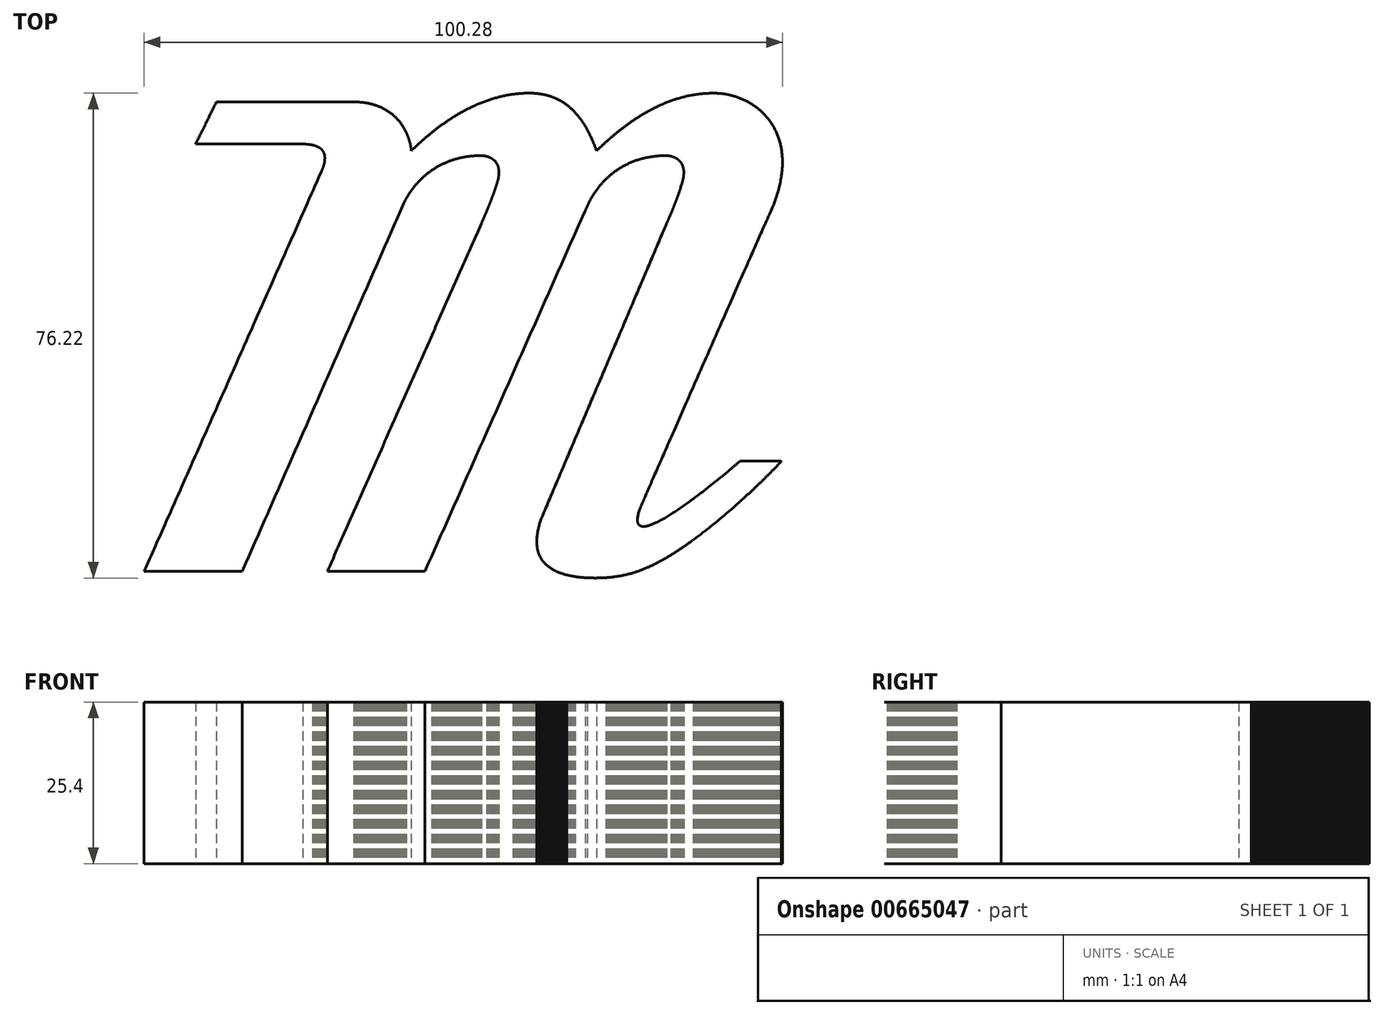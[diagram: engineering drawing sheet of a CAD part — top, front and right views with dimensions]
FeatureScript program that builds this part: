
annotation { "Feature Type Name" : "Feature", "Feature Type Description" : "" }
export const myFeature = defineFeature(function(context is Context, id is Id, definition is map)
    precondition{}
    {
        {
            var Q0;
            Q0=qCreatedBy(makeId("Top.planeOp"),FACE);
            var sketch = newSketch(context, id + "F0", { "sketchPlane" : qUnion([Q0])});
            skLineSegment(sketch, "E0", {"start": v(28.08, -26.44) * mm, "end": v(28.1, -26.39) * mm});
            skLineSegment(sketch, "E1", {"start": v(28.1, -26.39) * mm, "end": v(28.13, -26.32) * mm});
            skLineSegment(sketch, "E2", {"start": v(28.13, -26.32) * mm, "end": v(28.16, -26.25) * mm});
            skLineSegment(sketch, "E3", {"start": v(28.16, -26.25) * mm, "end": v(28.2, -26.16) * mm});
            skLineSegment(sketch, "E4", {"start": v(28.2, -26.16) * mm, "end": v(28.24, -26.05) * mm});
            skLineSegment(sketch, "E5", {"start": v(28.24, -26.05) * mm, "end": v(28.3, -25.94) * mm});
            skLineSegment(sketch, "E6", {"start": v(28.3, -25.94) * mm, "end": v(28.35, -25.81) * mm});
            skLineSegment(sketch, "E7", {"start": v(28.35, -25.81) * mm, "end": v(28.4, -25.68) * mm});
            skLineSegment(sketch, "E8", {"start": v(28.4, -25.68) * mm, "end": v(28.47, -25.53) * mm});
            skLineSegment(sketch, "E9", {"start": v(28.47, -25.53) * mm, "end": v(28.54, -25.37) * mm});
            skLineSegment(sketch, "E10", {"start": v(28.54, -25.37) * mm, "end": v(28.62, -25.2) * mm});
            skLineSegment(sketch, "E11", {"start": v(28.62, -25.2) * mm, "end": v(28.7, -25.02) * mm});
            skLineSegment(sketch, "E12", {"start": v(28.7, -25.02) * mm, "end": v(28.78, -24.82) * mm});
            skLineSegment(sketch, "E13", {"start": v(28.78, -24.82) * mm, "end": v(28.87, -24.62) * mm});
            skLineSegment(sketch, "E14", {"start": v(28.87, -24.62) * mm, "end": v(28.96, -24.4) * mm});
            skLineSegment(sketch, "E15", {"start": v(28.96, -24.4) * mm, "end": v(29.06, -24.19) * mm});
            skLineSegment(sketch, "E16", {"start": v(29.06, -24.19) * mm, "end": v(29.16, -23.95) * mm});
            skLineSegment(sketch, "E17", {"start": v(29.16, -23.95) * mm, "end": v(29.27, -23.71) * mm});
            skLineSegment(sketch, "E18", {"start": v(29.27, -23.71) * mm, "end": v(29.38, -23.46) * mm});
            skLineSegment(sketch, "E19", {"start": v(29.38, -23.46) * mm, "end": v(29.5, -23.2) * mm});
            skLineSegment(sketch, "E20", {"start": v(29.5, -23.2) * mm, "end": v(29.61, -22.93) * mm});
            skLineSegment(sketch, "E21", {"start": v(29.61, -22.93) * mm, "end": v(29.73, -22.65) * mm});
            skLineSegment(sketch, "E22", {"start": v(29.73, -22.65) * mm, "end": v(29.86, -22.36) * mm});
            skLineSegment(sketch, "E23", {"start": v(29.86, -22.36) * mm, "end": v(29.99, -22.07) * mm});
            skLineSegment(sketch, "E24", {"start": v(29.99, -22.07) * mm, "end": v(30.12, -21.76) * mm});
            skLineSegment(sketch, "E25", {"start": v(30.12, -21.76) * mm, "end": v(30.26, -21.45) * mm});
            skLineSegment(sketch, "E26", {"start": v(30.26, -21.45) * mm, "end": v(30.4, -21.13) * mm});
            skLineSegment(sketch, "E27", {"start": v(30.4, -21.13) * mm, "end": v(30.54, -20.8) * mm});
            skLineSegment(sketch, "E28", {"start": v(30.54, -20.8) * mm, "end": v(30.69, -20.47) * mm});
            skLineSegment(sketch, "E29", {"start": v(30.69, -20.47) * mm, "end": v(30.84, -20.12) * mm});
            skLineSegment(sketch, "E30", {"start": v(30.84, -20.12) * mm, "end": v(31, -19.77) * mm});
            skLineSegment(sketch, "E31", {"start": v(31, -19.77) * mm, "end": v(31.15, -19.42) * mm});
            skLineSegment(sketch, "E32", {"start": v(31.15, -19.42) * mm, "end": v(31.31, -19.05) * mm});
            skLineSegment(sketch, "E33", {"start": v(31.31, -19.05) * mm, "end": v(31.47, -18.68) * mm});
            skLineSegment(sketch, "E34", {"start": v(31.47, -18.68) * mm, "end": v(31.64, -18.3) * mm});
            skLineSegment(sketch, "E35", {"start": v(31.64, -18.3) * mm, "end": v(31.8, -17.92) * mm});
            skLineSegment(sketch, "E36", {"start": v(31.8, -17.92) * mm, "end": v(31.98, -17.53) * mm});
            skLineSegment(sketch, "E37", {"start": v(31.98, -17.53) * mm, "end": v(32.15, -17.13) * mm});
            skLineSegment(sketch, "E38", {"start": v(32.15, -17.13) * mm, "end": v(32.33, -16.73) * mm});
            skLineSegment(sketch, "E39", {"start": v(32.33, -16.73) * mm, "end": v(32.5, -16.33) * mm});
            skLineSegment(sketch, "E40", {"start": v(32.5, -16.33) * mm, "end": v(32.69, -15.91) * mm});
            skLineSegment(sketch, "E41", {"start": v(32.69, -15.91) * mm, "end": v(32.87, -15.5) * mm});
            skLineSegment(sketch, "E42", {"start": v(32.87, -15.5) * mm, "end": v(33.06, -15.07) * mm});
            skLineSegment(sketch, "E43", {"start": v(33.06, -15.07) * mm, "end": v(33.24, -14.65) * mm});
            skLineSegment(sketch, "E44", {"start": v(33.24, -14.65) * mm, "end": v(33.43, -14.21) * mm});
            skLineSegment(sketch, "E45", {"start": v(33.43, -14.21) * mm, "end": v(33.62, -13.78) * mm});
            skLineSegment(sketch, "E46", {"start": v(33.62, -13.78) * mm, "end": v(33.82, -13.34) * mm});
            skLineSegment(sketch, "E47", {"start": v(33.82, -13.34) * mm, "end": v(34.01, -12.9) * mm});
            skLineSegment(sketch, "E48", {"start": v(34.01, -12.9) * mm, "end": v(34.2, -12.44) * mm});
            skLineSegment(sketch, "E49", {"start": v(34.2, -12.44) * mm, "end": v(34.4, -12) * mm});
            skLineSegment(sketch, "E50", {"start": v(34.4, -12) * mm, "end": v(34.6, -11.54) * mm});
            skLineSegment(sketch, "E51", {"start": v(34.6, -11.54) * mm, "end": v(34.8, -11.08) * mm});
            skLineSegment(sketch, "E52", {"start": v(34.8, -11.08) * mm, "end": v(35.01, -10.62) * mm});
            skLineSegment(sketch, "E53", {"start": v(35.01, -10.62) * mm, "end": v(35.22, -10.15) * mm});
            skLineSegment(sketch, "E54", {"start": v(35.22, -10.15) * mm, "end": v(35.42, -9.68) * mm});
            skLineSegment(sketch, "E55", {"start": v(35.42, -9.68) * mm, "end": v(35.63, -9.21) * mm});
            skLineSegment(sketch, "E56", {"start": v(35.63, -9.21) * mm, "end": v(35.84, -8.74) * mm});
            skLineSegment(sketch, "E57", {"start": v(35.84, -8.74) * mm, "end": v(36.04, -8.27) * mm});
            skLineSegment(sketch, "E58", {"start": v(36.04, -8.27) * mm, "end": v(36.25, -7.79) * mm});
            skLineSegment(sketch, "E59", {"start": v(36.25, -7.79) * mm, "end": v(36.46, -7.31) * mm});
            skLineSegment(sketch, "E60", {"start": v(36.46, -7.31) * mm, "end": v(36.68, -6.83) * mm});
            skLineSegment(sketch, "E61", {"start": v(36.68, -6.83) * mm, "end": v(36.89, -6.35) * mm});
            skLineSegment(sketch, "E62", {"start": v(36.89, -6.35) * mm, "end": v(37.1, -5.87) * mm});
            skLineSegment(sketch, "E63", {"start": v(37.1, -5.87) * mm, "end": v(37.31, -5.38) * mm});
            skLineSegment(sketch, "E64", {"start": v(37.31, -5.38) * mm, "end": v(37.53, -4.9) * mm});
            skLineSegment(sketch, "E65", {"start": v(37.53, -4.9) * mm, "end": v(37.74, -4.41) * mm});
            skLineSegment(sketch, "E66", {"start": v(37.74, -4.41) * mm, "end": v(37.95, -3.93) * mm});
            skLineSegment(sketch, "E67", {"start": v(37.95, -3.93) * mm, "end": v(38.17, -3.44) * mm});
            skLineSegment(sketch, "E68", {"start": v(38.17, -3.44) * mm, "end": v(38.38, -2.95) * mm});
            skLineSegment(sketch, "E69", {"start": v(38.38, -2.95) * mm, "end": v(38.6, -2.47) * mm});
            skLineSegment(sketch, "E70", {"start": v(38.6, -2.47) * mm, "end": v(38.8, -1.98) * mm});
            skLineSegment(sketch, "E71", {"start": v(38.8, -1.98) * mm, "end": v(39.02, -1.5) * mm});
            skLineSegment(sketch, "E72", {"start": v(39.02, -1.5) * mm, "end": v(39.23, -1) * mm});
            skLineSegment(sketch, "E73", {"start": v(39.23, -1) * mm, "end": v(39.45, -0.52) * mm});
            skLineSegment(sketch, "E74", {"start": v(39.45, -0.52) * mm, "end": v(39.66, -0.04) * mm});
            skLineSegment(sketch, "E75", {"start": v(39.66, -0.04) * mm, "end": v(39.87, 0.44) * mm});
            skLineSegment(sketch, "E76", {"start": v(39.87, 0.44) * mm, "end": v(40.08, 0.92) * mm});
            skLineSegment(sketch, "E77", {"start": v(40.08, 0.92) * mm, "end": v(40.3, 1.4) * mm});
            skLineSegment(sketch, "E78", {"start": v(40.3, 1.4) * mm, "end": v(40.5, 1.88) * mm});
            skLineSegment(sketch, "E79", {"start": v(40.5, 1.88) * mm, "end": v(40.71, 2.35) * mm});
            skLineSegment(sketch, "E80", {"start": v(40.71, 2.35) * mm, "end": v(40.92, 2.83) * mm});
            skLineSegment(sketch, "E81", {"start": v(40.92, 2.83) * mm, "end": v(41.13, 3.3) * mm});
            skLineSegment(sketch, "E82", {"start": v(41.13, 3.3) * mm, "end": v(41.34, 3.77) * mm});
            skLineSegment(sketch, "E83", {"start": v(41.34, 3.77) * mm, "end": v(41.54, 4.23) * mm});
            skLineSegment(sketch, "E84", {"start": v(41.54, 4.23) * mm, "end": v(41.75, 4.7) * mm});
            skLineSegment(sketch, "E85", {"start": v(41.75, 4.7) * mm, "end": v(41.95, 5.16) * mm});
            skLineSegment(sketch, "E86", {"start": v(41.95, 5.16) * mm, "end": v(42.15, 5.61) * mm});
            skLineSegment(sketch, "E87", {"start": v(42.15, 5.61) * mm, "end": v(42.35, 6.07) * mm});
            skLineSegment(sketch, "E88", {"start": v(42.35, 6.07) * mm, "end": v(42.55, 6.52) * mm});
            skLineSegment(sketch, "E89", {"start": v(42.55, 6.52) * mm, "end": v(42.74, 6.96) * mm});
            skLineSegment(sketch, "E90", {"start": v(42.74, 6.96) * mm, "end": v(42.94, 7.4) * mm});
            skLineSegment(sketch, "E91", {"start": v(42.94, 7.4) * mm, "end": v(43.13, 7.84) * mm});
            skLineSegment(sketch, "E92", {"start": v(43.13, 7.84) * mm, "end": v(43.32, 8.28) * mm});
            skLineSegment(sketch, "E93", {"start": v(43.32, 8.28) * mm, "end": v(43.51, 8.7) * mm});
            skLineSegment(sketch, "E94", {"start": v(43.51, 8.7) * mm, "end": v(43.7, 9.13) * mm});
            skLineSegment(sketch, "E95", {"start": v(43.7, 9.13) * mm, "end": v(43.89, 9.55) * mm});
            skLineSegment(sketch, "E96", {"start": v(43.89, 9.55) * mm, "end": v(44.07, 9.96) * mm});
            skLineSegment(sketch, "E97", {"start": v(44.07, 9.96) * mm, "end": v(44.25, 10.37) * mm});
            skLineSegment(sketch, "E98", {"start": v(44.25, 10.37) * mm, "end": v(44.43, 10.77) * mm});
            skLineSegment(sketch, "E99", {"start": v(44.43, 10.77) * mm, "end": v(44.6, 11.17) * mm});
            skLineSegment(sketch, "E100", {"start": v(44.6, 11.17) * mm, "end": v(44.78, 11.56) * mm});
            skLineSegment(sketch, "E101", {"start": v(44.78, 11.56) * mm, "end": v(44.95, 11.95) * mm});
            skLineSegment(sketch, "E102", {"start": v(44.95, 11.95) * mm, "end": v(45.11, 12.33) * mm});
            skLineSegment(sketch, "E103", {"start": v(45.11, 12.33) * mm, "end": v(45.28, 12.7) * mm});
            skLineSegment(sketch, "E104", {"start": v(45.28, 12.7) * mm, "end": v(45.44, 13.07) * mm});
            skLineSegment(sketch, "E105", {"start": v(45.44, 13.07) * mm, "end": v(45.6, 13.43) * mm});
            skLineSegment(sketch, "E106", {"start": v(45.6, 13.43) * mm, "end": v(45.76, 13.78) * mm});
            skLineSegment(sketch, "E107", {"start": v(45.76, 13.78) * mm, "end": v(45.91, 14.13) * mm});
            skLineSegment(sketch, "E108", {"start": v(45.91, 14.13) * mm, "end": v(46.06, 14.47) * mm});
            skLineSegment(sketch, "E109", {"start": v(46.06, 14.47) * mm, "end": v(46.2, 14.8) * mm});
            skLineSegment(sketch, "E110", {"start": v(46.2, 14.8) * mm, "end": v(46.35, 15.12) * mm});
            skLineSegment(sketch, "E111", {"start": v(46.35, 15.12) * mm, "end": v(46.5, 15.44) * mm});
            skLineSegment(sketch, "E112", {"start": v(46.5, 15.44) * mm, "end": v(46.63, 15.74) * mm});
            skLineSegment(sketch, "E113", {"start": v(46.63, 15.74) * mm, "end": v(46.76, 16.04) * mm});
            skLineSegment(sketch, "E114", {"start": v(46.76, 16.04) * mm, "end": v(46.89, 16.33) * mm});
            skLineSegment(sketch, "E115", {"start": v(46.89, 16.33) * mm, "end": v(47.01, 16.62) * mm});
            skLineSegment(sketch, "E116", {"start": v(47.01, 16.62) * mm, "end": v(47.14, 16.89) * mm});
            skLineSegment(sketch, "E117", {"start": v(47.14, 16.89) * mm, "end": v(47.25, 17.15) * mm});
            skLineSegment(sketch, "E118", {"start": v(47.25, 17.15) * mm, "end": v(47.37, 17.4) * mm});
            skLineSegment(sketch, "E119", {"start": v(47.37, 17.4) * mm, "end": v(47.48, 17.65) * mm});
            skLineSegment(sketch, "E120", {"start": v(47.48, 17.65) * mm, "end": v(47.58, 17.89) * mm});
            skLineSegment(sketch, "E121", {"start": v(47.58, 17.89) * mm, "end": v(47.68, 18.12) * mm});
            skLineSegment(sketch, "E122", {"start": v(47.68, 18.12) * mm, "end": v(47.78, 18.33) * mm});
            skLineSegment(sketch, "E123", {"start": v(47.78, 18.33) * mm, "end": v(47.87, 18.54) * mm});
            skLineSegment(sketch, "E124", {"start": v(47.87, 18.54) * mm, "end": v(47.96, 18.73) * mm});
            skLineSegment(sketch, "E125", {"start": v(47.96, 18.73) * mm, "end": v(48.04, 18.92) * mm});
            skLineSegment(sketch, "E126", {"start": v(48.04, 18.92) * mm, "end": v(48.12, 19.1) * mm});
            skLineSegment(sketch, "E127", {"start": v(48.12, 19.1) * mm, "end": v(48.2, 19.26) * mm});
            skLineSegment(sketch, "E128", {"start": v(48.2, 19.26) * mm, "end": v(48.33, 19.55) * mm});
            skLineSegment(sketch, "E129", {"start": v(48.33, 19.55) * mm, "end": v(48.45, 19.84) * mm});
            skLineSegment(sketch, "E130", {"start": v(48.45, 19.84) * mm, "end": v(48.57, 20.12) * mm});
            skLineSegment(sketch, "E131", {"start": v(48.57, 20.12) * mm, "end": v(48.68, 20.4) * mm});
            skLineSegment(sketch, "E132", {"start": v(48.68, 20.4) * mm, "end": v(48.8, 20.69) * mm});
            skLineSegment(sketch, "E133", {"start": v(48.8, 20.69) * mm, "end": v(48.9, 20.97) * mm});
            skLineSegment(sketch, "E134", {"start": v(48.9, 20.97) * mm, "end": v(49, 21.24) * mm});
            skLineSegment(sketch, "E135", {"start": v(49, 21.24) * mm, "end": v(49.1, 21.52) * mm});
            skLineSegment(sketch, "E136", {"start": v(49.1, 21.52) * mm, "end": v(49.2, 21.8) * mm});
            skLineSegment(sketch, "E137", {"start": v(49.2, 21.8) * mm, "end": v(49.28, 22.06) * mm});
            skLineSegment(sketch, "E138", {"start": v(49.28, 22.06) * mm, "end": v(49.36, 22.33) * mm});
            skLineSegment(sketch, "E139", {"start": v(49.36, 22.33) * mm, "end": v(49.44, 22.6) * mm});
            skLineSegment(sketch, "E140", {"start": v(49.44, 22.6) * mm, "end": v(49.51, 22.86) * mm});
            skLineSegment(sketch, "E141", {"start": v(49.51, 22.86) * mm, "end": v(49.58, 23.12) * mm});
            skLineSegment(sketch, "E142", {"start": v(49.58, 23.12) * mm, "end": v(49.65, 23.38) * mm});
            skLineSegment(sketch, "E143", {"start": v(49.65, 23.38) * mm, "end": v(49.7, 23.64) * mm});
            skLineSegment(sketch, "E144", {"start": v(49.7, 23.64) * mm, "end": v(49.77, 23.9) * mm});
            skLineSegment(sketch, "E145", {"start": v(49.77, 23.9) * mm, "end": v(49.82, 24.15) * mm});
            skLineSegment(sketch, "E146", {"start": v(49.82, 24.15) * mm, "end": v(49.87, 24.4) * mm});
            skLineSegment(sketch, "E147", {"start": v(49.87, 24.4) * mm, "end": v(49.91, 24.65) * mm});
            skLineSegment(sketch, "E148", {"start": v(49.91, 24.65) * mm, "end": v(49.95, 24.9) * mm});
            skLineSegment(sketch, "E149", {"start": v(49.95, 24.9) * mm, "end": v(49.99, 25.14) * mm});
            skLineSegment(sketch, "E150", {"start": v(49.99, 25.14) * mm, "end": v(50.02, 25.38) * mm});
            skLineSegment(sketch, "E151", {"start": v(50.02, 25.38) * mm, "end": v(50.05, 25.62) * mm});
            skLineSegment(sketch, "E152", {"start": v(50.05, 25.62) * mm, "end": v(50.08, 25.86) * mm});
            skLineSegment(sketch, "E153", {"start": v(50.08, 25.86) * mm, "end": v(50.1, 26.1) * mm});
            skLineSegment(sketch, "E154", {"start": v(50.1, 26.1) * mm, "end": v(50.11, 26.32) * mm});
            skLineSegment(sketch, "E155", {"start": v(50.11, 26.32) * mm, "end": v(50.13, 26.55) * mm});
            skLineSegment(sketch, "E156", {"start": v(50.13, 26.55) * mm, "end": v(50.14, 26.78) * mm});
            skLineSegment(sketch, "E157", {"start": v(50.14, 26.78) * mm, "end": v(50.14, 27) * mm});
            skLineSegment(sketch, "E158", {"start": v(50.14, 27) * mm, "end": v(50.14, 27.23) * mm});
            skLineSegment(sketch, "E159", {"start": v(50.14, 27.23) * mm, "end": v(50.14, 27.45) * mm});
            skLineSegment(sketch, "E160", {"start": v(50.14, 27.45) * mm, "end": v(50.14, 27.67) * mm});
            skLineSegment(sketch, "E161", {"start": v(50.14, 27.67) * mm, "end": v(50.13, 27.9) * mm});
            skLineSegment(sketch, "E162", {"start": v(50.13, 27.9) * mm, "end": v(50.12, 28.1) * mm});
            skLineSegment(sketch, "E163", {"start": v(50.12, 28.1) * mm, "end": v(50.1, 28.32) * mm});
            skLineSegment(sketch, "E164", {"start": v(50.1, 28.32) * mm, "end": v(50.08, 28.53) * mm});
            skLineSegment(sketch, "E165", {"start": v(50.08, 28.53) * mm, "end": v(50.06, 28.74) * mm});
            skLineSegment(sketch, "E166", {"start": v(50.06, 28.74) * mm, "end": v(50.03, 28.94) * mm});
            skLineSegment(sketch, "E167", {"start": v(50.03, 28.94) * mm, "end": v(50, 29.15) * mm});
            skLineSegment(sketch, "E168", {"start": v(50, 29.15) * mm, "end": v(49.97, 29.35) * mm});
            skLineSegment(sketch, "E169", {"start": v(49.97, 29.35) * mm, "end": v(49.94, 29.55) * mm});
            skLineSegment(sketch, "E170", {"start": v(49.94, 29.55) * mm, "end": v(49.9, 29.74) * mm});
            skLineSegment(sketch, "E171", {"start": v(49.9, 29.74) * mm, "end": v(49.86, 29.94) * mm});
            skLineSegment(sketch, "E172", {"start": v(49.86, 29.94) * mm, "end": v(49.81, 30.13) * mm});
            skLineSegment(sketch, "E173", {"start": v(49.81, 30.13) * mm, "end": v(49.76, 30.32) * mm});
            skLineSegment(sketch, "E174", {"start": v(49.76, 30.32) * mm, "end": v(49.71, 30.5) * mm});
            skLineSegment(sketch, "E175", {"start": v(49.71, 30.5) * mm, "end": v(49.66, 30.7) * mm});
            skLineSegment(sketch, "E176", {"start": v(49.66, 30.7) * mm, "end": v(49.6, 30.88) * mm});
            skLineSegment(sketch, "E177", {"start": v(49.6, 30.88) * mm, "end": v(49.54, 31.06) * mm});
            skLineSegment(sketch, "E178", {"start": v(49.54, 31.06) * mm, "end": v(49.48, 31.23) * mm});
            skLineSegment(sketch, "E179", {"start": v(49.48, 31.23) * mm, "end": v(49.41, 31.41) * mm});
            skLineSegment(sketch, "E180", {"start": v(49.41, 31.41) * mm, "end": v(49.35, 31.59) * mm});
            skLineSegment(sketch, "E181", {"start": v(49.35, 31.59) * mm, "end": v(49.27, 31.76) * mm});
            skLineSegment(sketch, "E182", {"start": v(49.27, 31.76) * mm, "end": v(49.2, 31.93) * mm});
            skLineSegment(sketch, "E183", {"start": v(49.2, 31.93) * mm, "end": v(49.12, 32.1) * mm});
            skLineSegment(sketch, "E184", {"start": v(49.12, 32.1) * mm, "end": v(49.05, 32.26) * mm});
            skLineSegment(sketch, "E185", {"start": v(49.05, 32.26) * mm, "end": v(48.96, 32.42) * mm});
            skLineSegment(sketch, "E186", {"start": v(48.96, 32.42) * mm, "end": v(48.88, 32.58) * mm});
            skLineSegment(sketch, "E187", {"start": v(48.88, 32.58) * mm, "end": v(48.8, 32.74) * mm});
            skLineSegment(sketch, "E188", {"start": v(48.8, 32.74) * mm, "end": v(48.7, 32.9) * mm});
            skLineSegment(sketch, "E189", {"start": v(48.7, 32.9) * mm, "end": v(48.61, 33.05) * mm});
            skLineSegment(sketch, "E190", {"start": v(48.61, 33.05) * mm, "end": v(48.52, 33.2) * mm});
            skLineSegment(sketch, "E191", {"start": v(48.52, 33.2) * mm, "end": v(48.42, 33.35) * mm});
            skLineSegment(sketch, "E192", {"start": v(48.42, 33.35) * mm, "end": v(48.33, 33.5) * mm});
            skLineSegment(sketch, "E193", {"start": v(48.33, 33.5) * mm, "end": v(48.23, 33.64) * mm});
            skLineSegment(sketch, "E194", {"start": v(48.23, 33.64) * mm, "end": v(48.12, 33.78) * mm});
            skLineSegment(sketch, "E195", {"start": v(48.12, 33.78) * mm, "end": v(48.02, 33.92) * mm});
            skLineSegment(sketch, "E196", {"start": v(48.02, 33.92) * mm, "end": v(47.91, 34.06) * mm});
            skLineSegment(sketch, "E197", {"start": v(47.91, 34.06) * mm, "end": v(47.8, 34.2) * mm});
            skLineSegment(sketch, "E198", {"start": v(47.8, 34.2) * mm, "end": v(47.7, 34.33) * mm});
            skLineSegment(sketch, "E199", {"start": v(47.7, 34.33) * mm, "end": v(47.58, 34.46) * mm});
            skLineSegment(sketch, "E200", {"start": v(47.58, 34.46) * mm, "end": v(47.46, 34.6) * mm});
            skLineSegment(sketch, "E201", {"start": v(47.46, 34.6) * mm, "end": v(47.35, 34.72) * mm});
            skLineSegment(sketch, "E202", {"start": v(47.35, 34.72) * mm, "end": v(47.23, 34.84) * mm});
            skLineSegment(sketch, "E203", {"start": v(47.23, 34.84) * mm, "end": v(47.1, 34.96) * mm});
            skLineSegment(sketch, "E204", {"start": v(47.1, 34.96) * mm, "end": v(46.98, 35.08) * mm});
            skLineSegment(sketch, "E205", {"start": v(46.98, 35.08) * mm, "end": v(46.86, 35.2) * mm});
            skLineSegment(sketch, "E206", {"start": v(46.86, 35.2) * mm, "end": v(46.73, 35.31) * mm});
            skLineSegment(sketch, "E207", {"start": v(46.73, 35.31) * mm, "end": v(46.6, 35.43) * mm});
            skLineSegment(sketch, "E208", {"start": v(46.6, 35.43) * mm, "end": v(46.48, 35.54) * mm});
            skLineSegment(sketch, "E209", {"start": v(46.48, 35.54) * mm, "end": v(46.35, 35.64) * mm});
            skLineSegment(sketch, "E210", {"start": v(46.35, 35.64) * mm, "end": v(46.21, 35.75) * mm});
            skLineSegment(sketch, "E211", {"start": v(46.21, 35.75) * mm, "end": v(46.08, 35.85) * mm});
            skLineSegment(sketch, "E212", {"start": v(46.08, 35.85) * mm, "end": v(45.95, 35.95) * mm});
            skLineSegment(sketch, "E213", {"start": v(45.95, 35.95) * mm, "end": v(45.8, 36.05) * mm});
            skLineSegment(sketch, "E214", {"start": v(45.8, 36.05) * mm, "end": v(45.67, 36.15) * mm});
            skLineSegment(sketch, "E215", {"start": v(45.67, 36.15) * mm, "end": v(45.53, 36.24) * mm});
            skLineSegment(sketch, "E216", {"start": v(45.53, 36.24) * mm, "end": v(45.4, 36.34) * mm});
            skLineSegment(sketch, "E217", {"start": v(45.4, 36.34) * mm, "end": v(45.25, 36.43) * mm});
            skLineSegment(sketch, "E218", {"start": v(45.25, 36.43) * mm, "end": v(45.1, 36.51) * mm});
            skLineSegment(sketch, "E219", {"start": v(45.1, 36.51) * mm, "end": v(44.96, 36.6) * mm});
            skLineSegment(sketch, "E220", {"start": v(44.96, 36.6) * mm, "end": v(44.82, 36.68) * mm});
            skLineSegment(sketch, "E221", {"start": v(44.82, 36.68) * mm, "end": v(44.67, 36.76) * mm});
            skLineSegment(sketch, "E222", {"start": v(44.67, 36.76) * mm, "end": v(44.52, 36.84) * mm});
            skLineSegment(sketch, "E223", {"start": v(44.52, 36.84) * mm, "end": v(44.37, 36.91) * mm});
            skLineSegment(sketch, "E224", {"start": v(44.37, 36.91) * mm, "end": v(44.22, 36.99) * mm});
            skLineSegment(sketch, "E225", {"start": v(44.22, 36.99) * mm, "end": v(44.07, 37.06) * mm});
            skLineSegment(sketch, "E226", {"start": v(44.07, 37.06) * mm, "end": v(43.92, 37.13) * mm});
            skLineSegment(sketch, "E227", {"start": v(43.92, 37.13) * mm, "end": v(43.77, 37.2) * mm});
            skLineSegment(sketch, "E228", {"start": v(43.77, 37.2) * mm, "end": v(43.62, 37.26) * mm});
            skLineSegment(sketch, "E229", {"start": v(43.62, 37.26) * mm, "end": v(43.46, 37.32) * mm});
            skLineSegment(sketch, "E230", {"start": v(43.46, 37.32) * mm, "end": v(43.3, 37.38) * mm});
            skLineSegment(sketch, "E231", {"start": v(43.3, 37.38) * mm, "end": v(43.15, 37.44) * mm});
            skLineSegment(sketch, "E232", {"start": v(43.15, 37.44) * mm, "end": v(43, 37.5) * mm});
            skLineSegment(sketch, "E233", {"start": v(43, 37.5) * mm, "end": v(42.84, 37.54) * mm});
            skLineSegment(sketch, "E234", {"start": v(42.84, 37.54) * mm, "end": v(42.68, 37.6) * mm});
            skLineSegment(sketch, "E235", {"start": v(42.68, 37.6) * mm, "end": v(42.52, 37.64) * mm});
            skLineSegment(sketch, "E236", {"start": v(42.52, 37.64) * mm, "end": v(42.37, 37.69) * mm});
            skLineSegment(sketch, "E237", {"start": v(42.37, 37.69) * mm, "end": v(42.2, 37.73) * mm});
            skLineSegment(sketch, "E238", {"start": v(42.2, 37.73) * mm, "end": v(42.05, 37.77) * mm});
            skLineSegment(sketch, "E239", {"start": v(42.05, 37.77) * mm, "end": v(41.89, 37.8) * mm});
            skLineSegment(sketch, "E240", {"start": v(41.89, 37.8) * mm, "end": v(41.73, 37.85) * mm});
            skLineSegment(sketch, "E241", {"start": v(41.73, 37.85) * mm, "end": v(41.57, 37.88) * mm});
            skLineSegment(sketch, "E242", {"start": v(41.57, 37.88) * mm, "end": v(41.4, 37.91) * mm});
            skLineSegment(sketch, "E243", {"start": v(41.4, 37.91) * mm, "end": v(41.25, 37.94) * mm});
            skLineSegment(sketch, "E244", {"start": v(41.25, 37.94) * mm, "end": v(41.09, 37.97) * mm});
            skLineSegment(sketch, "E245", {"start": v(41.09, 37.97) * mm, "end": v(40.93, 38) * mm});
            skLineSegment(sketch, "E246", {"start": v(40.93, 38) * mm, "end": v(40.76, 38.01) * mm});
            skLineSegment(sketch, "E247", {"start": v(40.76, 38.01) * mm, "end": v(40.6, 38.03) * mm});
            skLineSegment(sketch, "E248", {"start": v(40.6, 38.03) * mm, "end": v(40.44, 38.05) * mm});
            skLineSegment(sketch, "E249", {"start": v(40.44, 38.05) * mm, "end": v(40.28, 38.07) * mm});
            skLineSegment(sketch, "E250", {"start": v(40.28, 38.07) * mm, "end": v(40.12, 38.08) * mm});
            skLineSegment(sketch, "E251", {"start": v(40.12, 38.08) * mm, "end": v(39.96, 38.1) * mm});
            skLineSegment(sketch, "E252", {"start": v(39.96, 38.1) * mm, "end": v(39.8, 38.1) * mm});
            skLineSegment(sketch, "E253", {"start": v(39.8, 38.1) * mm, "end": v(39.64, 38.1) * mm});
            skLineSegment(sketch, "E254", {"start": v(39.64, 38.1) * mm, "end": v(39.48, 38.1) * mm});
            skLineSegment(sketch, "E255", {"start": v(39.48, 38.1) * mm, "end": v(39.32, 38.1) * mm});
            skLineSegment(sketch, "E256", {"start": v(39.32, 38.1) * mm, "end": v(39.11, 38.1) * mm});
            skLineSegment(sketch, "E257", {"start": v(39.11, 38.1) * mm, "end": v(38.91, 38.1) * mm});
            skLineSegment(sketch, "E258", {"start": v(38.91, 38.1) * mm, "end": v(38.7, 38.1) * mm});
            skLineSegment(sketch, "E259", {"start": v(38.7, 38.1) * mm, "end": v(38.5, 38.1) * mm});
            skLineSegment(sketch, "E260", {"start": v(38.5, 38.1) * mm, "end": v(38.3, 38.08) * mm});
            skLineSegment(sketch, "E261", {"start": v(38.3, 38.08) * mm, "end": v(38.1, 38.07) * mm});
            skLineSegment(sketch, "E262", {"start": v(38.1, 38.07) * mm, "end": v(37.9, 38.05) * mm});
            skLineSegment(sketch, "E263", {"start": v(37.9, 38.05) * mm, "end": v(37.7, 38.04) * mm});
            skLineSegment(sketch, "E264", {"start": v(37.7, 38.04) * mm, "end": v(37.5, 38.02) * mm});
            skLineSegment(sketch, "E265", {"start": v(37.5, 38.02) * mm, "end": v(37.31, 38) * mm});
            skLineSegment(sketch, "E266", {"start": v(37.31, 38) * mm, "end": v(37.12, 37.98) * mm});
            skLineSegment(sketch, "E267", {"start": v(37.12, 37.98) * mm, "end": v(36.92, 37.95) * mm});
            skLineSegment(sketch, "E268", {"start": v(36.92, 37.95) * mm, "end": v(36.73, 37.93) * mm});
            skLineSegment(sketch, "E269", {"start": v(36.73, 37.93) * mm, "end": v(36.53, 37.9) * mm});
            skLineSegment(sketch, "E270", {"start": v(36.53, 37.9) * mm, "end": v(36.34, 37.87) * mm});
            skLineSegment(sketch, "E271", {"start": v(36.34, 37.87) * mm, "end": v(36.15, 37.84) * mm});
            skLineSegment(sketch, "E272", {"start": v(36.15, 37.84) * mm, "end": v(35.96, 37.8) * mm});
            skLineSegment(sketch, "E273", {"start": v(35.96, 37.8) * mm, "end": v(35.76, 37.77) * mm});
            skLineSegment(sketch, "E274", {"start": v(35.76, 37.77) * mm, "end": v(35.58, 37.73) * mm});
            skLineSegment(sketch, "E275", {"start": v(35.58, 37.73) * mm, "end": v(35.39, 37.69) * mm});
            skLineSegment(sketch, "E276", {"start": v(35.39, 37.69) * mm, "end": v(35.2, 37.65) * mm});
            skLineSegment(sketch, "E277", {"start": v(35.2, 37.65) * mm, "end": v(35.01, 37.6) * mm});
            skLineSegment(sketch, "E278", {"start": v(35.01, 37.6) * mm, "end": v(34.82, 37.56) * mm});
            skLineSegment(sketch, "E279", {"start": v(34.82, 37.56) * mm, "end": v(34.64, 37.52) * mm});
            skLineSegment(sketch, "E280", {"start": v(34.64, 37.52) * mm, "end": v(34.45, 37.47) * mm});
            skLineSegment(sketch, "E281", {"start": v(34.45, 37.47) * mm, "end": v(34.27, 37.42) * mm});
            skLineSegment(sketch, "E282", {"start": v(34.27, 37.42) * mm, "end": v(34.09, 37.37) * mm});
            skLineSegment(sketch, "E283", {"start": v(34.09, 37.37) * mm, "end": v(33.9, 37.32) * mm});
            skLineSegment(sketch, "E284", {"start": v(33.9, 37.32) * mm, "end": v(33.73, 37.26) * mm});
            skLineSegment(sketch, "E285", {"start": v(33.73, 37.26) * mm, "end": v(33.54, 37.2) * mm});
            skLineSegment(sketch, "E286", {"start": v(33.54, 37.2) * mm, "end": v(33.37, 37.15) * mm});
            skLineSegment(sketch, "E287", {"start": v(33.37, 37.15) * mm, "end": v(33.19, 37.1) * mm});
            skLineSegment(sketch, "E288", {"start": v(33.19, 37.1) * mm, "end": v(33, 37.03) * mm});
            skLineSegment(sketch, "E289", {"start": v(33, 37.03) * mm, "end": v(32.83, 36.97) * mm});
            skLineSegment(sketch, "E290", {"start": v(32.83, 36.97) * mm, "end": v(32.66, 36.9) * mm});
            skLineSegment(sketch, "E291", {"start": v(32.66, 36.9) * mm, "end": v(32.48, 36.84) * mm});
            skLineSegment(sketch, "E292", {"start": v(32.48, 36.84) * mm, "end": v(32.3, 36.78) * mm});
            skLineSegment(sketch, "E293", {"start": v(32.3, 36.78) * mm, "end": v(32.14, 36.71) * mm});
            skLineSegment(sketch, "E294", {"start": v(32.14, 36.71) * mm, "end": v(31.96, 36.65) * mm});
            skLineSegment(sketch, "E295", {"start": v(31.96, 36.65) * mm, "end": v(31.8, 36.58) * mm});
            skLineSegment(sketch, "E296", {"start": v(31.8, 36.58) * mm, "end": v(31.62, 36.5) * mm});
            skLineSegment(sketch, "E297", {"start": v(31.62, 36.5) * mm, "end": v(31.45, 36.44) * mm});
            skLineSegment(sketch, "E298", {"start": v(31.45, 36.44) * mm, "end": v(31.28, 36.36) * mm});
            skLineSegment(sketch, "E299", {"start": v(31.28, 36.36) * mm, "end": v(31.12, 36.3) * mm});
            skLineSegment(sketch, "E300", {"start": v(31.12, 36.3) * mm, "end": v(30.95, 36.22) * mm});
            skLineSegment(sketch, "E301", {"start": v(30.95, 36.22) * mm, "end": v(30.79, 36.14) * mm});
            skLineSegment(sketch, "E302", {"start": v(30.79, 36.14) * mm, "end": v(30.62, 36.07) * mm});
            skLineSegment(sketch, "E303", {"start": v(30.62, 36.07) * mm, "end": v(30.46, 35.99) * mm});
            skLineSegment(sketch, "E304", {"start": v(30.46, 35.99) * mm, "end": v(30.3, 35.91) * mm});
            skLineSegment(sketch, "E305", {"start": v(30.3, 35.91) * mm, "end": v(30.13, 35.83) * mm});
            skLineSegment(sketch, "E306", {"start": v(30.13, 35.83) * mm, "end": v(29.97, 35.75) * mm});
            skLineSegment(sketch, "E307", {"start": v(29.97, 35.75) * mm, "end": v(29.81, 35.67) * mm});
            skLineSegment(sketch, "E308", {"start": v(29.81, 35.67) * mm, "end": v(29.66, 35.59) * mm});
            skLineSegment(sketch, "E309", {"start": v(29.66, 35.59) * mm, "end": v(29.5, 35.5) * mm});
            skLineSegment(sketch, "E310", {"start": v(29.5, 35.5) * mm, "end": v(29.34, 35.42) * mm});
            skLineSegment(sketch, "E311", {"start": v(29.34, 35.42) * mm, "end": v(29.19, 35.34) * mm});
            skLineSegment(sketch, "E312", {"start": v(29.19, 35.34) * mm, "end": v(29.03, 35.25) * mm});
            skLineSegment(sketch, "E313", {"start": v(29.03, 35.25) * mm, "end": v(28.88, 35.17) * mm});
            skLineSegment(sketch, "E314", {"start": v(28.88, 35.17) * mm, "end": v(28.73, 35.08) * mm});
            skLineSegment(sketch, "E315", {"start": v(28.73, 35.08) * mm, "end": v(28.57, 35) * mm});
            skLineSegment(sketch, "E316", {"start": v(28.57, 35) * mm, "end": v(28.42, 34.9) * mm});
            skLineSegment(sketch, "E317", {"start": v(28.42, 34.9) * mm, "end": v(28.27, 34.82) * mm});
            skLineSegment(sketch, "E318", {"start": v(28.27, 34.82) * mm, "end": v(28.13, 34.73) * mm});
            skLineSegment(sketch, "E319", {"start": v(28.13, 34.73) * mm, "end": v(27.98, 34.64) * mm});
            skLineSegment(sketch, "E320", {"start": v(27.98, 34.64) * mm, "end": v(27.83, 34.55) * mm});
            skLineSegment(sketch, "E321", {"start": v(27.83, 34.55) * mm, "end": v(27.69, 34.46) * mm});
            skLineSegment(sketch, "E322", {"start": v(27.69, 34.46) * mm, "end": v(27.54, 34.37) * mm});
            skLineSegment(sketch, "E323", {"start": v(27.54, 34.37) * mm, "end": v(27.4, 34.28) * mm});
            skLineSegment(sketch, "E324", {"start": v(27.4, 34.28) * mm, "end": v(27.26, 34.19) * mm});
            skLineSegment(sketch, "E325", {"start": v(27.26, 34.19) * mm, "end": v(27.12, 34.1) * mm});
            skLineSegment(sketch, "E326", {"start": v(27.12, 34.1) * mm, "end": v(26.98, 34) * mm});
            skLineSegment(sketch, "E327", {"start": v(26.98, 34) * mm, "end": v(26.84, 33.9) * mm});
            skLineSegment(sketch, "E328", {"start": v(26.84, 33.9) * mm, "end": v(26.7, 33.82) * mm});
            skLineSegment(sketch, "E329", {"start": v(26.7, 33.82) * mm, "end": v(26.56, 33.72) * mm});
            skLineSegment(sketch, "E330", {"start": v(26.56, 33.72) * mm, "end": v(26.43, 33.63) * mm});
            skLineSegment(sketch, "E331", {"start": v(26.43, 33.63) * mm, "end": v(26.3, 33.54) * mm});
            skLineSegment(sketch, "E332", {"start": v(26.3, 33.54) * mm, "end": v(26.16, 33.44) * mm});
            skLineSegment(sketch, "E333", {"start": v(26.16, 33.44) * mm, "end": v(26.03, 33.35) * mm});
            skLineSegment(sketch, "E334", {"start": v(26.03, 33.35) * mm, "end": v(25.9, 33.25) * mm});
            skLineSegment(sketch, "E335", {"start": v(25.9, 33.25) * mm, "end": v(25.77, 33.16) * mm});
            skLineSegment(sketch, "E336", {"start": v(25.77, 33.16) * mm, "end": v(25.64, 33.06) * mm});
            skLineSegment(sketch, "E337", {"start": v(25.64, 33.06) * mm, "end": v(25.5, 32.97) * mm});
            skLineSegment(sketch, "E338", {"start": v(25.5, 32.97) * mm, "end": v(25.38, 32.88) * mm});
            skLineSegment(sketch, "E339", {"start": v(25.38, 32.88) * mm, "end": v(25.26, 32.78) * mm});
            skLineSegment(sketch, "E340", {"start": v(25.26, 32.78) * mm, "end": v(25.13, 32.69) * mm});
            skLineSegment(sketch, "E341", {"start": v(25.13, 32.69) * mm, "end": v(25, 32.6) * mm});
            skLineSegment(sketch, "E342", {"start": v(25, 32.6) * mm, "end": v(24.89, 32.5) * mm});
            skLineSegment(sketch, "E343", {"start": v(24.89, 32.5) * mm, "end": v(24.77, 32.4) * mm});
            skLineSegment(sketch, "E344", {"start": v(24.77, 32.4) * mm, "end": v(24.65, 32.31) * mm});
            skLineSegment(sketch, "E345", {"start": v(24.65, 32.31) * mm, "end": v(24.53, 32.22) * mm});
            skLineSegment(sketch, "E346", {"start": v(24.53, 32.22) * mm, "end": v(24.41, 32.12) * mm});
            skLineSegment(sketch, "E347", {"start": v(24.41, 32.12) * mm, "end": v(24.3, 32.03) * mm});
            skLineSegment(sketch, "E348", {"start": v(24.3, 32.03) * mm, "end": v(24.18, 31.94) * mm});
            skLineSegment(sketch, "E349", {"start": v(24.18, 31.94) * mm, "end": v(24.07, 31.84) * mm});
            skLineSegment(sketch, "E350", {"start": v(24.07, 31.84) * mm, "end": v(23.95, 31.75) * mm});
            skLineSegment(sketch, "E351", {"start": v(23.95, 31.75) * mm, "end": v(23.84, 31.66) * mm});
            skLineSegment(sketch, "E352", {"start": v(23.84, 31.66) * mm, "end": v(23.73, 31.57) * mm});
            skLineSegment(sketch, "E353", {"start": v(23.73, 31.57) * mm, "end": v(23.62, 31.48) * mm});
            skLineSegment(sketch, "E354", {"start": v(23.62, 31.48) * mm, "end": v(23.51, 31.38) * mm});
            skLineSegment(sketch, "E355", {"start": v(23.51, 31.38) * mm, "end": v(23.4, 31.3) * mm});
            skLineSegment(sketch, "E356", {"start": v(23.4, 31.3) * mm, "end": v(23.3, 31.2) * mm});
            skLineSegment(sketch, "E357", {"start": v(23.3, 31.2) * mm, "end": v(23.2, 31.11) * mm});
            skLineSegment(sketch, "E358", {"start": v(23.2, 31.11) * mm, "end": v(23.1, 31.02) * mm});
            skLineSegment(sketch, "E359", {"start": v(23.1, 31.02) * mm, "end": v(23, 30.94) * mm});
            skLineSegment(sketch, "E360", {"start": v(23, 30.94) * mm, "end": v(22.9, 30.85) * mm});
            skLineSegment(sketch, "E361", {"start": v(22.9, 30.85) * mm, "end": v(22.8, 30.76) * mm});
            skLineSegment(sketch, "E362", {"start": v(22.8, 30.76) * mm, "end": v(22.7, 30.67) * mm});
            skLineSegment(sketch, "E363", {"start": v(22.7, 30.67) * mm, "end": v(22.6, 30.59) * mm});
            skLineSegment(sketch, "E364", {"start": v(22.6, 30.59) * mm, "end": v(22.5, 30.5) * mm});
            skLineSegment(sketch, "E365", {"start": v(22.5, 30.5) * mm, "end": v(22.4, 30.42) * mm});
            skLineSegment(sketch, "E366", {"start": v(22.4, 30.42) * mm, "end": v(22.31, 30.33) * mm});
            skLineSegment(sketch, "E367", {"start": v(22.31, 30.33) * mm, "end": v(22.22, 30.25) * mm});
            skLineSegment(sketch, "E368", {"start": v(22.22, 30.25) * mm, "end": v(22.13, 30.17) * mm});
            skLineSegment(sketch, "E369", {"start": v(22.13, 30.17) * mm, "end": v(22.04, 30.09) * mm});
            skLineSegment(sketch, "E370", {"start": v(22.04, 30.09) * mm, "end": v(21.96, 30) * mm});
            skLineSegment(sketch, "E371", {"start": v(21.96, 30) * mm, "end": v(21.87, 29.93) * mm});
            skLineSegment(sketch, "E372", {"start": v(21.87, 29.93) * mm, "end": v(21.78, 29.85) * mm});
            skLineSegment(sketch, "E373", {"start": v(21.78, 29.85) * mm, "end": v(21.7, 29.77) * mm});
            skLineSegment(sketch, "E374", {"start": v(21.7, 29.77) * mm, "end": v(21.62, 29.7) * mm});
            skLineSegment(sketch, "E375", {"start": v(21.62, 29.7) * mm, "end": v(21.53, 29.62) * mm});
            skLineSegment(sketch, "E376", {"start": v(21.53, 29.62) * mm, "end": v(21.45, 29.54) * mm});
            skLineSegment(sketch, "E377", {"start": v(21.45, 29.54) * mm, "end": v(21.37, 29.47) * mm});
            skLineSegment(sketch, "E378", {"start": v(21.37, 29.47) * mm, "end": v(21.3, 29.4) * mm});
            skLineSegment(sketch, "E379", {"start": v(21.3, 29.4) * mm, "end": v(21.22, 29.32) * mm});
            skLineSegment(sketch, "E380", {"start": v(21.22, 29.32) * mm, "end": v(21.15, 29.25) * mm});
            skLineSegment(sketch, "E381", {"start": v(21.15, 29.25) * mm, "end": v(21.07, 29.19) * mm});
            skLineSegment(sketch, "E382", {"start": v(21.07, 29.19) * mm, "end": v(21, 29.12) * mm});
            skLineSegment(sketch, "E383", {"start": v(21, 29.12) * mm, "end": v(20.93, 29.05) * mm});
            skLineSegment(sketch, "E384", {"start": v(20.93, 29.05) * mm, "end": v(20.88, 29.17) * mm});
            skLineSegment(sketch, "E385", {"start": v(20.88, 29.17) * mm, "end": v(20.84, 29.3) * mm});
            skLineSegment(sketch, "E386", {"start": v(20.84, 29.3) * mm, "end": v(20.8, 29.42) * mm});
            skLineSegment(sketch, "E387", {"start": v(20.8, 29.42) * mm, "end": v(20.75, 29.55) * mm});
            skLineSegment(sketch, "E388", {"start": v(20.75, 29.55) * mm, "end": v(20.7, 29.67) * mm});
            skLineSegment(sketch, "E389", {"start": v(20.7, 29.67) * mm, "end": v(20.65, 29.79) * mm});
            skLineSegment(sketch, "E390", {"start": v(20.65, 29.79) * mm, "end": v(20.6, 29.91) * mm});
            skLineSegment(sketch, "E391", {"start": v(20.6, 29.91) * mm, "end": v(20.56, 30.03) * mm});
            skLineSegment(sketch, "E392", {"start": v(20.56, 30.03) * mm, "end": v(20.51, 30.15) * mm});
            skLineSegment(sketch, "E393", {"start": v(20.51, 30.15) * mm, "end": v(20.46, 30.27) * mm});
            skLineSegment(sketch, "E394", {"start": v(20.46, 30.27) * mm, "end": v(20.41, 30.39) * mm});
            skLineSegment(sketch, "E395", {"start": v(20.41, 30.39) * mm, "end": v(20.36, 30.5) * mm});
            skLineSegment(sketch, "E396", {"start": v(20.36, 30.5) * mm, "end": v(20.31, 30.62) * mm});
            skLineSegment(sketch, "E397", {"start": v(20.31, 30.62) * mm, "end": v(20.26, 30.74) * mm});
            skLineSegment(sketch, "E398", {"start": v(20.26, 30.74) * mm, "end": v(20.21, 30.85) * mm});
            skLineSegment(sketch, "E399", {"start": v(20.21, 30.85) * mm, "end": v(20.16, 30.97) * mm});
            skLineSegment(sketch, "E400", {"start": v(20.16, 30.97) * mm, "end": v(20.11, 31.08) * mm});
            skLineSegment(sketch, "E401", {"start": v(20.11, 31.08) * mm, "end": v(20.06, 31.2) * mm});
            skLineSegment(sketch, "E402", {"start": v(20.06, 31.2) * mm, "end": v(20, 31.31) * mm});
            skLineSegment(sketch, "E403", {"start": v(20, 31.31) * mm, "end": v(19.95, 31.42) * mm});
            skLineSegment(sketch, "E404", {"start": v(19.95, 31.42) * mm, "end": v(19.9, 31.54) * mm});
            skLineSegment(sketch, "E405", {"start": v(19.9, 31.54) * mm, "end": v(19.84, 31.65) * mm});
            skLineSegment(sketch, "E406", {"start": v(19.84, 31.65) * mm, "end": v(19.79, 31.76) * mm});
            skLineSegment(sketch, "E407", {"start": v(19.79, 31.76) * mm, "end": v(19.73, 31.87) * mm});
            skLineSegment(sketch, "E408", {"start": v(19.73, 31.87) * mm, "end": v(19.68, 31.97) * mm});
            skLineSegment(sketch, "E409", {"start": v(19.68, 31.97) * mm, "end": v(19.62, 32.08) * mm});
            skLineSegment(sketch, "E410", {"start": v(19.62, 32.08) * mm, "end": v(19.57, 32.19) * mm});
            skLineSegment(sketch, "E411", {"start": v(19.57, 32.19) * mm, "end": v(19.5, 32.3) * mm});
            skLineSegment(sketch, "E412", {"start": v(19.5, 32.3) * mm, "end": v(19.45, 32.4) * mm});
            skLineSegment(sketch, "E413", {"start": v(19.45, 32.4) * mm, "end": v(19.4, 32.5) * mm});
            skLineSegment(sketch, "E414", {"start": v(19.4, 32.5) * mm, "end": v(19.33, 32.61) * mm});
            skLineSegment(sketch, "E415", {"start": v(19.33, 32.61) * mm, "end": v(19.27, 32.71) * mm});
            skLineSegment(sketch, "E416", {"start": v(19.27, 32.71) * mm, "end": v(19.21, 32.82) * mm});
            skLineSegment(sketch, "E417", {"start": v(19.21, 32.82) * mm, "end": v(19.15, 32.92) * mm});
            skLineSegment(sketch, "E418", {"start": v(19.15, 32.92) * mm, "end": v(19.1, 33.02) * mm});
            skLineSegment(sketch, "E419", {"start": v(19.1, 33.02) * mm, "end": v(19.03, 33.12) * mm});
            skLineSegment(sketch, "E420", {"start": v(19.03, 33.12) * mm, "end": v(18.97, 33.22) * mm});
            skLineSegment(sketch, "E421", {"start": v(18.97, 33.22) * mm, "end": v(18.9, 33.32) * mm});
            skLineSegment(sketch, "E422", {"start": v(18.9, 33.32) * mm, "end": v(18.84, 33.42) * mm});
            skLineSegment(sketch, "E423", {"start": v(18.84, 33.42) * mm, "end": v(18.78, 33.51) * mm});
            skLineSegment(sketch, "E424", {"start": v(18.78, 33.51) * mm, "end": v(18.71, 33.6) * mm});
            skLineSegment(sketch, "E425", {"start": v(18.71, 33.6) * mm, "end": v(18.65, 33.7) * mm});
            skLineSegment(sketch, "E426", {"start": v(18.65, 33.7) * mm, "end": v(18.58, 33.8) * mm});
            skLineSegment(sketch, "E427", {"start": v(18.58, 33.8) * mm, "end": v(18.52, 33.9) * mm});
            skLineSegment(sketch, "E428", {"start": v(18.52, 33.9) * mm, "end": v(18.45, 33.99) * mm});
            skLineSegment(sketch, "E429", {"start": v(18.45, 33.99) * mm, "end": v(18.38, 34.08) * mm});
            skLineSegment(sketch, "E430", {"start": v(18.38, 34.08) * mm, "end": v(18.32, 34.17) * mm});
            skLineSegment(sketch, "E431", {"start": v(18.32, 34.17) * mm, "end": v(18.25, 34.26) * mm});
            skLineSegment(sketch, "E432", {"start": v(18.25, 34.26) * mm, "end": v(18.18, 34.35) * mm});
            skLineSegment(sketch, "E433", {"start": v(18.18, 34.35) * mm, "end": v(18.1, 34.44) * mm});
            skLineSegment(sketch, "E434", {"start": v(18.1, 34.44) * mm, "end": v(18.04, 34.52) * mm});
            skLineSegment(sketch, "E435", {"start": v(18.04, 34.52) * mm, "end": v(17.97, 34.61) * mm});
            skLineSegment(sketch, "E436", {"start": v(17.97, 34.61) * mm, "end": v(17.9, 34.7) * mm});
            skLineSegment(sketch, "E437", {"start": v(17.9, 34.7) * mm, "end": v(17.82, 34.78) * mm});
            skLineSegment(sketch, "E438", {"start": v(17.82, 34.78) * mm, "end": v(17.75, 34.87) * mm});
            skLineSegment(sketch, "E439", {"start": v(17.75, 34.87) * mm, "end": v(17.68, 34.95) * mm});
            skLineSegment(sketch, "E440", {"start": v(17.68, 34.95) * mm, "end": v(17.6, 35.03) * mm});
            skLineSegment(sketch, "E441", {"start": v(17.6, 35.03) * mm, "end": v(17.53, 35.11) * mm});
            skLineSegment(sketch, "E442", {"start": v(17.53, 35.11) * mm, "end": v(17.45, 35.2) * mm});
            skLineSegment(sketch, "E443", {"start": v(17.45, 35.2) * mm, "end": v(17.37, 35.27) * mm});
            skLineSegment(sketch, "E444", {"start": v(17.37, 35.27) * mm, "end": v(17.3, 35.35) * mm});
            skLineSegment(sketch, "E445", {"start": v(17.3, 35.35) * mm, "end": v(17.22, 35.43) * mm});
            skLineSegment(sketch, "E446", {"start": v(17.22, 35.43) * mm, "end": v(17.14, 35.5) * mm});
            skLineSegment(sketch, "E447", {"start": v(17.14, 35.5) * mm, "end": v(17.06, 35.58) * mm});
            skLineSegment(sketch, "E448", {"start": v(17.06, 35.58) * mm, "end": v(16.98, 35.65) * mm});
            skLineSegment(sketch, "E449", {"start": v(16.98, 35.65) * mm, "end": v(16.9, 35.73) * mm});
            skLineSegment(sketch, "E450", {"start": v(16.9, 35.73) * mm, "end": v(16.82, 35.8) * mm});
            skLineSegment(sketch, "E451", {"start": v(16.82, 35.8) * mm, "end": v(16.74, 35.87) * mm});
            skLineSegment(sketch, "E452", {"start": v(16.74, 35.87) * mm, "end": v(16.66, 35.94) * mm});
            skLineSegment(sketch, "E453", {"start": v(16.66, 35.94) * mm, "end": v(16.57, 36.01) * mm});
            skLineSegment(sketch, "E454", {"start": v(16.57, 36.01) * mm, "end": v(16.5, 36.08) * mm});
            skLineSegment(sketch, "E455", {"start": v(16.5, 36.08) * mm, "end": v(16.4, 36.15) * mm});
            skLineSegment(sketch, "E456", {"start": v(16.4, 36.15) * mm, "end": v(16.32, 36.21) * mm});
            skLineSegment(sketch, "E457", {"start": v(16.32, 36.21) * mm, "end": v(16.23, 36.28) * mm});
            skLineSegment(sketch, "E458", {"start": v(16.23, 36.28) * mm, "end": v(16.15, 36.34) * mm});
            skLineSegment(sketch, "E459", {"start": v(16.15, 36.34) * mm, "end": v(16.06, 36.4) * mm});
            skLineSegment(sketch, "E460", {"start": v(16.06, 36.4) * mm, "end": v(15.97, 36.47) * mm});
            skLineSegment(sketch, "E461", {"start": v(15.97, 36.47) * mm, "end": v(15.88, 36.53) * mm});
            skLineSegment(sketch, "E462", {"start": v(15.88, 36.53) * mm, "end": v(15.8, 36.59) * mm});
            skLineSegment(sketch, "E463", {"start": v(15.8, 36.59) * mm, "end": v(15.7, 36.65) * mm});
            skLineSegment(sketch, "E464", {"start": v(15.7, 36.65) * mm, "end": v(15.61, 36.7) * mm});
            skLineSegment(sketch, "E465", {"start": v(15.61, 36.7) * mm, "end": v(15.52, 36.76) * mm});
            skLineSegment(sketch, "E466", {"start": v(15.52, 36.76) * mm, "end": v(15.43, 36.82) * mm});
            skLineSegment(sketch, "E467", {"start": v(15.43, 36.82) * mm, "end": v(15.33, 36.87) * mm});
            skLineSegment(sketch, "E468", {"start": v(15.33, 36.87) * mm, "end": v(15.24, 36.93) * mm});
            skLineSegment(sketch, "E469", {"start": v(15.24, 36.93) * mm, "end": v(15.14, 36.98) * mm});
            skLineSegment(sketch, "E470", {"start": v(15.14, 36.98) * mm, "end": v(15.05, 37.03) * mm});
            skLineSegment(sketch, "E471", {"start": v(15.05, 37.03) * mm, "end": v(14.95, 37.08) * mm});
            skLineSegment(sketch, "E472", {"start": v(14.95, 37.08) * mm, "end": v(14.85, 37.13) * mm});
            skLineSegment(sketch, "E473", {"start": v(14.85, 37.13) * mm, "end": v(14.76, 37.18) * mm});
            skLineSegment(sketch, "E474", {"start": v(14.76, 37.18) * mm, "end": v(14.66, 37.23) * mm});
            skLineSegment(sketch, "E475", {"start": v(14.66, 37.23) * mm, "end": v(14.56, 37.27) * mm});
            skLineSegment(sketch, "E476", {"start": v(14.56, 37.27) * mm, "end": v(14.46, 37.32) * mm});
            skLineSegment(sketch, "E477", {"start": v(14.46, 37.32) * mm, "end": v(14.36, 37.36) * mm});
            skLineSegment(sketch, "E478", {"start": v(14.36, 37.36) * mm, "end": v(14.25, 37.4) * mm});
            skLineSegment(sketch, "E479", {"start": v(14.25, 37.4) * mm, "end": v(14.15, 37.44) * mm});
            skLineSegment(sketch, "E480", {"start": v(14.15, 37.44) * mm, "end": v(14.05, 37.48) * mm});
            skLineSegment(sketch, "E481", {"start": v(14.05, 37.48) * mm, "end": v(13.94, 37.52) * mm});
            skLineSegment(sketch, "E482", {"start": v(13.94, 37.52) * mm, "end": v(13.84, 37.56) * mm});
            skLineSegment(sketch, "E483", {"start": v(13.84, 37.56) * mm, "end": v(13.73, 37.6) * mm});
            skLineSegment(sketch, "E484", {"start": v(13.73, 37.6) * mm, "end": v(13.62, 37.63) * mm});
            skLineSegment(sketch, "E485", {"start": v(13.62, 37.63) * mm, "end": v(13.51, 37.67) * mm});
            skLineSegment(sketch, "E486", {"start": v(13.51, 37.67) * mm, "end": v(13.4, 37.7) * mm});
            skLineSegment(sketch, "E487", {"start": v(13.4, 37.7) * mm, "end": v(13.3, 37.73) * mm});
            skLineSegment(sketch, "E488", {"start": v(13.3, 37.73) * mm, "end": v(13.19, 37.76) * mm});
            skLineSegment(sketch, "E489", {"start": v(13.19, 37.76) * mm, "end": v(13.07, 37.79) * mm});
            skLineSegment(sketch, "E490", {"start": v(13.07, 37.79) * mm, "end": v(12.96, 37.82) * mm});
            skLineSegment(sketch, "E491", {"start": v(12.96, 37.82) * mm, "end": v(12.85, 37.84) * mm});
            skLineSegment(sketch, "E492", {"start": v(12.85, 37.84) * mm, "end": v(12.73, 37.87) * mm});
            skLineSegment(sketch, "E493", {"start": v(12.73, 37.87) * mm, "end": v(12.62, 37.9) * mm});
            skLineSegment(sketch, "E494", {"start": v(12.62, 37.9) * mm, "end": v(12.5, 37.92) * mm});
            skLineSegment(sketch, "E495", {"start": v(12.5, 37.92) * mm, "end": v(12.39, 37.94) * mm});
            skLineSegment(sketch, "E496", {"start": v(12.39, 37.94) * mm, "end": v(12.27, 37.96) * mm});
            skLineSegment(sketch, "E497", {"start": v(12.27, 37.96) * mm, "end": v(12.15, 37.98) * mm});
            skLineSegment(sketch, "E498", {"start": v(12.15, 37.98) * mm, "end": v(12.03, 38) * mm});
            skLineSegment(sketch, "E499", {"start": v(12.03, 38) * mm, "end": v(11.9, 38.01) * mm});
            skLineSegment(sketch, "E500", {"start": v(11.9, 38.01) * mm, "end": v(11.79, 38.03) * mm});
            skLineSegment(sketch, "E501", {"start": v(11.79, 38.03) * mm, "end": v(11.67, 38.04) * mm});
            skLineSegment(sketch, "E502", {"start": v(11.67, 38.04) * mm, "end": v(11.54, 38.05) * mm});
            skLineSegment(sketch, "E503", {"start": v(11.54, 38.05) * mm, "end": v(11.42, 38.07) * mm});
            skLineSegment(sketch, "E504", {"start": v(11.42, 38.07) * mm, "end": v(11.3, 38.08) * mm});
            skLineSegment(sketch, "E505", {"start": v(11.3, 38.08) * mm, "end": v(11.17, 38.08) * mm});
            skLineSegment(sketch, "E506", {"start": v(11.17, 38.08) * mm, "end": v(11.04, 38.1) * mm});
            skLineSegment(sketch, "E507", {"start": v(11.04, 38.1) * mm, "end": v(10.91, 38.1) * mm});
            skLineSegment(sketch, "E508", {"start": v(10.91, 38.1) * mm, "end": v(10.78, 38.1) * mm});
            skLineSegment(sketch, "E509", {"start": v(10.78, 38.1) * mm, "end": v(10.65, 38.1) * mm});
            skLineSegment(sketch, "E510", {"start": v(10.65, 38.1) * mm, "end": v(10.52, 38.1) * mm});
            skLineSegment(sketch, "E511", {"start": v(10.52, 38.1) * mm, "end": v(10.4, 38.1) * mm});
            skLineSegment(sketch, "E512", {"start": v(10.4, 38.1) * mm, "end": v(10.19, 38.1) * mm});
            skLineSegment(sketch, "E513", {"start": v(10.19, 38.1) * mm, "end": v(9.99, 38.1) * mm});
            skLineSegment(sketch, "E514", {"start": v(9.99, 38.1) * mm, "end": v(9.79, 38.1) * mm});
            skLineSegment(sketch, "E515", {"start": v(9.79, 38.1) * mm, "end": v(9.59, 38.1) * mm});
            skLineSegment(sketch, "E516", {"start": v(9.59, 38.1) * mm, "end": v(9.39, 38.08) * mm});
            skLineSegment(sketch, "E517", {"start": v(9.39, 38.08) * mm, "end": v(9.19, 38.07) * mm});
            skLineSegment(sketch, "E518", {"start": v(9.19, 38.07) * mm, "end": v(8.99, 38.06) * mm});
            skLineSegment(sketch, "E519", {"start": v(8.99, 38.06) * mm, "end": v(8.8, 38.04) * mm});
            skLineSegment(sketch, "E520", {"start": v(8.8, 38.04) * mm, "end": v(8.6, 38.02) * mm});
            skLineSegment(sketch, "E521", {"start": v(8.6, 38.02) * mm, "end": v(8.4, 38) * mm});
            skLineSegment(sketch, "E522", {"start": v(8.4, 38) * mm, "end": v(8.2, 37.98) * mm});
            skLineSegment(sketch, "E523", {"start": v(8.2, 37.98) * mm, "end": v(8, 37.96) * mm});
            skLineSegment(sketch, "E524", {"start": v(8, 37.96) * mm, "end": v(7.81, 37.93) * mm});
            skLineSegment(sketch, "E525", {"start": v(7.81, 37.93) * mm, "end": v(7.62, 37.9) * mm});
            skLineSegment(sketch, "E526", {"start": v(7.62, 37.9) * mm, "end": v(7.43, 37.87) * mm});
            skLineSegment(sketch, "E527", {"start": v(7.43, 37.87) * mm, "end": v(7.24, 37.84) * mm});
            skLineSegment(sketch, "E528", {"start": v(7.24, 37.84) * mm, "end": v(7.04, 37.8) * mm});
            skLineSegment(sketch, "E529", {"start": v(7.04, 37.8) * mm, "end": v(6.85, 37.78) * mm});
            skLineSegment(sketch, "E530", {"start": v(6.85, 37.78) * mm, "end": v(6.67, 37.74) * mm});
            skLineSegment(sketch, "E531", {"start": v(6.67, 37.74) * mm, "end": v(6.48, 37.7) * mm});
            skLineSegment(sketch, "E532", {"start": v(6.48, 37.7) * mm, "end": v(6.29, 37.66) * mm});
            skLineSegment(sketch, "E533", {"start": v(6.29, 37.66) * mm, "end": v(6.1, 37.62) * mm});
            skLineSegment(sketch, "E534", {"start": v(6.1, 37.62) * mm, "end": v(5.92, 37.58) * mm});
            skLineSegment(sketch, "E535", {"start": v(5.92, 37.58) * mm, "end": v(5.73, 37.53) * mm});
            skLineSegment(sketch, "E536", {"start": v(5.73, 37.53) * mm, "end": v(5.55, 37.48) * mm});
            skLineSegment(sketch, "E537", {"start": v(5.55, 37.48) * mm, "end": v(5.36, 37.44) * mm});
            skLineSegment(sketch, "E538", {"start": v(5.36, 37.44) * mm, "end": v(5.18, 37.39) * mm});
            skLineSegment(sketch, "E539", {"start": v(5.18, 37.39) * mm, "end": v(5, 37.33) * mm});
            skLineSegment(sketch, "E540", {"start": v(5, 37.33) * mm, "end": v(4.81, 37.28) * mm});
            skLineSegment(sketch, "E541", {"start": v(4.81, 37.28) * mm, "end": v(4.63, 37.23) * mm});
            skLineSegment(sketch, "E542", {"start": v(4.63, 37.23) * mm, "end": v(4.45, 37.17) * mm});
            skLineSegment(sketch, "E543", {"start": v(4.45, 37.17) * mm, "end": v(4.28, 37.12) * mm});
            skLineSegment(sketch, "E544", {"start": v(4.28, 37.12) * mm, "end": v(4.1, 37.06) * mm});
            skLineSegment(sketch, "E545", {"start": v(4.1, 37.06) * mm, "end": v(3.92, 37) * mm});
            skLineSegment(sketch, "E546", {"start": v(3.92, 37) * mm, "end": v(3.74, 36.94) * mm});
            skLineSegment(sketch, "E547", {"start": v(3.74, 36.94) * mm, "end": v(3.57, 36.87) * mm});
            skLineSegment(sketch, "E548", {"start": v(3.57, 36.87) * mm, "end": v(3.4, 36.81) * mm});
            skLineSegment(sketch, "E549", {"start": v(3.4, 36.81) * mm, "end": v(3.22, 36.75) * mm});
            skLineSegment(sketch, "E550", {"start": v(3.22, 36.75) * mm, "end": v(3.05, 36.68) * mm});
            skLineSegment(sketch, "E551", {"start": v(3.05, 36.68) * mm, "end": v(2.88, 36.61) * mm});
            skLineSegment(sketch, "E552", {"start": v(2.88, 36.61) * mm, "end": v(2.7, 36.54) * mm});
            skLineSegment(sketch, "E553", {"start": v(2.7, 36.54) * mm, "end": v(2.53, 36.47) * mm});
            skLineSegment(sketch, "E554", {"start": v(2.53, 36.47) * mm, "end": v(2.36, 36.4) * mm});
            skLineSegment(sketch, "E555", {"start": v(2.36, 36.4) * mm, "end": v(2.2, 36.33) * mm});
            skLineSegment(sketch, "E556", {"start": v(2.2, 36.33) * mm, "end": v(2.03, 36.26) * mm});
            skLineSegment(sketch, "E557", {"start": v(2.03, 36.26) * mm, "end": v(1.86, 36.18) * mm});
            skLineSegment(sketch, "E558", {"start": v(1.86, 36.18) * mm, "end": v(1.7, 36.1) * mm});
            skLineSegment(sketch, "E559", {"start": v(1.7, 36.1) * mm, "end": v(1.53, 36.03) * mm});
            skLineSegment(sketch, "E560", {"start": v(1.53, 36.03) * mm, "end": v(1.37, 35.96) * mm});
            skLineSegment(sketch, "E561", {"start": v(1.37, 35.96) * mm, "end": v(1.2, 35.88) * mm});
            skLineSegment(sketch, "E562", {"start": v(1.2, 35.88) * mm, "end": v(1.04, 35.8) * mm});
            skLineSegment(sketch, "E563", {"start": v(1.04, 35.8) * mm, "end": v(0.88, 35.72) * mm});
            skLineSegment(sketch, "E564", {"start": v(0.88, 35.72) * mm, "end": v(0.72, 35.64) * mm});
            skLineSegment(sketch, "E565", {"start": v(0.72, 35.64) * mm, "end": v(0.56, 35.56) * mm});
            skLineSegment(sketch, "E566", {"start": v(0.56, 35.56) * mm, "end": v(0.4, 35.48) * mm});
            skLineSegment(sketch, "E567", {"start": v(0.4, 35.48) * mm, "end": v(0.25, 35.4) * mm});
            skLineSegment(sketch, "E568", {"start": v(0.25, 35.4) * mm, "end": v(0.1, 35.3) * mm});
            skLineSegment(sketch, "E569", {"start": v(0.1, 35.3) * mm, "end": v(-0.06, 35.22) * mm});
            skLineSegment(sketch, "E570", {"start": v(-0.06, 35.22) * mm, "end": v(-0.22, 35.14) * mm});
            skLineSegment(sketch, "E571", {"start": v(-0.22, 35.14) * mm, "end": v(-0.37, 35.05) * mm});
            skLineSegment(sketch, "E572", {"start": v(-0.37, 35.05) * mm, "end": v(-0.52, 34.97) * mm});
            skLineSegment(sketch, "E573", {"start": v(-0.52, 34.97) * mm, "end": v(-0.67, 34.88) * mm});
            skLineSegment(sketch, "E574", {"start": v(-0.67, 34.88) * mm, "end": v(-0.82, 34.8) * mm});
            skLineSegment(sketch, "E575", {"start": v(-0.82, 34.8) * mm, "end": v(-0.97, 34.7) * mm});
            skLineSegment(sketch, "E576", {"start": v(-0.97, 34.7) * mm, "end": v(-1.12, 34.62) * mm});
            skLineSegment(sketch, "E577", {"start": v(-1.12, 34.62) * mm, "end": v(-1.27, 34.53) * mm});
            skLineSegment(sketch, "E578", {"start": v(-1.27, 34.53) * mm, "end": v(-1.41, 34.44) * mm});
            skLineSegment(sketch, "E579", {"start": v(-1.41, 34.44) * mm, "end": v(-1.56, 34.35) * mm});
            skLineSegment(sketch, "E580", {"start": v(-1.56, 34.35) * mm, "end": v(-1.7, 34.25) * mm});
            skLineSegment(sketch, "E581", {"start": v(-1.7, 34.25) * mm, "end": v(-1.85, 34.16) * mm});
            skLineSegment(sketch, "E582", {"start": v(-1.85, 34.16) * mm, "end": v(-1.99, 34.07) * mm});
            skLineSegment(sketch, "E583", {"start": v(-1.99, 34.07) * mm, "end": v(-2.13, 33.98) * mm});
            skLineSegment(sketch, "E584", {"start": v(-2.13, 33.98) * mm, "end": v(-2.27, 33.89) * mm});
            skLineSegment(sketch, "E585", {"start": v(-2.27, 33.89) * mm, "end": v(-2.4, 33.8) * mm});
            skLineSegment(sketch, "E586", {"start": v(-2.4, 33.8) * mm, "end": v(-2.54, 33.7) * mm});
            skLineSegment(sketch, "E587", {"start": v(-2.54, 33.7) * mm, "end": v(-2.68, 33.6) * mm});
            skLineSegment(sketch, "E588", {"start": v(-2.68, 33.6) * mm, "end": v(-2.82, 33.52) * mm});
            skLineSegment(sketch, "E589", {"start": v(-2.82, 33.52) * mm, "end": v(-2.95, 33.42) * mm});
            skLineSegment(sketch, "E590", {"start": v(-2.95, 33.42) * mm, "end": v(-3.08, 33.33) * mm});
            skLineSegment(sketch, "E591", {"start": v(-3.08, 33.33) * mm, "end": v(-3.22, 33.23) * mm});
            skLineSegment(sketch, "E592", {"start": v(-3.22, 33.23) * mm, "end": v(-3.35, 33.14) * mm});
            skLineSegment(sketch, "E593", {"start": v(-3.35, 33.14) * mm, "end": v(-3.48, 33.05) * mm});
            skLineSegment(sketch, "E594", {"start": v(-3.48, 33.05) * mm, "end": v(-3.6, 32.95) * mm});
            skLineSegment(sketch, "E595", {"start": v(-3.6, 32.95) * mm, "end": v(-3.73, 32.86) * mm});
            skLineSegment(sketch, "E596", {"start": v(-3.73, 32.86) * mm, "end": v(-3.86, 32.76) * mm});
            skLineSegment(sketch, "E597", {"start": v(-3.86, 32.76) * mm, "end": v(-3.99, 32.67) * mm});
            skLineSegment(sketch, "E598", {"start": v(-3.99, 32.67) * mm, "end": v(-4.11, 32.57) * mm});
            skLineSegment(sketch, "E599", {"start": v(-4.11, 32.57) * mm, "end": v(-4.23, 32.48) * mm});
            skLineSegment(sketch, "E600", {"start": v(-4.23, 32.48) * mm, "end": v(-4.36, 32.39) * mm});
            skLineSegment(sketch, "E601", {"start": v(-4.36, 32.39) * mm, "end": v(-4.48, 32.3) * mm});
            skLineSegment(sketch, "E602", {"start": v(-4.48, 32.3) * mm, "end": v(-4.6, 32.2) * mm});
            skLineSegment(sketch, "E603", {"start": v(-4.6, 32.2) * mm, "end": v(-4.72, 32.1) * mm});
            skLineSegment(sketch, "E604", {"start": v(-4.72, 32.1) * mm, "end": v(-4.83, 32.01) * mm});
            skLineSegment(sketch, "E605", {"start": v(-4.83, 32.01) * mm, "end": v(-4.95, 31.92) * mm});
            skLineSegment(sketch, "E606", {"start": v(-4.95, 31.92) * mm, "end": v(-5.07, 31.82) * mm});
            skLineSegment(sketch, "E607", {"start": v(-5.07, 31.82) * mm, "end": v(-5.18, 31.73) * mm});
            skLineSegment(sketch, "E608", {"start": v(-5.18, 31.73) * mm, "end": v(-5.3, 31.64) * mm});
            skLineSegment(sketch, "E609", {"start": v(-5.3, 31.64) * mm, "end": v(-5.4, 31.55) * mm});
            skLineSegment(sketch, "E610", {"start": v(-5.4, 31.55) * mm, "end": v(-5.51, 31.45) * mm});
            skLineSegment(sketch, "E611", {"start": v(-5.51, 31.45) * mm, "end": v(-5.62, 31.36) * mm});
            skLineSegment(sketch, "E612", {"start": v(-5.62, 31.36) * mm, "end": v(-5.73, 31.27) * mm});
            skLineSegment(sketch, "E613", {"start": v(-5.73, 31.27) * mm, "end": v(-5.84, 31.18) * mm});
            skLineSegment(sketch, "E614", {"start": v(-5.84, 31.18) * mm, "end": v(-5.94, 31.09) * mm});
            skLineSegment(sketch, "E615", {"start": v(-5.94, 31.09) * mm, "end": v(-6.05, 31) * mm});
            skLineSegment(sketch, "E616", {"start": v(-6.05, 31) * mm, "end": v(-6.15, 30.91) * mm});
            skLineSegment(sketch, "E617", {"start": v(-6.15, 30.91) * mm, "end": v(-6.25, 30.82) * mm});
            skLineSegment(sketch, "E618", {"start": v(-6.25, 30.82) * mm, "end": v(-6.35, 30.73) * mm});
            skLineSegment(sketch, "E619", {"start": v(-6.35, 30.73) * mm, "end": v(-6.45, 30.65) * mm});
            skLineSegment(sketch, "E620", {"start": v(-6.45, 30.65) * mm, "end": v(-6.55, 30.56) * mm});
            skLineSegment(sketch, "E621", {"start": v(-6.55, 30.56) * mm, "end": v(-6.65, 30.47) * mm});
            skLineSegment(sketch, "E622", {"start": v(-6.65, 30.47) * mm, "end": v(-6.75, 30.39) * mm});
            skLineSegment(sketch, "E623", {"start": v(-6.75, 30.39) * mm, "end": v(-6.84, 30.3) * mm});
            skLineSegment(sketch, "E624", {"start": v(-6.84, 30.3) * mm, "end": v(-6.93, 30.22) * mm});
            skLineSegment(sketch, "E625", {"start": v(-6.93, 30.22) * mm, "end": v(-7.02, 30.13) * mm});
            skLineSegment(sketch, "E626", {"start": v(-7.02, 30.13) * mm, "end": v(-7.12, 30.05) * mm});
            skLineSegment(sketch, "E627", {"start": v(-7.12, 30.05) * mm, "end": v(-7.2, 29.97) * mm});
            skLineSegment(sketch, "E628", {"start": v(-7.2, 29.97) * mm, "end": v(-7.3, 29.89) * mm});
            skLineSegment(sketch, "E629", {"start": v(-7.3, 29.89) * mm, "end": v(-7.38, 29.8) * mm});
            skLineSegment(sketch, "E630", {"start": v(-7.38, 29.8) * mm, "end": v(-7.47, 29.72) * mm});
            skLineSegment(sketch, "E631", {"start": v(-7.47, 29.72) * mm, "end": v(-7.55, 29.65) * mm});
            skLineSegment(sketch, "E632", {"start": v(-7.55, 29.65) * mm, "end": v(-7.63, 29.57) * mm});
            skLineSegment(sketch, "E633", {"start": v(-7.63, 29.57) * mm, "end": v(-7.71, 29.5) * mm});
            skLineSegment(sketch, "E634", {"start": v(-7.71, 29.5) * mm, "end": v(-7.8, 29.41) * mm});
            skLineSegment(sketch, "E635", {"start": v(-7.8, 29.41) * mm, "end": v(-7.87, 29.34) * mm});
            skLineSegment(sketch, "E636", {"start": v(-7.87, 29.34) * mm, "end": v(-7.95, 29.27) * mm});
            skLineSegment(sketch, "E637", {"start": v(-7.95, 29.27) * mm, "end": v(-8.03, 29.2) * mm});
            skLineSegment(sketch, "E638", {"start": v(-8.03, 29.2) * mm, "end": v(-8.1, 29.12) * mm});
            skLineSegment(sketch, "E639", {"start": v(-8.1, 29.12) * mm, "end": v(-8.18, 29.05) * mm});
            skLineSegment(sketch, "E640", {"start": v(-8.18, 29.05) * mm, "end": v(-8.18, 29.09) * mm});
            skLineSegment(sketch, "E641", {"start": v(-8.18, 29.09) * mm, "end": v(-8.18, 29.13) * mm});
            skLineSegment(sketch, "E642", {"start": v(-8.18, 29.13) * mm, "end": v(-8.19, 29.17) * mm});
            skLineSegment(sketch, "E643", {"start": v(-8.19, 29.17) * mm, "end": v(-8.19, 29.22) * mm});
            skLineSegment(sketch, "E644", {"start": v(-8.19, 29.22) * mm, "end": v(-8.2, 29.26) * mm});
            skLineSegment(sketch, "E645", {"start": v(-8.2, 29.26) * mm, "end": v(-8.2, 29.31) * mm});
            skLineSegment(sketch, "E646", {"start": v(-8.2, 29.31) * mm, "end": v(-8.2, 29.36) * mm});
            skLineSegment(sketch, "E647", {"start": v(-8.2, 29.36) * mm, "end": v(-8.21, 29.41) * mm});
            skLineSegment(sketch, "E648", {"start": v(-8.21, 29.41) * mm, "end": v(-8.22, 29.46) * mm});
            skLineSegment(sketch, "E649", {"start": v(-8.22, 29.46) * mm, "end": v(-8.23, 29.52) * mm});
            skLineSegment(sketch, "E650", {"start": v(-8.23, 29.52) * mm, "end": v(-8.24, 29.57) * mm});
            skLineSegment(sketch, "E651", {"start": v(-8.24, 29.57) * mm, "end": v(-8.24, 29.63) * mm});
            skLineSegment(sketch, "E652", {"start": v(-8.24, 29.63) * mm, "end": v(-8.25, 29.68) * mm});
            skLineSegment(sketch, "E653", {"start": v(-8.25, 29.68) * mm, "end": v(-8.26, 29.74) * mm});
            skLineSegment(sketch, "E654", {"start": v(-8.26, 29.74) * mm, "end": v(-8.28, 29.8) * mm});
            skLineSegment(sketch, "E655", {"start": v(-8.28, 29.8) * mm, "end": v(-8.29, 29.86) * mm});
            skLineSegment(sketch, "E656", {"start": v(-8.29, 29.86) * mm, "end": v(-8.3, 29.92) * mm});
            skLineSegment(sketch, "E657", {"start": v(-8.3, 29.92) * mm, "end": v(-8.31, 29.98) * mm});
            skLineSegment(sketch, "E658", {"start": v(-8.31, 29.98) * mm, "end": v(-8.33, 30.05) * mm});
            skLineSegment(sketch, "E659", {"start": v(-8.33, 30.05) * mm, "end": v(-8.34, 30.11) * mm});
            skLineSegment(sketch, "E660", {"start": v(-8.34, 30.11) * mm, "end": v(-8.36, 30.18) * mm});
            skLineSegment(sketch, "E661", {"start": v(-8.36, 30.18) * mm, "end": v(-8.37, 30.24) * mm});
            skLineSegment(sketch, "E662", {"start": v(-8.37, 30.24) * mm, "end": v(-8.39, 30.31) * mm});
            skLineSegment(sketch, "E663", {"start": v(-8.39, 30.31) * mm, "end": v(-8.4, 30.38) * mm});
            skLineSegment(sketch, "E664", {"start": v(-8.4, 30.38) * mm, "end": v(-8.43, 30.45) * mm});
            skLineSegment(sketch, "E665", {"start": v(-8.43, 30.45) * mm, "end": v(-8.45, 30.52) * mm});
            skLineSegment(sketch, "E666", {"start": v(-8.45, 30.52) * mm, "end": v(-8.47, 30.59) * mm});
            skLineSegment(sketch, "E667", {"start": v(-8.47, 30.59) * mm, "end": v(-8.49, 30.66) * mm});
            skLineSegment(sketch, "E668", {"start": v(-8.49, 30.66) * mm, "end": v(-8.5, 30.73) * mm});
            skLineSegment(sketch, "E669", {"start": v(-8.5, 30.73) * mm, "end": v(-8.53, 30.8) * mm});
            skLineSegment(sketch, "E670", {"start": v(-8.53, 30.8) * mm, "end": v(-8.55, 30.88) * mm});
            skLineSegment(sketch, "E671", {"start": v(-8.55, 30.88) * mm, "end": v(-8.58, 30.96) * mm});
            skLineSegment(sketch, "E672", {"start": v(-8.58, 30.96) * mm, "end": v(-8.6, 31.03) * mm});
            skLineSegment(sketch, "E673", {"start": v(-8.6, 31.03) * mm, "end": v(-8.63, 31.1) * mm});
            skLineSegment(sketch, "E674", {"start": v(-8.63, 31.1) * mm, "end": v(-8.66, 31.18) * mm});
            skLineSegment(sketch, "E675", {"start": v(-8.66, 31.18) * mm, "end": v(-8.69, 31.26) * mm});
            skLineSegment(sketch, "E676", {"start": v(-8.69, 31.26) * mm, "end": v(-8.72, 31.34) * mm});
            skLineSegment(sketch, "E677", {"start": v(-8.72, 31.34) * mm, "end": v(-8.75, 31.42) * mm});
            skLineSegment(sketch, "E678", {"start": v(-8.75, 31.42) * mm, "end": v(-8.78, 31.5) * mm});
            skLineSegment(sketch, "E679", {"start": v(-8.78, 31.5) * mm, "end": v(-8.81, 31.57) * mm});
            skLineSegment(sketch, "E680", {"start": v(-8.81, 31.57) * mm, "end": v(-8.85, 31.65) * mm});
            skLineSegment(sketch, "E681", {"start": v(-8.85, 31.65) * mm, "end": v(-8.88, 31.73) * mm});
            skLineSegment(sketch, "E682", {"start": v(-8.88, 31.73) * mm, "end": v(-8.92, 31.81) * mm});
            skLineSegment(sketch, "E683", {"start": v(-8.92, 31.81) * mm, "end": v(-8.95, 31.9) * mm});
            skLineSegment(sketch, "E684", {"start": v(-8.95, 31.9) * mm, "end": v(-9, 31.97) * mm});
            skLineSegment(sketch, "E685", {"start": v(-9, 31.97) * mm, "end": v(-9.03, 32.05) * mm});
            skLineSegment(sketch, "E686", {"start": v(-9.03, 32.05) * mm, "end": v(-9.07, 32.14) * mm});
            skLineSegment(sketch, "E687", {"start": v(-9.07, 32.14) * mm, "end": v(-9.11, 32.22) * mm});
            skLineSegment(sketch, "E688", {"start": v(-9.11, 32.22) * mm, "end": v(-9.15, 32.3) * mm});
            skLineSegment(sketch, "E689", {"start": v(-9.15, 32.3) * mm, "end": v(-9.2, 32.38) * mm});
            skLineSegment(sketch, "E690", {"start": v(-9.2, 32.38) * mm, "end": v(-9.24, 32.46) * mm});
            skLineSegment(sketch, "E691", {"start": v(-9.24, 32.46) * mm, "end": v(-9.29, 32.54) * mm});
            skLineSegment(sketch, "E692", {"start": v(-9.29, 32.54) * mm, "end": v(-9.34, 32.63) * mm});
            skLineSegment(sketch, "E693", {"start": v(-9.34, 32.63) * mm, "end": v(-9.38, 32.7) * mm});
            skLineSegment(sketch, "E694", {"start": v(-9.38, 32.7) * mm, "end": v(-9.43, 32.79) * mm});
            skLineSegment(sketch, "E695", {"start": v(-9.43, 32.79) * mm, "end": v(-9.48, 32.87) * mm});
            skLineSegment(sketch, "E696", {"start": v(-9.48, 32.87) * mm, "end": v(-9.54, 32.95) * mm});
            skLineSegment(sketch, "E697", {"start": v(-9.54, 32.95) * mm, "end": v(-9.6, 33.04) * mm});
            skLineSegment(sketch, "E698", {"start": v(-9.6, 33.04) * mm, "end": v(-9.65, 33.12) * mm});
            skLineSegment(sketch, "E699", {"start": v(-9.65, 33.12) * mm, "end": v(-9.7, 33.2) * mm});
            skLineSegment(sketch, "E700", {"start": v(-9.7, 33.2) * mm, "end": v(-9.76, 33.28) * mm});
            skLineSegment(sketch, "E701", {"start": v(-9.76, 33.28) * mm, "end": v(-9.82, 33.36) * mm});
            skLineSegment(sketch, "E702", {"start": v(-9.82, 33.36) * mm, "end": v(-9.88, 33.44) * mm});
            skLineSegment(sketch, "E703", {"start": v(-9.88, 33.44) * mm, "end": v(-9.94, 33.52) * mm});
            skLineSegment(sketch, "E704", {"start": v(-9.94, 33.52) * mm, "end": v(-10, 33.6) * mm});
            skLineSegment(sketch, "E705", {"start": v(-10, 33.6) * mm, "end": v(-10.07, 33.68) * mm});
            skLineSegment(sketch, "E706", {"start": v(-10.07, 33.68) * mm, "end": v(-10.13, 33.76) * mm});
            skLineSegment(sketch, "E707", {"start": v(-10.13, 33.76) * mm, "end": v(-10.2, 33.84) * mm});
            skLineSegment(sketch, "E708", {"start": v(-10.2, 33.84) * mm, "end": v(-10.27, 33.92) * mm});
            skLineSegment(sketch, "E709", {"start": v(-10.27, 33.92) * mm, "end": v(-10.34, 34) * mm});
            skLineSegment(sketch, "E710", {"start": v(-10.34, 34) * mm, "end": v(-10.41, 34.08) * mm});
            skLineSegment(sketch, "E711", {"start": v(-10.41, 34.08) * mm, "end": v(-10.48, 34.15) * mm});
            skLineSegment(sketch, "E712", {"start": v(-10.48, 34.15) * mm, "end": v(-10.56, 34.23) * mm});
            skLineSegment(sketch, "E713", {"start": v(-10.56, 34.23) * mm, "end": v(-10.64, 34.3) * mm});
            skLineSegment(sketch, "E714", {"start": v(-10.64, 34.3) * mm, "end": v(-10.71, 34.38) * mm});
            skLineSegment(sketch, "E715", {"start": v(-10.71, 34.38) * mm, "end": v(-10.8, 34.46) * mm});
            skLineSegment(sketch, "E716", {"start": v(-10.8, 34.46) * mm, "end": v(-10.87, 34.53) * mm});
            skLineSegment(sketch, "E717", {"start": v(-10.87, 34.53) * mm, "end": v(-10.96, 34.6) * mm});
            skLineSegment(sketch, "E718", {"start": v(-10.96, 34.6) * mm, "end": v(-11.04, 34.68) * mm});
            skLineSegment(sketch, "E719", {"start": v(-11.04, 34.68) * mm, "end": v(-11.13, 34.75) * mm});
            skLineSegment(sketch, "E720", {"start": v(-11.13, 34.75) * mm, "end": v(-11.21, 34.82) * mm});
            skLineSegment(sketch, "E721", {"start": v(-11.21, 34.82) * mm, "end": v(-11.3, 34.9) * mm});
            skLineSegment(sketch, "E722", {"start": v(-11.3, 34.9) * mm, "end": v(-11.4, 34.96) * mm});
            skLineSegment(sketch, "E723", {"start": v(-11.4, 34.96) * mm, "end": v(-11.49, 35.03) * mm});
            skLineSegment(sketch, "E724", {"start": v(-11.49, 35.03) * mm, "end": v(-11.58, 35.1) * mm});
            skLineSegment(sketch, "E725", {"start": v(-11.58, 35.1) * mm, "end": v(-11.68, 35.16) * mm});
            skLineSegment(sketch, "E726", {"start": v(-11.68, 35.16) * mm, "end": v(-11.77, 35.23) * mm});
            skLineSegment(sketch, "E727", {"start": v(-11.77, 35.23) * mm, "end": v(-11.87, 35.3) * mm});
            skLineSegment(sketch, "E728", {"start": v(-11.87, 35.3) * mm, "end": v(-11.97, 35.36) * mm});
            skLineSegment(sketch, "E729", {"start": v(-11.97, 35.36) * mm, "end": v(-12.08, 35.42) * mm});
            skLineSegment(sketch, "E730", {"start": v(-12.08, 35.42) * mm, "end": v(-12.18, 35.48) * mm});
            skLineSegment(sketch, "E731", {"start": v(-12.18, 35.48) * mm, "end": v(-12.29, 35.55) * mm});
            skLineSegment(sketch, "E732", {"start": v(-12.29, 35.55) * mm, "end": v(-12.4, 35.6) * mm});
            skLineSegment(sketch, "E733", {"start": v(-12.4, 35.6) * mm, "end": v(-12.5, 35.66) * mm});
            skLineSegment(sketch, "E734", {"start": v(-12.5, 35.66) * mm, "end": v(-12.62, 35.72) * mm});
            skLineSegment(sketch, "E735", {"start": v(-12.62, 35.72) * mm, "end": v(-12.73, 35.78) * mm});
            skLineSegment(sketch, "E736", {"start": v(-12.73, 35.78) * mm, "end": v(-12.84, 35.83) * mm});
            skLineSegment(sketch, "E737", {"start": v(-12.84, 35.83) * mm, "end": v(-12.96, 35.88) * mm});
            skLineSegment(sketch, "E738", {"start": v(-12.96, 35.88) * mm, "end": v(-13.08, 35.94) * mm});
            skLineSegment(sketch, "E739", {"start": v(-13.08, 35.94) * mm, "end": v(-13.2, 35.99) * mm});
            skLineSegment(sketch, "E740", {"start": v(-13.2, 35.99) * mm, "end": v(-13.32, 36.04) * mm});
            skLineSegment(sketch, "E741", {"start": v(-13.32, 36.04) * mm, "end": v(-13.45, 36.09) * mm});
            skLineSegment(sketch, "E742", {"start": v(-13.45, 36.09) * mm, "end": v(-13.58, 36.13) * mm});
            skLineSegment(sketch, "E743", {"start": v(-13.58, 36.13) * mm, "end": v(-13.7, 36.18) * mm});
            skLineSegment(sketch, "E744", {"start": v(-13.7, 36.18) * mm, "end": v(-13.83, 36.22) * mm});
            skLineSegment(sketch, "E745", {"start": v(-13.83, 36.22) * mm, "end": v(-13.97, 36.26) * mm});
            skLineSegment(sketch, "E746", {"start": v(-13.97, 36.26) * mm, "end": v(-14.1, 36.3) * mm});
            skLineSegment(sketch, "E747", {"start": v(-14.1, 36.3) * mm, "end": v(-14.24, 36.34) * mm});
            skLineSegment(sketch, "E748", {"start": v(-14.24, 36.34) * mm, "end": v(-14.38, 36.38) * mm});
            skLineSegment(sketch, "E749", {"start": v(-14.38, 36.38) * mm, "end": v(-14.52, 36.42) * mm});
            skLineSegment(sketch, "E750", {"start": v(-14.52, 36.42) * mm, "end": v(-14.66, 36.45) * mm});
            skLineSegment(sketch, "E751", {"start": v(-14.66, 36.45) * mm, "end": v(-14.8, 36.48) * mm});
            skLineSegment(sketch, "E752", {"start": v(-14.8, 36.48) * mm, "end": v(-14.95, 36.51) * mm});
            skLineSegment(sketch, "E753", {"start": v(-14.95, 36.51) * mm, "end": v(-15.1, 36.54) * mm});
            skLineSegment(sketch, "E754", {"start": v(-15.1, 36.54) * mm, "end": v(-15.25, 36.57) * mm});
            skLineSegment(sketch, "E755", {"start": v(-15.25, 36.57) * mm, "end": v(-15.4, 36.6) * mm});
            skLineSegment(sketch, "E756", {"start": v(-15.4, 36.6) * mm, "end": v(-15.56, 36.62) * mm});
            skLineSegment(sketch, "E757", {"start": v(-15.56, 36.62) * mm, "end": v(-15.72, 36.64) * mm});
            skLineSegment(sketch, "E758", {"start": v(-15.72, 36.64) * mm, "end": v(-15.88, 36.66) * mm});
            skLineSegment(sketch, "E759", {"start": v(-15.88, 36.66) * mm, "end": v(-16.04, 36.68) * mm});
            skLineSegment(sketch, "E760", {"start": v(-16.04, 36.68) * mm, "end": v(-16.2, 36.7) * mm});
            skLineSegment(sketch, "E761", {"start": v(-16.2, 36.7) * mm, "end": v(-16.37, 36.7) * mm});
            skLineSegment(sketch, "E762", {"start": v(-16.37, 36.7) * mm, "end": v(-16.54, 36.72) * mm});
            skLineSegment(sketch, "E763", {"start": v(-16.54, 36.72) * mm, "end": v(-16.71, 36.73) * mm});
            skLineSegment(sketch, "E764", {"start": v(-16.71, 36.73) * mm, "end": v(-16.88, 36.73) * mm});
            skLineSegment(sketch, "E765", {"start": v(-16.88, 36.73) * mm, "end": v(-17.06, 36.74) * mm});
            skLineSegment(sketch, "E766", {"start": v(-17.06, 36.74) * mm, "end": v(-17.24, 36.74) * mm});
            skLineSegment(sketch, "E767", {"start": v(-17.24, 36.74) * mm, "end": v(-17.42, 36.74) * mm});
            skLineSegment(sketch, "E768", {"start": v(-17.42, 36.74) * mm, "end": v(-17.58, 36.74) * mm});
            skLineSegment(sketch, "E769", {"start": v(-17.58, 36.74) * mm, "end": v(-17.75, 36.74) * mm});
            skLineSegment(sketch, "E770", {"start": v(-17.75, 36.74) * mm, "end": v(-17.92, 36.74) * mm});
            skLineSegment(sketch, "E771", {"start": v(-17.92, 36.74) * mm, "end": v(-18.08, 36.74) * mm});
            skLineSegment(sketch, "E772", {"start": v(-18.08, 36.74) * mm, "end": v(-18.25, 36.74) * mm});
            skLineSegment(sketch, "E773", {"start": v(-18.25, 36.74) * mm, "end": v(-18.42, 36.74) * mm});
            skLineSegment(sketch, "E774", {"start": v(-18.42, 36.74) * mm, "end": v(-18.59, 36.74) * mm});
            skLineSegment(sketch, "E775", {"start": v(-18.59, 36.74) * mm, "end": v(-18.75, 36.74) * mm});
            skLineSegment(sketch, "E776", {"start": v(-18.75, 36.74) * mm, "end": v(-18.92, 36.74) * mm});
            skLineSegment(sketch, "E777", {"start": v(-18.92, 36.74) * mm, "end": v(-19.09, 36.74) * mm});
            skLineSegment(sketch, "E778", {"start": v(-19.09, 36.74) * mm, "end": v(-19.25, 36.74) * mm});
            skLineSegment(sketch, "E779", {"start": v(-19.25, 36.74) * mm, "end": v(-19.42, 36.74) * mm});
            skLineSegment(sketch, "E780", {"start": v(-19.42, 36.74) * mm, "end": v(-19.59, 36.74) * mm});
            skLineSegment(sketch, "E781", {"start": v(-19.59, 36.74) * mm, "end": v(-19.75, 36.74) * mm});
            skLineSegment(sketch, "E782", {"start": v(-19.75, 36.74) * mm, "end": v(-19.92, 36.74) * mm});
            skLineSegment(sketch, "E783", {"start": v(-19.92, 36.74) * mm, "end": v(-20.09, 36.74) * mm});
            skLineSegment(sketch, "E784", {"start": v(-20.09, 36.74) * mm, "end": v(-20.25, 36.74) * mm});
            skLineSegment(sketch, "E785", {"start": v(-20.25, 36.74) * mm, "end": v(-20.42, 36.74) * mm});
            skLineSegment(sketch, "E786", {"start": v(-20.42, 36.74) * mm, "end": v(-20.59, 36.74) * mm});
            skLineSegment(sketch, "E787", {"start": v(-20.59, 36.74) * mm, "end": v(-20.76, 36.74) * mm});
            skLineSegment(sketch, "E788", {"start": v(-20.76, 36.74) * mm, "end": v(-20.92, 36.74) * mm});
            skLineSegment(sketch, "E789", {"start": v(-20.92, 36.74) * mm, "end": v(-21.09, 36.74) * mm});
            skLineSegment(sketch, "E790", {"start": v(-21.09, 36.74) * mm, "end": v(-21.26, 36.74) * mm});
            skLineSegment(sketch, "E791", {"start": v(-21.26, 36.74) * mm, "end": v(-21.42, 36.74) * mm});
            skLineSegment(sketch, "E792", {"start": v(-21.42, 36.74) * mm, "end": v(-21.59, 36.74) * mm});
            skLineSegment(sketch, "E793", {"start": v(-21.59, 36.74) * mm, "end": v(-21.76, 36.74) * mm});
            skLineSegment(sketch, "E794", {"start": v(-21.76, 36.74) * mm, "end": v(-21.92, 36.74) * mm});
            skLineSegment(sketch, "E795", {"start": v(-21.92, 36.74) * mm, "end": v(-22.1, 36.74) * mm});
            skLineSegment(sketch, "E796", {"start": v(-22.1, 36.74) * mm, "end": v(-22.26, 36.74) * mm});
            skLineSegment(sketch, "E797", {"start": v(-22.26, 36.74) * mm, "end": v(-22.42, 36.74) * mm});
            skLineSegment(sketch, "E798", {"start": v(-22.42, 36.74) * mm, "end": v(-22.6, 36.74) * mm});
            skLineSegment(sketch, "E799", {"start": v(-22.6, 36.74) * mm, "end": v(-22.76, 36.74) * mm});
            skLineSegment(sketch, "E800", {"start": v(-22.76, 36.74) * mm, "end": v(-22.93, 36.74) * mm});
            skLineSegment(sketch, "E801", {"start": v(-22.93, 36.74) * mm, "end": v(-23.1, 36.74) * mm});
            skLineSegment(sketch, "E802", {"start": v(-23.1, 36.74) * mm, "end": v(-23.26, 36.74) * mm});
            skLineSegment(sketch, "E803", {"start": v(-23.26, 36.74) * mm, "end": v(-23.43, 36.74) * mm});
            skLineSegment(sketch, "E804", {"start": v(-23.43, 36.74) * mm, "end": v(-23.6, 36.74) * mm});
            skLineSegment(sketch, "E805", {"start": v(-23.6, 36.74) * mm, "end": v(-23.76, 36.74) * mm});
            skLineSegment(sketch, "E806", {"start": v(-23.76, 36.74) * mm, "end": v(-23.93, 36.74) * mm});
            skLineSegment(sketch, "E807", {"start": v(-23.93, 36.74) * mm, "end": v(-24.1, 36.74) * mm});
            skLineSegment(sketch, "E808", {"start": v(-24.1, 36.74) * mm, "end": v(-24.26, 36.74) * mm});
            skLineSegment(sketch, "E809", {"start": v(-24.26, 36.74) * mm, "end": v(-24.43, 36.74) * mm});
            skLineSegment(sketch, "E810", {"start": v(-24.43, 36.74) * mm, "end": v(-24.6, 36.74) * mm});
            skLineSegment(sketch, "E811", {"start": v(-24.6, 36.74) * mm, "end": v(-24.76, 36.74) * mm});
            skLineSegment(sketch, "E812", {"start": v(-24.76, 36.74) * mm, "end": v(-24.93, 36.74) * mm});
            skLineSegment(sketch, "E813", {"start": v(-24.93, 36.74) * mm, "end": v(-25.1, 36.74) * mm});
            skLineSegment(sketch, "E814", {"start": v(-25.1, 36.74) * mm, "end": v(-25.26, 36.74) * mm});
            skLineSegment(sketch, "E815", {"start": v(-25.26, 36.74) * mm, "end": v(-25.43, 36.74) * mm});
            skLineSegment(sketch, "E816", {"start": v(-25.43, 36.74) * mm, "end": v(-25.6, 36.74) * mm});
            skLineSegment(sketch, "E817", {"start": v(-25.6, 36.74) * mm, "end": v(-25.76, 36.74) * mm});
            skLineSegment(sketch, "E818", {"start": v(-25.76, 36.74) * mm, "end": v(-25.93, 36.74) * mm});
            skLineSegment(sketch, "E819", {"start": v(-25.93, 36.74) * mm, "end": v(-26.1, 36.74) * mm});
            skLineSegment(sketch, "E820", {"start": v(-26.1, 36.74) * mm, "end": v(-26.26, 36.74) * mm});
            skLineSegment(sketch, "E821", {"start": v(-26.26, 36.74) * mm, "end": v(-26.43, 36.74) * mm});
            skLineSegment(sketch, "E822", {"start": v(-26.43, 36.74) * mm, "end": v(-26.6, 36.74) * mm});
            skLineSegment(sketch, "E823", {"start": v(-26.6, 36.74) * mm, "end": v(-26.77, 36.74) * mm});
            skLineSegment(sketch, "E824", {"start": v(-26.77, 36.74) * mm, "end": v(-26.93, 36.74) * mm});
            skLineSegment(sketch, "E825", {"start": v(-26.93, 36.74) * mm, "end": v(-27.1, 36.74) * mm});
            skLineSegment(sketch, "E826", {"start": v(-27.1, 36.74) * mm, "end": v(-27.27, 36.74) * mm});
            skLineSegment(sketch, "E827", {"start": v(-27.27, 36.74) * mm, "end": v(-27.43, 36.74) * mm});
            skLineSegment(sketch, "E828", {"start": v(-27.43, 36.74) * mm, "end": v(-27.6, 36.74) * mm});
            skLineSegment(sketch, "E829", {"start": v(-27.6, 36.74) * mm, "end": v(-27.77, 36.74) * mm});
            skLineSegment(sketch, "E830", {"start": v(-27.77, 36.74) * mm, "end": v(-27.93, 36.74) * mm});
            skLineSegment(sketch, "E831", {"start": v(-27.93, 36.74) * mm, "end": v(-28.1, 36.74) * mm});
            skLineSegment(sketch, "E832", {"start": v(-28.1, 36.74) * mm, "end": v(-28.27, 36.74) * mm});
            skLineSegment(sketch, "E833", {"start": v(-28.27, 36.74) * mm, "end": v(-28.43, 36.74) * mm});
            skLineSegment(sketch, "E834", {"start": v(-28.43, 36.74) * mm, "end": v(-28.6, 36.74) * mm});
            skLineSegment(sketch, "E835", {"start": v(-28.6, 36.74) * mm, "end": v(-28.77, 36.74) * mm});
            skLineSegment(sketch, "E836", {"start": v(-28.77, 36.74) * mm, "end": v(-28.94, 36.74) * mm});
            skLineSegment(sketch, "E837", {"start": v(-28.94, 36.74) * mm, "end": v(-29.1, 36.74) * mm});
            skLineSegment(sketch, "E838", {"start": v(-29.1, 36.74) * mm, "end": v(-29.27, 36.74) * mm});
            skLineSegment(sketch, "E839", {"start": v(-29.27, 36.74) * mm, "end": v(-29.44, 36.74) * mm});
            skLineSegment(sketch, "E840", {"start": v(-29.44, 36.74) * mm, "end": v(-29.6, 36.74) * mm});
            skLineSegment(sketch, "E841", {"start": v(-29.6, 36.74) * mm, "end": v(-29.77, 36.74) * mm});
            skLineSegment(sketch, "E842", {"start": v(-29.77, 36.74) * mm, "end": v(-29.94, 36.74) * mm});
            skLineSegment(sketch, "E843", {"start": v(-29.94, 36.74) * mm, "end": v(-30.1, 36.74) * mm});
            skLineSegment(sketch, "E844", {"start": v(-30.1, 36.74) * mm, "end": v(-30.27, 36.74) * mm});
            skLineSegment(sketch, "E845", {"start": v(-30.27, 36.74) * mm, "end": v(-30.44, 36.74) * mm});
            skLineSegment(sketch, "E846", {"start": v(-30.44, 36.74) * mm, "end": v(-30.6, 36.74) * mm});
            skLineSegment(sketch, "E847", {"start": v(-30.6, 36.74) * mm, "end": v(-30.77, 36.74) * mm});
            skLineSegment(sketch, "E848", {"start": v(-30.77, 36.74) * mm, "end": v(-30.94, 36.74) * mm});
            skLineSegment(sketch, "E849", {"start": v(-30.94, 36.74) * mm, "end": v(-31.1, 36.74) * mm});
            skLineSegment(sketch, "E850", {"start": v(-31.1, 36.74) * mm, "end": v(-31.27, 36.74) * mm});
            skLineSegment(sketch, "E851", {"start": v(-31.27, 36.74) * mm, "end": v(-31.44, 36.74) * mm});
            skLineSegment(sketch, "E852", {"start": v(-31.44, 36.74) * mm, "end": v(-31.6, 36.74) * mm});
            skLineSegment(sketch, "E853", {"start": v(-31.6, 36.74) * mm, "end": v(-31.77, 36.74) * mm});
            skLineSegment(sketch, "E854", {"start": v(-31.77, 36.74) * mm, "end": v(-31.94, 36.74) * mm});
            skLineSegment(sketch, "E855", {"start": v(-31.94, 36.74) * mm, "end": v(-32.1, 36.74) * mm});
            skLineSegment(sketch, "E856", {"start": v(-32.1, 36.74) * mm, "end": v(-32.27, 36.74) * mm});
            skLineSegment(sketch, "E857", {"start": v(-32.27, 36.74) * mm, "end": v(-32.44, 36.74) * mm});
            skLineSegment(sketch, "E858", {"start": v(-32.44, 36.74) * mm, "end": v(-32.6, 36.74) * mm});
            skLineSegment(sketch, "E859", {"start": v(-32.6, 36.74) * mm, "end": v(-32.78, 36.74) * mm});
            skLineSegment(sketch, "E860", {"start": v(-32.78, 36.74) * mm, "end": v(-32.94, 36.74) * mm});
            skLineSegment(sketch, "E861", {"start": v(-32.94, 36.74) * mm, "end": v(-33.1, 36.74) * mm});
            skLineSegment(sketch, "E862", {"start": v(-33.1, 36.74) * mm, "end": v(-33.28, 36.74) * mm});
            skLineSegment(sketch, "E863", {"start": v(-33.28, 36.74) * mm, "end": v(-33.44, 36.74) * mm});
            skLineSegment(sketch, "E864", {"start": v(-33.44, 36.74) * mm, "end": v(-33.6, 36.74) * mm});
            skLineSegment(sketch, "E865", {"start": v(-33.6, 36.74) * mm, "end": v(-33.78, 36.74) * mm});
            skLineSegment(sketch, "E866", {"start": v(-33.78, 36.74) * mm, "end": v(-33.94, 36.74) * mm});
            skLineSegment(sketch, "E867", {"start": v(-33.94, 36.74) * mm, "end": v(-34.11, 36.74) * mm});
            skLineSegment(sketch, "E868", {"start": v(-34.11, 36.74) * mm, "end": v(-34.28, 36.74) * mm});
            skLineSegment(sketch, "E869", {"start": v(-34.28, 36.74) * mm, "end": v(-34.44, 36.74) * mm});
            skLineSegment(sketch, "E870", {"start": v(-34.44, 36.74) * mm, "end": v(-34.61, 36.74) * mm});
            skLineSegment(sketch, "E871", {"start": v(-34.61, 36.74) * mm, "end": v(-34.78, 36.74) * mm});
            skLineSegment(sketch, "E872", {"start": v(-34.78, 36.74) * mm, "end": v(-34.95, 36.74) * mm});
            skLineSegment(sketch, "E873", {"start": v(-34.95, 36.74) * mm, "end": v(-35.11, 36.74) * mm});
            skLineSegment(sketch, "E874", {"start": v(-35.11, 36.74) * mm, "end": v(-35.28, 36.74) * mm});
            skLineSegment(sketch, "E875", {"start": v(-35.28, 36.74) * mm, "end": v(-35.45, 36.74) * mm});
            skLineSegment(sketch, "E876", {"start": v(-35.45, 36.74) * mm, "end": v(-35.61, 36.74) * mm});
            skLineSegment(sketch, "E877", {"start": v(-35.61, 36.74) * mm, "end": v(-35.78, 36.74) * mm});
            skLineSegment(sketch, "E878", {"start": v(-35.78, 36.74) * mm, "end": v(-35.95, 36.74) * mm});
            skLineSegment(sketch, "E879", {"start": v(-35.95, 36.74) * mm, "end": v(-36.11, 36.74) * mm});
            skLineSegment(sketch, "E880", {"start": v(-36.11, 36.74) * mm, "end": v(-36.28, 36.74) * mm});
            skLineSegment(sketch, "E881", {"start": v(-36.28, 36.74) * mm, "end": v(-36.45, 36.74) * mm});
            skLineSegment(sketch, "E882", {"start": v(-36.45, 36.74) * mm, "end": v(-36.61, 36.74) * mm});
            skLineSegment(sketch, "E883", {"start": v(-36.61, 36.74) * mm, "end": v(-36.78, 36.74) * mm});
            skLineSegment(sketch, "E884", {"start": v(-36.78, 36.74) * mm, "end": v(-36.95, 36.74) * mm});
            skLineSegment(sketch, "E885", {"start": v(-36.95, 36.74) * mm, "end": v(-37.12, 36.74) * mm});
            skLineSegment(sketch, "E886", {"start": v(-37.12, 36.74) * mm, "end": v(-37.28, 36.74) * mm});
            skLineSegment(sketch, "E887", {"start": v(-37.28, 36.74) * mm, "end": v(-37.45, 36.74) * mm});
            skLineSegment(sketch, "E888", {"start": v(-37.45, 36.74) * mm, "end": v(-37.62, 36.74) * mm});
            skLineSegment(sketch, "E889", {"start": v(-37.62, 36.74) * mm, "end": v(-37.78, 36.74) * mm});
            skLineSegment(sketch, "E890", {"start": v(-37.78, 36.74) * mm, "end": v(-37.95, 36.74) * mm});
            skLineSegment(sketch, "E891", {"start": v(-37.95, 36.74) * mm, "end": v(-38.12, 36.74) * mm});
            skLineSegment(sketch, "E892", {"start": v(-38.12, 36.74) * mm, "end": v(-38.28, 36.74) * mm});
            skLineSegment(sketch, "E893", {"start": v(-38.28, 36.74) * mm, "end": v(-38.45, 36.74) * mm});
            skLineSegment(sketch, "E894", {"start": v(-38.45, 36.74) * mm, "end": v(-38.62, 36.74) * mm});
            skLineSegment(sketch, "E895", {"start": v(-38.62, 36.74) * mm, "end": v(-38.79, 36.74) * mm});
            skLineSegment(sketch, "E896", {"start": v(-38.79, 36.74) * mm, "end": v(-38.81, 36.7) * mm});
            skLineSegment(sketch, "E897", {"start": v(-38.81, 36.7) * mm, "end": v(-38.84, 36.64) * mm});
            skLineSegment(sketch, "E898", {"start": v(-38.84, 36.64) * mm, "end": v(-38.86, 36.59) * mm});
            skLineSegment(sketch, "E899", {"start": v(-38.86, 36.59) * mm, "end": v(-38.89, 36.54) * mm});
            skLineSegment(sketch, "E900", {"start": v(-38.89, 36.54) * mm, "end": v(-38.91, 36.49) * mm});
            skLineSegment(sketch, "E901", {"start": v(-38.91, 36.49) * mm, "end": v(-38.94, 36.43) * mm});
            skLineSegment(sketch, "E902", {"start": v(-38.94, 36.43) * mm, "end": v(-38.96, 36.38) * mm});
            skLineSegment(sketch, "E903", {"start": v(-38.96, 36.38) * mm, "end": v(-38.99, 36.33) * mm});
            skLineSegment(sketch, "E904", {"start": v(-38.99, 36.33) * mm, "end": v(-39.01, 36.28) * mm});
            skLineSegment(sketch, "E905", {"start": v(-39.01, 36.28) * mm, "end": v(-39.04, 36.23) * mm});
            skLineSegment(sketch, "E906", {"start": v(-39.04, 36.23) * mm, "end": v(-39.07, 36.17) * mm});
            skLineSegment(sketch, "E907", {"start": v(-39.07, 36.17) * mm, "end": v(-39.1, 36.12) * mm});
            skLineSegment(sketch, "E908", {"start": v(-39.1, 36.12) * mm, "end": v(-39.12, 36.07) * mm});
            skLineSegment(sketch, "E909", {"start": v(-39.12, 36.07) * mm, "end": v(-39.14, 36.02) * mm});
            skLineSegment(sketch, "E910", {"start": v(-39.14, 36.02) * mm, "end": v(-39.17, 35.97) * mm});
            skLineSegment(sketch, "E911", {"start": v(-39.17, 35.97) * mm, "end": v(-39.2, 35.91) * mm});
            skLineSegment(sketch, "E912", {"start": v(-39.2, 35.91) * mm, "end": v(-39.22, 35.86) * mm});
            skLineSegment(sketch, "E913", {"start": v(-39.22, 35.86) * mm, "end": v(-39.24, 35.81) * mm});
            skLineSegment(sketch, "E914", {"start": v(-39.24, 35.81) * mm, "end": v(-39.27, 35.76) * mm});
            skLineSegment(sketch, "E915", {"start": v(-39.27, 35.76) * mm, "end": v(-39.3, 35.7) * mm});
            skLineSegment(sketch, "E916", {"start": v(-39.3, 35.7) * mm, "end": v(-39.32, 35.66) * mm});
            skLineSegment(sketch, "E917", {"start": v(-39.32, 35.66) * mm, "end": v(-39.35, 35.6) * mm});
            skLineSegment(sketch, "E918", {"start": v(-39.35, 35.6) * mm, "end": v(-39.37, 35.55) * mm});
            skLineSegment(sketch, "E919", {"start": v(-39.37, 35.55) * mm, "end": v(-39.4, 35.5) * mm});
            skLineSegment(sketch, "E920", {"start": v(-39.4, 35.5) * mm, "end": v(-39.42, 35.45) * mm});
            skLineSegment(sketch, "E921", {"start": v(-39.42, 35.45) * mm, "end": v(-39.45, 35.4) * mm});
            skLineSegment(sketch, "E922", {"start": v(-39.45, 35.4) * mm, "end": v(-39.47, 35.34) * mm});
            skLineSegment(sketch, "E923", {"start": v(-39.47, 35.34) * mm, "end": v(-39.5, 35.3) * mm});
            skLineSegment(sketch, "E924", {"start": v(-39.5, 35.3) * mm, "end": v(-39.53, 35.24) * mm});
            skLineSegment(sketch, "E925", {"start": v(-39.53, 35.24) * mm, "end": v(-39.55, 35.19) * mm});
            skLineSegment(sketch, "E926", {"start": v(-39.55, 35.19) * mm, "end": v(-39.58, 35.14) * mm});
            skLineSegment(sketch, "E927", {"start": v(-39.58, 35.14) * mm, "end": v(-39.6, 35.09) * mm});
            skLineSegment(sketch, "E928", {"start": v(-39.6, 35.09) * mm, "end": v(-39.63, 35.03) * mm});
            skLineSegment(sketch, "E929", {"start": v(-39.63, 35.03) * mm, "end": v(-39.65, 34.98) * mm});
            skLineSegment(sketch, "E930", {"start": v(-39.65, 34.98) * mm, "end": v(-39.68, 34.93) * mm});
            skLineSegment(sketch, "E931", {"start": v(-39.68, 34.93) * mm, "end": v(-39.7, 34.88) * mm});
            skLineSegment(sketch, "E932", {"start": v(-39.7, 34.88) * mm, "end": v(-39.73, 34.83) * mm});
            skLineSegment(sketch, "E933", {"start": v(-39.73, 34.83) * mm, "end": v(-39.76, 34.77) * mm});
            skLineSegment(sketch, "E934", {"start": v(-39.76, 34.77) * mm, "end": v(-39.78, 34.72) * mm});
            skLineSegment(sketch, "E935", {"start": v(-39.78, 34.72) * mm, "end": v(-39.8, 34.67) * mm});
            skLineSegment(sketch, "E936", {"start": v(-39.8, 34.67) * mm, "end": v(-39.83, 34.62) * mm});
            skLineSegment(sketch, "E937", {"start": v(-39.83, 34.62) * mm, "end": v(-39.86, 34.57) * mm});
            skLineSegment(sketch, "E938", {"start": v(-39.86, 34.57) * mm, "end": v(-39.88, 34.52) * mm});
            skLineSegment(sketch, "E939", {"start": v(-39.88, 34.52) * mm, "end": v(-39.9, 34.46) * mm});
            skLineSegment(sketch, "E940", {"start": v(-39.9, 34.46) * mm, "end": v(-39.93, 34.41) * mm});
            skLineSegment(sketch, "E941", {"start": v(-39.93, 34.41) * mm, "end": v(-39.96, 34.36) * mm});
            skLineSegment(sketch, "E942", {"start": v(-39.96, 34.36) * mm, "end": v(-39.99, 34.3) * mm});
            skLineSegment(sketch, "E943", {"start": v(-39.99, 34.3) * mm, "end": v(-40.01, 34.26) * mm});
            skLineSegment(sketch, "E944", {"start": v(-40.01, 34.26) * mm, "end": v(-40.04, 34.2) * mm});
            skLineSegment(sketch, "E945", {"start": v(-40.04, 34.2) * mm, "end": v(-40.06, 34.15) * mm});
            skLineSegment(sketch, "E946", {"start": v(-40.06, 34.15) * mm, "end": v(-40.09, 34.1) * mm});
            skLineSegment(sketch, "E947", {"start": v(-40.09, 34.1) * mm, "end": v(-40.11, 34.05) * mm});
            skLineSegment(sketch, "E948", {"start": v(-40.11, 34.05) * mm, "end": v(-40.14, 34) * mm});
            skLineSegment(sketch, "E949", {"start": v(-40.14, 34) * mm, "end": v(-40.16, 33.94) * mm});
            skLineSegment(sketch, "E950", {"start": v(-40.16, 33.94) * mm, "end": v(-40.2, 33.9) * mm});
            skLineSegment(sketch, "E951", {"start": v(-40.2, 33.9) * mm, "end": v(-40.22, 33.84) * mm});
            skLineSegment(sketch, "E952", {"start": v(-40.22, 33.84) * mm, "end": v(-40.24, 33.79) * mm});
            skLineSegment(sketch, "E953", {"start": v(-40.24, 33.79) * mm, "end": v(-40.27, 33.74) * mm});
            skLineSegment(sketch, "E954", {"start": v(-40.27, 33.74) * mm, "end": v(-40.3, 33.69) * mm});
            skLineSegment(sketch, "E955", {"start": v(-40.3, 33.69) * mm, "end": v(-40.32, 33.63) * mm});
            skLineSegment(sketch, "E956", {"start": v(-40.32, 33.63) * mm, "end": v(-40.34, 33.58) * mm});
            skLineSegment(sketch, "E957", {"start": v(-40.34, 33.58) * mm, "end": v(-40.37, 33.53) * mm});
            skLineSegment(sketch, "E958", {"start": v(-40.37, 33.53) * mm, "end": v(-40.4, 33.48) * mm});
            skLineSegment(sketch, "E959", {"start": v(-40.4, 33.48) * mm, "end": v(-40.42, 33.43) * mm});
            skLineSegment(sketch, "E960", {"start": v(-40.42, 33.43) * mm, "end": v(-40.45, 33.37) * mm});
            skLineSegment(sketch, "E961", {"start": v(-40.45, 33.37) * mm, "end": v(-40.47, 33.32) * mm});
            skLineSegment(sketch, "E962", {"start": v(-40.47, 33.32) * mm, "end": v(-40.5, 33.27) * mm});
            skLineSegment(sketch, "E963", {"start": v(-40.5, 33.27) * mm, "end": v(-40.52, 33.22) * mm});
            skLineSegment(sketch, "E964", {"start": v(-40.52, 33.22) * mm, "end": v(-40.55, 33.17) * mm});
            skLineSegment(sketch, "E965", {"start": v(-40.55, 33.17) * mm, "end": v(-40.57, 33.12) * mm});
            skLineSegment(sketch, "E966", {"start": v(-40.57, 33.12) * mm, "end": v(-40.6, 33.06) * mm});
            skLineSegment(sketch, "E967", {"start": v(-40.6, 33.06) * mm, "end": v(-40.62, 33.01) * mm});
            skLineSegment(sketch, "E968", {"start": v(-40.62, 33.01) * mm, "end": v(-40.65, 32.96) * mm});
            skLineSegment(sketch, "E969", {"start": v(-40.65, 32.96) * mm, "end": v(-40.68, 32.9) * mm});
            skLineSegment(sketch, "E970", {"start": v(-40.68, 32.9) * mm, "end": v(-40.7, 32.86) * mm});
            skLineSegment(sketch, "E971", {"start": v(-40.7, 32.86) * mm, "end": v(-40.73, 32.8) * mm});
            skLineSegment(sketch, "E972", {"start": v(-40.73, 32.8) * mm, "end": v(-40.75, 32.75) * mm});
            skLineSegment(sketch, "E973", {"start": v(-40.75, 32.75) * mm, "end": v(-40.78, 32.7) * mm});
            skLineSegment(sketch, "E974", {"start": v(-40.78, 32.7) * mm, "end": v(-40.8, 32.65) * mm});
            skLineSegment(sketch, "E975", {"start": v(-40.8, 32.65) * mm, "end": v(-40.83, 32.6) * mm});
            skLineSegment(sketch, "E976", {"start": v(-40.83, 32.6) * mm, "end": v(-40.85, 32.55) * mm});
            skLineSegment(sketch, "E977", {"start": v(-40.85, 32.55) * mm, "end": v(-40.88, 32.5) * mm});
            skLineSegment(sketch, "E978", {"start": v(-40.88, 32.5) * mm, "end": v(-40.9, 32.44) * mm});
            skLineSegment(sketch, "E979", {"start": v(-40.9, 32.44) * mm, "end": v(-40.93, 32.39) * mm});
            skLineSegment(sketch, "E980", {"start": v(-40.93, 32.39) * mm, "end": v(-40.96, 32.34) * mm});
            skLineSegment(sketch, "E981", {"start": v(-40.96, 32.34) * mm, "end": v(-40.98, 32.29) * mm});
            skLineSegment(sketch, "E982", {"start": v(-40.98, 32.29) * mm, "end": v(-41, 32.23) * mm});
            skLineSegment(sketch, "E983", {"start": v(-41, 32.23) * mm, "end": v(-41.03, 32.18) * mm});
            skLineSegment(sketch, "E984", {"start": v(-41.03, 32.18) * mm, "end": v(-41.06, 32.13) * mm});
            skLineSegment(sketch, "E985", {"start": v(-41.06, 32.13) * mm, "end": v(-41.08, 32.08) * mm});
            skLineSegment(sketch, "E986", {"start": v(-41.08, 32.08) * mm, "end": v(-41.1, 32.03) * mm});
            skLineSegment(sketch, "E987", {"start": v(-41.1, 32.03) * mm, "end": v(-41.14, 31.97) * mm});
            skLineSegment(sketch, "E988", {"start": v(-41.14, 31.97) * mm, "end": v(-41.16, 31.92) * mm});
            skLineSegment(sketch, "E989", {"start": v(-41.16, 31.92) * mm, "end": v(-41.19, 31.87) * mm});
            skLineSegment(sketch, "E990", {"start": v(-41.19, 31.87) * mm, "end": v(-41.21, 31.82) * mm});
            skLineSegment(sketch, "E991", {"start": v(-41.21, 31.82) * mm, "end": v(-41.24, 31.77) * mm});
            skLineSegment(sketch, "E992", {"start": v(-41.24, 31.77) * mm, "end": v(-41.26, 31.72) * mm});
            skLineSegment(sketch, "E993", {"start": v(-41.26, 31.72) * mm, "end": v(-41.29, 31.66) * mm});
            skLineSegment(sketch, "E994", {"start": v(-41.29, 31.66) * mm, "end": v(-41.31, 31.61) * mm});
            skLineSegment(sketch, "E995", {"start": v(-41.31, 31.61) * mm, "end": v(-41.34, 31.56) * mm});
            skLineSegment(sketch, "E996", {"start": v(-41.34, 31.56) * mm, "end": v(-41.37, 31.5) * mm});
            skLineSegment(sketch, "E997", {"start": v(-41.37, 31.5) * mm, "end": v(-41.4, 31.46) * mm});
            skLineSegment(sketch, "E998", {"start": v(-41.4, 31.46) * mm, "end": v(-41.42, 31.4) * mm});
            skLineSegment(sketch, "E999", {"start": v(-41.42, 31.4) * mm, "end": v(-41.44, 31.35) * mm});
            skLineSegment(sketch, "E1000", {"start": v(-41.44, 31.35) * mm, "end": v(-41.47, 31.3) * mm});
            skLineSegment(sketch, "E1001", {"start": v(-41.47, 31.3) * mm, "end": v(-41.5, 31.25) * mm});
            skLineSegment(sketch, "E1002", {"start": v(-41.5, 31.25) * mm, "end": v(-41.52, 31.2) * mm});
            skLineSegment(sketch, "E1003", {"start": v(-41.52, 31.2) * mm, "end": v(-41.54, 31.15) * mm});
            skLineSegment(sketch, "E1004", {"start": v(-41.54, 31.15) * mm, "end": v(-41.57, 31.1) * mm});
            skLineSegment(sketch, "E1005", {"start": v(-41.57, 31.1) * mm, "end": v(-41.6, 31.04) * mm});
            skLineSegment(sketch, "E1006", {"start": v(-41.6, 31.04) * mm, "end": v(-41.62, 30.99) * mm});
            skLineSegment(sketch, "E1007", {"start": v(-41.62, 30.99) * mm, "end": v(-41.65, 30.94) * mm});
            skLineSegment(sketch, "E1008", {"start": v(-41.65, 30.94) * mm, "end": v(-41.67, 30.89) * mm});
            skLineSegment(sketch, "E1009", {"start": v(-41.67, 30.89) * mm, "end": v(-41.7, 30.83) * mm});
            skLineSegment(sketch, "E1010", {"start": v(-41.7, 30.83) * mm, "end": v(-41.72, 30.78) * mm});
            skLineSegment(sketch, "E1011", {"start": v(-41.72, 30.78) * mm, "end": v(-41.75, 30.73) * mm});
            skLineSegment(sketch, "E1012", {"start": v(-41.75, 30.73) * mm, "end": v(-41.77, 30.68) * mm});
            skLineSegment(sketch, "E1013", {"start": v(-41.77, 30.68) * mm, "end": v(-41.8, 30.63) * mm});
            skLineSegment(sketch, "E1014", {"start": v(-41.8, 30.63) * mm, "end": v(-41.83, 30.57) * mm});
            skLineSegment(sketch, "E1015", {"start": v(-41.83, 30.57) * mm, "end": v(-41.85, 30.52) * mm});
            skLineSegment(sketch, "E1016", {"start": v(-41.85, 30.52) * mm, "end": v(-41.88, 30.47) * mm});
            skLineSegment(sketch, "E1017", {"start": v(-41.88, 30.47) * mm, "end": v(-41.9, 30.42) * mm});
            skLineSegment(sketch, "E1018", {"start": v(-41.9, 30.42) * mm, "end": v(-41.93, 30.37) * mm});
            skLineSegment(sketch, "E1019", {"start": v(-41.93, 30.37) * mm, "end": v(-41.95, 30.32) * mm});
            skLineSegment(sketch, "E1020", {"start": v(-41.95, 30.32) * mm, "end": v(-41.98, 30.26) * mm});
            skLineSegment(sketch, "E1021", {"start": v(-41.98, 30.26) * mm, "end": v(-42, 30.21) * mm});
            skLineSegment(sketch, "E1022", {"start": v(-42, 30.21) * mm, "end": v(-42.03, 30.16) * mm});
            skLineSegment(sketch, "E1023", {"start": v(-42.03, 30.16) * mm, "end": v(-42.06, 30.1) * mm});
            skLineSegment(sketch, "E1024", {"start": v(-42.06, 30.1) * mm, "end": v(-41.92, 30.1) * mm});
            skLineSegment(sketch, "E1025", {"start": v(-41.92, 30.1) * mm, "end": v(-41.8, 30.1) * mm});
            skLineSegment(sketch, "E1026", {"start": v(-41.8, 30.1) * mm, "end": v(-41.66, 30.1) * mm});
            skLineSegment(sketch, "E1027", {"start": v(-41.66, 30.1) * mm, "end": v(-41.53, 30.1) * mm});
            skLineSegment(sketch, "E1028", {"start": v(-41.53, 30.1) * mm, "end": v(-41.4, 30.1) * mm});
            skLineSegment(sketch, "E1029", {"start": v(-41.4, 30.1) * mm, "end": v(-41.27, 30.1) * mm});
            skLineSegment(sketch, "E1030", {"start": v(-41.27, 30.1) * mm, "end": v(-41.13, 30.1) * mm});
            skLineSegment(sketch, "E1031", {"start": v(-41.13, 30.1) * mm, "end": v(-41, 30.1) * mm});
            skLineSegment(sketch, "E1032", {"start": v(-41, 30.1) * mm, "end": v(-40.87, 30.1) * mm});
            skLineSegment(sketch, "E1033", {"start": v(-40.87, 30.1) * mm, "end": v(-40.74, 30.1) * mm});
            skLineSegment(sketch, "E1034", {"start": v(-40.74, 30.1) * mm, "end": v(-40.6, 30.1) * mm});
            skLineSegment(sketch, "E1035", {"start": v(-40.6, 30.1) * mm, "end": v(-40.48, 30.1) * mm});
            skLineSegment(sketch, "E1036", {"start": v(-40.48, 30.1) * mm, "end": v(-40.35, 30.1) * mm});
            skLineSegment(sketch, "E1037", {"start": v(-40.35, 30.1) * mm, "end": v(-40.21, 30.1) * mm});
            skLineSegment(sketch, "E1038", {"start": v(-40.21, 30.1) * mm, "end": v(-40.08, 30.1) * mm});
            skLineSegment(sketch, "E1039", {"start": v(-40.08, 30.1) * mm, "end": v(-39.95, 30.1) * mm});
            skLineSegment(sketch, "E1040", {"start": v(-39.95, 30.1) * mm, "end": v(-39.82, 30.1) * mm});
            skLineSegment(sketch, "E1041", {"start": v(-39.82, 30.1) * mm, "end": v(-39.69, 30.1) * mm});
            skLineSegment(sketch, "E1042", {"start": v(-39.69, 30.1) * mm, "end": v(-39.56, 30.1) * mm});
            skLineSegment(sketch, "E1043", {"start": v(-39.56, 30.1) * mm, "end": v(-39.43, 30.1) * mm});
            skLineSegment(sketch, "E1044", {"start": v(-39.43, 30.1) * mm, "end": v(-39.3, 30.1) * mm});
            skLineSegment(sketch, "E1045", {"start": v(-39.3, 30.1) * mm, "end": v(-39.16, 30.1) * mm});
            skLineSegment(sketch, "E1046", {"start": v(-39.16, 30.1) * mm, "end": v(-39.03, 30.1) * mm});
            skLineSegment(sketch, "E1047", {"start": v(-39.03, 30.1) * mm, "end": v(-38.9, 30.1) * mm});
            skLineSegment(sketch, "E1048", {"start": v(-38.9, 30.1) * mm, "end": v(-38.77, 30.1) * mm});
            skLineSegment(sketch, "E1049", {"start": v(-38.77, 30.1) * mm, "end": v(-38.64, 30.1) * mm});
            skLineSegment(sketch, "E1050", {"start": v(-38.64, 30.1) * mm, "end": v(-38.5, 30.1) * mm});
            skLineSegment(sketch, "E1051", {"start": v(-38.5, 30.1) * mm, "end": v(-38.37, 30.1) * mm});
            skLineSegment(sketch, "E1052", {"start": v(-38.37, 30.1) * mm, "end": v(-38.24, 30.1) * mm});
            skLineSegment(sketch, "E1053", {"start": v(-38.24, 30.1) * mm, "end": v(-38.11, 30.1) * mm});
            skLineSegment(sketch, "E1054", {"start": v(-38.11, 30.1) * mm, "end": v(-37.98, 30.1) * mm});
            skLineSegment(sketch, "E1055", {"start": v(-37.98, 30.1) * mm, "end": v(-37.85, 30.1) * mm});
            skLineSegment(sketch, "E1056", {"start": v(-37.85, 30.1) * mm, "end": v(-37.72, 30.1) * mm});
            skLineSegment(sketch, "E1057", {"start": v(-37.72, 30.1) * mm, "end": v(-37.58, 30.1) * mm});
            skLineSegment(sketch, "E1058", {"start": v(-37.58, 30.1) * mm, "end": v(-37.45, 30.1) * mm});
            skLineSegment(sketch, "E1059", {"start": v(-37.45, 30.1) * mm, "end": v(-37.32, 30.1) * mm});
            skLineSegment(sketch, "E1060", {"start": v(-37.32, 30.1) * mm, "end": v(-37.2, 30.1) * mm});
            skLineSegment(sketch, "E1061", {"start": v(-37.2, 30.1) * mm, "end": v(-37.06, 30.1) * mm});
            skLineSegment(sketch, "E1062", {"start": v(-37.06, 30.1) * mm, "end": v(-36.93, 30.1) * mm});
            skLineSegment(sketch, "E1063", {"start": v(-36.93, 30.1) * mm, "end": v(-36.8, 30.1) * mm});
            skLineSegment(sketch, "E1064", {"start": v(-36.8, 30.1) * mm, "end": v(-36.66, 30.1) * mm});
            skLineSegment(sketch, "E1065", {"start": v(-36.66, 30.1) * mm, "end": v(-36.53, 30.1) * mm});
            skLineSegment(sketch, "E1066", {"start": v(-36.53, 30.1) * mm, "end": v(-36.4, 30.1) * mm});
            skLineSegment(sketch, "E1067", {"start": v(-36.4, 30.1) * mm, "end": v(-36.27, 30.1) * mm});
            skLineSegment(sketch, "E1068", {"start": v(-36.27, 30.1) * mm, "end": v(-36.14, 30.1) * mm});
            skLineSegment(sketch, "E1069", {"start": v(-36.14, 30.1) * mm, "end": v(-36, 30.1) * mm});
            skLineSegment(sketch, "E1070", {"start": v(-36, 30.1) * mm, "end": v(-35.88, 30.1) * mm});
            skLineSegment(sketch, "E1071", {"start": v(-35.88, 30.1) * mm, "end": v(-35.74, 30.1) * mm});
            skLineSegment(sketch, "E1072", {"start": v(-35.74, 30.1) * mm, "end": v(-35.61, 30.1) * mm});
            skLineSegment(sketch, "E1073", {"start": v(-35.61, 30.1) * mm, "end": v(-35.48, 30.1) * mm});
            skLineSegment(sketch, "E1074", {"start": v(-35.48, 30.1) * mm, "end": v(-35.35, 30.1) * mm});
            skLineSegment(sketch, "E1075", {"start": v(-35.35, 30.1) * mm, "end": v(-35.22, 30.1) * mm});
            skLineSegment(sketch, "E1076", {"start": v(-35.22, 30.1) * mm, "end": v(-35.09, 30.1) * mm});
            skLineSegment(sketch, "E1077", {"start": v(-35.09, 30.1) * mm, "end": v(-34.96, 30.1) * mm});
            skLineSegment(sketch, "E1078", {"start": v(-34.96, 30.1) * mm, "end": v(-34.82, 30.1) * mm});
            skLineSegment(sketch, "E1079", {"start": v(-34.82, 30.1) * mm, "end": v(-34.7, 30.1) * mm});
            skLineSegment(sketch, "E1080", {"start": v(-34.7, 30.1) * mm, "end": v(-34.56, 30.1) * mm});
            skLineSegment(sketch, "E1081", {"start": v(-34.56, 30.1) * mm, "end": v(-34.43, 30.1) * mm});
            skLineSegment(sketch, "E1082", {"start": v(-34.43, 30.1) * mm, "end": v(-34.3, 30.1) * mm});
            skLineSegment(sketch, "E1083", {"start": v(-34.3, 30.1) * mm, "end": v(-34.17, 30.1) * mm});
            skLineSegment(sketch, "E1084", {"start": v(-34.17, 30.1) * mm, "end": v(-34.04, 30.1) * mm});
            skLineSegment(sketch, "E1085", {"start": v(-34.04, 30.1) * mm, "end": v(-33.9, 30.1) * mm});
            skLineSegment(sketch, "E1086", {"start": v(-33.9, 30.1) * mm, "end": v(-33.77, 30.1) * mm});
            skLineSegment(sketch, "E1087", {"start": v(-33.77, 30.1) * mm, "end": v(-33.64, 30.1) * mm});
            skLineSegment(sketch, "E1088", {"start": v(-33.64, 30.1) * mm, "end": v(-33.5, 30.1) * mm});
            skLineSegment(sketch, "E1089", {"start": v(-33.5, 30.1) * mm, "end": v(-33.38, 30.1) * mm});
            skLineSegment(sketch, "E1090", {"start": v(-33.38, 30.1) * mm, "end": v(-33.25, 30.1) * mm});
            skLineSegment(sketch, "E1091", {"start": v(-33.25, 30.1) * mm, "end": v(-33.11, 30.1) * mm});
            skLineSegment(sketch, "E1092", {"start": v(-33.11, 30.1) * mm, "end": v(-32.98, 30.1) * mm});
            skLineSegment(sketch, "E1093", {"start": v(-32.98, 30.1) * mm, "end": v(-32.85, 30.1) * mm});
            skLineSegment(sketch, "E1094", {"start": v(-32.85, 30.1) * mm, "end": v(-32.72, 30.1) * mm});
            skLineSegment(sketch, "E1095", {"start": v(-32.72, 30.1) * mm, "end": v(-32.59, 30.1) * mm});
            skLineSegment(sketch, "E1096", {"start": v(-32.59, 30.1) * mm, "end": v(-32.46, 30.1) * mm});
            skLineSegment(sketch, "E1097", {"start": v(-32.46, 30.1) * mm, "end": v(-32.33, 30.1) * mm});
            skLineSegment(sketch, "E1098", {"start": v(-32.33, 30.1) * mm, "end": v(-32.2, 30.1) * mm});
            skLineSegment(sketch, "E1099", {"start": v(-32.2, 30.1) * mm, "end": v(-32.06, 30.1) * mm});
            skLineSegment(sketch, "E1100", {"start": v(-32.06, 30.1) * mm, "end": v(-31.93, 30.1) * mm});
            skLineSegment(sketch, "E1101", {"start": v(-31.93, 30.1) * mm, "end": v(-31.8, 30.1) * mm});
            skLineSegment(sketch, "E1102", {"start": v(-31.8, 30.1) * mm, "end": v(-31.67, 30.1) * mm});
            skLineSegment(sketch, "E1103", {"start": v(-31.67, 30.1) * mm, "end": v(-31.54, 30.1) * mm});
            skLineSegment(sketch, "E1104", {"start": v(-31.54, 30.1) * mm, "end": v(-31.4, 30.1) * mm});
            skLineSegment(sketch, "E1105", {"start": v(-31.4, 30.1) * mm, "end": v(-31.27, 30.1) * mm});
            skLineSegment(sketch, "E1106", {"start": v(-31.27, 30.1) * mm, "end": v(-31.14, 30.1) * mm});
            skLineSegment(sketch, "E1107", {"start": v(-31.14, 30.1) * mm, "end": v(-31.01, 30.1) * mm});
            skLineSegment(sketch, "E1108", {"start": v(-31.01, 30.1) * mm, "end": v(-30.88, 30.1) * mm});
            skLineSegment(sketch, "E1109", {"start": v(-30.88, 30.1) * mm, "end": v(-30.75, 30.1) * mm});
            skLineSegment(sketch, "E1110", {"start": v(-30.75, 30.1) * mm, "end": v(-30.62, 30.1) * mm});
            skLineSegment(sketch, "E1111", {"start": v(-30.62, 30.1) * mm, "end": v(-30.49, 30.1) * mm});
            skLineSegment(sketch, "E1112", {"start": v(-30.49, 30.1) * mm, "end": v(-30.35, 30.1) * mm});
            skLineSegment(sketch, "E1113", {"start": v(-30.35, 30.1) * mm, "end": v(-30.22, 30.1) * mm});
            skLineSegment(sketch, "E1114", {"start": v(-30.22, 30.1) * mm, "end": v(-30.1, 30.1) * mm});
            skLineSegment(sketch, "E1115", {"start": v(-30.1, 30.1) * mm, "end": v(-29.96, 30.1) * mm});
            skLineSegment(sketch, "E1116", {"start": v(-29.96, 30.1) * mm, "end": v(-29.83, 30.1) * mm});
            skLineSegment(sketch, "E1117", {"start": v(-29.83, 30.1) * mm, "end": v(-29.7, 30.1) * mm});
            skLineSegment(sketch, "E1118", {"start": v(-29.7, 30.1) * mm, "end": v(-29.57, 30.1) * mm});
            skLineSegment(sketch, "E1119", {"start": v(-29.57, 30.1) * mm, "end": v(-29.43, 30.1) * mm});
            skLineSegment(sketch, "E1120", {"start": v(-29.43, 30.1) * mm, "end": v(-29.3, 30.1) * mm});
            skLineSegment(sketch, "E1121", {"start": v(-29.3, 30.1) * mm, "end": v(-29.17, 30.1) * mm});
            skLineSegment(sketch, "E1122", {"start": v(-29.17, 30.1) * mm, "end": v(-29.04, 30.1) * mm});
            skLineSegment(sketch, "E1123", {"start": v(-29.04, 30.1) * mm, "end": v(-28.9, 30.1) * mm});
            skLineSegment(sketch, "E1124", {"start": v(-28.9, 30.1) * mm, "end": v(-28.78, 30.1) * mm});
            skLineSegment(sketch, "E1125", {"start": v(-28.78, 30.1) * mm, "end": v(-28.64, 30.1) * mm});
            skLineSegment(sketch, "E1126", {"start": v(-28.64, 30.1) * mm, "end": v(-28.51, 30.1) * mm});
            skLineSegment(sketch, "E1127", {"start": v(-28.51, 30.1) * mm, "end": v(-28.38, 30.1) * mm});
            skLineSegment(sketch, "E1128", {"start": v(-28.38, 30.1) * mm, "end": v(-28.25, 30.1) * mm});
            skLineSegment(sketch, "E1129", {"start": v(-28.25, 30.1) * mm, "end": v(-28.12, 30.1) * mm});
            skLineSegment(sketch, "E1130", {"start": v(-28.12, 30.1) * mm, "end": v(-27.99, 30.1) * mm});
            skLineSegment(sketch, "E1131", {"start": v(-27.99, 30.1) * mm, "end": v(-27.86, 30.1) * mm});
            skLineSegment(sketch, "E1132", {"start": v(-27.86, 30.1) * mm, "end": v(-27.72, 30.1) * mm});
            skLineSegment(sketch, "E1133", {"start": v(-27.72, 30.1) * mm, "end": v(-27.6, 30.1) * mm});
            skLineSegment(sketch, "E1134", {"start": v(-27.6, 30.1) * mm, "end": v(-27.46, 30.1) * mm});
            skLineSegment(sketch, "E1135", {"start": v(-27.46, 30.1) * mm, "end": v(-27.33, 30.1) * mm});
            skLineSegment(sketch, "E1136", {"start": v(-27.33, 30.1) * mm, "end": v(-27.2, 30.1) * mm});
            skLineSegment(sketch, "E1137", {"start": v(-27.2, 30.1) * mm, "end": v(-27.07, 30.1) * mm});
            skLineSegment(sketch, "E1138", {"start": v(-27.07, 30.1) * mm, "end": v(-26.94, 30.1) * mm});
            skLineSegment(sketch, "E1139", {"start": v(-26.94, 30.1) * mm, "end": v(-26.8, 30.1) * mm});
            skLineSegment(sketch, "E1140", {"start": v(-26.8, 30.1) * mm, "end": v(-26.67, 30.1) * mm});
            skLineSegment(sketch, "E1141", {"start": v(-26.67, 30.1) * mm, "end": v(-26.54, 30.1) * mm});
            skLineSegment(sketch, "E1142", {"start": v(-26.54, 30.1) * mm, "end": v(-26.4, 30.1) * mm});
            skLineSegment(sketch, "E1143", {"start": v(-26.4, 30.1) * mm, "end": v(-26.28, 30.1) * mm});
            skLineSegment(sketch, "E1144", {"start": v(-26.28, 30.1) * mm, "end": v(-26.15, 30.1) * mm});
            skLineSegment(sketch, "E1145", {"start": v(-26.15, 30.1) * mm, "end": v(-26.02, 30.1) * mm});
            skLineSegment(sketch, "E1146", {"start": v(-26.02, 30.1) * mm, "end": v(-25.88, 30.1) * mm});
            skLineSegment(sketch, "E1147", {"start": v(-25.88, 30.1) * mm, "end": v(-25.75, 30.1) * mm});
            skLineSegment(sketch, "E1148", {"start": v(-25.75, 30.1) * mm, "end": v(-25.62, 30.1) * mm});
            skLineSegment(sketch, "E1149", {"start": v(-25.62, 30.1) * mm, "end": v(-25.49, 30.1) * mm});
            skLineSegment(sketch, "E1150", {"start": v(-25.49, 30.1) * mm, "end": v(-25.36, 30.1) * mm});
            skLineSegment(sketch, "E1151", {"start": v(-25.36, 30.1) * mm, "end": v(-25.23, 30.1) * mm});
            skLineSegment(sketch, "E1152", {"start": v(-25.23, 30.1) * mm, "end": v(-25.17, 30.1) * mm});
            skLineSegment(sketch, "E1153", {"start": v(-25.17, 30.1) * mm, "end": v(-25.12, 30.1) * mm});
            skLineSegment(sketch, "E1154", {"start": v(-25.12, 30.1) * mm, "end": v(-25.07, 30.1) * mm});
            skLineSegment(sketch, "E1155", {"start": v(-25.07, 30.1) * mm, "end": v(-25.01, 30.1) * mm});
            skLineSegment(sketch, "E1156", {"start": v(-25.01, 30.1) * mm, "end": v(-24.96, 30.1) * mm});
            skLineSegment(sketch, "E1157", {"start": v(-24.96, 30.1) * mm, "end": v(-24.9, 30.1) * mm});
            skLineSegment(sketch, "E1158", {"start": v(-24.9, 30.1) * mm, "end": v(-24.86, 30.1) * mm});
            skLineSegment(sketch, "E1159", {"start": v(-24.86, 30.1) * mm, "end": v(-24.8, 30.1) * mm});
            skLineSegment(sketch, "E1160", {"start": v(-24.8, 30.1) * mm, "end": v(-24.75, 30.1) * mm});
            skLineSegment(sketch, "E1161", {"start": v(-24.75, 30.1) * mm, "end": v(-24.7, 30.09) * mm});
            skLineSegment(sketch, "E1162", {"start": v(-24.7, 30.09) * mm, "end": v(-24.65, 30.08) * mm});
            skLineSegment(sketch, "E1163", {"start": v(-24.65, 30.08) * mm, "end": v(-24.6, 30.08) * mm});
            skLineSegment(sketch, "E1164", {"start": v(-24.6, 30.08) * mm, "end": v(-24.54, 30.08) * mm});
            skLineSegment(sketch, "E1165", {"start": v(-24.54, 30.08) * mm, "end": v(-24.5, 30.07) * mm});
            skLineSegment(sketch, "E1166", {"start": v(-24.5, 30.07) * mm, "end": v(-24.44, 30.07) * mm});
            skLineSegment(sketch, "E1167", {"start": v(-24.44, 30.07) * mm, "end": v(-24.39, 30.06) * mm});
            skLineSegment(sketch, "E1168", {"start": v(-24.39, 30.06) * mm, "end": v(-24.33, 30.06) * mm});
            skLineSegment(sketch, "E1169", {"start": v(-24.33, 30.06) * mm, "end": v(-24.28, 30.05) * mm});
            skLineSegment(sketch, "E1170", {"start": v(-24.28, 30.05) * mm, "end": v(-24.23, 30.04) * mm});
            skLineSegment(sketch, "E1171", {"start": v(-24.23, 30.04) * mm, "end": v(-24.18, 30.04) * mm});
            skLineSegment(sketch, "E1172", {"start": v(-24.18, 30.04) * mm, "end": v(-24.13, 30.03) * mm});
            skLineSegment(sketch, "E1173", {"start": v(-24.13, 30.03) * mm, "end": v(-24.08, 30.02) * mm});
            skLineSegment(sketch, "E1174", {"start": v(-24.08, 30.02) * mm, "end": v(-24.03, 30.02) * mm});
            skLineSegment(sketch, "E1175", {"start": v(-24.03, 30.02) * mm, "end": v(-23.98, 30) * mm});
            skLineSegment(sketch, "E1176", {"start": v(-23.98, 30) * mm, "end": v(-23.93, 30) * mm});
            skLineSegment(sketch, "E1177", {"start": v(-23.93, 30) * mm, "end": v(-23.88, 30) * mm});
            skLineSegment(sketch, "E1178", {"start": v(-23.88, 30) * mm, "end": v(-23.83, 29.98) * mm});
            skLineSegment(sketch, "E1179", {"start": v(-23.83, 29.98) * mm, "end": v(-23.78, 29.97) * mm});
            skLineSegment(sketch, "E1180", {"start": v(-23.78, 29.97) * mm, "end": v(-23.73, 29.96) * mm});
            skLineSegment(sketch, "E1181", {"start": v(-23.73, 29.96) * mm, "end": v(-23.69, 29.95) * mm});
            skLineSegment(sketch, "E1182", {"start": v(-23.69, 29.95) * mm, "end": v(-23.64, 29.94) * mm});
            skLineSegment(sketch, "E1183", {"start": v(-23.64, 29.94) * mm, "end": v(-23.6, 29.93) * mm});
            skLineSegment(sketch, "E1184", {"start": v(-23.6, 29.93) * mm, "end": v(-23.54, 29.92) * mm});
            skLineSegment(sketch, "E1185", {"start": v(-23.54, 29.92) * mm, "end": v(-23.5, 29.9) * mm});
            skLineSegment(sketch, "E1186", {"start": v(-23.5, 29.9) * mm, "end": v(-23.45, 29.9) * mm});
            skLineSegment(sketch, "E1187", {"start": v(-23.45, 29.9) * mm, "end": v(-23.4, 29.88) * mm});
            skLineSegment(sketch, "E1188", {"start": v(-23.4, 29.88) * mm, "end": v(-23.36, 29.87) * mm});
            skLineSegment(sketch, "E1189", {"start": v(-23.36, 29.87) * mm, "end": v(-23.31, 29.85) * mm});
            skLineSegment(sketch, "E1190", {"start": v(-23.31, 29.85) * mm, "end": v(-23.27, 29.84) * mm});
            skLineSegment(sketch, "E1191", {"start": v(-23.27, 29.84) * mm, "end": v(-23.22, 29.82) * mm});
            skLineSegment(sketch, "E1192", {"start": v(-23.22, 29.82) * mm, "end": v(-23.18, 29.8) * mm});
            skLineSegment(sketch, "E1193", {"start": v(-23.18, 29.8) * mm, "end": v(-23.14, 29.8) * mm});
            skLineSegment(sketch, "E1194", {"start": v(-23.14, 29.8) * mm, "end": v(-23.1, 29.77) * mm});
            skLineSegment(sketch, "E1195", {"start": v(-23.1, 29.77) * mm, "end": v(-23.05, 29.76) * mm});
            skLineSegment(sketch, "E1196", {"start": v(-23.05, 29.76) * mm, "end": v(-23, 29.74) * mm});
            skLineSegment(sketch, "E1197", {"start": v(-23, 29.74) * mm, "end": v(-22.97, 29.72) * mm});
            skLineSegment(sketch, "E1198", {"start": v(-22.97, 29.72) * mm, "end": v(-22.92, 29.7) * mm});
            skLineSegment(sketch, "E1199", {"start": v(-22.92, 29.7) * mm, "end": v(-22.88, 29.68) * mm});
            skLineSegment(sketch, "E1200", {"start": v(-22.88, 29.68) * mm, "end": v(-22.84, 29.66) * mm});
            skLineSegment(sketch, "E1201", {"start": v(-22.84, 29.66) * mm, "end": v(-22.8, 29.64) * mm});
            skLineSegment(sketch, "E1202", {"start": v(-22.8, 29.64) * mm, "end": v(-22.76, 29.62) * mm});
            skLineSegment(sketch, "E1203", {"start": v(-22.76, 29.62) * mm, "end": v(-22.73, 29.6) * mm});
            skLineSegment(sketch, "E1204", {"start": v(-22.73, 29.6) * mm, "end": v(-22.69, 29.58) * mm});
            skLineSegment(sketch, "E1205", {"start": v(-22.69, 29.58) * mm, "end": v(-22.65, 29.56) * mm});
            skLineSegment(sketch, "E1206", {"start": v(-22.65, 29.56) * mm, "end": v(-22.61, 29.53) * mm});
            skLineSegment(sketch, "E1207", {"start": v(-22.61, 29.53) * mm, "end": v(-22.58, 29.5) * mm});
            skLineSegment(sketch, "E1208", {"start": v(-22.58, 29.5) * mm, "end": v(-22.54, 29.48) * mm});
            skLineSegment(sketch, "E1209", {"start": v(-22.54, 29.48) * mm, "end": v(-22.5, 29.46) * mm});
            skLineSegment(sketch, "E1210", {"start": v(-22.5, 29.46) * mm, "end": v(-22.47, 29.43) * mm});
            skLineSegment(sketch, "E1211", {"start": v(-22.47, 29.43) * mm, "end": v(-22.44, 29.4) * mm});
            skLineSegment(sketch, "E1212", {"start": v(-22.44, 29.4) * mm, "end": v(-22.4, 29.38) * mm});
            skLineSegment(sketch, "E1213", {"start": v(-22.4, 29.38) * mm, "end": v(-22.37, 29.35) * mm});
            skLineSegment(sketch, "E1214", {"start": v(-22.37, 29.35) * mm, "end": v(-22.34, 29.33) * mm});
            skLineSegment(sketch, "E1215", {"start": v(-22.34, 29.33) * mm, "end": v(-22.31, 29.3) * mm});
            skLineSegment(sketch, "E1216", {"start": v(-22.31, 29.3) * mm, "end": v(-22.28, 29.27) * mm});
            skLineSegment(sketch, "E1217", {"start": v(-22.28, 29.27) * mm, "end": v(-22.25, 29.24) * mm});
            skLineSegment(sketch, "E1218", {"start": v(-22.25, 29.24) * mm, "end": v(-22.22, 29.2) * mm});
            skLineSegment(sketch, "E1219", {"start": v(-22.22, 29.2) * mm, "end": v(-22.2, 29.18) * mm});
            skLineSegment(sketch, "E1220", {"start": v(-22.2, 29.18) * mm, "end": v(-22.17, 29.14) * mm});
            skLineSegment(sketch, "E1221", {"start": v(-22.17, 29.14) * mm, "end": v(-22.14, 29.11) * mm});
            skLineSegment(sketch, "E1222", {"start": v(-22.14, 29.11) * mm, "end": v(-22.12, 29.08) * mm});
            skLineSegment(sketch, "E1223", {"start": v(-22.12, 29.08) * mm, "end": v(-22.1, 29.04) * mm});
            skLineSegment(sketch, "E1224", {"start": v(-22.1, 29.04) * mm, "end": v(-22.07, 29) * mm});
            skLineSegment(sketch, "E1225", {"start": v(-22.07, 29) * mm, "end": v(-22.04, 28.97) * mm});
            skLineSegment(sketch, "E1226", {"start": v(-22.04, 28.97) * mm, "end": v(-22.02, 28.94) * mm});
            skLineSegment(sketch, "E1227", {"start": v(-22.02, 28.94) * mm, "end": v(-22, 28.9) * mm});
            skLineSegment(sketch, "E1228", {"start": v(-22, 28.9) * mm, "end": v(-21.98, 28.86) * mm});
            skLineSegment(sketch, "E1229", {"start": v(-21.98, 28.86) * mm, "end": v(-21.96, 28.82) * mm});
            skLineSegment(sketch, "E1230", {"start": v(-21.96, 28.82) * mm, "end": v(-21.94, 28.78) * mm});
            skLineSegment(sketch, "E1231", {"start": v(-21.94, 28.78) * mm, "end": v(-21.92, 28.74) * mm});
            skLineSegment(sketch, "E1232", {"start": v(-21.92, 28.74) * mm, "end": v(-21.9, 28.7) * mm});
            skLineSegment(sketch, "E1233", {"start": v(-21.9, 28.7) * mm, "end": v(-21.89, 28.66) * mm});
            skLineSegment(sketch, "E1234", {"start": v(-21.89, 28.66) * mm, "end": v(-21.87, 28.62) * mm});
            skLineSegment(sketch, "E1235", {"start": v(-21.87, 28.62) * mm, "end": v(-21.86, 28.58) * mm});
            skLineSegment(sketch, "E1236", {"start": v(-21.86, 28.58) * mm, "end": v(-21.84, 28.53) * mm});
            skLineSegment(sketch, "E1237", {"start": v(-21.84, 28.53) * mm, "end": v(-21.83, 28.49) * mm});
            skLineSegment(sketch, "E1238", {"start": v(-21.83, 28.49) * mm, "end": v(-21.82, 28.44) * mm});
            skLineSegment(sketch, "E1239", {"start": v(-21.82, 28.44) * mm, "end": v(-21.8, 28.4) * mm});
            skLineSegment(sketch, "E1240", {"start": v(-21.8, 28.4) * mm, "end": v(-21.8, 28.35) * mm});
            skLineSegment(sketch, "E1241", {"start": v(-21.8, 28.35) * mm, "end": v(-21.79, 28.3) * mm});
            skLineSegment(sketch, "E1242", {"start": v(-21.79, 28.3) * mm, "end": v(-21.78, 28.25) * mm});
            skLineSegment(sketch, "E1243", {"start": v(-21.78, 28.25) * mm, "end": v(-21.77, 28.2) * mm});
            skLineSegment(sketch, "E1244", {"start": v(-21.77, 28.2) * mm, "end": v(-21.77, 28.15) * mm});
            skLineSegment(sketch, "E1245", {"start": v(-21.77, 28.15) * mm, "end": v(-21.76, 28.1) * mm});
            skLineSegment(sketch, "E1246", {"start": v(-21.76, 28.1) * mm, "end": v(-21.76, 28.05) * mm});
            skLineSegment(sketch, "E1247", {"start": v(-21.76, 28.05) * mm, "end": v(-21.76, 28) * mm});
            skLineSegment(sketch, "E1248", {"start": v(-21.76, 28) * mm, "end": v(-21.76, 27.94) * mm});
            skLineSegment(sketch, "E1249", {"start": v(-21.76, 27.94) * mm, "end": v(-21.75, 27.9) * mm});
            skLineSegment(sketch, "E1250", {"start": v(-21.75, 27.9) * mm, "end": v(-21.76, 27.83) * mm});
            skLineSegment(sketch, "E1251", {"start": v(-21.76, 27.83) * mm, "end": v(-21.76, 27.78) * mm});
            skLineSegment(sketch, "E1252", {"start": v(-21.76, 27.78) * mm, "end": v(-21.76, 27.72) * mm});
            skLineSegment(sketch, "E1253", {"start": v(-21.76, 27.72) * mm, "end": v(-21.76, 27.66) * mm});
            skLineSegment(sketch, "E1254", {"start": v(-21.76, 27.66) * mm, "end": v(-21.77, 27.6) * mm});
            skLineSegment(sketch, "E1255", {"start": v(-21.77, 27.6) * mm, "end": v(-21.77, 27.54) * mm});
            skLineSegment(sketch, "E1256", {"start": v(-21.77, 27.54) * mm, "end": v(-21.78, 27.48) * mm});
            skLineSegment(sketch, "E1257", {"start": v(-21.78, 27.48) * mm, "end": v(-21.79, 27.42) * mm});
            skLineSegment(sketch, "E1258", {"start": v(-21.79, 27.42) * mm, "end": v(-21.8, 27.36) * mm});
            skLineSegment(sketch, "E1259", {"start": v(-21.8, 27.36) * mm, "end": v(-21.81, 27.3) * mm});
            skLineSegment(sketch, "E1260", {"start": v(-21.81, 27.3) * mm, "end": v(-21.82, 27.23) * mm});
            skLineSegment(sketch, "E1261", {"start": v(-21.82, 27.23) * mm, "end": v(-21.84, 27.17) * mm});
            skLineSegment(sketch, "E1262", {"start": v(-21.84, 27.17) * mm, "end": v(-21.85, 27.1) * mm});
            skLineSegment(sketch, "E1263", {"start": v(-21.85, 27.1) * mm, "end": v(-21.86, 27.03) * mm});
            skLineSegment(sketch, "E1264", {"start": v(-21.86, 27.03) * mm, "end": v(-21.88, 26.96) * mm});
            skLineSegment(sketch, "E1265", {"start": v(-21.88, 26.96) * mm, "end": v(-21.9, 26.9) * mm});
            skLineSegment(sketch, "E1266", {"start": v(-21.9, 26.9) * mm, "end": v(-21.92, 26.82) * mm});
            skLineSegment(sketch, "E1267", {"start": v(-21.92, 26.82) * mm, "end": v(-21.94, 26.75) * mm});
            skLineSegment(sketch, "E1268", {"start": v(-21.94, 26.75) * mm, "end": v(-21.96, 26.68) * mm});
            skLineSegment(sketch, "E1269", {"start": v(-21.96, 26.68) * mm, "end": v(-21.98, 26.6) * mm});
            skLineSegment(sketch, "E1270", {"start": v(-21.98, 26.6) * mm, "end": v(-22, 26.53) * mm});
            skLineSegment(sketch, "E1271", {"start": v(-22, 26.53) * mm, "end": v(-22.04, 26.46) * mm});
            skLineSegment(sketch, "E1272", {"start": v(-22.04, 26.46) * mm, "end": v(-22.06, 26.38) * mm});
            skLineSegment(sketch, "E1273", {"start": v(-22.06, 26.38) * mm, "end": v(-22.1, 26.3) * mm});
            skLineSegment(sketch, "E1274", {"start": v(-22.1, 26.3) * mm, "end": v(-22.12, 26.23) * mm});
            skLineSegment(sketch, "E1275", {"start": v(-22.12, 26.23) * mm, "end": v(-22.15, 26.15) * mm});
            skLineSegment(sketch, "E1276", {"start": v(-22.15, 26.15) * mm, "end": v(-22.18, 26.07) * mm});
            skLineSegment(sketch, "E1277", {"start": v(-22.18, 26.07) * mm, "end": v(-22.22, 25.99) * mm});
            skLineSegment(sketch, "E1278", {"start": v(-22.22, 25.99) * mm, "end": v(-22.25, 25.9) * mm});
            skLineSegment(sketch, "E1279", {"start": v(-22.25, 25.9) * mm, "end": v(-22.3, 25.82) * mm});
            skLineSegment(sketch, "E1280", {"start": v(-22.3, 25.82) * mm, "end": v(-22.5, 25.33) * mm});
            skLineSegment(sketch, "E1281", {"start": v(-22.5, 25.33) * mm, "end": v(-22.73, 24.84) * mm});
            skLineSegment(sketch, "E1282", {"start": v(-22.73, 24.84) * mm, "end": v(-22.94, 24.35) * mm});
            skLineSegment(sketch, "E1283", {"start": v(-22.94, 24.35) * mm, "end": v(-23.16, 23.85) * mm});
            skLineSegment(sketch, "E1284", {"start": v(-23.16, 23.85) * mm, "end": v(-23.38, 23.36) * mm});
            skLineSegment(sketch, "E1285", {"start": v(-23.38, 23.36) * mm, "end": v(-23.6, 22.87) * mm});
            skLineSegment(sketch, "E1286", {"start": v(-23.6, 22.87) * mm, "end": v(-23.81, 22.38) * mm});
            skLineSegment(sketch, "E1287", {"start": v(-23.81, 22.38) * mm, "end": v(-24.03, 21.89) * mm});
            skLineSegment(sketch, "E1288", {"start": v(-24.03, 21.89) * mm, "end": v(-24.25, 21.4) * mm});
            skLineSegment(sketch, "E1289", {"start": v(-24.25, 21.4) * mm, "end": v(-24.47, 20.9) * mm});
            skLineSegment(sketch, "E1290", {"start": v(-24.47, 20.9) * mm, "end": v(-24.68, 20.42) * mm});
            skLineSegment(sketch, "E1291", {"start": v(-24.68, 20.42) * mm, "end": v(-24.9, 19.92) * mm});
            skLineSegment(sketch, "E1292", {"start": v(-24.9, 19.92) * mm, "end": v(-25.12, 19.43) * mm});
            skLineSegment(sketch, "E1293", {"start": v(-25.12, 19.43) * mm, "end": v(-25.34, 18.94) * mm});
            skLineSegment(sketch, "E1294", {"start": v(-25.34, 18.94) * mm, "end": v(-25.55, 18.45) * mm});
            skLineSegment(sketch, "E1295", {"start": v(-25.55, 18.45) * mm, "end": v(-25.77, 17.96) * mm});
            skLineSegment(sketch, "E1296", {"start": v(-25.77, 17.96) * mm, "end": v(-25.99, 17.47) * mm});
            skLineSegment(sketch, "E1297", {"start": v(-25.99, 17.47) * mm, "end": v(-26.2, 16.98) * mm});
            skLineSegment(sketch, "E1298", {"start": v(-26.2, 16.98) * mm, "end": v(-26.42, 16.48) * mm});
            skLineSegment(sketch, "E1299", {"start": v(-26.42, 16.48) * mm, "end": v(-26.64, 16) * mm});
            skLineSegment(sketch, "E1300", {"start": v(-26.64, 16) * mm, "end": v(-26.86, 15.5) * mm});
            skLineSegment(sketch, "E1301", {"start": v(-26.86, 15.5) * mm, "end": v(-27.08, 15.01) * mm});
            skLineSegment(sketch, "E1302", {"start": v(-27.08, 15.01) * mm, "end": v(-27.3, 14.52) * mm});
            skLineSegment(sketch, "E1303", {"start": v(-27.3, 14.52) * mm, "end": v(-27.51, 14.03) * mm});
            skLineSegment(sketch, "E1304", {"start": v(-27.51, 14.03) * mm, "end": v(-27.73, 13.54) * mm});
            skLineSegment(sketch, "E1305", {"start": v(-27.73, 13.54) * mm, "end": v(-27.95, 13.05) * mm});
            skLineSegment(sketch, "E1306", {"start": v(-27.95, 13.05) * mm, "end": v(-28.17, 12.55) * mm});
            skLineSegment(sketch, "E1307", {"start": v(-28.17, 12.55) * mm, "end": v(-28.38, 12.06) * mm});
            skLineSegment(sketch, "E1308", {"start": v(-28.38, 12.06) * mm, "end": v(-28.6, 11.57) * mm});
            skLineSegment(sketch, "E1309", {"start": v(-28.6, 11.57) * mm, "end": v(-28.82, 11.08) * mm});
            skLineSegment(sketch, "E1310", {"start": v(-28.82, 11.08) * mm, "end": v(-29.04, 10.59) * mm});
            skLineSegment(sketch, "E1311", {"start": v(-29.04, 10.59) * mm, "end": v(-29.25, 10.1) * mm});
            skLineSegment(sketch, "E1312", {"start": v(-29.25, 10.1) * mm, "end": v(-29.47, 9.6) * mm});
            skLineSegment(sketch, "E1313", {"start": v(-29.47, 9.6) * mm, "end": v(-29.69, 9.12) * mm});
            skLineSegment(sketch, "E1314", {"start": v(-29.69, 9.12) * mm, "end": v(-29.9, 8.62) * mm});
            skLineSegment(sketch, "E1315", {"start": v(-29.9, 8.62) * mm, "end": v(-30.12, 8.13) * mm});
            skLineSegment(sketch, "E1316", {"start": v(-30.12, 8.13) * mm, "end": v(-30.34, 7.64) * mm});
            skLineSegment(sketch, "E1317", {"start": v(-30.34, 7.64) * mm, "end": v(-30.56, 7.15) * mm});
            skLineSegment(sketch, "E1318", {"start": v(-30.56, 7.15) * mm, "end": v(-30.78, 6.66) * mm});
            skLineSegment(sketch, "E1319", {"start": v(-30.78, 6.66) * mm, "end": v(-31, 6.17) * mm});
            skLineSegment(sketch, "E1320", {"start": v(-31, 6.17) * mm, "end": v(-31.21, 5.68) * mm});
            skLineSegment(sketch, "E1321", {"start": v(-31.21, 5.68) * mm, "end": v(-31.43, 5.18) * mm});
            skLineSegment(sketch, "E1322", {"start": v(-31.43, 5.18) * mm, "end": v(-31.65, 4.7) * mm});
            skLineSegment(sketch, "E1323", {"start": v(-31.65, 4.7) * mm, "end": v(-31.87, 4.2) * mm});
            skLineSegment(sketch, "E1324", {"start": v(-31.87, 4.2) * mm, "end": v(-32.08, 3.71) * mm});
            skLineSegment(sketch, "E1325", {"start": v(-32.08, 3.71) * mm, "end": v(-32.3, 3.22) * mm});
            skLineSegment(sketch, "E1326", {"start": v(-32.3, 3.22) * mm, "end": v(-32.52, 2.73) * mm});
            skLineSegment(sketch, "E1327", {"start": v(-32.52, 2.73) * mm, "end": v(-32.74, 2.24) * mm});
            skLineSegment(sketch, "E1328", {"start": v(-32.74, 2.24) * mm, "end": v(-32.95, 1.75) * mm});
            skLineSegment(sketch, "E1329", {"start": v(-32.95, 1.75) * mm, "end": v(-33.17, 1.25) * mm});
            skLineSegment(sketch, "E1330", {"start": v(-33.17, 1.25) * mm, "end": v(-33.39, 0.76) * mm});
            skLineSegment(sketch, "E1331", {"start": v(-33.39, 0.76) * mm, "end": v(-33.6, 0.27) * mm});
            skLineSegment(sketch, "E1332", {"start": v(-33.6, 0.27) * mm, "end": v(-33.82, -0.22) * mm});
            skLineSegment(sketch, "E1333", {"start": v(-33.82, -0.22) * mm, "end": v(-34.04, -0.71) * mm});
            skLineSegment(sketch, "E1334", {"start": v(-34.04, -0.71) * mm, "end": v(-34.26, -1.2) * mm});
            skLineSegment(sketch, "E1335", {"start": v(-34.26, -1.2) * mm, "end": v(-34.48, -1.7) * mm});
            skLineSegment(sketch, "E1336", {"start": v(-34.48, -1.7) * mm, "end": v(-34.7, -2.19) * mm});
            skLineSegment(sketch, "E1337", {"start": v(-34.7, -2.19) * mm, "end": v(-34.91, -2.68) * mm});
            skLineSegment(sketch, "E1338", {"start": v(-34.91, -2.68) * mm, "end": v(-35.13, -3.17) * mm});
            skLineSegment(sketch, "E1339", {"start": v(-35.13, -3.17) * mm, "end": v(-35.35, -3.66) * mm});
            skLineSegment(sketch, "E1340", {"start": v(-35.35, -3.66) * mm, "end": v(-35.56, -4.15) * mm});
            skLineSegment(sketch, "E1341", {"start": v(-35.56, -4.15) * mm, "end": v(-35.78, -4.64) * mm});
            skLineSegment(sketch, "E1342", {"start": v(-35.78, -4.64) * mm, "end": v(-36, -5.13) * mm});
            skLineSegment(sketch, "E1343", {"start": v(-36, -5.13) * mm, "end": v(-36.22, -5.62) * mm});
            skLineSegment(sketch, "E1344", {"start": v(-36.22, -5.62) * mm, "end": v(-36.43, -6.12) * mm});
            skLineSegment(sketch, "E1345", {"start": v(-36.43, -6.12) * mm, "end": v(-36.65, -6.6) * mm});
            skLineSegment(sketch, "E1346", {"start": v(-36.65, -6.6) * mm, "end": v(-36.87, -7.1) * mm});
            skLineSegment(sketch, "E1347", {"start": v(-36.87, -7.1) * mm, "end": v(-37.09, -7.59) * mm});
            skLineSegment(sketch, "E1348", {"start": v(-37.09, -7.59) * mm, "end": v(-37.3, -8.08) * mm});
            skLineSegment(sketch, "E1349", {"start": v(-37.3, -8.08) * mm, "end": v(-37.52, -8.57) * mm});
            skLineSegment(sketch, "E1350", {"start": v(-37.52, -8.57) * mm, "end": v(-37.74, -9.06) * mm});
            skLineSegment(sketch, "E1351", {"start": v(-37.74, -9.06) * mm, "end": v(-37.96, -9.56) * mm});
            skLineSegment(sketch, "E1352", {"start": v(-37.96, -9.56) * mm, "end": v(-38.18, -10.05) * mm});
            skLineSegment(sketch, "E1353", {"start": v(-38.18, -10.05) * mm, "end": v(-38.4, -10.54) * mm});
            skLineSegment(sketch, "E1354", {"start": v(-38.4, -10.54) * mm, "end": v(-38.61, -11.03) * mm});
            skLineSegment(sketch, "E1355", {"start": v(-38.61, -11.03) * mm, "end": v(-38.83, -11.52) * mm});
            skLineSegment(sketch, "E1356", {"start": v(-38.83, -11.52) * mm, "end": v(-39.05, -12.01) * mm});
            skLineSegment(sketch, "E1357", {"start": v(-39.05, -12.01) * mm, "end": v(-39.26, -12.5) * mm});
            skLineSegment(sketch, "E1358", {"start": v(-39.26, -12.5) * mm, "end": v(-39.48, -13) * mm});
            skLineSegment(sketch, "E1359", {"start": v(-39.48, -13) * mm, "end": v(-39.7, -13.49) * mm});
            skLineSegment(sketch, "E1360", {"start": v(-39.7, -13.49) * mm, "end": v(-39.92, -13.98) * mm});
            skLineSegment(sketch, "E1361", {"start": v(-39.92, -13.98) * mm, "end": v(-40.13, -14.47) * mm});
            skLineSegment(sketch, "E1362", {"start": v(-40.13, -14.47) * mm, "end": v(-40.35, -14.96) * mm});
            skLineSegment(sketch, "E1363", {"start": v(-40.35, -14.96) * mm, "end": v(-40.57, -15.45) * mm});
            skLineSegment(sketch, "E1364", {"start": v(-40.57, -15.45) * mm, "end": v(-40.79, -15.94) * mm});
            skLineSegment(sketch, "E1365", {"start": v(-40.79, -15.94) * mm, "end": v(-41, -16.43) * mm});
            skLineSegment(sketch, "E1366", {"start": v(-41, -16.43) * mm, "end": v(-41.22, -16.92) * mm});
            skLineSegment(sketch, "E1367", {"start": v(-41.22, -16.92) * mm, "end": v(-41.44, -17.42) * mm});
            skLineSegment(sketch, "E1368", {"start": v(-41.44, -17.42) * mm, "end": v(-41.66, -17.9) * mm});
            skLineSegment(sketch, "E1369", {"start": v(-41.66, -17.9) * mm, "end": v(-41.87, -18.4) * mm});
            skLineSegment(sketch, "E1370", {"start": v(-41.87, -18.4) * mm, "end": v(-42.1, -18.9) * mm});
            skLineSegment(sketch, "E1371", {"start": v(-42.1, -18.9) * mm, "end": v(-42.3, -19.38) * mm});
            skLineSegment(sketch, "E1372", {"start": v(-42.3, -19.38) * mm, "end": v(-42.53, -19.87) * mm});
            skLineSegment(sketch, "E1373", {"start": v(-42.53, -19.87) * mm, "end": v(-42.75, -20.36) * mm});
            skLineSegment(sketch, "E1374", {"start": v(-42.75, -20.36) * mm, "end": v(-42.96, -20.86) * mm});
            skLineSegment(sketch, "E1375", {"start": v(-42.96, -20.86) * mm, "end": v(-43.18, -21.35) * mm});
            skLineSegment(sketch, "E1376", {"start": v(-43.18, -21.35) * mm, "end": v(-43.4, -21.84) * mm});
            skLineSegment(sketch, "E1377", {"start": v(-43.4, -21.84) * mm, "end": v(-43.62, -22.33) * mm});
            skLineSegment(sketch, "E1378", {"start": v(-43.62, -22.33) * mm, "end": v(-43.83, -22.82) * mm});
            skLineSegment(sketch, "E1379", {"start": v(-43.83, -22.82) * mm, "end": v(-44.05, -23.31) * mm});
            skLineSegment(sketch, "E1380", {"start": v(-44.05, -23.31) * mm, "end": v(-44.27, -23.8) * mm});
            skLineSegment(sketch, "E1381", {"start": v(-44.27, -23.8) * mm, "end": v(-44.49, -24.3) * mm});
            skLineSegment(sketch, "E1382", {"start": v(-44.49, -24.3) * mm, "end": v(-44.7, -24.79) * mm});
            skLineSegment(sketch, "E1383", {"start": v(-44.7, -24.79) * mm, "end": v(-44.92, -25.28) * mm});
            skLineSegment(sketch, "E1384", {"start": v(-44.92, -25.28) * mm, "end": v(-45.14, -25.77) * mm});
            skLineSegment(sketch, "E1385", {"start": v(-45.14, -25.77) * mm, "end": v(-45.36, -26.26) * mm});
            skLineSegment(sketch, "E1386", {"start": v(-45.36, -26.26) * mm, "end": v(-45.57, -26.75) * mm});
            skLineSegment(sketch, "E1387", {"start": v(-45.57, -26.75) * mm, "end": v(-45.8, -27.24) * mm});
            skLineSegment(sketch, "E1388", {"start": v(-45.8, -27.24) * mm, "end": v(-46, -27.73) * mm});
            skLineSegment(sketch, "E1389", {"start": v(-46, -27.73) * mm, "end": v(-46.23, -28.23) * mm});
            skLineSegment(sketch, "E1390", {"start": v(-46.23, -28.23) * mm, "end": v(-46.44, -28.72) * mm});
            skLineSegment(sketch, "E1391", {"start": v(-46.44, -28.72) * mm, "end": v(-46.66, -29.2) * mm});
            skLineSegment(sketch, "E1392", {"start": v(-46.66, -29.2) * mm, "end": v(-46.88, -29.7) * mm});
            skLineSegment(sketch, "E1393", {"start": v(-46.88, -29.7) * mm, "end": v(-47.1, -30.2) * mm});
            skLineSegment(sketch, "E1394", {"start": v(-47.1, -30.2) * mm, "end": v(-47.31, -30.68) * mm});
            skLineSegment(sketch, "E1395", {"start": v(-47.31, -30.68) * mm, "end": v(-47.53, -31.17) * mm});
            skLineSegment(sketch, "E1396", {"start": v(-47.53, -31.17) * mm, "end": v(-47.75, -31.66) * mm});
            skLineSegment(sketch, "E1397", {"start": v(-47.75, -31.66) * mm, "end": v(-47.97, -32.16) * mm});
            skLineSegment(sketch, "E1398", {"start": v(-47.97, -32.16) * mm, "end": v(-48.19, -32.65) * mm});
            skLineSegment(sketch, "E1399", {"start": v(-48.19, -32.65) * mm, "end": v(-48.4, -33.14) * mm});
            skLineSegment(sketch, "E1400", {"start": v(-48.4, -33.14) * mm, "end": v(-48.62, -33.63) * mm});
            skLineSegment(sketch, "E1401", {"start": v(-48.62, -33.63) * mm, "end": v(-48.84, -34.12) * mm});
            skLineSegment(sketch, "E1402", {"start": v(-48.84, -34.12) * mm, "end": v(-49.06, -34.61) * mm});
            skLineSegment(sketch, "E1403", {"start": v(-49.06, -34.61) * mm, "end": v(-49.27, -35.1) * mm});
            skLineSegment(sketch, "E1404", {"start": v(-49.27, -35.1) * mm, "end": v(-49.5, -35.6) * mm});
            skLineSegment(sketch, "E1405", {"start": v(-49.5, -35.6) * mm, "end": v(-49.7, -36.09) * mm});
            skLineSegment(sketch, "E1406", {"start": v(-49.7, -36.09) * mm, "end": v(-49.93, -36.58) * mm});
            skLineSegment(sketch, "E1407", {"start": v(-49.93, -36.58) * mm, "end": v(-50.14, -37.07) * mm});
            skLineSegment(sketch, "E1408", {"start": v(-50.14, -37.07) * mm, "end": v(-50.02, -37.07) * mm});
            skLineSegment(sketch, "E1409", {"start": v(-50.02, -37.07) * mm, "end": v(-49.9, -37.07) * mm});
            skLineSegment(sketch, "E1410", {"start": v(-49.9, -37.07) * mm, "end": v(-49.78, -37.07) * mm});
            skLineSegment(sketch, "E1411", {"start": v(-49.78, -37.07) * mm, "end": v(-49.66, -37.07) * mm});
            skLineSegment(sketch, "E1412", {"start": v(-49.66, -37.07) * mm, "end": v(-49.54, -37.07) * mm});
            skLineSegment(sketch, "E1413", {"start": v(-49.54, -37.07) * mm, "end": v(-49.42, -37.07) * mm});
            skLineSegment(sketch, "E1414", {"start": v(-49.42, -37.07) * mm, "end": v(-49.3, -37.07) * mm});
            skLineSegment(sketch, "E1415", {"start": v(-49.3, -37.07) * mm, "end": v(-49.18, -37.07) * mm});
            skLineSegment(sketch, "E1416", {"start": v(-49.18, -37.07) * mm, "end": v(-49.06, -37.07) * mm});
            skLineSegment(sketch, "E1417", {"start": v(-49.06, -37.07) * mm, "end": v(-48.94, -37.07) * mm});
            skLineSegment(sketch, "E1418", {"start": v(-48.94, -37.07) * mm, "end": v(-48.82, -37.07) * mm});
            skLineSegment(sketch, "E1419", {"start": v(-48.82, -37.07) * mm, "end": v(-48.7, -37.07) * mm});
            skLineSegment(sketch, "E1420", {"start": v(-48.7, -37.07) * mm, "end": v(-48.58, -37.07) * mm});
            skLineSegment(sketch, "E1421", {"start": v(-48.58, -37.07) * mm, "end": v(-48.46, -37.07) * mm});
            skLineSegment(sketch, "E1422", {"start": v(-48.46, -37.07) * mm, "end": v(-48.34, -37.07) * mm});
            skLineSegment(sketch, "E1423", {"start": v(-48.34, -37.07) * mm, "end": v(-48.22, -37.07) * mm});
            skLineSegment(sketch, "E1424", {"start": v(-48.22, -37.07) * mm, "end": v(-48.1, -37.07) * mm});
            skLineSegment(sketch, "E1425", {"start": v(-48.1, -37.07) * mm, "end": v(-47.98, -37.07) * mm});
            skLineSegment(sketch, "E1426", {"start": v(-47.98, -37.07) * mm, "end": v(-47.86, -37.07) * mm});
            skLineSegment(sketch, "E1427", {"start": v(-47.86, -37.07) * mm, "end": v(-47.74, -37.07) * mm});
            skLineSegment(sketch, "E1428", {"start": v(-47.74, -37.07) * mm, "end": v(-47.62, -37.07) * mm});
            skLineSegment(sketch, "E1429", {"start": v(-47.62, -37.07) * mm, "end": v(-47.5, -37.07) * mm});
            skLineSegment(sketch, "E1430", {"start": v(-47.5, -37.07) * mm, "end": v(-47.38, -37.07) * mm});
            skLineSegment(sketch, "E1431", {"start": v(-47.38, -37.07) * mm, "end": v(-47.26, -37.07) * mm});
            skLineSegment(sketch, "E1432", {"start": v(-47.26, -37.07) * mm, "end": v(-47.13, -37.07) * mm});
            skLineSegment(sketch, "E1433", {"start": v(-47.13, -37.07) * mm, "end": v(-47.01, -37.07) * mm});
            skLineSegment(sketch, "E1434", {"start": v(-47.01, -37.07) * mm, "end": v(-46.9, -37.07) * mm});
            skLineSegment(sketch, "E1435", {"start": v(-46.9, -37.07) * mm, "end": v(-46.77, -37.07) * mm});
            skLineSegment(sketch, "E1436", {"start": v(-46.77, -37.07) * mm, "end": v(-46.65, -37.07) * mm});
            skLineSegment(sketch, "E1437", {"start": v(-46.65, -37.07) * mm, "end": v(-46.53, -37.07) * mm});
            skLineSegment(sketch, "E1438", {"start": v(-46.53, -37.07) * mm, "end": v(-46.41, -37.07) * mm});
            skLineSegment(sketch, "E1439", {"start": v(-46.41, -37.07) * mm, "end": v(-46.3, -37.07) * mm});
            skLineSegment(sketch, "E1440", {"start": v(-46.3, -37.07) * mm, "end": v(-46.17, -37.07) * mm});
            skLineSegment(sketch, "E1441", {"start": v(-46.17, -37.07) * mm, "end": v(-46.05, -37.07) * mm});
            skLineSegment(sketch, "E1442", {"start": v(-46.05, -37.07) * mm, "end": v(-45.93, -37.07) * mm});
            skLineSegment(sketch, "E1443", {"start": v(-45.93, -37.07) * mm, "end": v(-45.81, -37.07) * mm});
            skLineSegment(sketch, "E1444", {"start": v(-45.81, -37.07) * mm, "end": v(-45.7, -37.07) * mm});
            skLineSegment(sketch, "E1445", {"start": v(-45.7, -37.07) * mm, "end": v(-45.57, -37.07) * mm});
            skLineSegment(sketch, "E1446", {"start": v(-45.57, -37.07) * mm, "end": v(-45.45, -37.07) * mm});
            skLineSegment(sketch, "E1447", {"start": v(-45.45, -37.07) * mm, "end": v(-45.33, -37.07) * mm});
            skLineSegment(sketch, "E1448", {"start": v(-45.33, -37.07) * mm, "end": v(-45.2, -37.07) * mm});
            skLineSegment(sketch, "E1449", {"start": v(-45.2, -37.07) * mm, "end": v(-45.09, -37.07) * mm});
            skLineSegment(sketch, "E1450", {"start": v(-45.09, -37.07) * mm, "end": v(-44.97, -37.07) * mm});
            skLineSegment(sketch, "E1451", {"start": v(-44.97, -37.07) * mm, "end": v(-44.85, -37.07) * mm});
            skLineSegment(sketch, "E1452", {"start": v(-44.85, -37.07) * mm, "end": v(-44.73, -37.07) * mm});
            skLineSegment(sketch, "E1453", {"start": v(-44.73, -37.07) * mm, "end": v(-44.6, -37.07) * mm});
            skLineSegment(sketch, "E1454", {"start": v(-44.6, -37.07) * mm, "end": v(-44.49, -37.07) * mm});
            skLineSegment(sketch, "E1455", {"start": v(-44.49, -37.07) * mm, "end": v(-44.37, -37.07) * mm});
            skLineSegment(sketch, "E1456", {"start": v(-44.37, -37.07) * mm, "end": v(-44.25, -37.07) * mm});
            skLineSegment(sketch, "E1457", {"start": v(-44.25, -37.07) * mm, "end": v(-44.13, -37.07) * mm});
            skLineSegment(sketch, "E1458", {"start": v(-44.13, -37.07) * mm, "end": v(-44, -37.07) * mm});
            skLineSegment(sketch, "E1459", {"start": v(-44, -37.07) * mm, "end": v(-43.89, -37.07) * mm});
            skLineSegment(sketch, "E1460", {"start": v(-43.89, -37.07) * mm, "end": v(-43.77, -37.07) * mm});
            skLineSegment(sketch, "E1461", {"start": v(-43.77, -37.07) * mm, "end": v(-43.65, -37.07) * mm});
            skLineSegment(sketch, "E1462", {"start": v(-43.65, -37.07) * mm, "end": v(-43.52, -37.07) * mm});
            skLineSegment(sketch, "E1463", {"start": v(-43.52, -37.07) * mm, "end": v(-43.4, -37.07) * mm});
            skLineSegment(sketch, "E1464", {"start": v(-43.4, -37.07) * mm, "end": v(-43.28, -37.07) * mm});
            skLineSegment(sketch, "E1465", {"start": v(-43.28, -37.07) * mm, "end": v(-43.16, -37.07) * mm});
            skLineSegment(sketch, "E1466", {"start": v(-43.16, -37.07) * mm, "end": v(-43.04, -37.07) * mm});
            skLineSegment(sketch, "E1467", {"start": v(-43.04, -37.07) * mm, "end": v(-42.92, -37.07) * mm});
            skLineSegment(sketch, "E1468", {"start": v(-42.92, -37.07) * mm, "end": v(-42.8, -37.07) * mm});
            skLineSegment(sketch, "E1469", {"start": v(-42.8, -37.07) * mm, "end": v(-42.68, -37.07) * mm});
            skLineSegment(sketch, "E1470", {"start": v(-42.68, -37.07) * mm, "end": v(-42.56, -37.07) * mm});
            skLineSegment(sketch, "E1471", {"start": v(-42.56, -37.07) * mm, "end": v(-42.44, -37.07) * mm});
            skLineSegment(sketch, "E1472", {"start": v(-42.44, -37.07) * mm, "end": v(-42.32, -37.07) * mm});
            skLineSegment(sketch, "E1473", {"start": v(-42.32, -37.07) * mm, "end": v(-42.2, -37.07) * mm});
            skLineSegment(sketch, "E1474", {"start": v(-42.2, -37.07) * mm, "end": v(-42.08, -37.07) * mm});
            skLineSegment(sketch, "E1475", {"start": v(-42.08, -37.07) * mm, "end": v(-41.96, -37.07) * mm});
            skLineSegment(sketch, "E1476", {"start": v(-41.96, -37.07) * mm, "end": v(-41.84, -37.07) * mm});
            skLineSegment(sketch, "E1477", {"start": v(-41.84, -37.07) * mm, "end": v(-41.72, -37.07) * mm});
            skLineSegment(sketch, "E1478", {"start": v(-41.72, -37.07) * mm, "end": v(-41.6, -37.07) * mm});
            skLineSegment(sketch, "E1479", {"start": v(-41.6, -37.07) * mm, "end": v(-41.48, -37.07) * mm});
            skLineSegment(sketch, "E1480", {"start": v(-41.48, -37.07) * mm, "end": v(-41.36, -37.07) * mm});
            skLineSegment(sketch, "E1481", {"start": v(-41.36, -37.07) * mm, "end": v(-41.24, -37.07) * mm});
            skLineSegment(sketch, "E1482", {"start": v(-41.24, -37.07) * mm, "end": v(-41.12, -37.07) * mm});
            skLineSegment(sketch, "E1483", {"start": v(-41.12, -37.07) * mm, "end": v(-41, -37.07) * mm});
            skLineSegment(sketch, "E1484", {"start": v(-41, -37.07) * mm, "end": v(-40.88, -37.07) * mm});
            skLineSegment(sketch, "E1485", {"start": v(-40.88, -37.07) * mm, "end": v(-40.76, -37.07) * mm});
            skLineSegment(sketch, "E1486", {"start": v(-40.76, -37.07) * mm, "end": v(-40.64, -37.07) * mm});
            skLineSegment(sketch, "E1487", {"start": v(-40.64, -37.07) * mm, "end": v(-40.52, -37.07) * mm});
            skLineSegment(sketch, "E1488", {"start": v(-40.52, -37.07) * mm, "end": v(-40.4, -37.07) * mm});
            skLineSegment(sketch, "E1489", {"start": v(-40.4, -37.07) * mm, "end": v(-40.28, -37.07) * mm});
            skLineSegment(sketch, "E1490", {"start": v(-40.28, -37.07) * mm, "end": v(-40.16, -37.07) * mm});
            skLineSegment(sketch, "E1491", {"start": v(-40.16, -37.07) * mm, "end": v(-40.03, -37.07) * mm});
            skLineSegment(sketch, "E1492", {"start": v(-40.03, -37.07) * mm, "end": v(-39.91, -37.07) * mm});
            skLineSegment(sketch, "E1493", {"start": v(-39.91, -37.07) * mm, "end": v(-39.8, -37.07) * mm});
            skLineSegment(sketch, "E1494", {"start": v(-39.8, -37.07) * mm, "end": v(-39.67, -37.07) * mm});
            skLineSegment(sketch, "E1495", {"start": v(-39.67, -37.07) * mm, "end": v(-39.55, -37.07) * mm});
            skLineSegment(sketch, "E1496", {"start": v(-39.55, -37.07) * mm, "end": v(-39.43, -37.07) * mm});
            skLineSegment(sketch, "E1497", {"start": v(-39.43, -37.07) * mm, "end": v(-39.31, -37.07) * mm});
            skLineSegment(sketch, "E1498", {"start": v(-39.31, -37.07) * mm, "end": v(-39.2, -37.07) * mm});
            skLineSegment(sketch, "E1499", {"start": v(-39.2, -37.07) * mm, "end": v(-39.07, -37.07) * mm});
            skLineSegment(sketch, "E1500", {"start": v(-39.07, -37.07) * mm, "end": v(-38.95, -37.07) * mm});
            skLineSegment(sketch, "E1501", {"start": v(-38.95, -37.07) * mm, "end": v(-38.83, -37.07) * mm});
            skLineSegment(sketch, "E1502", {"start": v(-38.83, -37.07) * mm, "end": v(-38.71, -37.07) * mm});
            skLineSegment(sketch, "E1503", {"start": v(-38.71, -37.07) * mm, "end": v(-38.6, -37.07) * mm});
            skLineSegment(sketch, "E1504", {"start": v(-38.6, -37.07) * mm, "end": v(-38.47, -37.07) * mm});
            skLineSegment(sketch, "E1505", {"start": v(-38.47, -37.07) * mm, "end": v(-38.35, -37.07) * mm});
            skLineSegment(sketch, "E1506", {"start": v(-38.35, -37.07) * mm, "end": v(-38.23, -37.07) * mm});
            skLineSegment(sketch, "E1507", {"start": v(-38.23, -37.07) * mm, "end": v(-38.1, -37.07) * mm});
            skLineSegment(sketch, "E1508", {"start": v(-38.1, -37.07) * mm, "end": v(-37.99, -37.07) * mm});
            skLineSegment(sketch, "E1509", {"start": v(-37.99, -37.07) * mm, "end": v(-37.87, -37.07) * mm});
            skLineSegment(sketch, "E1510", {"start": v(-37.87, -37.07) * mm, "end": v(-37.75, -37.07) * mm});
            skLineSegment(sketch, "E1511", {"start": v(-37.75, -37.07) * mm, "end": v(-37.63, -37.07) * mm});
            skLineSegment(sketch, "E1512", {"start": v(-37.63, -37.07) * mm, "end": v(-37.5, -37.07) * mm});
            skLineSegment(sketch, "E1513", {"start": v(-37.5, -37.07) * mm, "end": v(-37.39, -37.07) * mm});
            skLineSegment(sketch, "E1514", {"start": v(-37.39, -37.07) * mm, "end": v(-37.27, -37.07) * mm});
            skLineSegment(sketch, "E1515", {"start": v(-37.27, -37.07) * mm, "end": v(-37.15, -37.07) * mm});
            skLineSegment(sketch, "E1516", {"start": v(-37.15, -37.07) * mm, "end": v(-37.03, -37.07) * mm});
            skLineSegment(sketch, "E1517", {"start": v(-37.03, -37.07) * mm, "end": v(-36.9, -37.07) * mm});
            skLineSegment(sketch, "E1518", {"start": v(-36.9, -37.07) * mm, "end": v(-36.79, -37.07) * mm});
            skLineSegment(sketch, "E1519", {"start": v(-36.79, -37.07) * mm, "end": v(-36.67, -37.07) * mm});
            skLineSegment(sketch, "E1520", {"start": v(-36.67, -37.07) * mm, "end": v(-36.54, -37.07) * mm});
            skLineSegment(sketch, "E1521", {"start": v(-36.54, -37.07) * mm, "end": v(-36.42, -37.07) * mm});
            skLineSegment(sketch, "E1522", {"start": v(-36.42, -37.07) * mm, "end": v(-36.3, -37.07) * mm});
            skLineSegment(sketch, "E1523", {"start": v(-36.3, -37.07) * mm, "end": v(-36.18, -37.07) * mm});
            skLineSegment(sketch, "E1524", {"start": v(-36.18, -37.07) * mm, "end": v(-36.06, -37.07) * mm});
            skLineSegment(sketch, "E1525", {"start": v(-36.06, -37.07) * mm, "end": v(-35.94, -37.07) * mm});
            skLineSegment(sketch, "E1526", {"start": v(-35.94, -37.07) * mm, "end": v(-35.82, -37.07) * mm});
            skLineSegment(sketch, "E1527", {"start": v(-35.82, -37.07) * mm, "end": v(-35.7, -37.07) * mm});
            skLineSegment(sketch, "E1528", {"start": v(-35.7, -37.07) * mm, "end": v(-35.58, -37.07) * mm});
            skLineSegment(sketch, "E1529", {"start": v(-35.58, -37.07) * mm, "end": v(-35.46, -37.07) * mm});
            skLineSegment(sketch, "E1530", {"start": v(-35.46, -37.07) * mm, "end": v(-35.34, -37.07) * mm});
            skLineSegment(sketch, "E1531", {"start": v(-35.34, -37.07) * mm, "end": v(-35.22, -37.07) * mm});
            skLineSegment(sketch, "E1532", {"start": v(-35.22, -37.07) * mm, "end": v(-35.1, -37.07) * mm});
            skLineSegment(sketch, "E1533", {"start": v(-35.1, -37.07) * mm, "end": v(-34.98, -37.07) * mm});
            skLineSegment(sketch, "E1534", {"start": v(-34.98, -37.07) * mm, "end": v(-34.86, -37.07) * mm});
            skLineSegment(sketch, "E1535", {"start": v(-34.86, -37.07) * mm, "end": v(-34.74, -37.07) * mm});
            skLineSegment(sketch, "E1536", {"start": v(-34.74, -37.07) * mm, "end": v(-34.54, -36.62) * mm});
            skLineSegment(sketch, "E1537", {"start": v(-34.54, -36.62) * mm, "end": v(-34.34, -36.16) * mm});
            skLineSegment(sketch, "E1538", {"start": v(-34.34, -36.16) * mm, "end": v(-34.14, -35.71) * mm});
            skLineSegment(sketch, "E1539", {"start": v(-34.14, -35.71) * mm, "end": v(-33.95, -35.26) * mm});
            skLineSegment(sketch, "E1540", {"start": v(-33.95, -35.26) * mm, "end": v(-33.75, -34.8) * mm});
            skLineSegment(sketch, "E1541", {"start": v(-33.75, -34.8) * mm, "end": v(-33.55, -34.35) * mm});
            skLineSegment(sketch, "E1542", {"start": v(-33.55, -34.35) * mm, "end": v(-33.35, -33.9) * mm});
            skLineSegment(sketch, "E1543", {"start": v(-33.35, -33.9) * mm, "end": v(-33.15, -33.45) * mm});
            skLineSegment(sketch, "E1544", {"start": v(-33.15, -33.45) * mm, "end": v(-32.95, -33) * mm});
            skLineSegment(sketch, "E1545", {"start": v(-32.95, -33) * mm, "end": v(-32.75, -32.54) * mm});
            skLineSegment(sketch, "E1546", {"start": v(-32.75, -32.54) * mm, "end": v(-32.56, -32.09) * mm});
            skLineSegment(sketch, "E1547", {"start": v(-32.56, -32.09) * mm, "end": v(-32.36, -31.64) * mm});
            skLineSegment(sketch, "E1548", {"start": v(-32.36, -31.64) * mm, "end": v(-32.16, -31.18) * mm});
            skLineSegment(sketch, "E1549", {"start": v(-32.16, -31.18) * mm, "end": v(-31.96, -30.73) * mm});
            skLineSegment(sketch, "E1550", {"start": v(-31.96, -30.73) * mm, "end": v(-31.76, -30.28) * mm});
            skLineSegment(sketch, "E1551", {"start": v(-31.76, -30.28) * mm, "end": v(-31.56, -29.83) * mm});
            skLineSegment(sketch, "E1552", {"start": v(-31.56, -29.83) * mm, "end": v(-31.36, -29.37) * mm});
            skLineSegment(sketch, "E1553", {"start": v(-31.36, -29.37) * mm, "end": v(-31.17, -28.92) * mm});
            skLineSegment(sketch, "E1554", {"start": v(-31.17, -28.92) * mm, "end": v(-30.97, -28.47) * mm});
            skLineSegment(sketch, "E1555", {"start": v(-30.97, -28.47) * mm, "end": v(-30.77, -28.02) * mm});
            skLineSegment(sketch, "E1556", {"start": v(-30.77, -28.02) * mm, "end": v(-30.57, -27.56) * mm});
            skLineSegment(sketch, "E1557", {"start": v(-30.57, -27.56) * mm, "end": v(-30.37, -27.1) * mm});
            skLineSegment(sketch, "E1558", {"start": v(-30.37, -27.1) * mm, "end": v(-30.17, -26.66) * mm});
            skLineSegment(sketch, "E1559", {"start": v(-30.17, -26.66) * mm, "end": v(-29.97, -26.2) * mm});
            skLineSegment(sketch, "E1560", {"start": v(-29.97, -26.2) * mm, "end": v(-29.78, -25.75) * mm});
            skLineSegment(sketch, "E1561", {"start": v(-29.78, -25.75) * mm, "end": v(-29.58, -25.3) * mm});
            skLineSegment(sketch, "E1562", {"start": v(-29.58, -25.3) * mm, "end": v(-29.38, -24.85) * mm});
            skLineSegment(sketch, "E1563", {"start": v(-29.38, -24.85) * mm, "end": v(-29.18, -24.4) * mm});
            skLineSegment(sketch, "E1564", {"start": v(-29.18, -24.4) * mm, "end": v(-28.98, -23.94) * mm});
            skLineSegment(sketch, "E1565", {"start": v(-28.98, -23.94) * mm, "end": v(-28.78, -23.49) * mm});
            skLineSegment(sketch, "E1566", {"start": v(-28.78, -23.49) * mm, "end": v(-28.58, -23.04) * mm});
            skLineSegment(sketch, "E1567", {"start": v(-28.58, -23.04) * mm, "end": v(-28.39, -22.58) * mm});
            skLineSegment(sketch, "E1568", {"start": v(-28.39, -22.58) * mm, "end": v(-28.19, -22.13) * mm});
            skLineSegment(sketch, "E1569", {"start": v(-28.19, -22.13) * mm, "end": v(-27.99, -21.68) * mm});
            skLineSegment(sketch, "E1570", {"start": v(-27.99, -21.68) * mm, "end": v(-27.79, -21.22) * mm});
            skLineSegment(sketch, "E1571", {"start": v(-27.79, -21.22) * mm, "end": v(-27.6, -20.77) * mm});
            skLineSegment(sketch, "E1572", {"start": v(-27.6, -20.77) * mm, "end": v(-27.4, -20.32) * mm});
            skLineSegment(sketch, "E1573", {"start": v(-27.4, -20.32) * mm, "end": v(-27.2, -19.87) * mm});
            skLineSegment(sketch, "E1574", {"start": v(-27.2, -19.87) * mm, "end": v(-27, -19.41) * mm});
            skLineSegment(sketch, "E1575", {"start": v(-27, -19.41) * mm, "end": v(-26.8, -18.96) * mm});
            skLineSegment(sketch, "E1576", {"start": v(-26.8, -18.96) * mm, "end": v(-26.6, -18.5) * mm});
            skLineSegment(sketch, "E1577", {"start": v(-26.6, -18.5) * mm, "end": v(-26.4, -18.06) * mm});
            skLineSegment(sketch, "E1578", {"start": v(-26.4, -18.06) * mm, "end": v(-26.2, -17.6) * mm});
            skLineSegment(sketch, "E1579", {"start": v(-26.2, -17.6) * mm, "end": v(-26, -17.15) * mm});
            skLineSegment(sketch, "E1580", {"start": v(-26, -17.15) * mm, "end": v(-25.8, -16.7) * mm});
            skLineSegment(sketch, "E1581", {"start": v(-25.8, -16.7) * mm, "end": v(-25.6, -16.25) * mm});
            skLineSegment(sketch, "E1582", {"start": v(-25.6, -16.25) * mm, "end": v(-25.4, -15.8) * mm});
            skLineSegment(sketch, "E1583", {"start": v(-25.4, -15.8) * mm, "end": v(-25.2, -15.34) * mm});
            skLineSegment(sketch, "E1584", {"start": v(-25.2, -15.34) * mm, "end": v(-25, -14.89) * mm});
            skLineSegment(sketch, "E1585", {"start": v(-25, -14.89) * mm, "end": v(-24.81, -14.43) * mm});
            skLineSegment(sketch, "E1586", {"start": v(-24.81, -14.43) * mm, "end": v(-24.61, -13.98) * mm});
            skLineSegment(sketch, "E1587", {"start": v(-24.61, -13.98) * mm, "end": v(-24.41, -13.53) * mm});
            skLineSegment(sketch, "E1588", {"start": v(-24.41, -13.53) * mm, "end": v(-24.21, -13.08) * mm});
            skLineSegment(sketch, "E1589", {"start": v(-24.21, -13.08) * mm, "end": v(-24.02, -12.62) * mm});
            skLineSegment(sketch, "E1590", {"start": v(-24.02, -12.62) * mm, "end": v(-23.82, -12.17) * mm});
            skLineSegment(sketch, "E1591", {"start": v(-23.82, -12.17) * mm, "end": v(-23.62, -11.72) * mm});
            skLineSegment(sketch, "E1592", {"start": v(-23.62, -11.72) * mm, "end": v(-23.42, -11.27) * mm});
            skLineSegment(sketch, "E1593", {"start": v(-23.42, -11.27) * mm, "end": v(-23.22, -10.81) * mm});
            skLineSegment(sketch, "E1594", {"start": v(-23.22, -10.81) * mm, "end": v(-23.02, -10.36) * mm});
            skLineSegment(sketch, "E1595", {"start": v(-23.02, -10.36) * mm, "end": v(-22.82, -9.9) * mm});
            skLineSegment(sketch, "E1596", {"start": v(-22.82, -9.9) * mm, "end": v(-22.63, -9.46) * mm});
            skLineSegment(sketch, "E1597", {"start": v(-22.63, -9.46) * mm, "end": v(-22.43, -9) * mm});
            skLineSegment(sketch, "E1598", {"start": v(-22.43, -9) * mm, "end": v(-22.23, -8.55) * mm});
            skLineSegment(sketch, "E1599", {"start": v(-22.23, -8.55) * mm, "end": v(-22.03, -8.1) * mm});
            skLineSegment(sketch, "E1600", {"start": v(-22.03, -8.1) * mm, "end": v(-21.83, -7.64) * mm});
            skLineSegment(sketch, "E1601", {"start": v(-21.83, -7.64) * mm, "end": v(-21.63, -7.2) * mm});
            skLineSegment(sketch, "E1602", {"start": v(-21.63, -7.2) * mm, "end": v(-21.43, -6.74) * mm});
            skLineSegment(sketch, "E1603", {"start": v(-21.43, -6.74) * mm, "end": v(-21.24, -6.29) * mm});
            skLineSegment(sketch, "E1604", {"start": v(-21.24, -6.29) * mm, "end": v(-21.04, -5.83) * mm});
            skLineSegment(sketch, "E1605", {"start": v(-21.04, -5.83) * mm, "end": v(-20.84, -5.38) * mm});
            skLineSegment(sketch, "E1606", {"start": v(-20.84, -5.38) * mm, "end": v(-20.64, -4.93) * mm});
            skLineSegment(sketch, "E1607", {"start": v(-20.64, -4.93) * mm, "end": v(-20.44, -4.48) * mm});
            skLineSegment(sketch, "E1608", {"start": v(-20.44, -4.48) * mm, "end": v(-20.24, -4.02) * mm});
            skLineSegment(sketch, "E1609", {"start": v(-20.24, -4.02) * mm, "end": v(-20.04, -3.57) * mm});
            skLineSegment(sketch, "E1610", {"start": v(-20.04, -3.57) * mm, "end": v(-19.85, -3.12) * mm});
            skLineSegment(sketch, "E1611", {"start": v(-19.85, -3.12) * mm, "end": v(-19.65, -2.66) * mm});
            skLineSegment(sketch, "E1612", {"start": v(-19.65, -2.66) * mm, "end": v(-19.45, -2.21) * mm});
            skLineSegment(sketch, "E1613", {"start": v(-19.45, -2.21) * mm, "end": v(-19.25, -1.76) * mm});
            skLineSegment(sketch, "E1614", {"start": v(-19.25, -1.76) * mm, "end": v(-19.05, -1.3) * mm});
            skLineSegment(sketch, "E1615", {"start": v(-19.05, -1.3) * mm, "end": v(-18.85, -0.85) * mm});
            skLineSegment(sketch, "E1616", {"start": v(-18.85, -0.85) * mm, "end": v(-18.65, -0.4) * mm});
            skLineSegment(sketch, "E1617", {"start": v(-18.65, -0.4) * mm, "end": v(-18.46, 0.05) * mm});
            skLineSegment(sketch, "E1618", {"start": v(-18.46, 0.05) * mm, "end": v(-18.26, 0.5) * mm});
            skLineSegment(sketch, "E1619", {"start": v(-18.26, 0.5) * mm, "end": v(-18.06, 0.96) * mm});
            skLineSegment(sketch, "E1620", {"start": v(-18.06, 0.96) * mm, "end": v(-17.86, 1.4) * mm});
            skLineSegment(sketch, "E1621", {"start": v(-17.86, 1.4) * mm, "end": v(-17.66, 1.86) * mm});
            skLineSegment(sketch, "E1622", {"start": v(-17.66, 1.86) * mm, "end": v(-17.46, 2.31) * mm});
            skLineSegment(sketch, "E1623", {"start": v(-17.46, 2.31) * mm, "end": v(-17.26, 2.77) * mm});
            skLineSegment(sketch, "E1624", {"start": v(-17.26, 2.77) * mm, "end": v(-17.07, 3.22) * mm});
            skLineSegment(sketch, "E1625", {"start": v(-17.07, 3.22) * mm, "end": v(-16.87, 3.67) * mm});
            skLineSegment(sketch, "E1626", {"start": v(-16.87, 3.67) * mm, "end": v(-16.67, 4.13) * mm});
            skLineSegment(sketch, "E1627", {"start": v(-16.67, 4.13) * mm, "end": v(-16.47, 4.58) * mm});
            skLineSegment(sketch, "E1628", {"start": v(-16.47, 4.58) * mm, "end": v(-16.27, 5.03) * mm});
            skLineSegment(sketch, "E1629", {"start": v(-16.27, 5.03) * mm, "end": v(-16.07, 5.48) * mm});
            skLineSegment(sketch, "E1630", {"start": v(-16.07, 5.48) * mm, "end": v(-15.87, 5.94) * mm});
            skLineSegment(sketch, "E1631", {"start": v(-15.87, 5.94) * mm, "end": v(-15.68, 6.39) * mm});
            skLineSegment(sketch, "E1632", {"start": v(-15.68, 6.39) * mm, "end": v(-15.48, 6.84) * mm});
            skLineSegment(sketch, "E1633", {"start": v(-15.48, 6.84) * mm, "end": v(-15.28, 7.3) * mm});
            skLineSegment(sketch, "E1634", {"start": v(-15.28, 7.3) * mm, "end": v(-15.08, 7.75) * mm});
            skLineSegment(sketch, "E1635", {"start": v(-15.08, 7.75) * mm, "end": v(-14.88, 8.2) * mm});
            skLineSegment(sketch, "E1636", {"start": v(-14.88, 8.2) * mm, "end": v(-14.68, 8.65) * mm});
            skLineSegment(sketch, "E1637", {"start": v(-14.68, 8.65) * mm, "end": v(-14.48, 9.1) * mm});
            skLineSegment(sketch, "E1638", {"start": v(-14.48, 9.1) * mm, "end": v(-14.29, 9.56) * mm});
            skLineSegment(sketch, "E1639", {"start": v(-14.29, 9.56) * mm, "end": v(-14.09, 10.01) * mm});
            skLineSegment(sketch, "E1640", {"start": v(-14.09, 10.01) * mm, "end": v(-13.89, 10.46) * mm});
            skLineSegment(sketch, "E1641", {"start": v(-13.89, 10.46) * mm, "end": v(-13.69, 10.92) * mm});
            skLineSegment(sketch, "E1642", {"start": v(-13.69, 10.92) * mm, "end": v(-13.5, 11.37) * mm});
            skLineSegment(sketch, "E1643", {"start": v(-13.5, 11.37) * mm, "end": v(-13.3, 11.82) * mm});
            skLineSegment(sketch, "E1644", {"start": v(-13.3, 11.82) * mm, "end": v(-13.1, 12.27) * mm});
            skLineSegment(sketch, "E1645", {"start": v(-13.1, 12.27) * mm, "end": v(-12.9, 12.73) * mm});
            skLineSegment(sketch, "E1646", {"start": v(-12.9, 12.73) * mm, "end": v(-12.7, 13.18) * mm});
            skLineSegment(sketch, "E1647", {"start": v(-12.7, 13.18) * mm, "end": v(-12.5, 13.63) * mm});
            skLineSegment(sketch, "E1648", {"start": v(-12.5, 13.63) * mm, "end": v(-12.3, 14.08) * mm});
            skLineSegment(sketch, "E1649", {"start": v(-12.3, 14.08) * mm, "end": v(-12.1, 14.54) * mm});
            skLineSegment(sketch, "E1650", {"start": v(-12.1, 14.54) * mm, "end": v(-11.9, 14.99) * mm});
            skLineSegment(sketch, "E1651", {"start": v(-11.9, 14.99) * mm, "end": v(-11.7, 15.44) * mm});
            skLineSegment(sketch, "E1652", {"start": v(-11.7, 15.44) * mm, "end": v(-11.5, 15.9) * mm});
            skLineSegment(sketch, "E1653", {"start": v(-11.5, 15.9) * mm, "end": v(-11.3, 16.35) * mm});
            skLineSegment(sketch, "E1654", {"start": v(-11.3, 16.35) * mm, "end": v(-11.1, 16.8) * mm});
            skLineSegment(sketch, "E1655", {"start": v(-11.1, 16.8) * mm, "end": v(-10.9, 17.25) * mm});
            skLineSegment(sketch, "E1656", {"start": v(-10.9, 17.25) * mm, "end": v(-10.71, 17.7) * mm});
            skLineSegment(sketch, "E1657", {"start": v(-10.71, 17.7) * mm, "end": v(-10.51, 18.16) * mm});
            skLineSegment(sketch, "E1658", {"start": v(-10.51, 18.16) * mm, "end": v(-10.31, 18.61) * mm});
            skLineSegment(sketch, "E1659", {"start": v(-10.31, 18.61) * mm, "end": v(-10.12, 19.06) * mm});
            skLineSegment(sketch, "E1660", {"start": v(-10.12, 19.06) * mm, "end": v(-9.92, 19.52) * mm});
            skLineSegment(sketch, "E1661", {"start": v(-9.92, 19.52) * mm, "end": v(-9.72, 19.97) * mm});
            skLineSegment(sketch, "E1662", {"start": v(-9.72, 19.97) * mm, "end": v(-9.52, 20.42) * mm});
            skLineSegment(sketch, "E1663", {"start": v(-9.52, 20.42) * mm, "end": v(-9.32, 20.87) * mm});
            skLineSegment(sketch, "E1664", {"start": v(-9.32, 20.87) * mm, "end": v(-9.3, 20.92) * mm});
            skLineSegment(sketch, "E1665", {"start": v(-9.3, 20.92) * mm, "end": v(-9.28, 20.96) * mm});
            skLineSegment(sketch, "E1666", {"start": v(-9.28, 20.96) * mm, "end": v(-9.26, 21) * mm});
            skLineSegment(sketch, "E1667", {"start": v(-9.26, 21) * mm, "end": v(-9.23, 21.05) * mm});
            skLineSegment(sketch, "E1668", {"start": v(-9.23, 21.05) * mm, "end": v(-9.2, 21.1) * mm});
            skLineSegment(sketch, "E1669", {"start": v(-9.2, 21.1) * mm, "end": v(-9.18, 21.15) * mm});
            skLineSegment(sketch, "E1670", {"start": v(-9.18, 21.15) * mm, "end": v(-9.16, 21.2) * mm});
            skLineSegment(sketch, "E1671", {"start": v(-9.16, 21.2) * mm, "end": v(-9.13, 21.25) * mm});
            skLineSegment(sketch, "E1672", {"start": v(-9.13, 21.25) * mm, "end": v(-9.1, 21.3) * mm});
            skLineSegment(sketch, "E1673", {"start": v(-9.1, 21.3) * mm, "end": v(-9.07, 21.36) * mm});
            skLineSegment(sketch, "E1674", {"start": v(-9.07, 21.36) * mm, "end": v(-9.04, 21.41) * mm});
            skLineSegment(sketch, "E1675", {"start": v(-9.04, 21.41) * mm, "end": v(-9.01, 21.47) * mm});
            skLineSegment(sketch, "E1676", {"start": v(-9.01, 21.47) * mm, "end": v(-8.98, 21.52) * mm});
            skLineSegment(sketch, "E1677", {"start": v(-8.98, 21.52) * mm, "end": v(-8.95, 21.58) * mm});
            skLineSegment(sketch, "E1678", {"start": v(-8.95, 21.58) * mm, "end": v(-8.92, 21.64) * mm});
            skLineSegment(sketch, "E1679", {"start": v(-8.92, 21.64) * mm, "end": v(-8.88, 21.7) * mm});
            skLineSegment(sketch, "E1680", {"start": v(-8.88, 21.7) * mm, "end": v(-8.84, 21.76) * mm});
            skLineSegment(sketch, "E1681", {"start": v(-8.84, 21.76) * mm, "end": v(-8.8, 21.82) * mm});
            skLineSegment(sketch, "E1682", {"start": v(-8.8, 21.82) * mm, "end": v(-8.77, 21.89) * mm});
            skLineSegment(sketch, "E1683", {"start": v(-8.77, 21.89) * mm, "end": v(-8.73, 21.95) * mm});
            skLineSegment(sketch, "E1684", {"start": v(-8.73, 21.95) * mm, "end": v(-8.7, 22.02) * mm});
            skLineSegment(sketch, "E1685", {"start": v(-8.7, 22.02) * mm, "end": v(-8.65, 22.08) * mm});
            skLineSegment(sketch, "E1686", {"start": v(-8.65, 22.08) * mm, "end": v(-8.6, 22.15) * mm});
            skLineSegment(sketch, "E1687", {"start": v(-8.6, 22.15) * mm, "end": v(-8.56, 22.22) * mm});
            skLineSegment(sketch, "E1688", {"start": v(-8.56, 22.22) * mm, "end": v(-8.52, 22.28) * mm});
            skLineSegment(sketch, "E1689", {"start": v(-8.52, 22.28) * mm, "end": v(-8.48, 22.35) * mm});
            skLineSegment(sketch, "E1690", {"start": v(-8.48, 22.35) * mm, "end": v(-8.43, 22.42) * mm});
            skLineSegment(sketch, "E1691", {"start": v(-8.43, 22.42) * mm, "end": v(-8.38, 22.5) * mm});
            skLineSegment(sketch, "E1692", {"start": v(-8.38, 22.5) * mm, "end": v(-8.33, 22.56) * mm});
            skLineSegment(sketch, "E1693", {"start": v(-8.33, 22.56) * mm, "end": v(-8.28, 22.63) * mm});
            skLineSegment(sketch, "E1694", {"start": v(-8.28, 22.63) * mm, "end": v(-8.23, 22.7) * mm});
            skLineSegment(sketch, "E1695", {"start": v(-8.23, 22.7) * mm, "end": v(-8.18, 22.78) * mm});
            skLineSegment(sketch, "E1696", {"start": v(-8.18, 22.78) * mm, "end": v(-8.13, 22.85) * mm});
            skLineSegment(sketch, "E1697", {"start": v(-8.13, 22.85) * mm, "end": v(-8.07, 22.93) * mm});
            skLineSegment(sketch, "E1698", {"start": v(-8.07, 22.93) * mm, "end": v(-8.02, 23) * mm});
            skLineSegment(sketch, "E1699", {"start": v(-8.02, 23) * mm, "end": v(-7.96, 23.08) * mm});
            skLineSegment(sketch, "E1700", {"start": v(-7.96, 23.08) * mm, "end": v(-7.9, 23.15) * mm});
            skLineSegment(sketch, "E1701", {"start": v(-7.9, 23.15) * mm, "end": v(-7.85, 23.23) * mm});
            skLineSegment(sketch, "E1702", {"start": v(-7.85, 23.23) * mm, "end": v(-7.79, 23.3) * mm});
            skLineSegment(sketch, "E1703", {"start": v(-7.79, 23.3) * mm, "end": v(-7.73, 23.38) * mm});
            skLineSegment(sketch, "E1704", {"start": v(-7.73, 23.38) * mm, "end": v(-7.67, 23.45) * mm});
            skLineSegment(sketch, "E1705", {"start": v(-7.67, 23.45) * mm, "end": v(-7.6, 23.53) * mm});
            skLineSegment(sketch, "E1706", {"start": v(-7.6, 23.53) * mm, "end": v(-7.54, 23.6) * mm});
            skLineSegment(sketch, "E1707", {"start": v(-7.54, 23.6) * mm, "end": v(-7.47, 23.69) * mm});
            skLineSegment(sketch, "E1708", {"start": v(-7.47, 23.69) * mm, "end": v(-7.4, 23.76) * mm});
            skLineSegment(sketch, "E1709", {"start": v(-7.4, 23.76) * mm, "end": v(-7.34, 23.84) * mm});
            skLineSegment(sketch, "E1710", {"start": v(-7.34, 23.84) * mm, "end": v(-7.27, 23.92) * mm});
            skLineSegment(sketch, "E1711", {"start": v(-7.27, 23.92) * mm, "end": v(-7.2, 24) * mm});
            skLineSegment(sketch, "E1712", {"start": v(-7.2, 24) * mm, "end": v(-7.13, 24.08) * mm});
            skLineSegment(sketch, "E1713", {"start": v(-7.13, 24.08) * mm, "end": v(-7.05, 24.15) * mm});
            skLineSegment(sketch, "E1714", {"start": v(-7.05, 24.15) * mm, "end": v(-6.98, 24.23) * mm});
            skLineSegment(sketch, "E1715", {"start": v(-6.98, 24.23) * mm, "end": v(-6.9, 24.31) * mm});
            skLineSegment(sketch, "E1716", {"start": v(-6.9, 24.31) * mm, "end": v(-6.83, 24.39) * mm});
            skLineSegment(sketch, "E1717", {"start": v(-6.83, 24.39) * mm, "end": v(-6.75, 24.47) * mm});
            skLineSegment(sketch, "E1718", {"start": v(-6.75, 24.47) * mm, "end": v(-6.67, 24.55) * mm});
            skLineSegment(sketch, "E1719", {"start": v(-6.67, 24.55) * mm, "end": v(-6.6, 24.62) * mm});
            skLineSegment(sketch, "E1720", {"start": v(-6.6, 24.62) * mm, "end": v(-6.51, 24.7) * mm});
            skLineSegment(sketch, "E1721", {"start": v(-6.51, 24.7) * mm, "end": v(-6.43, 24.78) * mm});
            skLineSegment(sketch, "E1722", {"start": v(-6.43, 24.78) * mm, "end": v(-6.35, 24.86) * mm});
            skLineSegment(sketch, "E1723", {"start": v(-6.35, 24.86) * mm, "end": v(-6.26, 24.94) * mm});
            skLineSegment(sketch, "E1724", {"start": v(-6.26, 24.94) * mm, "end": v(-6.17, 25.01) * mm});
            skLineSegment(sketch, "E1725", {"start": v(-6.17, 25.01) * mm, "end": v(-6.09, 25.1) * mm});
            skLineSegment(sketch, "E1726", {"start": v(-6.09, 25.1) * mm, "end": v(-6, 25.17) * mm});
            skLineSegment(sketch, "E1727", {"start": v(-6, 25.17) * mm, "end": v(-5.9, 25.24) * mm});
            skLineSegment(sketch, "E1728", {"start": v(-5.9, 25.24) * mm, "end": v(-5.82, 25.32) * mm});
            skLineSegment(sketch, "E1729", {"start": v(-5.82, 25.32) * mm, "end": v(-5.72, 25.4) * mm});
            skLineSegment(sketch, "E1730", {"start": v(-5.72, 25.4) * mm, "end": v(-5.63, 25.47) * mm});
            skLineSegment(sketch, "E1731", {"start": v(-5.63, 25.47) * mm, "end": v(-5.53, 25.55) * mm});
            skLineSegment(sketch, "E1732", {"start": v(-5.53, 25.55) * mm, "end": v(-5.44, 25.62) * mm});
            skLineSegment(sketch, "E1733", {"start": v(-5.44, 25.62) * mm, "end": v(-5.34, 25.7) * mm});
            skLineSegment(sketch, "E1734", {"start": v(-5.34, 25.7) * mm, "end": v(-5.24, 25.77) * mm});
            skLineSegment(sketch, "E1735", {"start": v(-5.24, 25.77) * mm, "end": v(-5.14, 25.84) * mm});
            skLineSegment(sketch, "E1736", {"start": v(-5.14, 25.84) * mm, "end": v(-5.03, 25.92) * mm});
            skLineSegment(sketch, "E1737", {"start": v(-5.03, 25.92) * mm, "end": v(-4.93, 25.99) * mm});
            skLineSegment(sketch, "E1738", {"start": v(-4.93, 25.99) * mm, "end": v(-4.83, 26.06) * mm});
            skLineSegment(sketch, "E1739", {"start": v(-4.83, 26.06) * mm, "end": v(-4.72, 26.13) * mm});
            skLineSegment(sketch, "E1740", {"start": v(-4.72, 26.13) * mm, "end": v(-4.61, 26.2) * mm});
            skLineSegment(sketch, "E1741", {"start": v(-4.61, 26.2) * mm, "end": v(-4.5, 26.27) * mm});
            skLineSegment(sketch, "E1742", {"start": v(-4.5, 26.27) * mm, "end": v(-4.4, 26.34) * mm});
            skLineSegment(sketch, "E1743", {"start": v(-4.4, 26.34) * mm, "end": v(-4.28, 26.4) * mm});
            skLineSegment(sketch, "E1744", {"start": v(-4.28, 26.4) * mm, "end": v(-4.17, 26.48) * mm});
            skLineSegment(sketch, "E1745", {"start": v(-4.17, 26.48) * mm, "end": v(-4.05, 26.54) * mm});
            skLineSegment(sketch, "E1746", {"start": v(-4.05, 26.54) * mm, "end": v(-3.94, 26.6) * mm});
            skLineSegment(sketch, "E1747", {"start": v(-3.94, 26.6) * mm, "end": v(-3.82, 26.67) * mm});
            skLineSegment(sketch, "E1748", {"start": v(-3.82, 26.67) * mm, "end": v(-3.7, 26.74) * mm});
            skLineSegment(sketch, "E1749", {"start": v(-3.7, 26.74) * mm, "end": v(-3.58, 26.8) * mm});
            skLineSegment(sketch, "E1750", {"start": v(-3.58, 26.8) * mm, "end": v(-3.46, 26.86) * mm});
            skLineSegment(sketch, "E1751", {"start": v(-3.46, 26.86) * mm, "end": v(-3.33, 26.92) * mm});
            skLineSegment(sketch, "E1752", {"start": v(-3.33, 26.92) * mm, "end": v(-3.2, 26.98) * mm});
            skLineSegment(sketch, "E1753", {"start": v(-3.2, 26.98) * mm, "end": v(-3.08, 27.04) * mm});
            skLineSegment(sketch, "E1754", {"start": v(-3.08, 27.04) * mm, "end": v(-2.96, 27.1) * mm});
            skLineSegment(sketch, "E1755", {"start": v(-2.96, 27.1) * mm, "end": v(-2.83, 27.16) * mm});
            skLineSegment(sketch, "E1756", {"start": v(-2.83, 27.16) * mm, "end": v(-2.7, 27.22) * mm});
            skLineSegment(sketch, "E1757", {"start": v(-2.7, 27.22) * mm, "end": v(-2.56, 27.27) * mm});
            skLineSegment(sketch, "E1758", {"start": v(-2.56, 27.27) * mm, "end": v(-2.43, 27.33) * mm});
            skLineSegment(sketch, "E1759", {"start": v(-2.43, 27.33) * mm, "end": v(-2.3, 27.38) * mm});
            skLineSegment(sketch, "E1760", {"start": v(-2.3, 27.38) * mm, "end": v(-2.16, 27.43) * mm});
            skLineSegment(sketch, "E1761", {"start": v(-2.16, 27.43) * mm, "end": v(-2.02, 27.48) * mm});
            skLineSegment(sketch, "E1762", {"start": v(-2.02, 27.48) * mm, "end": v(-1.88, 27.53) * mm});
            skLineSegment(sketch, "E1763", {"start": v(-1.88, 27.53) * mm, "end": v(-1.74, 27.58) * mm});
            skLineSegment(sketch, "E1764", {"start": v(-1.74, 27.58) * mm, "end": v(-1.6, 27.62) * mm});
            skLineSegment(sketch, "E1765", {"start": v(-1.6, 27.62) * mm, "end": v(-1.45, 27.67) * mm});
            skLineSegment(sketch, "E1766", {"start": v(-1.45, 27.67) * mm, "end": v(-1.3, 27.71) * mm});
            skLineSegment(sketch, "E1767", {"start": v(-1.3, 27.71) * mm, "end": v(-1.16, 27.75) * mm});
            skLineSegment(sketch, "E1768", {"start": v(-1.16, 27.75) * mm, "end": v(-1.01, 27.8) * mm});
            skLineSegment(sketch, "E1769", {"start": v(-1.01, 27.8) * mm, "end": v(-0.86, 27.84) * mm});
            skLineSegment(sketch, "E1770", {"start": v(-0.86, 27.84) * mm, "end": v(-0.7, 27.87) * mm});
            skLineSegment(sketch, "E1771", {"start": v(-0.7, 27.87) * mm, "end": v(-0.56, 27.91) * mm});
            skLineSegment(sketch, "E1772", {"start": v(-0.56, 27.91) * mm, "end": v(-0.4, 27.95) * mm});
            skLineSegment(sketch, "E1773", {"start": v(-0.4, 27.95) * mm, "end": v(-0.24, 27.98) * mm});
            skLineSegment(sketch, "E1774", {"start": v(-0.24, 27.98) * mm, "end": v(-0.09, 28.01) * mm});
            skLineSegment(sketch, "E1775", {"start": v(-0.09, 28.01) * mm, "end": v(0.07, 28.04) * mm});
            skLineSegment(sketch, "E1776", {"start": v(0.07, 28.04) * mm, "end": v(0.24, 28.07) * mm});
            skLineSegment(sketch, "E1777", {"start": v(0.24, 28.07) * mm, "end": v(0.4, 28.1) * mm});
            skLineSegment(sketch, "E1778", {"start": v(0.4, 28.1) * mm, "end": v(0.56, 28.12) * mm});
            skLineSegment(sketch, "E1779", {"start": v(0.56, 28.12) * mm, "end": v(0.73, 28.15) * mm});
            skLineSegment(sketch, "E1780", {"start": v(0.73, 28.15) * mm, "end": v(0.9, 28.17) * mm});
            skLineSegment(sketch, "E1781", {"start": v(0.9, 28.17) * mm, "end": v(1.07, 28.19) * mm});
            skLineSegment(sketch, "E1782", {"start": v(1.07, 28.19) * mm, "end": v(1.24, 28.2) * mm});
            skLineSegment(sketch, "E1783", {"start": v(1.24, 28.2) * mm, "end": v(1.41, 28.22) * mm});
            skLineSegment(sketch, "E1784", {"start": v(1.41, 28.22) * mm, "end": v(1.59, 28.24) * mm});
            skLineSegment(sketch, "E1785", {"start": v(1.59, 28.24) * mm, "end": v(1.76, 28.25) * mm});
            skLineSegment(sketch, "E1786", {"start": v(1.76, 28.25) * mm, "end": v(1.94, 28.26) * mm});
            skLineSegment(sketch, "E1787", {"start": v(1.94, 28.26) * mm, "end": v(2.12, 28.27) * mm});
            skLineSegment(sketch, "E1788", {"start": v(2.12, 28.27) * mm, "end": v(2.3, 28.28) * mm});
            skLineSegment(sketch, "E1789", {"start": v(2.3, 28.28) * mm, "end": v(2.48, 28.28) * mm});
            skLineSegment(sketch, "E1790", {"start": v(2.48, 28.28) * mm, "end": v(2.67, 28.29) * mm});
            skLineSegment(sketch, "E1791", {"start": v(2.67, 28.29) * mm, "end": v(2.85, 28.29) * mm});
            skLineSegment(sketch, "E1792", {"start": v(2.85, 28.29) * mm, "end": v(2.86, 28.29) * mm});
            skLineSegment(sketch, "E1793", {"start": v(2.86, 28.29) * mm, "end": v(2.86, 28.29) * mm});
            skLineSegment(sketch, "E1794", {"start": v(2.86, 28.29) * mm, "end": v(2.87, 28.29) * mm});
            skLineSegment(sketch, "E1795", {"start": v(2.87, 28.29) * mm, "end": v(2.88, 28.29) * mm});
            skLineSegment(sketch, "E1796", {"start": v(2.88, 28.29) * mm, "end": v(2.88, 28.29) * mm});
            skLineSegment(sketch, "E1797", {"start": v(2.88, 28.29) * mm, "end": v(2.9, 28.29) * mm});
            skLineSegment(sketch, "E1798", {"start": v(2.9, 28.29) * mm, "end": v(2.9, 28.29) * mm});
            skLineSegment(sketch, "E1799", {"start": v(2.9, 28.29) * mm, "end": v(2.91, 28.29) * mm});
            skLineSegment(sketch, "E1800", {"start": v(2.91, 28.29) * mm, "end": v(2.93, 28.29) * mm});
            skLineSegment(sketch, "E1801", {"start": v(2.93, 28.29) * mm, "end": v(2.94, 28.29) * mm});
            skLineSegment(sketch, "E1802", {"start": v(2.94, 28.29) * mm, "end": v(2.95, 28.28) * mm});
            skLineSegment(sketch, "E1803", {"start": v(2.95, 28.28) * mm, "end": v(2.97, 28.28) * mm});
            skLineSegment(sketch, "E1804", {"start": v(2.97, 28.28) * mm, "end": v(2.99, 28.28) * mm});
            skLineSegment(sketch, "E1805", {"start": v(2.99, 28.28) * mm, "end": v(3, 28.28) * mm});
            skLineSegment(sketch, "E1806", {"start": v(3, 28.28) * mm, "end": v(3.02, 28.28) * mm});
            skLineSegment(sketch, "E1807", {"start": v(3.02, 28.28) * mm, "end": v(3.04, 28.28) * mm});
            skLineSegment(sketch, "E1808", {"start": v(3.04, 28.28) * mm, "end": v(3.06, 28.28) * mm});
            skLineSegment(sketch, "E1809", {"start": v(3.06, 28.28) * mm, "end": v(3.08, 28.27) * mm});
            skLineSegment(sketch, "E1810", {"start": v(3.08, 28.27) * mm, "end": v(3.1, 28.27) * mm});
            skLineSegment(sketch, "E1811", {"start": v(3.1, 28.27) * mm, "end": v(3.12, 28.27) * mm});
            skLineSegment(sketch, "E1812", {"start": v(3.12, 28.27) * mm, "end": v(3.15, 28.27) * mm});
            skLineSegment(sketch, "E1813", {"start": v(3.15, 28.27) * mm, "end": v(3.17, 28.27) * mm});
            skLineSegment(sketch, "E1814", {"start": v(3.17, 28.27) * mm, "end": v(3.2, 28.26) * mm});
            skLineSegment(sketch, "E1815", {"start": v(3.2, 28.26) * mm, "end": v(3.22, 28.26) * mm});
            skLineSegment(sketch, "E1816", {"start": v(3.22, 28.26) * mm, "end": v(3.25, 28.26) * mm});
            skLineSegment(sketch, "E1817", {"start": v(3.25, 28.26) * mm, "end": v(3.27, 28.25) * mm});
            skLineSegment(sketch, "E1818", {"start": v(3.27, 28.25) * mm, "end": v(3.3, 28.25) * mm});
            skLineSegment(sketch, "E1819", {"start": v(3.3, 28.25) * mm, "end": v(3.33, 28.24) * mm});
            skLineSegment(sketch, "E1820", {"start": v(3.33, 28.24) * mm, "end": v(3.36, 28.24) * mm});
            skLineSegment(sketch, "E1821", {"start": v(3.36, 28.24) * mm, "end": v(3.39, 28.23) * mm});
            skLineSegment(sketch, "E1822", {"start": v(3.39, 28.23) * mm, "end": v(3.42, 28.23) * mm});
            skLineSegment(sketch, "E1823", {"start": v(3.42, 28.23) * mm, "end": v(3.45, 28.22) * mm});
            skLineSegment(sketch, "E1824", {"start": v(3.45, 28.22) * mm, "end": v(3.48, 28.22) * mm});
            skLineSegment(sketch, "E1825", {"start": v(3.48, 28.22) * mm, "end": v(3.5, 28.2) * mm});
            skLineSegment(sketch, "E1826", {"start": v(3.5, 28.2) * mm, "end": v(3.54, 28.2) * mm});
            skLineSegment(sketch, "E1827", {"start": v(3.54, 28.2) * mm, "end": v(3.57, 28.2) * mm});
            skLineSegment(sketch, "E1828", {"start": v(3.57, 28.2) * mm, "end": v(3.6, 28.19) * mm});
            skLineSegment(sketch, "E1829", {"start": v(3.6, 28.19) * mm, "end": v(3.64, 28.18) * mm});
            skLineSegment(sketch, "E1830", {"start": v(3.64, 28.18) * mm, "end": v(3.67, 28.17) * mm});
            skLineSegment(sketch, "E1831", {"start": v(3.67, 28.17) * mm, "end": v(3.7, 28.16) * mm});
            skLineSegment(sketch, "E1832", {"start": v(3.7, 28.16) * mm, "end": v(3.74, 28.15) * mm});
            skLineSegment(sketch, "E1833", {"start": v(3.74, 28.15) * mm, "end": v(3.77, 28.14) * mm});
            skLineSegment(sketch, "E1834", {"start": v(3.77, 28.14) * mm, "end": v(3.8, 28.13) * mm});
            skLineSegment(sketch, "E1835", {"start": v(3.8, 28.13) * mm, "end": v(3.84, 28.12) * mm});
            skLineSegment(sketch, "E1836", {"start": v(3.84, 28.12) * mm, "end": v(3.88, 28.1) * mm});
            skLineSegment(sketch, "E1837", {"start": v(3.88, 28.1) * mm, "end": v(3.91, 28.1) * mm});
            skLineSegment(sketch, "E1838", {"start": v(3.91, 28.1) * mm, "end": v(3.95, 28.08) * mm});
            skLineSegment(sketch, "E1839", {"start": v(3.95, 28.08) * mm, "end": v(3.98, 28.07) * mm});
            skLineSegment(sketch, "E1840", {"start": v(3.98, 28.07) * mm, "end": v(4.02, 28.06) * mm});
            skLineSegment(sketch, "E1841", {"start": v(4.02, 28.06) * mm, "end": v(4.06, 28.04) * mm});
            skLineSegment(sketch, "E1842", {"start": v(4.06, 28.04) * mm, "end": v(4.1, 28.03) * mm});
            skLineSegment(sketch, "E1843", {"start": v(4.1, 28.03) * mm, "end": v(4.13, 28.01) * mm});
            skLineSegment(sketch, "E1844", {"start": v(4.13, 28.01) * mm, "end": v(4.16, 28) * mm});
            skLineSegment(sketch, "E1845", {"start": v(4.16, 28) * mm, "end": v(4.2, 27.98) * mm});
            skLineSegment(sketch, "E1846", {"start": v(4.2, 27.98) * mm, "end": v(4.24, 27.96) * mm});
            skLineSegment(sketch, "E1847", {"start": v(4.24, 27.96) * mm, "end": v(4.27, 27.94) * mm});
            skLineSegment(sketch, "E1848", {"start": v(4.27, 27.94) * mm, "end": v(4.3, 27.93) * mm});
            skLineSegment(sketch, "E1849", {"start": v(4.3, 27.93) * mm, "end": v(4.34, 27.9) * mm});
            skLineSegment(sketch, "E1850", {"start": v(4.34, 27.9) * mm, "end": v(4.38, 27.89) * mm});
            skLineSegment(sketch, "E1851", {"start": v(4.38, 27.89) * mm, "end": v(4.42, 27.87) * mm});
            skLineSegment(sketch, "E1852", {"start": v(4.42, 27.87) * mm, "end": v(4.45, 27.85) * mm});
            skLineSegment(sketch, "E1853", {"start": v(4.45, 27.85) * mm, "end": v(4.49, 27.82) * mm});
            skLineSegment(sketch, "E1854", {"start": v(4.49, 27.82) * mm, "end": v(4.52, 27.8) * mm});
            skLineSegment(sketch, "E1855", {"start": v(4.52, 27.8) * mm, "end": v(4.56, 27.78) * mm});
            skLineSegment(sketch, "E1856", {"start": v(4.56, 27.78) * mm, "end": v(4.6, 27.75) * mm});
            skLineSegment(sketch, "E1857", {"start": v(4.6, 27.75) * mm, "end": v(4.63, 27.73) * mm});
            skLineSegment(sketch, "E1858", {"start": v(4.63, 27.73) * mm, "end": v(4.66, 27.7) * mm});
            skLineSegment(sketch, "E1859", {"start": v(4.66, 27.7) * mm, "end": v(4.7, 27.68) * mm});
            skLineSegment(sketch, "E1860", {"start": v(4.7, 27.68) * mm, "end": v(4.73, 27.65) * mm});
            skLineSegment(sketch, "E1861", {"start": v(4.73, 27.65) * mm, "end": v(4.77, 27.62) * mm});
            skLineSegment(sketch, "E1862", {"start": v(4.77, 27.62) * mm, "end": v(4.8, 27.6) * mm});
            skLineSegment(sketch, "E1863", {"start": v(4.8, 27.6) * mm, "end": v(4.83, 27.56) * mm});
            skLineSegment(sketch, "E1864", {"start": v(4.83, 27.56) * mm, "end": v(4.87, 27.53) * mm});
            skLineSegment(sketch, "E1865", {"start": v(4.87, 27.53) * mm, "end": v(4.9, 27.5) * mm});
            skLineSegment(sketch, "E1866", {"start": v(4.9, 27.5) * mm, "end": v(4.93, 27.47) * mm});
            skLineSegment(sketch, "E1867", {"start": v(4.93, 27.47) * mm, "end": v(4.96, 27.44) * mm});
            skLineSegment(sketch, "E1868", {"start": v(4.96, 27.44) * mm, "end": v(5, 27.4) * mm});
            skLineSegment(sketch, "E1869", {"start": v(5, 27.4) * mm, "end": v(5.02, 27.37) * mm});
            skLineSegment(sketch, "E1870", {"start": v(5.02, 27.37) * mm, "end": v(5.05, 27.34) * mm});
            skLineSegment(sketch, "E1871", {"start": v(5.05, 27.34) * mm, "end": v(5.08, 27.3) * mm});
            skLineSegment(sketch, "E1872", {"start": v(5.08, 27.3) * mm, "end": v(5.11, 27.26) * mm});
            skLineSegment(sketch, "E1873", {"start": v(5.11, 27.26) * mm, "end": v(5.14, 27.22) * mm});
            skLineSegment(sketch, "E1874", {"start": v(5.14, 27.22) * mm, "end": v(5.17, 27.18) * mm});
            skLineSegment(sketch, "E1875", {"start": v(5.17, 27.18) * mm, "end": v(5.2, 27.15) * mm});
            skLineSegment(sketch, "E1876", {"start": v(5.2, 27.15) * mm, "end": v(5.22, 27.1) * mm});
            skLineSegment(sketch, "E1877", {"start": v(5.22, 27.1) * mm, "end": v(5.25, 27.06) * mm});
            skLineSegment(sketch, "E1878", {"start": v(5.25, 27.06) * mm, "end": v(5.27, 27.02) * mm});
            skLineSegment(sketch, "E1879", {"start": v(5.27, 27.02) * mm, "end": v(5.3, 26.98) * mm});
            skLineSegment(sketch, "E1880", {"start": v(5.3, 26.98) * mm, "end": v(5.32, 26.93) * mm});
            skLineSegment(sketch, "E1881", {"start": v(5.32, 26.93) * mm, "end": v(5.34, 26.89) * mm});
            skLineSegment(sketch, "E1882", {"start": v(5.34, 26.89) * mm, "end": v(5.36, 26.84) * mm});
            skLineSegment(sketch, "E1883", {"start": v(5.36, 26.84) * mm, "end": v(5.38, 26.8) * mm});
            skLineSegment(sketch, "E1884", {"start": v(5.38, 26.8) * mm, "end": v(5.4, 26.74) * mm});
            skLineSegment(sketch, "E1885", {"start": v(5.4, 26.74) * mm, "end": v(5.42, 26.7) * mm});
            skLineSegment(sketch, "E1886", {"start": v(5.42, 26.7) * mm, "end": v(5.44, 26.64) * mm});
            skLineSegment(sketch, "E1887", {"start": v(5.44, 26.64) * mm, "end": v(5.46, 26.59) * mm});
            skLineSegment(sketch, "E1888", {"start": v(5.46, 26.59) * mm, "end": v(5.48, 26.54) * mm});
            skLineSegment(sketch, "E1889", {"start": v(5.48, 26.54) * mm, "end": v(5.5, 26.48) * mm});
            skLineSegment(sketch, "E1890", {"start": v(5.5, 26.48) * mm, "end": v(5.5, 26.43) * mm});
            skLineSegment(sketch, "E1891", {"start": v(5.5, 26.43) * mm, "end": v(5.52, 26.37) * mm});
            skLineSegment(sketch, "E1892", {"start": v(5.52, 26.37) * mm, "end": v(5.53, 26.31) * mm});
            skLineSegment(sketch, "E1893", {"start": v(5.53, 26.31) * mm, "end": v(5.54, 26.25) * mm});
            skLineSegment(sketch, "E1894", {"start": v(5.54, 26.25) * mm, "end": v(5.55, 26.2) * mm});
            skLineSegment(sketch, "E1895", {"start": v(5.55, 26.2) * mm, "end": v(5.56, 26.13) * mm});
            skLineSegment(sketch, "E1896", {"start": v(5.56, 26.13) * mm, "end": v(5.57, 26.07) * mm});
            skLineSegment(sketch, "E1897", {"start": v(5.57, 26.07) * mm, "end": v(5.58, 26) * mm});
            skLineSegment(sketch, "E1898", {"start": v(5.58, 26) * mm, "end": v(5.59, 25.94) * mm});
            skLineSegment(sketch, "E1899", {"start": v(5.59, 25.94) * mm, "end": v(5.59, 25.88) * mm});
            skLineSegment(sketch, "E1900", {"start": v(5.59, 25.88) * mm, "end": v(5.6, 25.8) * mm});
            skLineSegment(sketch, "E1901", {"start": v(5.6, 25.8) * mm, "end": v(5.6, 25.74) * mm});
            skLineSegment(sketch, "E1902", {"start": v(5.6, 25.74) * mm, "end": v(5.6, 25.67) * mm});
            skLineSegment(sketch, "E1903", {"start": v(5.6, 25.67) * mm, "end": v(5.6, 25.6) * mm});
            skLineSegment(sketch, "E1904", {"start": v(5.6, 25.6) * mm, "end": v(5.6, 25.53) * mm});
            skLineSegment(sketch, "E1905", {"start": v(5.6, 25.53) * mm, "end": v(5.6, 25.45) * mm});
            skLineSegment(sketch, "E1906", {"start": v(5.6, 25.45) * mm, "end": v(5.59, 25.38) * mm});
            skLineSegment(sketch, "E1907", {"start": v(5.59, 25.38) * mm, "end": v(5.58, 25.3) * mm});
            skLineSegment(sketch, "E1908", {"start": v(5.58, 25.3) * mm, "end": v(5.58, 25.23) * mm});
            skLineSegment(sketch, "E1909", {"start": v(5.58, 25.23) * mm, "end": v(5.57, 25.15) * mm});
            skLineSegment(sketch, "E1910", {"start": v(5.57, 25.15) * mm, "end": v(5.56, 25.07) * mm});
            skLineSegment(sketch, "E1911", {"start": v(5.56, 25.07) * mm, "end": v(5.55, 24.99) * mm});
            skLineSegment(sketch, "E1912", {"start": v(5.55, 24.99) * mm, "end": v(5.54, 24.9) * mm});
            skLineSegment(sketch, "E1913", {"start": v(5.54, 24.9) * mm, "end": v(5.52, 24.82) * mm});
            skLineSegment(sketch, "E1914", {"start": v(5.52, 24.82) * mm, "end": v(5.5, 24.73) * mm});
            skLineSegment(sketch, "E1915", {"start": v(5.5, 24.73) * mm, "end": v(5.49, 24.65) * mm});
            skLineSegment(sketch, "E1916", {"start": v(5.49, 24.65) * mm, "end": v(5.47, 24.56) * mm});
            skLineSegment(sketch, "E1917", {"start": v(5.47, 24.56) * mm, "end": v(5.45, 24.47) * mm});
            skLineSegment(sketch, "E1918", {"start": v(5.45, 24.47) * mm, "end": v(5.43, 24.4) * mm});
            skLineSegment(sketch, "E1919", {"start": v(5.43, 24.4) * mm, "end": v(5.41, 24.34) * mm});
            skLineSegment(sketch, "E1920", {"start": v(5.41, 24.34) * mm, "end": v(5.4, 24.28) * mm});
            skLineSegment(sketch, "E1921", {"start": v(5.4, 24.28) * mm, "end": v(5.37, 24.22) * mm});
            skLineSegment(sketch, "E1922", {"start": v(5.37, 24.22) * mm, "end": v(5.36, 24.15) * mm});
            skLineSegment(sketch, "E1923", {"start": v(5.36, 24.15) * mm, "end": v(5.34, 24.09) * mm});
            skLineSegment(sketch, "E1924", {"start": v(5.34, 24.09) * mm, "end": v(5.32, 24.03) * mm});
            skLineSegment(sketch, "E1925", {"start": v(5.32, 24.03) * mm, "end": v(5.3, 23.96) * mm});
            skLineSegment(sketch, "E1926", {"start": v(5.3, 23.96) * mm, "end": v(5.28, 23.9) * mm});
            skLineSegment(sketch, "E1927", {"start": v(5.28, 23.9) * mm, "end": v(5.26, 23.83) * mm});
            skLineSegment(sketch, "E1928", {"start": v(5.26, 23.83) * mm, "end": v(5.24, 23.77) * mm});
            skLineSegment(sketch, "E1929", {"start": v(5.24, 23.77) * mm, "end": v(5.22, 23.7) * mm});
            skLineSegment(sketch, "E1930", {"start": v(5.22, 23.7) * mm, "end": v(5.2, 23.64) * mm});
            skLineSegment(sketch, "E1931", {"start": v(5.2, 23.64) * mm, "end": v(5.18, 23.58) * mm});
            skLineSegment(sketch, "E1932", {"start": v(5.18, 23.58) * mm, "end": v(5.15, 23.52) * mm});
            skLineSegment(sketch, "E1933", {"start": v(5.15, 23.52) * mm, "end": v(5.13, 23.45) * mm});
            skLineSegment(sketch, "E1934", {"start": v(5.13, 23.45) * mm, "end": v(5.11, 23.4) * mm});
            skLineSegment(sketch, "E1935", {"start": v(5.11, 23.4) * mm, "end": v(5.1, 23.33) * mm});
            skLineSegment(sketch, "E1936", {"start": v(5.1, 23.33) * mm, "end": v(5.07, 23.26) * mm});
            skLineSegment(sketch, "E1937", {"start": v(5.07, 23.26) * mm, "end": v(5.05, 23.2) * mm});
            skLineSegment(sketch, "E1938", {"start": v(5.05, 23.2) * mm, "end": v(5.03, 23.14) * mm});
            skLineSegment(sketch, "E1939", {"start": v(5.03, 23.14) * mm, "end": v(5, 23.08) * mm});
            skLineSegment(sketch, "E1940", {"start": v(5, 23.08) * mm, "end": v(4.99, 23.01) * mm});
            skLineSegment(sketch, "E1941", {"start": v(4.99, 23.01) * mm, "end": v(4.97, 22.95) * mm});
            skLineSegment(sketch, "E1942", {"start": v(4.97, 22.95) * mm, "end": v(4.94, 22.89) * mm});
            skLineSegment(sketch, "E1943", {"start": v(4.94, 22.89) * mm, "end": v(4.92, 22.82) * mm});
            skLineSegment(sketch, "E1944", {"start": v(4.92, 22.82) * mm, "end": v(4.9, 22.76) * mm});
            skLineSegment(sketch, "E1945", {"start": v(4.9, 22.76) * mm, "end": v(4.88, 22.7) * mm});
            skLineSegment(sketch, "E1946", {"start": v(4.88, 22.7) * mm, "end": v(4.86, 22.64) * mm});
            skLineSegment(sketch, "E1947", {"start": v(4.86, 22.64) * mm, "end": v(4.84, 22.57) * mm});
            skLineSegment(sketch, "E1948", {"start": v(4.84, 22.57) * mm, "end": v(4.81, 22.51) * mm});
            skLineSegment(sketch, "E1949", {"start": v(4.81, 22.51) * mm, "end": v(4.8, 22.45) * mm});
            skLineSegment(sketch, "E1950", {"start": v(4.8, 22.45) * mm, "end": v(4.77, 22.39) * mm});
            skLineSegment(sketch, "E1951", {"start": v(4.77, 22.39) * mm, "end": v(4.75, 22.33) * mm});
            skLineSegment(sketch, "E1952", {"start": v(4.75, 22.33) * mm, "end": v(4.73, 22.26) * mm});
            skLineSegment(sketch, "E1953", {"start": v(4.73, 22.26) * mm, "end": v(4.7, 22.2) * mm});
            skLineSegment(sketch, "E1954", {"start": v(4.7, 22.2) * mm, "end": v(4.68, 22.14) * mm});
            skLineSegment(sketch, "E1955", {"start": v(4.68, 22.14) * mm, "end": v(4.66, 22.08) * mm});
            skLineSegment(sketch, "E1956", {"start": v(4.66, 22.08) * mm, "end": v(4.64, 22.02) * mm});
            skLineSegment(sketch, "E1957", {"start": v(4.64, 22.02) * mm, "end": v(4.61, 21.96) * mm});
            skLineSegment(sketch, "E1958", {"start": v(4.61, 21.96) * mm, "end": v(4.6, 21.9) * mm});
            skLineSegment(sketch, "E1959", {"start": v(4.6, 21.9) * mm, "end": v(4.57, 21.83) * mm});
            skLineSegment(sketch, "E1960", {"start": v(4.57, 21.83) * mm, "end": v(4.55, 21.77) * mm});
            skLineSegment(sketch, "E1961", {"start": v(4.55, 21.77) * mm, "end": v(4.52, 21.71) * mm});
            skLineSegment(sketch, "E1962", {"start": v(4.52, 21.71) * mm, "end": v(4.5, 21.65) * mm});
            skLineSegment(sketch, "E1963", {"start": v(4.5, 21.65) * mm, "end": v(4.48, 21.6) * mm});
            skLineSegment(sketch, "E1964", {"start": v(4.48, 21.6) * mm, "end": v(4.46, 21.53) * mm});
            skLineSegment(sketch, "E1965", {"start": v(4.46, 21.53) * mm, "end": v(4.43, 21.47) * mm});
            skLineSegment(sketch, "E1966", {"start": v(4.43, 21.47) * mm, "end": v(4.41, 21.41) * mm});
            skLineSegment(sketch, "E1967", {"start": v(4.41, 21.41) * mm, "end": v(4.39, 21.35) * mm});
            skLineSegment(sketch, "E1968", {"start": v(4.39, 21.35) * mm, "end": v(4.37, 21.3) * mm});
            skLineSegment(sketch, "E1969", {"start": v(4.37, 21.3) * mm, "end": v(4.34, 21.23) * mm});
            skLineSegment(sketch, "E1970", {"start": v(4.34, 21.23) * mm, "end": v(4.32, 21.17) * mm});
            skLineSegment(sketch, "E1971", {"start": v(4.32, 21.17) * mm, "end": v(4.3, 21.12) * mm});
            skLineSegment(sketch, "E1972", {"start": v(4.3, 21.12) * mm, "end": v(4.28, 21.06) * mm});
            skLineSegment(sketch, "E1973", {"start": v(4.28, 21.06) * mm, "end": v(4.25, 21) * mm});
            skLineSegment(sketch, "E1974", {"start": v(4.25, 21) * mm, "end": v(4.23, 20.94) * mm});
            skLineSegment(sketch, "E1975", {"start": v(4.23, 20.94) * mm, "end": v(4.2, 20.88) * mm});
            skLineSegment(sketch, "E1976", {"start": v(4.2, 20.88) * mm, "end": v(4.19, 20.82) * mm});
            skLineSegment(sketch, "E1977", {"start": v(4.19, 20.82) * mm, "end": v(4.16, 20.77) * mm});
            skLineSegment(sketch, "E1978", {"start": v(4.16, 20.77) * mm, "end": v(4.14, 20.7) * mm});
            skLineSegment(sketch, "E1979", {"start": v(4.14, 20.7) * mm, "end": v(4.12, 20.65) * mm});
            skLineSegment(sketch, "E1980", {"start": v(4.12, 20.65) * mm, "end": v(4.1, 20.6) * mm});
            skLineSegment(sketch, "E1981", {"start": v(4.1, 20.6) * mm, "end": v(4.07, 20.54) * mm});
            skLineSegment(sketch, "E1982", {"start": v(4.07, 20.54) * mm, "end": v(4.05, 20.48) * mm});
            skLineSegment(sketch, "E1983", {"start": v(4.05, 20.48) * mm, "end": v(4.03, 20.43) * mm});
            skLineSegment(sketch, "E1984", {"start": v(4.03, 20.43) * mm, "end": v(4, 20.37) * mm});
            skLineSegment(sketch, "E1985", {"start": v(4, 20.37) * mm, "end": v(3.98, 20.31) * mm});
            skLineSegment(sketch, "E1986", {"start": v(3.98, 20.31) * mm, "end": v(3.96, 20.26) * mm});
            skLineSegment(sketch, "E1987", {"start": v(3.96, 20.26) * mm, "end": v(3.94, 20.2) * mm});
            skLineSegment(sketch, "E1988", {"start": v(3.94, 20.2) * mm, "end": v(3.92, 20.15) * mm});
            skLineSegment(sketch, "E1989", {"start": v(3.92, 20.15) * mm, "end": v(3.9, 20.1) * mm});
            skLineSegment(sketch, "E1990", {"start": v(3.9, 20.1) * mm, "end": v(3.87, 20.04) * mm});
            skLineSegment(sketch, "E1991", {"start": v(3.87, 20.04) * mm, "end": v(3.85, 19.98) * mm});
            skLineSegment(sketch, "E1992", {"start": v(3.85, 19.98) * mm, "end": v(3.83, 19.93) * mm});
            skLineSegment(sketch, "E1993", {"start": v(3.83, 19.93) * mm, "end": v(3.8, 19.88) * mm});
            skLineSegment(sketch, "E1994", {"start": v(3.8, 19.88) * mm, "end": v(3.79, 19.82) * mm});
            skLineSegment(sketch, "E1995", {"start": v(3.79, 19.82) * mm, "end": v(3.76, 19.77) * mm});
            skLineSegment(sketch, "E1996", {"start": v(3.76, 19.77) * mm, "end": v(3.74, 19.72) * mm});
            skLineSegment(sketch, "E1997", {"start": v(3.74, 19.72) * mm, "end": v(3.72, 19.67) * mm});
            skLineSegment(sketch, "E1998", {"start": v(3.72, 19.67) * mm, "end": v(3.7, 19.61) * mm});
            skLineSegment(sketch, "E1999", {"start": v(3.7, 19.61) * mm, "end": v(3.68, 19.56) * mm});
            skLineSegment(sketch, "E2000", {"start": v(3.68, 19.56) * mm, "end": v(3.66, 19.51) * mm});
            skLineSegment(sketch, "E2001", {"start": v(3.66, 19.51) * mm, "end": v(3.64, 19.46) * mm});
            skLineSegment(sketch, "E2002", {"start": v(3.64, 19.46) * mm, "end": v(3.61, 19.4) * mm});
            skLineSegment(sketch, "E2003", {"start": v(3.61, 19.4) * mm, "end": v(3.6, 19.36) * mm});
            skLineSegment(sketch, "E2004", {"start": v(3.6, 19.36) * mm, "end": v(3.57, 19.3) * mm});
            skLineSegment(sketch, "E2005", {"start": v(3.57, 19.3) * mm, "end": v(3.55, 19.26) * mm});
            skLineSegment(sketch, "E2006", {"start": v(3.55, 19.26) * mm, "end": v(3.53, 19.2) * mm});
            skLineSegment(sketch, "E2007", {"start": v(3.53, 19.2) * mm, "end": v(3.51, 19.16) * mm});
            skLineSegment(sketch, "E2008", {"start": v(3.51, 19.16) * mm, "end": v(3.49, 19.11) * mm});
            skLineSegment(sketch, "E2009", {"start": v(3.49, 19.11) * mm, "end": v(3.47, 19.06) * mm});
            skLineSegment(sketch, "E2010", {"start": v(3.47, 19.06) * mm, "end": v(3.45, 19.01) * mm});
            skLineSegment(sketch, "E2011", {"start": v(3.45, 19.01) * mm, "end": v(3.43, 18.97) * mm});
            skLineSegment(sketch, "E2012", {"start": v(3.43, 18.97) * mm, "end": v(3.4, 18.92) * mm});
            skLineSegment(sketch, "E2013", {"start": v(3.4, 18.92) * mm, "end": v(3.39, 18.87) * mm});
            skLineSegment(sketch, "E2014", {"start": v(3.39, 18.87) * mm, "end": v(3.37, 18.83) * mm});
            skLineSegment(sketch, "E2015", {"start": v(3.37, 18.83) * mm, "end": v(3.35, 18.78) * mm});
            skLineSegment(sketch, "E2016", {"start": v(3.35, 18.78) * mm, "end": v(3.33, 18.73) * mm});
            skLineSegment(sketch, "E2017", {"start": v(3.33, 18.73) * mm, "end": v(3.3, 18.69) * mm});
            skLineSegment(sketch, "E2018", {"start": v(3.3, 18.69) * mm, "end": v(3.29, 18.64) * mm});
            skLineSegment(sketch, "E2019", {"start": v(3.29, 18.64) * mm, "end": v(3.27, 18.6) * mm});
            skLineSegment(sketch, "E2020", {"start": v(3.27, 18.6) * mm, "end": v(3.25, 18.55) * mm});
            skLineSegment(sketch, "E2021", {"start": v(3.25, 18.55) * mm, "end": v(3.23, 18.5) * mm});
            skLineSegment(sketch, "E2022", {"start": v(3.23, 18.5) * mm, "end": v(3.21, 18.47) * mm});
            skLineSegment(sketch, "E2023", {"start": v(3.21, 18.47) * mm, "end": v(3.2, 18.42) * mm});
            skLineSegment(sketch, "E2024", {"start": v(3.2, 18.42) * mm, "end": v(3.18, 18.38) * mm});
            skLineSegment(sketch, "E2025", {"start": v(3.18, 18.38) * mm, "end": v(3.16, 18.34) * mm});
            skLineSegment(sketch, "E2026", {"start": v(3.16, 18.34) * mm, "end": v(3.14, 18.3) * mm});
            skLineSegment(sketch, "E2027", {"start": v(3.14, 18.3) * mm, "end": v(3.12, 18.25) * mm});
            skLineSegment(sketch, "E2028", {"start": v(3.12, 18.25) * mm, "end": v(3.1, 18.21) * mm});
            skLineSegment(sketch, "E2029", {"start": v(3.1, 18.21) * mm, "end": v(3.09, 18.17) * mm});
            skLineSegment(sketch, "E2030", {"start": v(3.09, 18.17) * mm, "end": v(3.07, 18.13) * mm});
            skLineSegment(sketch, "E2031", {"start": v(3.07, 18.13) * mm, "end": v(3.05, 18.1) * mm});
            skLineSegment(sketch, "E2032", {"start": v(3.05, 18.1) * mm, "end": v(3.03, 18.05) * mm});
            skLineSegment(sketch, "E2033", {"start": v(3.03, 18.05) * mm, "end": v(3.02, 18.02) * mm});
            skLineSegment(sketch, "E2034", {"start": v(3.02, 18.02) * mm, "end": v(3, 17.98) * mm});
            skLineSegment(sketch, "E2035", {"start": v(3, 17.98) * mm, "end": v(2.98, 17.94) * mm});
            skLineSegment(sketch, "E2036", {"start": v(2.98, 17.94) * mm, "end": v(2.97, 17.9) * mm});
            skLineSegment(sketch, "E2037", {"start": v(2.97, 17.9) * mm, "end": v(2.95, 17.86) * mm});
            skLineSegment(sketch, "E2038", {"start": v(2.95, 17.86) * mm, "end": v(2.93, 17.83) * mm});
            skLineSegment(sketch, "E2039", {"start": v(2.93, 17.83) * mm, "end": v(2.92, 17.8) * mm});
            skLineSegment(sketch, "E2040", {"start": v(2.92, 17.8) * mm, "end": v(2.9, 17.76) * mm});
            skLineSegment(sketch, "E2041", {"start": v(2.9, 17.76) * mm, "end": v(2.88, 17.72) * mm});
            skLineSegment(sketch, "E2042", {"start": v(2.88, 17.72) * mm, "end": v(2.87, 17.69) * mm});
            skLineSegment(sketch, "E2043", {"start": v(2.87, 17.69) * mm, "end": v(2.85, 17.65) * mm});
            skLineSegment(sketch, "E2044", {"start": v(2.85, 17.65) * mm, "end": v(2.84, 17.62) * mm});
            skLineSegment(sketch, "E2045", {"start": v(2.84, 17.62) * mm, "end": v(2.82, 17.59) * mm});
            skLineSegment(sketch, "E2046", {"start": v(2.82, 17.59) * mm, "end": v(2.64, 17.16) * mm});
            skLineSegment(sketch, "E2047", {"start": v(2.64, 17.16) * mm, "end": v(2.45, 16.73) * mm});
            skLineSegment(sketch, "E2048", {"start": v(2.45, 16.73) * mm, "end": v(2.26, 16.3) * mm});
            skLineSegment(sketch, "E2049", {"start": v(2.26, 16.3) * mm, "end": v(2.07, 15.88) * mm});
            skLineSegment(sketch, "E2050", {"start": v(2.07, 15.88) * mm, "end": v(1.88, 15.45) * mm});
            skLineSegment(sketch, "E2051", {"start": v(1.88, 15.45) * mm, "end": v(1.7, 15.02) * mm});
            skLineSegment(sketch, "E2052", {"start": v(1.7, 15.02) * mm, "end": v(1.5, 14.6) * mm});
            skLineSegment(sketch, "E2053", {"start": v(1.5, 14.6) * mm, "end": v(1.31, 14.17) * mm});
            skLineSegment(sketch, "E2054", {"start": v(1.31, 14.17) * mm, "end": v(1.12, 13.74) * mm});
            skLineSegment(sketch, "E2055", {"start": v(1.12, 13.74) * mm, "end": v(0.93, 13.32) * mm});
            skLineSegment(sketch, "E2056", {"start": v(0.93, 13.32) * mm, "end": v(0.75, 12.89) * mm});
            skLineSegment(sketch, "E2057", {"start": v(0.75, 12.89) * mm, "end": v(0.56, 12.46) * mm});
            skLineSegment(sketch, "E2058", {"start": v(0.56, 12.46) * mm, "end": v(0.37, 12.04) * mm});
            skLineSegment(sketch, "E2059", {"start": v(0.37, 12.04) * mm, "end": v(0.18, 11.6) * mm});
            skLineSegment(sketch, "E2060", {"start": v(0.18, 11.6) * mm, "end": v(-0.01, 11.18) * mm});
            skLineSegment(sketch, "E2061", {"start": v(-0.01, 11.18) * mm, "end": v(-0.2, 10.75) * mm});
            skLineSegment(sketch, "E2062", {"start": v(-0.2, 10.75) * mm, "end": v(-0.39, 10.33) * mm});
            skLineSegment(sketch, "E2063", {"start": v(-0.39, 10.33) * mm, "end": v(-0.58, 9.9) * mm});
            skLineSegment(sketch, "E2064", {"start": v(-0.58, 9.9) * mm, "end": v(-0.77, 9.47) * mm});
            skLineSegment(sketch, "E2065", {"start": v(-0.77, 9.47) * mm, "end": v(-0.96, 9.05) * mm});
            skLineSegment(sketch, "E2066", {"start": v(-0.96, 9.05) * mm, "end": v(-1.14, 8.62) * mm});
            skLineSegment(sketch, "E2067", {"start": v(-1.14, 8.62) * mm, "end": v(-1.33, 8.2) * mm});
            skLineSegment(sketch, "E2068", {"start": v(-1.33, 8.2) * mm, "end": v(-1.52, 7.77) * mm});
            skLineSegment(sketch, "E2069", {"start": v(-1.52, 7.77) * mm, "end": v(-1.71, 7.34) * mm});
            skLineSegment(sketch, "E2070", {"start": v(-1.71, 7.34) * mm, "end": v(-1.9, 6.91) * mm});
            skLineSegment(sketch, "E2071", {"start": v(-1.9, 6.91) * mm, "end": v(-2.09, 6.48) * mm});
            skLineSegment(sketch, "E2072", {"start": v(-2.09, 6.48) * mm, "end": v(-2.28, 6.06) * mm});
            skLineSegment(sketch, "E2073", {"start": v(-2.28, 6.06) * mm, "end": v(-2.47, 5.63) * mm});
            skLineSegment(sketch, "E2074", {"start": v(-2.47, 5.63) * mm, "end": v(-2.66, 5.2) * mm});
            skLineSegment(sketch, "E2075", {"start": v(-2.66, 5.2) * mm, "end": v(-2.85, 4.78) * mm});
            skLineSegment(sketch, "E2076", {"start": v(-2.85, 4.78) * mm, "end": v(-3.03, 4.35) * mm});
            skLineSegment(sketch, "E2077", {"start": v(-3.03, 4.35) * mm, "end": v(-3.22, 3.92) * mm});
            skLineSegment(sketch, "E2078", {"start": v(-3.22, 3.92) * mm, "end": v(-3.41, 3.5) * mm});
            skLineSegment(sketch, "E2079", {"start": v(-3.41, 3.5) * mm, "end": v(-3.6, 3.07) * mm});
            skLineSegment(sketch, "E2080", {"start": v(-3.6, 3.07) * mm, "end": v(-3.8, 2.64) * mm});
            skLineSegment(sketch, "E2081", {"start": v(-3.8, 2.64) * mm, "end": v(-3.98, 2.21) * mm});
            skLineSegment(sketch, "E2082", {"start": v(-3.98, 2.21) * mm, "end": v(-4.17, 1.79) * mm});
            skLineSegment(sketch, "E2083", {"start": v(-4.17, 1.79) * mm, "end": v(-4.36, 1.36) * mm});
            skLineSegment(sketch, "E2084", {"start": v(-4.36, 1.36) * mm, "end": v(-4.55, 0.93) * mm});
            skLineSegment(sketch, "E2085", {"start": v(-4.55, 0.93) * mm, "end": v(-4.74, 0.5) * mm});
            skLineSegment(sketch, "E2086", {"start": v(-4.74, 0.5) * mm, "end": v(-4.92, 0.08) * mm});
            skLineSegment(sketch, "E2087", {"start": v(-4.92, 0.08) * mm, "end": v(-5.11, -0.35) * mm});
            skLineSegment(sketch, "E2088", {"start": v(-5.11, -0.35) * mm, "end": v(-5.3, -0.77) * mm});
            skLineSegment(sketch, "E2089", {"start": v(-5.3, -0.77) * mm, "end": v(-5.5, -1.2) * mm});
            skLineSegment(sketch, "E2090", {"start": v(-5.5, -1.2) * mm, "end": v(-5.68, -1.63) * mm});
            skLineSegment(sketch, "E2091", {"start": v(-5.68, -1.63) * mm, "end": v(-5.87, -2.06) * mm});
            skLineSegment(sketch, "E2092", {"start": v(-5.87, -2.06) * mm, "end": v(-6.06, -2.48) * mm});
            skLineSegment(sketch, "E2093", {"start": v(-6.06, -2.48) * mm, "end": v(-6.25, -2.9) * mm});
            skLineSegment(sketch, "E2094", {"start": v(-6.25, -2.9) * mm, "end": v(-6.44, -3.34) * mm});
            skLineSegment(sketch, "E2095", {"start": v(-6.44, -3.34) * mm, "end": v(-6.63, -3.76) * mm});
            skLineSegment(sketch, "E2096", {"start": v(-6.63, -3.76) * mm, "end": v(-6.81, -4.2) * mm});
            skLineSegment(sketch, "E2097", {"start": v(-6.81, -4.2) * mm, "end": v(-7, -4.62) * mm});
            skLineSegment(sketch, "E2098", {"start": v(-7, -4.62) * mm, "end": v(-7.2, -5.04) * mm});
            skLineSegment(sketch, "E2099", {"start": v(-7.2, -5.04) * mm, "end": v(-7.38, -5.47) * mm});
            skLineSegment(sketch, "E2100", {"start": v(-7.38, -5.47) * mm, "end": v(-7.57, -5.9) * mm});
            skLineSegment(sketch, "E2101", {"start": v(-7.57, -5.9) * mm, "end": v(-7.76, -6.33) * mm});
            skLineSegment(sketch, "E2102", {"start": v(-7.76, -6.33) * mm, "end": v(-7.95, -6.75) * mm});
            skLineSegment(sketch, "E2103", {"start": v(-7.95, -6.75) * mm, "end": v(-8.14, -7.18) * mm});
            skLineSegment(sketch, "E2104", {"start": v(-8.14, -7.18) * mm, "end": v(-8.33, -7.6) * mm});
            skLineSegment(sketch, "E2105", {"start": v(-8.33, -7.6) * mm, "end": v(-8.52, -8.03) * mm});
            skLineSegment(sketch, "E2106", {"start": v(-8.52, -8.03) * mm, "end": v(-8.7, -8.46) * mm});
            skLineSegment(sketch, "E2107", {"start": v(-8.7, -8.46) * mm, "end": v(-8.9, -8.89) * mm});
            skLineSegment(sketch, "E2108", {"start": v(-8.9, -8.89) * mm, "end": v(-9.08, -9.31) * mm});
            skLineSegment(sketch, "E2109", {"start": v(-9.08, -9.31) * mm, "end": v(-9.27, -9.74) * mm});
            skLineSegment(sketch, "E2110", {"start": v(-9.27, -9.74) * mm, "end": v(-9.46, -10.17) * mm});
            skLineSegment(sketch, "E2111", {"start": v(-9.46, -10.17) * mm, "end": v(-9.65, -10.6) * mm});
            skLineSegment(sketch, "E2112", {"start": v(-9.65, -10.6) * mm, "end": v(-9.84, -11.02) * mm});
            skLineSegment(sketch, "E2113", {"start": v(-9.84, -11.02) * mm, "end": v(-10.03, -11.45) * mm});
            skLineSegment(sketch, "E2114", {"start": v(-10.03, -11.45) * mm, "end": v(-10.22, -11.88) * mm});
            skLineSegment(sketch, "E2115", {"start": v(-10.22, -11.88) * mm, "end": v(-10.4, -12.3) * mm});
            skLineSegment(sketch, "E2116", {"start": v(-10.4, -12.3) * mm, "end": v(-10.6, -12.73) * mm});
            skLineSegment(sketch, "E2117", {"start": v(-10.6, -12.73) * mm, "end": v(-10.78, -13.16) * mm});
            skLineSegment(sketch, "E2118", {"start": v(-10.78, -13.16) * mm, "end": v(-10.97, -13.58) * mm});
            skLineSegment(sketch, "E2119", {"start": v(-10.97, -13.58) * mm, "end": v(-11.16, -14.01) * mm});
            skLineSegment(sketch, "E2120", {"start": v(-11.16, -14.01) * mm, "end": v(-11.35, -14.44) * mm});
            skLineSegment(sketch, "E2121", {"start": v(-11.35, -14.44) * mm, "end": v(-11.54, -14.86) * mm});
            skLineSegment(sketch, "E2122", {"start": v(-11.54, -14.86) * mm, "end": v(-11.73, -15.3) * mm});
            skLineSegment(sketch, "E2123", {"start": v(-11.73, -15.3) * mm, "end": v(-11.92, -15.72) * mm});
            skLineSegment(sketch, "E2124", {"start": v(-11.92, -15.72) * mm, "end": v(-12.1, -16.15) * mm});
            skLineSegment(sketch, "E2125", {"start": v(-12.1, -16.15) * mm, "end": v(-12.3, -16.57) * mm});
            skLineSegment(sketch, "E2126", {"start": v(-12.3, -16.57) * mm, "end": v(-12.48, -17) * mm});
            skLineSegment(sketch, "E2127", {"start": v(-12.48, -17) * mm, "end": v(-12.67, -17.43) * mm});
            skLineSegment(sketch, "E2128", {"start": v(-12.67, -17.43) * mm, "end": v(-12.86, -17.85) * mm});
            skLineSegment(sketch, "E2129", {"start": v(-12.86, -17.85) * mm, "end": v(-13.05, -18.28) * mm});
            skLineSegment(sketch, "E2130", {"start": v(-13.05, -18.28) * mm, "end": v(-13.24, -18.7) * mm});
            skLineSegment(sketch, "E2131", {"start": v(-13.24, -18.7) * mm, "end": v(-13.43, -19.13) * mm});
            skLineSegment(sketch, "E2132", {"start": v(-13.43, -19.13) * mm, "end": v(-13.62, -19.56) * mm});
            skLineSegment(sketch, "E2133", {"start": v(-13.62, -19.56) * mm, "end": v(-13.8, -19.99) * mm});
            skLineSegment(sketch, "E2134", {"start": v(-13.8, -19.99) * mm, "end": v(-14, -20.42) * mm});
            skLineSegment(sketch, "E2135", {"start": v(-14, -20.42) * mm, "end": v(-14.18, -20.84) * mm});
            skLineSegment(sketch, "E2136", {"start": v(-14.18, -20.84) * mm, "end": v(-14.37, -21.27) * mm});
            skLineSegment(sketch, "E2137", {"start": v(-14.37, -21.27) * mm, "end": v(-14.56, -21.7) * mm});
            skLineSegment(sketch, "E2138", {"start": v(-14.56, -21.7) * mm, "end": v(-14.75, -22.12) * mm});
            skLineSegment(sketch, "E2139", {"start": v(-14.75, -22.12) * mm, "end": v(-14.94, -22.55) * mm});
            skLineSegment(sketch, "E2140", {"start": v(-14.94, -22.55) * mm, "end": v(-15.13, -22.98) * mm});
            skLineSegment(sketch, "E2141", {"start": v(-15.13, -22.98) * mm, "end": v(-15.32, -23.4) * mm});
            skLineSegment(sketch, "E2142", {"start": v(-15.32, -23.4) * mm, "end": v(-15.5, -23.83) * mm});
            skLineSegment(sketch, "E2143", {"start": v(-15.5, -23.83) * mm, "end": v(-15.7, -24.26) * mm});
            skLineSegment(sketch, "E2144", {"start": v(-15.7, -24.26) * mm, "end": v(-15.89, -24.69) * mm});
            skLineSegment(sketch, "E2145", {"start": v(-15.89, -24.69) * mm, "end": v(-16.07, -25.11) * mm});
            skLineSegment(sketch, "E2146", {"start": v(-16.07, -25.11) * mm, "end": v(-16.26, -25.54) * mm});
            skLineSegment(sketch, "E2147", {"start": v(-16.26, -25.54) * mm, "end": v(-16.45, -25.97) * mm});
            skLineSegment(sketch, "E2148", {"start": v(-16.45, -25.97) * mm, "end": v(-16.64, -26.4) * mm});
            skLineSegment(sketch, "E2149", {"start": v(-16.64, -26.4) * mm, "end": v(-16.83, -26.82) * mm});
            skLineSegment(sketch, "E2150", {"start": v(-16.83, -26.82) * mm, "end": v(-17.02, -27.25) * mm});
            skLineSegment(sketch, "E2151", {"start": v(-17.02, -27.25) * mm, "end": v(-17.2, -27.67) * mm});
            skLineSegment(sketch, "E2152", {"start": v(-17.2, -27.67) * mm, "end": v(-17.4, -28.1) * mm});
            skLineSegment(sketch, "E2153", {"start": v(-17.4, -28.1) * mm, "end": v(-17.59, -28.53) * mm});
            skLineSegment(sketch, "E2154", {"start": v(-17.59, -28.53) * mm, "end": v(-17.78, -28.96) * mm});
            skLineSegment(sketch, "E2155", {"start": v(-17.78, -28.96) * mm, "end": v(-17.96, -29.38) * mm});
            skLineSegment(sketch, "E2156", {"start": v(-17.96, -29.38) * mm, "end": v(-18.15, -29.8) * mm});
            skLineSegment(sketch, "E2157", {"start": v(-18.15, -29.8) * mm, "end": v(-18.34, -30.24) * mm});
            skLineSegment(sketch, "E2158", {"start": v(-18.34, -30.24) * mm, "end": v(-18.53, -30.66) * mm});
            skLineSegment(sketch, "E2159", {"start": v(-18.53, -30.66) * mm, "end": v(-18.72, -31.1) * mm});
            skLineSegment(sketch, "E2160", {"start": v(-18.72, -31.1) * mm, "end": v(-18.9, -31.52) * mm});
            skLineSegment(sketch, "E2161", {"start": v(-18.9, -31.52) * mm, "end": v(-19.1, -31.94) * mm});
            skLineSegment(sketch, "E2162", {"start": v(-19.1, -31.94) * mm, "end": v(-19.29, -32.37) * mm});
            skLineSegment(sketch, "E2163", {"start": v(-19.29, -32.37) * mm, "end": v(-19.48, -32.8) * mm});
            skLineSegment(sketch, "E2164", {"start": v(-19.48, -32.8) * mm, "end": v(-19.67, -33.23) * mm});
            skLineSegment(sketch, "E2165", {"start": v(-19.67, -33.23) * mm, "end": v(-19.85, -33.65) * mm});
            skLineSegment(sketch, "E2166", {"start": v(-19.85, -33.65) * mm, "end": v(-20.04, -34.08) * mm});
            skLineSegment(sketch, "E2167", {"start": v(-20.04, -34.08) * mm, "end": v(-20.23, -34.5) * mm});
            skLineSegment(sketch, "E2168", {"start": v(-20.23, -34.5) * mm, "end": v(-20.42, -34.93) * mm});
            skLineSegment(sketch, "E2169", {"start": v(-20.42, -34.93) * mm, "end": v(-20.61, -35.36) * mm});
            skLineSegment(sketch, "E2170", {"start": v(-20.61, -35.36) * mm, "end": v(-20.8, -35.79) * mm});
            skLineSegment(sketch, "E2171", {"start": v(-20.8, -35.79) * mm, "end": v(-20.99, -36.21) * mm});
            skLineSegment(sketch, "E2172", {"start": v(-20.99, -36.21) * mm, "end": v(-21.18, -36.64) * mm});
            skLineSegment(sketch, "E2173", {"start": v(-21.18, -36.64) * mm, "end": v(-21.37, -37.07) * mm});
            skLineSegment(sketch, "E2174", {"start": v(-21.37, -37.07) * mm, "end": v(-21.25, -37.07) * mm});
            skLineSegment(sketch, "E2175", {"start": v(-21.25, -37.07) * mm, "end": v(-21.13, -37.07) * mm});
            skLineSegment(sketch, "E2176", {"start": v(-21.13, -37.07) * mm, "end": v(-21, -37.07) * mm});
            skLineSegment(sketch, "E2177", {"start": v(-21, -37.07) * mm, "end": v(-20.89, -37.07) * mm});
            skLineSegment(sketch, "E2178", {"start": v(-20.89, -37.07) * mm, "end": v(-20.77, -37.07) * mm});
            skLineSegment(sketch, "E2179", {"start": v(-20.77, -37.07) * mm, "end": v(-20.65, -37.07) * mm});
            skLineSegment(sketch, "E2180", {"start": v(-20.65, -37.07) * mm, "end": v(-20.53, -37.07) * mm});
            skLineSegment(sketch, "E2181", {"start": v(-20.53, -37.07) * mm, "end": v(-20.4, -37.07) * mm});
            skLineSegment(sketch, "E2182", {"start": v(-20.4, -37.07) * mm, "end": v(-20.29, -37.07) * mm});
            skLineSegment(sketch, "E2183", {"start": v(-20.29, -37.07) * mm, "end": v(-20.17, -37.07) * mm});
            skLineSegment(sketch, "E2184", {"start": v(-20.17, -37.07) * mm, "end": v(-20.05, -37.07) * mm});
            skLineSegment(sketch, "E2185", {"start": v(-20.05, -37.07) * mm, "end": v(-19.93, -37.07) * mm});
            skLineSegment(sketch, "E2186", {"start": v(-19.93, -37.07) * mm, "end": v(-19.8, -37.07) * mm});
            skLineSegment(sketch, "E2187", {"start": v(-19.8, -37.07) * mm, "end": v(-19.69, -37.07) * mm});
            skLineSegment(sketch, "E2188", {"start": v(-19.69, -37.07) * mm, "end": v(-19.57, -37.07) * mm});
            skLineSegment(sketch, "E2189", {"start": v(-19.57, -37.07) * mm, "end": v(-19.45, -37.07) * mm});
            skLineSegment(sketch, "E2190", {"start": v(-19.45, -37.07) * mm, "end": v(-19.33, -37.07) * mm});
            skLineSegment(sketch, "E2191", {"start": v(-19.33, -37.07) * mm, "end": v(-19.21, -37.07) * mm});
            skLineSegment(sketch, "E2192", {"start": v(-19.21, -37.07) * mm, "end": v(-19.1, -37.07) * mm});
            skLineSegment(sketch, "E2193", {"start": v(-19.1, -37.07) * mm, "end": v(-18.97, -37.07) * mm});
            skLineSegment(sketch, "E2194", {"start": v(-18.97, -37.07) * mm, "end": v(-18.85, -37.07) * mm});
            skLineSegment(sketch, "E2195", {"start": v(-18.85, -37.07) * mm, "end": v(-18.73, -37.07) * mm});
            skLineSegment(sketch, "E2196", {"start": v(-18.73, -37.07) * mm, "end": v(-18.61, -37.07) * mm});
            skLineSegment(sketch, "E2197", {"start": v(-18.61, -37.07) * mm, "end": v(-18.5, -37.07) * mm});
            skLineSegment(sketch, "E2198", {"start": v(-18.5, -37.07) * mm, "end": v(-18.37, -37.07) * mm});
            skLineSegment(sketch, "E2199", {"start": v(-18.37, -37.07) * mm, "end": v(-18.25, -37.07) * mm});
            skLineSegment(sketch, "E2200", {"start": v(-18.25, -37.07) * mm, "end": v(-18.13, -37.07) * mm});
            skLineSegment(sketch, "E2201", {"start": v(-18.13, -37.07) * mm, "end": v(-18.01, -37.07) * mm});
            skLineSegment(sketch, "E2202", {"start": v(-18.01, -37.07) * mm, "end": v(-17.9, -37.07) * mm});
            skLineSegment(sketch, "E2203", {"start": v(-17.9, -37.07) * mm, "end": v(-17.77, -37.07) * mm});
            skLineSegment(sketch, "E2204", {"start": v(-17.77, -37.07) * mm, "end": v(-17.65, -37.07) * mm});
            skLineSegment(sketch, "E2205", {"start": v(-17.65, -37.07) * mm, "end": v(-17.53, -37.07) * mm});
            skLineSegment(sketch, "E2206", {"start": v(-17.53, -37.07) * mm, "end": v(-17.41, -37.07) * mm});
            skLineSegment(sketch, "E2207", {"start": v(-17.41, -37.07) * mm, "end": v(-17.3, -37.07) * mm});
            skLineSegment(sketch, "E2208", {"start": v(-17.3, -37.07) * mm, "end": v(-17.17, -37.07) * mm});
            skLineSegment(sketch, "E2209", {"start": v(-17.17, -37.07) * mm, "end": v(-17.05, -37.07) * mm});
            skLineSegment(sketch, "E2210", {"start": v(-17.05, -37.07) * mm, "end": v(-16.93, -37.07) * mm});
            skLineSegment(sketch, "E2211", {"start": v(-16.93, -37.07) * mm, "end": v(-16.81, -37.07) * mm});
            skLineSegment(sketch, "E2212", {"start": v(-16.81, -37.07) * mm, "end": v(-16.7, -37.07) * mm});
            skLineSegment(sketch, "E2213", {"start": v(-16.7, -37.07) * mm, "end": v(-16.57, -37.07) * mm});
            skLineSegment(sketch, "E2214", {"start": v(-16.57, -37.07) * mm, "end": v(-16.45, -37.07) * mm});
            skLineSegment(sketch, "E2215", {"start": v(-16.45, -37.07) * mm, "end": v(-16.34, -37.07) * mm});
            skLineSegment(sketch, "E2216", {"start": v(-16.34, -37.07) * mm, "end": v(-16.22, -37.07) * mm});
            skLineSegment(sketch, "E2217", {"start": v(-16.22, -37.07) * mm, "end": v(-16.1, -37.07) * mm});
            skLineSegment(sketch, "E2218", {"start": v(-16.1, -37.07) * mm, "end": v(-15.98, -37.07) * mm});
            skLineSegment(sketch, "E2219", {"start": v(-15.98, -37.07) * mm, "end": v(-15.86, -37.07) * mm});
            skLineSegment(sketch, "E2220", {"start": v(-15.86, -37.07) * mm, "end": v(-15.74, -37.07) * mm});
            skLineSegment(sketch, "E2221", {"start": v(-15.74, -37.07) * mm, "end": v(-15.62, -37.07) * mm});
            skLineSegment(sketch, "E2222", {"start": v(-15.62, -37.07) * mm, "end": v(-15.5, -37.07) * mm});
            skLineSegment(sketch, "E2223", {"start": v(-15.5, -37.07) * mm, "end": v(-15.38, -37.07) * mm});
            skLineSegment(sketch, "E2224", {"start": v(-15.38, -37.07) * mm, "end": v(-15.26, -37.07) * mm});
            skLineSegment(sketch, "E2225", {"start": v(-15.26, -37.07) * mm, "end": v(-15.14, -37.07) * mm});
            skLineSegment(sketch, "E2226", {"start": v(-15.14, -37.07) * mm, "end": v(-15.02, -37.07) * mm});
            skLineSegment(sketch, "E2227", {"start": v(-15.02, -37.07) * mm, "end": v(-14.9, -37.07) * mm});
            skLineSegment(sketch, "E2228", {"start": v(-14.9, -37.07) * mm, "end": v(-14.78, -37.07) * mm});
            skLineSegment(sketch, "E2229", {"start": v(-14.78, -37.07) * mm, "end": v(-14.66, -37.07) * mm});
            skLineSegment(sketch, "E2230", {"start": v(-14.66, -37.07) * mm, "end": v(-14.54, -37.07) * mm});
            skLineSegment(sketch, "E2231", {"start": v(-14.54, -37.07) * mm, "end": v(-14.42, -37.07) * mm});
            skLineSegment(sketch, "E2232", {"start": v(-14.42, -37.07) * mm, "end": v(-14.3, -37.07) * mm});
            skLineSegment(sketch, "E2233", {"start": v(-14.3, -37.07) * mm, "end": v(-14.18, -37.07) * mm});
            skLineSegment(sketch, "E2234", {"start": v(-14.18, -37.07) * mm, "end": v(-14.06, -37.07) * mm});
            skLineSegment(sketch, "E2235", {"start": v(-14.06, -37.07) * mm, "end": v(-13.94, -37.07) * mm});
            skLineSegment(sketch, "E2236", {"start": v(-13.94, -37.07) * mm, "end": v(-13.82, -37.07) * mm});
            skLineSegment(sketch, "E2237", {"start": v(-13.82, -37.07) * mm, "end": v(-13.7, -37.07) * mm});
            skLineSegment(sketch, "E2238", {"start": v(-13.7, -37.07) * mm, "end": v(-13.58, -37.07) * mm});
            skLineSegment(sketch, "E2239", {"start": v(-13.58, -37.07) * mm, "end": v(-13.46, -37.07) * mm});
            skLineSegment(sketch, "E2240", {"start": v(-13.46, -37.07) * mm, "end": v(-13.34, -37.07) * mm});
            skLineSegment(sketch, "E2241", {"start": v(-13.34, -37.07) * mm, "end": v(-13.22, -37.07) * mm});
            skLineSegment(sketch, "E2242", {"start": v(-13.22, -37.07) * mm, "end": v(-13.1, -37.07) * mm});
            skLineSegment(sketch, "E2243", {"start": v(-13.1, -37.07) * mm, "end": v(-12.98, -37.07) * mm});
            skLineSegment(sketch, "E2244", {"start": v(-12.98, -37.07) * mm, "end": v(-12.86, -37.07) * mm});
            skLineSegment(sketch, "E2245", {"start": v(-12.86, -37.07) * mm, "end": v(-12.74, -37.07) * mm});
            skLineSegment(sketch, "E2246", {"start": v(-12.74, -37.07) * mm, "end": v(-12.62, -37.07) * mm});
            skLineSegment(sketch, "E2247", {"start": v(-12.62, -37.07) * mm, "end": v(-12.5, -37.07) * mm});
            skLineSegment(sketch, "E2248", {"start": v(-12.5, -37.07) * mm, "end": v(-12.38, -37.07) * mm});
            skLineSegment(sketch, "E2249", {"start": v(-12.38, -37.07) * mm, "end": v(-12.26, -37.07) * mm});
            skLineSegment(sketch, "E2250", {"start": v(-12.26, -37.07) * mm, "end": v(-12.14, -37.07) * mm});
            skLineSegment(sketch, "E2251", {"start": v(-12.14, -37.07) * mm, "end": v(-12.02, -37.07) * mm});
            skLineSegment(sketch, "E2252", {"start": v(-12.02, -37.07) * mm, "end": v(-11.9, -37.07) * mm});
            skLineSegment(sketch, "E2253", {"start": v(-11.9, -37.07) * mm, "end": v(-11.78, -37.07) * mm});
            skLineSegment(sketch, "E2254", {"start": v(-11.78, -37.07) * mm, "end": v(-11.66, -37.07) * mm});
            skLineSegment(sketch, "E2255", {"start": v(-11.66, -37.07) * mm, "end": v(-11.54, -37.07) * mm});
            skLineSegment(sketch, "E2256", {"start": v(-11.54, -37.07) * mm, "end": v(-11.42, -37.07) * mm});
            skLineSegment(sketch, "E2257", {"start": v(-11.42, -37.07) * mm, "end": v(-11.3, -37.07) * mm});
            skLineSegment(sketch, "E2258", {"start": v(-11.3, -37.07) * mm, "end": v(-11.18, -37.07) * mm});
            skLineSegment(sketch, "E2259", {"start": v(-11.18, -37.07) * mm, "end": v(-11.06, -37.07) * mm});
            skLineSegment(sketch, "E2260", {"start": v(-11.06, -37.07) * mm, "end": v(-10.94, -37.07) * mm});
            skLineSegment(sketch, "E2261", {"start": v(-10.94, -37.07) * mm, "end": v(-10.82, -37.07) * mm});
            skLineSegment(sketch, "E2262", {"start": v(-10.82, -37.07) * mm, "end": v(-10.7, -37.07) * mm});
            skLineSegment(sketch, "E2263", {"start": v(-10.7, -37.07) * mm, "end": v(-10.58, -37.07) * mm});
            skLineSegment(sketch, "E2264", {"start": v(-10.58, -37.07) * mm, "end": v(-10.47, -37.07) * mm});
            skLineSegment(sketch, "E2265", {"start": v(-10.47, -37.07) * mm, "end": v(-10.35, -37.07) * mm});
            skLineSegment(sketch, "E2266", {"start": v(-10.35, -37.07) * mm, "end": v(-10.23, -37.07) * mm});
            skLineSegment(sketch, "E2267", {"start": v(-10.23, -37.07) * mm, "end": v(-10.1, -37.07) * mm});
            skLineSegment(sketch, "E2268", {"start": v(-10.1, -37.07) * mm, "end": v(-9.99, -37.07) * mm});
            skLineSegment(sketch, "E2269", {"start": v(-9.99, -37.07) * mm, "end": v(-9.87, -37.07) * mm});
            skLineSegment(sketch, "E2270", {"start": v(-9.87, -37.07) * mm, "end": v(-9.75, -37.07) * mm});
            skLineSegment(sketch, "E2271", {"start": v(-9.75, -37.07) * mm, "end": v(-9.63, -37.07) * mm});
            skLineSegment(sketch, "E2272", {"start": v(-9.63, -37.07) * mm, "end": v(-9.5, -37.07) * mm});
            skLineSegment(sketch, "E2273", {"start": v(-9.5, -37.07) * mm, "end": v(-9.39, -37.07) * mm});
            skLineSegment(sketch, "E2274", {"start": v(-9.39, -37.07) * mm, "end": v(-9.27, -37.07) * mm});
            skLineSegment(sketch, "E2275", {"start": v(-9.27, -37.07) * mm, "end": v(-9.15, -37.07) * mm});
            skLineSegment(sketch, "E2276", {"start": v(-9.15, -37.07) * mm, "end": v(-9.03, -37.07) * mm});
            skLineSegment(sketch, "E2277", {"start": v(-9.03, -37.07) * mm, "end": v(-8.9, -37.07) * mm});
            skLineSegment(sketch, "E2278", {"start": v(-8.9, -37.07) * mm, "end": v(-8.79, -37.07) * mm});
            skLineSegment(sketch, "E2279", {"start": v(-8.79, -37.07) * mm, "end": v(-8.67, -37.07) * mm});
            skLineSegment(sketch, "E2280", {"start": v(-8.67, -37.07) * mm, "end": v(-8.55, -37.07) * mm});
            skLineSegment(sketch, "E2281", {"start": v(-8.55, -37.07) * mm, "end": v(-8.43, -37.07) * mm});
            skLineSegment(sketch, "E2282", {"start": v(-8.43, -37.07) * mm, "end": v(-8.3, -37.07) * mm});
            skLineSegment(sketch, "E2283", {"start": v(-8.3, -37.07) * mm, "end": v(-8.19, -37.07) * mm});
            skLineSegment(sketch, "E2284", {"start": v(-8.19, -37.07) * mm, "end": v(-8.07, -37.07) * mm});
            skLineSegment(sketch, "E2285", {"start": v(-8.07, -37.07) * mm, "end": v(-7.95, -37.07) * mm});
            skLineSegment(sketch, "E2286", {"start": v(-7.95, -37.07) * mm, "end": v(-7.83, -37.07) * mm});
            skLineSegment(sketch, "E2287", {"start": v(-7.83, -37.07) * mm, "end": v(-7.7, -37.07) * mm});
            skLineSegment(sketch, "E2288", {"start": v(-7.7, -37.07) * mm, "end": v(-7.59, -37.07) * mm});
            skLineSegment(sketch, "E2289", {"start": v(-7.59, -37.07) * mm, "end": v(-7.47, -37.07) * mm});
            skLineSegment(sketch, "E2290", {"start": v(-7.47, -37.07) * mm, "end": v(-7.35, -37.07) * mm});
            skLineSegment(sketch, "E2291", {"start": v(-7.35, -37.07) * mm, "end": v(-7.23, -37.07) * mm});
            skLineSegment(sketch, "E2292", {"start": v(-7.23, -37.07) * mm, "end": v(-7.11, -37.07) * mm});
            skLineSegment(sketch, "E2293", {"start": v(-7.11, -37.07) * mm, "end": v(-7, -37.07) * mm});
            skLineSegment(sketch, "E2294", {"start": v(-7, -37.07) * mm, "end": v(-6.87, -37.07) * mm});
            skLineSegment(sketch, "E2295", {"start": v(-6.87, -37.07) * mm, "end": v(-6.75, -37.07) * mm});
            skLineSegment(sketch, "E2296", {"start": v(-6.75, -37.07) * mm, "end": v(-6.63, -37.07) * mm});
            skLineSegment(sketch, "E2297", {"start": v(-6.63, -37.07) * mm, "end": v(-6.51, -37.07) * mm});
            skLineSegment(sketch, "E2298", {"start": v(-6.51, -37.07) * mm, "end": v(-6.4, -37.07) * mm});
            skLineSegment(sketch, "E2299", {"start": v(-6.4, -37.07) * mm, "end": v(-6.27, -37.07) * mm});
            skLineSegment(sketch, "E2300", {"start": v(-6.27, -37.07) * mm, "end": v(-6.15, -37.07) * mm});
            skLineSegment(sketch, "E2301", {"start": v(-6.15, -37.07) * mm, "end": v(-6.03, -37.07) * mm});
            skLineSegment(sketch, "E2302", {"start": v(-6.03, -37.07) * mm, "end": v(-5.84, -36.63) * mm});
            skLineSegment(sketch, "E2303", {"start": v(-5.84, -36.63) * mm, "end": v(-5.64, -36.18) * mm});
            skLineSegment(sketch, "E2304", {"start": v(-5.64, -36.18) * mm, "end": v(-5.44, -35.74) * mm});
            skLineSegment(sketch, "E2305", {"start": v(-5.44, -35.74) * mm, "end": v(-5.25, -35.3) * mm});
            skLineSegment(sketch, "E2306", {"start": v(-5.25, -35.3) * mm, "end": v(-5.05, -34.86) * mm});
            skLineSegment(sketch, "E2307", {"start": v(-5.05, -34.86) * mm, "end": v(-4.85, -34.41) * mm});
            skLineSegment(sketch, "E2308", {"start": v(-4.85, -34.41) * mm, "end": v(-4.66, -33.97) * mm});
            skLineSegment(sketch, "E2309", {"start": v(-4.66, -33.97) * mm, "end": v(-4.46, -33.53) * mm});
            skLineSegment(sketch, "E2310", {"start": v(-4.46, -33.53) * mm, "end": v(-4.26, -33.08) * mm});
            skLineSegment(sketch, "E2311", {"start": v(-4.26, -33.08) * mm, "end": v(-4.07, -32.64) * mm});
            skLineSegment(sketch, "E2312", {"start": v(-4.07, -32.64) * mm, "end": v(-3.87, -32.2) * mm});
            skLineSegment(sketch, "E2313", {"start": v(-3.87, -32.2) * mm, "end": v(-3.67, -31.76) * mm});
            skLineSegment(sketch, "E2314", {"start": v(-3.67, -31.76) * mm, "end": v(-3.48, -31.31) * mm});
            skLineSegment(sketch, "E2315", {"start": v(-3.48, -31.31) * mm, "end": v(-3.28, -30.87) * mm});
            skLineSegment(sketch, "E2316", {"start": v(-3.28, -30.87) * mm, "end": v(-3.08, -30.43) * mm});
            skLineSegment(sketch, "E2317", {"start": v(-3.08, -30.43) * mm, "end": v(-2.89, -29.98) * mm});
            skLineSegment(sketch, "E2318", {"start": v(-2.89, -29.98) * mm, "end": v(-2.69, -29.54) * mm});
            skLineSegment(sketch, "E2319", {"start": v(-2.69, -29.54) * mm, "end": v(-2.5, -29.1) * mm});
            skLineSegment(sketch, "E2320", {"start": v(-2.5, -29.1) * mm, "end": v(-2.3, -28.66) * mm});
            skLineSegment(sketch, "E2321", {"start": v(-2.3, -28.66) * mm, "end": v(-2.1, -28.21) * mm});
            skLineSegment(sketch, "E2322", {"start": v(-2.1, -28.21) * mm, "end": v(-1.9, -27.77) * mm});
            skLineSegment(sketch, "E2323", {"start": v(-1.9, -27.77) * mm, "end": v(-1.7, -27.33) * mm});
            skLineSegment(sketch, "E2324", {"start": v(-1.7, -27.33) * mm, "end": v(-1.5, -26.89) * mm});
            skLineSegment(sketch, "E2325", {"start": v(-1.5, -26.89) * mm, "end": v(-1.31, -26.44) * mm});
            skLineSegment(sketch, "E2326", {"start": v(-1.31, -26.44) * mm, "end": v(-1.12, -26) * mm});
            skLineSegment(sketch, "E2327", {"start": v(-1.12, -26) * mm, "end": v(-0.92, -25.56) * mm});
            skLineSegment(sketch, "E2328", {"start": v(-0.92, -25.56) * mm, "end": v(-0.72, -25.11) * mm});
            skLineSegment(sketch, "E2329", {"start": v(-0.72, -25.11) * mm, "end": v(-0.53, -24.67) * mm});
            skLineSegment(sketch, "E2330", {"start": v(-0.53, -24.67) * mm, "end": v(-0.33, -24.23) * mm});
            skLineSegment(sketch, "E2331", {"start": v(-0.33, -24.23) * mm, "end": v(-0.13, -23.79) * mm});
            skLineSegment(sketch, "E2332", {"start": v(-0.13, -23.79) * mm, "end": v(0.06, -23.34) * mm});
            skLineSegment(sketch, "E2333", {"start": v(0.06, -23.34) * mm, "end": v(0.26, -22.9) * mm});
            skLineSegment(sketch, "E2334", {"start": v(0.26, -22.9) * mm, "end": v(0.46, -22.46) * mm});
            skLineSegment(sketch, "E2335", {"start": v(0.46, -22.46) * mm, "end": v(0.65, -22.01) * mm});
            skLineSegment(sketch, "E2336", {"start": v(0.65, -22.01) * mm, "end": v(0.85, -21.57) * mm});
            skLineSegment(sketch, "E2337", {"start": v(0.85, -21.57) * mm, "end": v(1.05, -21.13) * mm});
            skLineSegment(sketch, "E2338", {"start": v(1.05, -21.13) * mm, "end": v(1.24, -20.69) * mm});
            skLineSegment(sketch, "E2339", {"start": v(1.24, -20.69) * mm, "end": v(1.44, -20.24) * mm});
            skLineSegment(sketch, "E2340", {"start": v(1.44, -20.24) * mm, "end": v(1.64, -19.8) * mm});
            skLineSegment(sketch, "E2341", {"start": v(1.64, -19.8) * mm, "end": v(1.83, -19.36) * mm});
            skLineSegment(sketch, "E2342", {"start": v(1.83, -19.36) * mm, "end": v(2.03, -18.92) * mm});
            skLineSegment(sketch, "E2343", {"start": v(2.03, -18.92) * mm, "end": v(2.23, -18.47) * mm});
            skLineSegment(sketch, "E2344", {"start": v(2.23, -18.47) * mm, "end": v(2.42, -18.03) * mm});
            skLineSegment(sketch, "E2345", {"start": v(2.42, -18.03) * mm, "end": v(2.62, -17.59) * mm});
            skLineSegment(sketch, "E2346", {"start": v(2.62, -17.59) * mm, "end": v(2.82, -17.14) * mm});
            skLineSegment(sketch, "E2347", {"start": v(2.82, -17.14) * mm, "end": v(3.01, -16.7) * mm});
            skLineSegment(sketch, "E2348", {"start": v(3.01, -16.7) * mm, "end": v(3.21, -16.26) * mm});
            skLineSegment(sketch, "E2349", {"start": v(3.21, -16.26) * mm, "end": v(3.4, -15.82) * mm});
            skLineSegment(sketch, "E2350", {"start": v(3.4, -15.82) * mm, "end": v(3.6, -15.37) * mm});
            skLineSegment(sketch, "E2351", {"start": v(3.6, -15.37) * mm, "end": v(3.8, -14.93) * mm});
            skLineSegment(sketch, "E2352", {"start": v(3.8, -14.93) * mm, "end": v(4, -14.49) * mm});
            skLineSegment(sketch, "E2353", {"start": v(4, -14.49) * mm, "end": v(4.2, -14.05) * mm});
            skLineSegment(sketch, "E2354", {"start": v(4.2, -14.05) * mm, "end": v(4.4, -13.6) * mm});
            skLineSegment(sketch, "E2355", {"start": v(4.4, -13.6) * mm, "end": v(4.59, -13.16) * mm});
            skLineSegment(sketch, "E2356", {"start": v(4.59, -13.16) * mm, "end": v(4.78, -12.72) * mm});
            skLineSegment(sketch, "E2357", {"start": v(4.78, -12.72) * mm, "end": v(4.98, -12.27) * mm});
            skLineSegment(sketch, "E2358", {"start": v(4.98, -12.27) * mm, "end": v(5.18, -11.83) * mm});
            skLineSegment(sketch, "E2359", {"start": v(5.18, -11.83) * mm, "end": v(5.37, -11.39) * mm});
            skLineSegment(sketch, "E2360", {"start": v(5.37, -11.39) * mm, "end": v(5.57, -10.95) * mm});
            skLineSegment(sketch, "E2361", {"start": v(5.57, -10.95) * mm, "end": v(5.77, -10.5) * mm});
            skLineSegment(sketch, "E2362", {"start": v(5.77, -10.5) * mm, "end": v(5.96, -10.06) * mm});
            skLineSegment(sketch, "E2363", {"start": v(5.96, -10.06) * mm, "end": v(6.16, -9.62) * mm});
            skLineSegment(sketch, "E2364", {"start": v(6.16, -9.62) * mm, "end": v(6.36, -9.17) * mm});
            skLineSegment(sketch, "E2365", {"start": v(6.36, -9.17) * mm, "end": v(6.55, -8.73) * mm});
            skLineSegment(sketch, "E2366", {"start": v(6.55, -8.73) * mm, "end": v(6.75, -8.29) * mm});
            skLineSegment(sketch, "E2367", {"start": v(6.75, -8.29) * mm, "end": v(6.95, -7.85) * mm});
            skLineSegment(sketch, "E2368", {"start": v(6.95, -7.85) * mm, "end": v(7.14, -7.4) * mm});
            skLineSegment(sketch, "E2369", {"start": v(7.14, -7.4) * mm, "end": v(7.34, -6.96) * mm});
            skLineSegment(sketch, "E2370", {"start": v(7.34, -6.96) * mm, "end": v(7.54, -6.52) * mm});
            skLineSegment(sketch, "E2371", {"start": v(7.54, -6.52) * mm, "end": v(7.73, -6.08) * mm});
            skLineSegment(sketch, "E2372", {"start": v(7.73, -6.08) * mm, "end": v(7.93, -5.63) * mm});
            skLineSegment(sketch, "E2373", {"start": v(7.93, -5.63) * mm, "end": v(8.13, -5.19) * mm});
            skLineSegment(sketch, "E2374", {"start": v(8.13, -5.19) * mm, "end": v(8.32, -4.75) * mm});
            skLineSegment(sketch, "E2375", {"start": v(8.32, -4.75) * mm, "end": v(8.52, -4.3) * mm});
            skLineSegment(sketch, "E2376", {"start": v(8.52, -4.3) * mm, "end": v(8.72, -3.86) * mm});
            skLineSegment(sketch, "E2377", {"start": v(8.72, -3.86) * mm, "end": v(8.91, -3.42) * mm});
            skLineSegment(sketch, "E2378", {"start": v(8.91, -3.42) * mm, "end": v(9.1, -2.98) * mm});
            skLineSegment(sketch, "E2379", {"start": v(9.1, -2.98) * mm, "end": v(9.3, -2.53) * mm});
            skLineSegment(sketch, "E2380", {"start": v(9.3, -2.53) * mm, "end": v(9.5, -2.1) * mm});
            skLineSegment(sketch, "E2381", {"start": v(9.5, -2.1) * mm, "end": v(9.7, -1.65) * mm});
            skLineSegment(sketch, "E2382", {"start": v(9.7, -1.65) * mm, "end": v(9.9, -1.2) * mm});
            skLineSegment(sketch, "E2383", {"start": v(9.9, -1.2) * mm, "end": v(10.1, -0.76) * mm});
            skLineSegment(sketch, "E2384", {"start": v(10.1, -0.76) * mm, "end": v(10.29, -0.32) * mm});
            skLineSegment(sketch, "E2385", {"start": v(10.29, -0.32) * mm, "end": v(10.49, 0.12) * mm});
            skLineSegment(sketch, "E2386", {"start": v(10.49, 0.12) * mm, "end": v(10.68, 0.57) * mm});
            skLineSegment(sketch, "E2387", {"start": v(10.68, 0.57) * mm, "end": v(10.88, 1) * mm});
            skLineSegment(sketch, "E2388", {"start": v(10.88, 1) * mm, "end": v(11.08, 1.45) * mm});
            skLineSegment(sketch, "E2389", {"start": v(11.08, 1.45) * mm, "end": v(11.27, 1.9) * mm});
            skLineSegment(sketch, "E2390", {"start": v(11.27, 1.9) * mm, "end": v(11.47, 2.34) * mm});
            skLineSegment(sketch, "E2391", {"start": v(11.47, 2.34) * mm, "end": v(11.67, 2.78) * mm});
            skLineSegment(sketch, "E2392", {"start": v(11.67, 2.78) * mm, "end": v(11.86, 3.22) * mm});
            skLineSegment(sketch, "E2393", {"start": v(11.86, 3.22) * mm, "end": v(12.06, 3.67) * mm});
            skLineSegment(sketch, "E2394", {"start": v(12.06, 3.67) * mm, "end": v(12.26, 4.1) * mm});
            skLineSegment(sketch, "E2395", {"start": v(12.26, 4.1) * mm, "end": v(12.45, 4.55) * mm});
            skLineSegment(sketch, "E2396", {"start": v(12.45, 4.55) * mm, "end": v(12.65, 5) * mm});
            skLineSegment(sketch, "E2397", {"start": v(12.65, 5) * mm, "end": v(12.85, 5.44) * mm});
            skLineSegment(sketch, "E2398", {"start": v(12.85, 5.44) * mm, "end": v(13.04, 5.88) * mm});
            skLineSegment(sketch, "E2399", {"start": v(13.04, 5.88) * mm, "end": v(13.24, 6.32) * mm});
            skLineSegment(sketch, "E2400", {"start": v(13.24, 6.32) * mm, "end": v(13.44, 6.76) * mm});
            skLineSegment(sketch, "E2401", {"start": v(13.44, 6.76) * mm, "end": v(13.63, 7.2) * mm});
            skLineSegment(sketch, "E2402", {"start": v(13.63, 7.2) * mm, "end": v(13.83, 7.65) * mm});
            skLineSegment(sketch, "E2403", {"start": v(13.83, 7.65) * mm, "end": v(14.03, 8.1) * mm});
            skLineSegment(sketch, "E2404", {"start": v(14.03, 8.1) * mm, "end": v(14.22, 8.54) * mm});
            skLineSegment(sketch, "E2405", {"start": v(14.22, 8.54) * mm, "end": v(14.42, 8.98) * mm});
            skLineSegment(sketch, "E2406", {"start": v(14.42, 8.98) * mm, "end": v(14.62, 9.42) * mm});
            skLineSegment(sketch, "E2407", {"start": v(14.62, 9.42) * mm, "end": v(14.81, 9.86) * mm});
            skLineSegment(sketch, "E2408", {"start": v(14.81, 9.86) * mm, "end": v(15, 10.3) * mm});
            skLineSegment(sketch, "E2409", {"start": v(15, 10.3) * mm, "end": v(15.2, 10.75) * mm});
            skLineSegment(sketch, "E2410", {"start": v(15.2, 10.75) * mm, "end": v(15.4, 11.2) * mm});
            skLineSegment(sketch, "E2411", {"start": v(15.4, 11.2) * mm, "end": v(15.6, 11.64) * mm});
            skLineSegment(sketch, "E2412", {"start": v(15.6, 11.64) * mm, "end": v(15.8, 12.08) * mm});
            skLineSegment(sketch, "E2413", {"start": v(15.8, 12.08) * mm, "end": v(16, 12.52) * mm});
            skLineSegment(sketch, "E2414", {"start": v(16, 12.52) * mm, "end": v(16.19, 12.96) * mm});
            skLineSegment(sketch, "E2415", {"start": v(16.19, 12.96) * mm, "end": v(16.39, 13.4) * mm});
            skLineSegment(sketch, "E2416", {"start": v(16.39, 13.4) * mm, "end": v(16.58, 13.85) * mm});
            skLineSegment(sketch, "E2417", {"start": v(16.58, 13.85) * mm, "end": v(16.78, 14.3) * mm});
            skLineSegment(sketch, "E2418", {"start": v(16.78, 14.3) * mm, "end": v(16.98, 14.73) * mm});
            skLineSegment(sketch, "E2419", {"start": v(16.98, 14.73) * mm, "end": v(17.17, 15.18) * mm});
            skLineSegment(sketch, "E2420", {"start": v(17.17, 15.18) * mm, "end": v(17.37, 15.62) * mm});
            skLineSegment(sketch, "E2421", {"start": v(17.37, 15.62) * mm, "end": v(17.57, 16.06) * mm});
            skLineSegment(sketch, "E2422", {"start": v(17.57, 16.06) * mm, "end": v(17.76, 16.5) * mm});
            skLineSegment(sketch, "E2423", {"start": v(17.76, 16.5) * mm, "end": v(17.96, 16.95) * mm});
            skLineSegment(sketch, "E2424", {"start": v(17.96, 16.95) * mm, "end": v(18.16, 17.4) * mm});
            skLineSegment(sketch, "E2425", {"start": v(18.16, 17.4) * mm, "end": v(18.35, 17.83) * mm});
            skLineSegment(sketch, "E2426", {"start": v(18.35, 17.83) * mm, "end": v(18.55, 18.28) * mm});
            skLineSegment(sketch, "E2427", {"start": v(18.55, 18.28) * mm, "end": v(18.75, 18.72) * mm});
            skLineSegment(sketch, "E2428", {"start": v(18.75, 18.72) * mm, "end": v(18.94, 19.16) * mm});
            skLineSegment(sketch, "E2429", {"start": v(18.94, 19.16) * mm, "end": v(19.14, 19.6) * mm});
            skLineSegment(sketch, "E2430", {"start": v(19.14, 19.6) * mm, "end": v(19.14, 19.61) * mm});
            skLineSegment(sketch, "E2431", {"start": v(19.14, 19.61) * mm, "end": v(19.14, 19.62) * mm});
            skLineSegment(sketch, "E2432", {"start": v(19.14, 19.62) * mm, "end": v(19.15, 19.62) * mm});
            skLineSegment(sketch, "E2433", {"start": v(19.15, 19.62) * mm, "end": v(19.15, 19.63) * mm});
            skLineSegment(sketch, "E2434", {"start": v(19.15, 19.63) * mm, "end": v(19.15, 19.63) * mm});
            skLineSegment(sketch, "E2435", {"start": v(19.15, 19.63) * mm, "end": v(19.16, 19.64) * mm});
            skLineSegment(sketch, "E2436", {"start": v(19.16, 19.64) * mm, "end": v(19.16, 19.65) * mm});
            skLineSegment(sketch, "E2437", {"start": v(19.16, 19.65) * mm, "end": v(19.16, 19.65) * mm});
            skLineSegment(sketch, "E2438", {"start": v(19.16, 19.65) * mm, "end": v(19.16, 19.66) * mm});
            skLineSegment(sketch, "E2439", {"start": v(19.16, 19.66) * mm, "end": v(19.17, 19.66) * mm});
            skLineSegment(sketch, "E2440", {"start": v(19.17, 19.66) * mm, "end": v(19.17, 19.67) * mm});
            skLineSegment(sketch, "E2441", {"start": v(19.17, 19.67) * mm, "end": v(19.17, 19.67) * mm});
            skLineSegment(sketch, "E2442", {"start": v(19.17, 19.67) * mm, "end": v(19.17, 19.68) * mm});
            skLineSegment(sketch, "E2443", {"start": v(19.17, 19.68) * mm, "end": v(19.18, 19.69) * mm});
            skLineSegment(sketch, "E2444", {"start": v(19.18, 19.69) * mm, "end": v(19.18, 19.7) * mm});
            skLineSegment(sketch, "E2445", {"start": v(19.18, 19.7) * mm, "end": v(19.18, 19.7) * mm});
            skLineSegment(sketch, "E2446", {"start": v(19.18, 19.7) * mm, "end": v(19.19, 19.7) * mm});
            skLineSegment(sketch, "E2447", {"start": v(19.19, 19.7) * mm, "end": v(19.19, 19.7) * mm});
            skLineSegment(sketch, "E2448", {"start": v(19.19, 19.7) * mm, "end": v(19.2, 19.72) * mm});
            skLineSegment(sketch, "E2449", {"start": v(19.2, 19.72) * mm, "end": v(19.2, 19.72) * mm});
            skLineSegment(sketch, "E2450", {"start": v(19.2, 19.72) * mm, "end": v(19.2, 19.73) * mm});
            skLineSegment(sketch, "E2451", {"start": v(19.2, 19.73) * mm, "end": v(19.2, 19.73) * mm});
            skLineSegment(sketch, "E2452", {"start": v(19.2, 19.73) * mm, "end": v(19.2, 19.74) * mm});
            skLineSegment(sketch, "E2453", {"start": v(19.2, 19.74) * mm, "end": v(19.2, 19.74) * mm});
            skLineSegment(sketch, "E2454", {"start": v(19.2, 19.74) * mm, "end": v(19.2, 19.75) * mm});
            skLineSegment(sketch, "E2455", {"start": v(19.2, 19.75) * mm, "end": v(19.21, 19.76) * mm});
            skLineSegment(sketch, "E2456", {"start": v(19.21, 19.76) * mm, "end": v(19.21, 19.76) * mm});
            skLineSegment(sketch, "E2457", {"start": v(19.21, 19.76) * mm, "end": v(19.22, 19.77) * mm});
            skLineSegment(sketch, "E2458", {"start": v(19.22, 19.77) * mm, "end": v(19.22, 19.77) * mm});
            skLineSegment(sketch, "E2459", {"start": v(19.22, 19.77) * mm, "end": v(19.22, 19.78) * mm});
            skLineSegment(sketch, "E2460", {"start": v(19.22, 19.78) * mm, "end": v(19.22, 19.79) * mm});
            skLineSegment(sketch, "E2461", {"start": v(19.22, 19.79) * mm, "end": v(19.23, 19.8) * mm});
            skLineSegment(sketch, "E2462", {"start": v(19.23, 19.8) * mm, "end": v(19.23, 19.8) * mm});
            skLineSegment(sketch, "E2463", {"start": v(19.23, 19.8) * mm, "end": v(19.24, 19.8) * mm});
            skLineSegment(sketch, "E2464", {"start": v(19.24, 19.8) * mm, "end": v(19.24, 19.81) * mm});
            skLineSegment(sketch, "E2465", {"start": v(19.24, 19.81) * mm, "end": v(19.24, 19.82) * mm});
            skLineSegment(sketch, "E2466", {"start": v(19.24, 19.82) * mm, "end": v(19.24, 19.83) * mm});
            skLineSegment(sketch, "E2467", {"start": v(19.24, 19.83) * mm, "end": v(19.25, 19.83) * mm});
            skLineSegment(sketch, "E2468", {"start": v(19.25, 19.83) * mm, "end": v(19.25, 19.84) * mm});
            skLineSegment(sketch, "E2469", {"start": v(19.25, 19.84) * mm, "end": v(19.25, 19.84) * mm});
            skLineSegment(sketch, "E2470", {"start": v(19.25, 19.84) * mm, "end": v(19.26, 19.85) * mm});
            skLineSegment(sketch, "E2471", {"start": v(19.26, 19.85) * mm, "end": v(19.26, 19.86) * mm});
            skLineSegment(sketch, "E2472", {"start": v(19.26, 19.86) * mm, "end": v(19.26, 19.86) * mm});
            skLineSegment(sketch, "E2473", {"start": v(19.26, 19.86) * mm, "end": v(19.26, 19.87) * mm});
            skLineSegment(sketch, "E2474", {"start": v(19.26, 19.87) * mm, "end": v(19.27, 19.87) * mm});
            skLineSegment(sketch, "E2475", {"start": v(19.27, 19.87) * mm, "end": v(19.27, 19.88) * mm});
            skLineSegment(sketch, "E2476", {"start": v(19.27, 19.88) * mm, "end": v(19.27, 19.88) * mm});
            skLineSegment(sketch, "E2477", {"start": v(19.27, 19.88) * mm, "end": v(19.27, 19.9) * mm});
            skLineSegment(sketch, "E2478", {"start": v(19.27, 19.9) * mm, "end": v(19.28, 19.9) * mm});
            skLineSegment(sketch, "E2479", {"start": v(19.28, 19.9) * mm, "end": v(19.28, 19.9) * mm});
            skLineSegment(sketch, "E2480", {"start": v(19.28, 19.9) * mm, "end": v(19.29, 19.91) * mm});
            skLineSegment(sketch, "E2481", {"start": v(19.29, 19.91) * mm, "end": v(19.29, 19.92) * mm});
            skLineSegment(sketch, "E2482", {"start": v(19.29, 19.92) * mm, "end": v(19.3, 19.93) * mm});
            skLineSegment(sketch, "E2483", {"start": v(19.3, 19.93) * mm, "end": v(19.3, 19.93) * mm});
            skLineSegment(sketch, "E2484", {"start": v(19.3, 19.93) * mm, "end": v(19.3, 19.94) * mm});
            skLineSegment(sketch, "E2485", {"start": v(19.3, 19.94) * mm, "end": v(19.3, 19.94) * mm});
            skLineSegment(sketch, "E2486", {"start": v(19.3, 19.94) * mm, "end": v(19.3, 19.95) * mm});
            skLineSegment(sketch, "E2487", {"start": v(19.3, 19.95) * mm, "end": v(19.3, 19.95) * mm});
            skLineSegment(sketch, "E2488", {"start": v(19.3, 19.95) * mm, "end": v(19.3, 19.96) * mm});
            skLineSegment(sketch, "E2489", {"start": v(19.3, 19.96) * mm, "end": v(19.31, 19.97) * mm});
            skLineSegment(sketch, "E2490", {"start": v(19.31, 19.97) * mm, "end": v(19.31, 19.97) * mm});
            skLineSegment(sketch, "E2491", {"start": v(19.31, 19.97) * mm, "end": v(19.32, 19.98) * mm});
            skLineSegment(sketch, "E2492", {"start": v(19.32, 19.98) * mm, "end": v(19.32, 19.98) * mm});
            skLineSegment(sketch, "E2493", {"start": v(19.32, 19.98) * mm, "end": v(19.32, 19.99) * mm});
            skLineSegment(sketch, "E2494", {"start": v(19.32, 19.99) * mm, "end": v(19.32, 20) * mm});
            skLineSegment(sketch, "E2495", {"start": v(19.32, 20) * mm, "end": v(19.33, 20) * mm});
            skLineSegment(sketch, "E2496", {"start": v(19.33, 20) * mm, "end": v(19.33, 20) * mm});
            skLineSegment(sketch, "E2497", {"start": v(19.33, 20) * mm, "end": v(19.33, 20.01) * mm});
            skLineSegment(sketch, "E2498", {"start": v(19.33, 20.01) * mm, "end": v(19.34, 20.02) * mm});
            skLineSegment(sketch, "E2499", {"start": v(19.34, 20.02) * mm, "end": v(19.34, 20.02) * mm});
            skLineSegment(sketch, "E2500", {"start": v(19.34, 20.02) * mm, "end": v(19.34, 20.03) * mm});
            skLineSegment(sketch, "E2501", {"start": v(19.34, 20.03) * mm, "end": v(19.34, 20.04) * mm});
            skLineSegment(sketch, "E2502", {"start": v(19.34, 20.04) * mm, "end": v(19.35, 20.04) * mm});
            skLineSegment(sketch, "E2503", {"start": v(19.35, 20.04) * mm, "end": v(19.35, 20.05) * mm});
            skLineSegment(sketch, "E2504", {"start": v(19.35, 20.05) * mm, "end": v(19.35, 20.05) * mm});
            skLineSegment(sketch, "E2505", {"start": v(19.35, 20.05) * mm, "end": v(19.36, 20.06) * mm});
            skLineSegment(sketch, "E2506", {"start": v(19.36, 20.06) * mm, "end": v(19.36, 20.06) * mm});
            skLineSegment(sketch, "E2507", {"start": v(19.36, 20.06) * mm, "end": v(19.36, 20.07) * mm});
            skLineSegment(sketch, "E2508", {"start": v(19.36, 20.07) * mm, "end": v(19.36, 20.08) * mm});
            skLineSegment(sketch, "E2509", {"start": v(19.36, 20.08) * mm, "end": v(19.37, 20.08) * mm});
            skLineSegment(sketch, "E2510", {"start": v(19.37, 20.08) * mm, "end": v(19.37, 20.09) * mm});
            skLineSegment(sketch, "E2511", {"start": v(19.37, 20.09) * mm, "end": v(19.37, 20.1) * mm});
            skLineSegment(sketch, "E2512", {"start": v(19.37, 20.1) * mm, "end": v(19.37, 20.1) * mm});
            skLineSegment(sketch, "E2513", {"start": v(19.37, 20.1) * mm, "end": v(19.38, 20.1) * mm});
            skLineSegment(sketch, "E2514", {"start": v(19.38, 20.1) * mm, "end": v(19.38, 20.11) * mm});
            skLineSegment(sketch, "E2515", {"start": v(19.38, 20.11) * mm, "end": v(19.38, 20.12) * mm});
            skLineSegment(sketch, "E2516", {"start": v(19.38, 20.12) * mm, "end": v(19.39, 20.12) * mm});
            skLineSegment(sketch, "E2517", {"start": v(19.39, 20.12) * mm, "end": v(19.39, 20.13) * mm});
            skLineSegment(sketch, "E2518", {"start": v(19.39, 20.13) * mm, "end": v(19.4, 20.13) * mm});
            skLineSegment(sketch, "E2519", {"start": v(19.4, 20.13) * mm, "end": v(19.4, 20.14) * mm});
            skLineSegment(sketch, "E2520", {"start": v(19.4, 20.14) * mm, "end": v(19.4, 20.15) * mm});
            skLineSegment(sketch, "E2521", {"start": v(19.4, 20.15) * mm, "end": v(19.4, 20.15) * mm});
            skLineSegment(sketch, "E2522", {"start": v(19.4, 20.15) * mm, "end": v(19.4, 20.16) * mm});
            skLineSegment(sketch, "E2523", {"start": v(19.4, 20.16) * mm, "end": v(19.4, 20.16) * mm});
            skLineSegment(sketch, "E2524", {"start": v(19.4, 20.16) * mm, "end": v(19.4, 20.17) * mm});
            skLineSegment(sketch, "E2525", {"start": v(19.4, 20.17) * mm, "end": v(19.41, 20.18) * mm});
            skLineSegment(sketch, "E2526", {"start": v(19.41, 20.18) * mm, "end": v(19.41, 20.18) * mm});
            skLineSegment(sketch, "E2527", {"start": v(19.41, 20.18) * mm, "end": v(19.42, 20.19) * mm});
            skLineSegment(sketch, "E2528", {"start": v(19.42, 20.19) * mm, "end": v(19.42, 20.2) * mm});
            skLineSegment(sketch, "E2529", {"start": v(19.42, 20.2) * mm, "end": v(19.42, 20.2) * mm});
            skLineSegment(sketch, "E2530", {"start": v(19.42, 20.2) * mm, "end": v(19.43, 20.21) * mm});
            skLineSegment(sketch, "E2531", {"start": v(19.43, 20.21) * mm, "end": v(19.43, 20.22) * mm});
            skLineSegment(sketch, "E2532", {"start": v(19.43, 20.22) * mm, "end": v(19.43, 20.22) * mm});
            skLineSegment(sketch, "E2533", {"start": v(19.43, 20.22) * mm, "end": v(19.44, 20.23) * mm});
            skLineSegment(sketch, "E2534", {"start": v(19.44, 20.23) * mm, "end": v(19.44, 20.23) * mm});
            skLineSegment(sketch, "E2535", {"start": v(19.44, 20.23) * mm, "end": v(19.44, 20.24) * mm});
            skLineSegment(sketch, "E2536", {"start": v(19.44, 20.24) * mm, "end": v(19.44, 20.25) * mm});
            skLineSegment(sketch, "E2537", {"start": v(19.44, 20.25) * mm, "end": v(19.45, 20.25) * mm});
            skLineSegment(sketch, "E2538", {"start": v(19.45, 20.25) * mm, "end": v(19.45, 20.26) * mm});
            skLineSegment(sketch, "E2539", {"start": v(19.45, 20.26) * mm, "end": v(19.45, 20.26) * mm});
            skLineSegment(sketch, "E2540", {"start": v(19.45, 20.26) * mm, "end": v(19.45, 20.27) * mm});
            skLineSegment(sketch, "E2541", {"start": v(19.45, 20.27) * mm, "end": v(19.46, 20.27) * mm});
            skLineSegment(sketch, "E2542", {"start": v(19.46, 20.27) * mm, "end": v(19.46, 20.28) * mm});
            skLineSegment(sketch, "E2543", {"start": v(19.46, 20.28) * mm, "end": v(19.46, 20.29) * mm});
            skLineSegment(sketch, "E2544", {"start": v(19.46, 20.29) * mm, "end": v(19.47, 20.3) * mm});
            skLineSegment(sketch, "E2545", {"start": v(19.47, 20.3) * mm, "end": v(19.47, 20.3) * mm});
            skLineSegment(sketch, "E2546", {"start": v(19.47, 20.3) * mm, "end": v(19.48, 20.31) * mm});
            skLineSegment(sketch, "E2547", {"start": v(19.48, 20.31) * mm, "end": v(19.48, 20.32) * mm});
            skLineSegment(sketch, "E2548", {"start": v(19.48, 20.32) * mm, "end": v(19.48, 20.33) * mm});
            skLineSegment(sketch, "E2549", {"start": v(19.48, 20.33) * mm, "end": v(19.49, 20.33) * mm});
            skLineSegment(sketch, "E2550", {"start": v(19.49, 20.33) * mm, "end": v(19.49, 20.34) * mm});
            skLineSegment(sketch, "E2551", {"start": v(19.49, 20.34) * mm, "end": v(19.5, 20.34) * mm});
            skLineSegment(sketch, "E2552", {"start": v(19.5, 20.34) * mm, "end": v(19.5, 20.35) * mm});
            skLineSegment(sketch, "E2553", {"start": v(19.5, 20.35) * mm, "end": v(19.5, 20.35) * mm});
            skLineSegment(sketch, "E2554", {"start": v(19.5, 20.35) * mm, "end": v(19.5, 20.36) * mm});
            skLineSegment(sketch, "E2555", {"start": v(19.5, 20.36) * mm, "end": v(19.5, 20.36) * mm});
            skLineSegment(sketch, "E2556", {"start": v(19.5, 20.36) * mm, "end": v(19.5, 20.37) * mm});
            skLineSegment(sketch, "E2557", {"start": v(19.5, 20.37) * mm, "end": v(19.5, 20.39) * mm});
            skLineSegment(sketch, "E2558", {"start": v(19.5, 20.39) * mm, "end": v(19.51, 20.4) * mm});
            skLineSegment(sketch, "E2559", {"start": v(19.51, 20.4) * mm, "end": v(19.52, 20.42) * mm});
            skLineSegment(sketch, "E2560", {"start": v(19.52, 20.42) * mm, "end": v(19.53, 20.44) * mm});
            skLineSegment(sketch, "E2561", {"start": v(19.53, 20.44) * mm, "end": v(19.54, 20.46) * mm});
            skLineSegment(sketch, "E2562", {"start": v(19.54, 20.46) * mm, "end": v(19.55, 20.49) * mm});
            skLineSegment(sketch, "E2563", {"start": v(19.55, 20.49) * mm, "end": v(19.56, 20.52) * mm});
            skLineSegment(sketch, "E2564", {"start": v(19.56, 20.52) * mm, "end": v(19.57, 20.55) * mm});
            skLineSegment(sketch, "E2565", {"start": v(19.57, 20.55) * mm, "end": v(19.59, 20.58) * mm});
            skLineSegment(sketch, "E2566", {"start": v(19.59, 20.58) * mm, "end": v(19.6, 20.61) * mm});
            skLineSegment(sketch, "E2567", {"start": v(19.6, 20.61) * mm, "end": v(19.62, 20.65) * mm});
            skLineSegment(sketch, "E2568", {"start": v(19.62, 20.65) * mm, "end": v(19.64, 20.7) * mm});
            skLineSegment(sketch, "E2569", {"start": v(19.64, 20.7) * mm, "end": v(19.66, 20.73) * mm});
            skLineSegment(sketch, "E2570", {"start": v(19.66, 20.73) * mm, "end": v(19.68, 20.78) * mm});
            skLineSegment(sketch, "E2571", {"start": v(19.68, 20.78) * mm, "end": v(19.7, 20.82) * mm});
            skLineSegment(sketch, "E2572", {"start": v(19.7, 20.82) * mm, "end": v(19.72, 20.87) * mm});
            skLineSegment(sketch, "E2573", {"start": v(19.72, 20.87) * mm, "end": v(19.75, 20.92) * mm});
            skLineSegment(sketch, "E2574", {"start": v(19.75, 20.92) * mm, "end": v(19.77, 20.97) * mm});
            skLineSegment(sketch, "E2575", {"start": v(19.77, 20.97) * mm, "end": v(19.8, 21.03) * mm});
            skLineSegment(sketch, "E2576", {"start": v(19.8, 21.03) * mm, "end": v(19.83, 21.08) * mm});
            skLineSegment(sketch, "E2577", {"start": v(19.83, 21.08) * mm, "end": v(19.86, 21.14) * mm});
            skLineSegment(sketch, "E2578", {"start": v(19.86, 21.14) * mm, "end": v(19.89, 21.2) * mm});
            skLineSegment(sketch, "E2579", {"start": v(19.89, 21.2) * mm, "end": v(19.92, 21.26) * mm});
            skLineSegment(sketch, "E2580", {"start": v(19.92, 21.26) * mm, "end": v(19.95, 21.32) * mm});
            skLineSegment(sketch, "E2581", {"start": v(19.95, 21.32) * mm, "end": v(19.99, 21.39) * mm});
            skLineSegment(sketch, "E2582", {"start": v(19.99, 21.39) * mm, "end": v(20.02, 21.45) * mm});
            skLineSegment(sketch, "E2583", {"start": v(20.02, 21.45) * mm, "end": v(20.06, 21.52) * mm});
            skLineSegment(sketch, "E2584", {"start": v(20.06, 21.52) * mm, "end": v(20.1, 21.6) * mm});
            skLineSegment(sketch, "E2585", {"start": v(20.1, 21.6) * mm, "end": v(20.14, 21.66) * mm});
            skLineSegment(sketch, "E2586", {"start": v(20.14, 21.66) * mm, "end": v(20.18, 21.73) * mm});
            skLineSegment(sketch, "E2587", {"start": v(20.18, 21.73) * mm, "end": v(20.23, 21.8) * mm});
            skLineSegment(sketch, "E2588", {"start": v(20.23, 21.8) * mm, "end": v(20.27, 21.88) * mm});
            skLineSegment(sketch, "E2589", {"start": v(20.27, 21.88) * mm, "end": v(20.32, 21.96) * mm});
            skLineSegment(sketch, "E2590", {"start": v(20.32, 21.96) * mm, "end": v(20.36, 22.03) * mm});
            skLineSegment(sketch, "E2591", {"start": v(20.36, 22.03) * mm, "end": v(20.41, 22.11) * mm});
            skLineSegment(sketch, "E2592", {"start": v(20.41, 22.11) * mm, "end": v(20.46, 22.2) * mm});
            skLineSegment(sketch, "E2593", {"start": v(20.46, 22.2) * mm, "end": v(20.52, 22.27) * mm});
            skLineSegment(sketch, "E2594", {"start": v(20.52, 22.27) * mm, "end": v(20.57, 22.35) * mm});
            skLineSegment(sketch, "E2595", {"start": v(20.57, 22.35) * mm, "end": v(20.63, 22.44) * mm});
            skLineSegment(sketch, "E2596", {"start": v(20.63, 22.44) * mm, "end": v(20.68, 22.52) * mm});
            skLineSegment(sketch, "E2597", {"start": v(20.68, 22.52) * mm, "end": v(20.74, 22.6) * mm});
            skLineSegment(sketch, "E2598", {"start": v(20.74, 22.6) * mm, "end": v(20.8, 22.69) * mm});
            skLineSegment(sketch, "E2599", {"start": v(20.8, 22.69) * mm, "end": v(20.86, 22.77) * mm});
            skLineSegment(sketch, "E2600", {"start": v(20.86, 22.77) * mm, "end": v(20.92, 22.86) * mm});
            skLineSegment(sketch, "E2601", {"start": v(20.92, 22.86) * mm, "end": v(20.99, 22.95) * mm});
            skLineSegment(sketch, "E2602", {"start": v(20.99, 22.95) * mm, "end": v(21.05, 23.04) * mm});
            skLineSegment(sketch, "E2603", {"start": v(21.05, 23.04) * mm, "end": v(21.12, 23.13) * mm});
            skLineSegment(sketch, "E2604", {"start": v(21.12, 23.13) * mm, "end": v(21.19, 23.22) * mm});
            skLineSegment(sketch, "E2605", {"start": v(21.19, 23.22) * mm, "end": v(21.26, 23.3) * mm});
            skLineSegment(sketch, "E2606", {"start": v(21.26, 23.3) * mm, "end": v(21.33, 23.4) * mm});
            skLineSegment(sketch, "E2607", {"start": v(21.33, 23.4) * mm, "end": v(21.4, 23.49) * mm});
            skLineSegment(sketch, "E2608", {"start": v(21.4, 23.49) * mm, "end": v(21.48, 23.58) * mm});
            skLineSegment(sketch, "E2609", {"start": v(21.48, 23.58) * mm, "end": v(21.56, 23.67) * mm});
            skLineSegment(sketch, "E2610", {"start": v(21.56, 23.67) * mm, "end": v(21.64, 23.76) * mm});
            skLineSegment(sketch, "E2611", {"start": v(21.64, 23.76) * mm, "end": v(21.72, 23.85) * mm});
            skLineSegment(sketch, "E2612", {"start": v(21.72, 23.85) * mm, "end": v(21.8, 23.95) * mm});
            skLineSegment(sketch, "E2613", {"start": v(21.8, 23.95) * mm, "end": v(21.89, 24.04) * mm});
            skLineSegment(sketch, "E2614", {"start": v(21.89, 24.04) * mm, "end": v(21.97, 24.13) * mm});
            skLineSegment(sketch, "E2615", {"start": v(21.97, 24.13) * mm, "end": v(22.06, 24.23) * mm});
            skLineSegment(sketch, "E2616", {"start": v(22.06, 24.23) * mm, "end": v(22.15, 24.32) * mm});
            skLineSegment(sketch, "E2617", {"start": v(22.15, 24.32) * mm, "end": v(22.24, 24.41) * mm});
            skLineSegment(sketch, "E2618", {"start": v(22.24, 24.41) * mm, "end": v(22.33, 24.5) * mm});
            skLineSegment(sketch, "E2619", {"start": v(22.33, 24.5) * mm, "end": v(22.42, 24.6) * mm});
            skLineSegment(sketch, "E2620", {"start": v(22.42, 24.6) * mm, "end": v(22.52, 24.7) * mm});
            skLineSegment(sketch, "E2621", {"start": v(22.52, 24.7) * mm, "end": v(22.62, 24.78) * mm});
            skLineSegment(sketch, "E2622", {"start": v(22.62, 24.78) * mm, "end": v(22.72, 24.88) * mm});
            skLineSegment(sketch, "E2623", {"start": v(22.72, 24.88) * mm, "end": v(22.82, 24.97) * mm});
            skLineSegment(sketch, "E2624", {"start": v(22.82, 24.97) * mm, "end": v(22.92, 25.06) * mm});
            skLineSegment(sketch, "E2625", {"start": v(22.92, 25.06) * mm, "end": v(23.03, 25.15) * mm});
            skLineSegment(sketch, "E2626", {"start": v(23.03, 25.15) * mm, "end": v(23.13, 25.24) * mm});
            skLineSegment(sketch, "E2627", {"start": v(23.13, 25.24) * mm, "end": v(23.24, 25.33) * mm});
            skLineSegment(sketch, "E2628", {"start": v(23.24, 25.33) * mm, "end": v(23.35, 25.42) * mm});
            skLineSegment(sketch, "E2629", {"start": v(23.35, 25.42) * mm, "end": v(23.47, 25.51) * mm});
            skLineSegment(sketch, "E2630", {"start": v(23.47, 25.51) * mm, "end": v(23.58, 25.6) * mm});
            skLineSegment(sketch, "E2631", {"start": v(23.58, 25.6) * mm, "end": v(23.7, 25.69) * mm});
            skLineSegment(sketch, "E2632", {"start": v(23.7, 25.69) * mm, "end": v(23.81, 25.78) * mm});
            skLineSegment(sketch, "E2633", {"start": v(23.81, 25.78) * mm, "end": v(23.93, 25.86) * mm});
            skLineSegment(sketch, "E2634", {"start": v(23.93, 25.86) * mm, "end": v(24.06, 25.95) * mm});
            skLineSegment(sketch, "E2635", {"start": v(24.06, 25.95) * mm, "end": v(24.18, 26.03) * mm});
            skLineSegment(sketch, "E2636", {"start": v(24.18, 26.03) * mm, "end": v(24.3, 26.12) * mm});
            skLineSegment(sketch, "E2637", {"start": v(24.3, 26.12) * mm, "end": v(24.43, 26.2) * mm});
            skLineSegment(sketch, "E2638", {"start": v(24.43, 26.2) * mm, "end": v(24.56, 26.28) * mm});
            skLineSegment(sketch, "E2639", {"start": v(24.56, 26.28) * mm, "end": v(24.7, 26.37) * mm});
            skLineSegment(sketch, "E2640", {"start": v(24.7, 26.37) * mm, "end": v(24.83, 26.45) * mm});
            skLineSegment(sketch, "E2641", {"start": v(24.83, 26.45) * mm, "end": v(24.96, 26.53) * mm});
            skLineSegment(sketch, "E2642", {"start": v(24.96, 26.53) * mm, "end": v(25.1, 26.6) * mm});
            skLineSegment(sketch, "E2643", {"start": v(25.1, 26.6) * mm, "end": v(25.24, 26.68) * mm});
            skLineSegment(sketch, "E2644", {"start": v(25.24, 26.68) * mm, "end": v(25.38, 26.76) * mm});
            skLineSegment(sketch, "E2645", {"start": v(25.38, 26.76) * mm, "end": v(25.53, 26.83) * mm});
            skLineSegment(sketch, "E2646", {"start": v(25.53, 26.83) * mm, "end": v(25.67, 26.9) * mm});
            skLineSegment(sketch, "E2647", {"start": v(25.67, 26.9) * mm, "end": v(25.82, 26.98) * mm});
            skLineSegment(sketch, "E2648", {"start": v(25.82, 26.98) * mm, "end": v(25.97, 27.05) * mm});
            skLineSegment(sketch, "E2649", {"start": v(25.97, 27.05) * mm, "end": v(26.12, 27.12) * mm});
            skLineSegment(sketch, "E2650", {"start": v(26.12, 27.12) * mm, "end": v(26.27, 27.18) * mm});
            skLineSegment(sketch, "E2651", {"start": v(26.27, 27.18) * mm, "end": v(26.43, 27.25) * mm});
            skLineSegment(sketch, "E2652", {"start": v(26.43, 27.25) * mm, "end": v(26.59, 27.31) * mm});
            skLineSegment(sketch, "E2653", {"start": v(26.59, 27.31) * mm, "end": v(26.75, 27.38) * mm});
            skLineSegment(sketch, "E2654", {"start": v(26.75, 27.38) * mm, "end": v(26.9, 27.44) * mm});
            skLineSegment(sketch, "E2655", {"start": v(26.9, 27.44) * mm, "end": v(27.07, 27.5) * mm});
            skLineSegment(sketch, "E2656", {"start": v(27.07, 27.5) * mm, "end": v(27.24, 27.55) * mm});
            skLineSegment(sketch, "E2657", {"start": v(27.24, 27.55) * mm, "end": v(27.4, 27.61) * mm});
            skLineSegment(sketch, "E2658", {"start": v(27.4, 27.61) * mm, "end": v(27.58, 27.66) * mm});
            skLineSegment(sketch, "E2659", {"start": v(27.58, 27.66) * mm, "end": v(27.75, 27.72) * mm});
            skLineSegment(sketch, "E2660", {"start": v(27.75, 27.72) * mm, "end": v(27.93, 27.77) * mm});
            skLineSegment(sketch, "E2661", {"start": v(27.93, 27.77) * mm, "end": v(28.1, 27.81) * mm});
            skLineSegment(sketch, "E2662", {"start": v(28.1, 27.81) * mm, "end": v(28.28, 27.86) * mm});
            skLineSegment(sketch, "E2663", {"start": v(28.28, 27.86) * mm, "end": v(28.46, 27.9) * mm});
            skLineSegment(sketch, "E2664", {"start": v(28.46, 27.9) * mm, "end": v(28.65, 27.95) * mm});
            skLineSegment(sketch, "E2665", {"start": v(28.65, 27.95) * mm, "end": v(28.83, 27.99) * mm});
            skLineSegment(sketch, "E2666", {"start": v(28.83, 27.99) * mm, "end": v(29.02, 28.02) * mm});
            skLineSegment(sketch, "E2667", {"start": v(29.02, 28.02) * mm, "end": v(29.21, 28.06) * mm});
            skLineSegment(sketch, "E2668", {"start": v(29.21, 28.06) * mm, "end": v(29.4, 28.1) * mm});
            skLineSegment(sketch, "E2669", {"start": v(29.4, 28.1) * mm, "end": v(29.6, 28.12) * mm});
            skLineSegment(sketch, "E2670", {"start": v(29.6, 28.12) * mm, "end": v(29.8, 28.15) * mm});
            skLineSegment(sketch, "E2671", {"start": v(29.8, 28.15) * mm, "end": v(30, 28.18) * mm});
            skLineSegment(sketch, "E2672", {"start": v(30, 28.18) * mm, "end": v(30.2, 28.2) * mm});
            skLineSegment(sketch, "E2673", {"start": v(30.2, 28.2) * mm, "end": v(30.4, 28.22) * mm});
            skLineSegment(sketch, "E2674", {"start": v(30.4, 28.22) * mm, "end": v(30.61, 28.24) * mm});
            skLineSegment(sketch, "E2675", {"start": v(30.61, 28.24) * mm, "end": v(30.82, 28.25) * mm});
            skLineSegment(sketch, "E2676", {"start": v(30.82, 28.25) * mm, "end": v(31.03, 28.26) * mm});
            skLineSegment(sketch, "E2677", {"start": v(31.03, 28.26) * mm, "end": v(31.24, 28.27) * mm});
            skLineSegment(sketch, "E2678", {"start": v(31.24, 28.27) * mm, "end": v(31.46, 28.28) * mm});
            skLineSegment(sketch, "E2679", {"start": v(31.46, 28.28) * mm, "end": v(31.68, 28.29) * mm});
            skLineSegment(sketch, "E2680", {"start": v(31.68, 28.29) * mm, "end": v(31.9, 28.29) * mm});
            skLineSegment(sketch, "E2681", {"start": v(31.9, 28.29) * mm, "end": v(31.9, 28.29) * mm});
            skLineSegment(sketch, "E2682", {"start": v(31.9, 28.29) * mm, "end": v(31.91, 28.29) * mm});
            skLineSegment(sketch, "E2683", {"start": v(31.91, 28.29) * mm, "end": v(31.92, 28.29) * mm});
            skLineSegment(sketch, "E2684", {"start": v(31.92, 28.29) * mm, "end": v(31.93, 28.29) * mm});
            skLineSegment(sketch, "E2685", {"start": v(31.93, 28.29) * mm, "end": v(31.94, 28.29) * mm});
            skLineSegment(sketch, "E2686", {"start": v(31.94, 28.29) * mm, "end": v(31.95, 28.29) * mm});
            skLineSegment(sketch, "E2687", {"start": v(31.95, 28.29) * mm, "end": v(31.96, 28.29) * mm});
            skLineSegment(sketch, "E2688", {"start": v(31.96, 28.29) * mm, "end": v(31.97, 28.29) * mm});
            skLineSegment(sketch, "E2689", {"start": v(31.97, 28.29) * mm, "end": v(31.99, 28.29) * mm});
            skLineSegment(sketch, "E2690", {"start": v(31.99, 28.29) * mm, "end": v(32, 28.28) * mm});
            skLineSegment(sketch, "E2691", {"start": v(32, 28.28) * mm, "end": v(32.02, 28.28) * mm});
            skLineSegment(sketch, "E2692", {"start": v(32.02, 28.28) * mm, "end": v(32.04, 28.28) * mm});
            skLineSegment(sketch, "E2693", {"start": v(32.04, 28.28) * mm, "end": v(32.06, 28.28) * mm});
            skLineSegment(sketch, "E2694", {"start": v(32.06, 28.28) * mm, "end": v(32.08, 28.28) * mm});
            skLineSegment(sketch, "E2695", {"start": v(32.08, 28.28) * mm, "end": v(32.1, 28.28) * mm});
            skLineSegment(sketch, "E2696", {"start": v(32.1, 28.28) * mm, "end": v(32.12, 28.28) * mm});
            skLineSegment(sketch, "E2697", {"start": v(32.12, 28.28) * mm, "end": v(32.14, 28.27) * mm});
            skLineSegment(sketch, "E2698", {"start": v(32.14, 28.27) * mm, "end": v(32.17, 28.27) * mm});
            skLineSegment(sketch, "E2699", {"start": v(32.17, 28.27) * mm, "end": v(32.2, 28.27) * mm});
            skLineSegment(sketch, "E2700", {"start": v(32.2, 28.27) * mm, "end": v(32.22, 28.27) * mm});
            skLineSegment(sketch, "E2701", {"start": v(32.22, 28.27) * mm, "end": v(32.25, 28.26) * mm});
            skLineSegment(sketch, "E2702", {"start": v(32.25, 28.26) * mm, "end": v(32.27, 28.26) * mm});
            skLineSegment(sketch, "E2703", {"start": v(32.27, 28.26) * mm, "end": v(32.3, 28.25) * mm});
            skLineSegment(sketch, "E2704", {"start": v(32.3, 28.25) * mm, "end": v(32.33, 28.25) * mm});
            skLineSegment(sketch, "E2705", {"start": v(32.33, 28.25) * mm, "end": v(32.36, 28.24) * mm});
            skLineSegment(sketch, "E2706", {"start": v(32.36, 28.24) * mm, "end": v(32.4, 28.24) * mm});
            skLineSegment(sketch, "E2707", {"start": v(32.4, 28.24) * mm, "end": v(32.42, 28.23) * mm});
            skLineSegment(sketch, "E2708", {"start": v(32.42, 28.23) * mm, "end": v(32.46, 28.23) * mm});
            skLineSegment(sketch, "E2709", {"start": v(32.46, 28.23) * mm, "end": v(32.5, 28.22) * mm});
            skLineSegment(sketch, "E2710", {"start": v(32.5, 28.22) * mm, "end": v(32.52, 28.22) * mm});
            skLineSegment(sketch, "E2711", {"start": v(32.52, 28.22) * mm, "end": v(32.56, 28.2) * mm});
            skLineSegment(sketch, "E2712", {"start": v(32.56, 28.2) * mm, "end": v(32.6, 28.2) * mm});
            skLineSegment(sketch, "E2713", {"start": v(32.6, 28.2) * mm, "end": v(32.63, 28.2) * mm});
            skLineSegment(sketch, "E2714", {"start": v(32.63, 28.2) * mm, "end": v(32.66, 28.18) * mm});
            skLineSegment(sketch, "E2715", {"start": v(32.66, 28.18) * mm, "end": v(32.7, 28.17) * mm});
            skLineSegment(sketch, "E2716", {"start": v(32.7, 28.17) * mm, "end": v(32.74, 28.16) * mm});
            skLineSegment(sketch, "E2717", {"start": v(32.74, 28.16) * mm, "end": v(32.77, 28.15) * mm});
            skLineSegment(sketch, "E2718", {"start": v(32.77, 28.15) * mm, "end": v(32.81, 28.14) * mm});
            skLineSegment(sketch, "E2719", {"start": v(32.81, 28.14) * mm, "end": v(32.85, 28.13) * mm});
            skLineSegment(sketch, "E2720", {"start": v(32.85, 28.13) * mm, "end": v(32.89, 28.12) * mm});
            skLineSegment(sketch, "E2721", {"start": v(32.89, 28.12) * mm, "end": v(32.93, 28.1) * mm});
            skLineSegment(sketch, "E2722", {"start": v(32.93, 28.1) * mm, "end": v(32.97, 28.1) * mm});
            skLineSegment(sketch, "E2723", {"start": v(32.97, 28.1) * mm, "end": v(33, 28.08) * mm});
            skLineSegment(sketch, "E2724", {"start": v(33, 28.08) * mm, "end": v(33.04, 28.07) * mm});
            skLineSegment(sketch, "E2725", {"start": v(33.04, 28.07) * mm, "end": v(33.08, 28.05) * mm});
            skLineSegment(sketch, "E2726", {"start": v(33.08, 28.05) * mm, "end": v(33.12, 28.03) * mm});
            skLineSegment(sketch, "E2727", {"start": v(33.12, 28.03) * mm, "end": v(33.16, 28.02) * mm});
            skLineSegment(sketch, "E2728", {"start": v(33.16, 28.02) * mm, "end": v(33.2, 28) * mm});
            skLineSegment(sketch, "E2729", {"start": v(33.2, 28) * mm, "end": v(33.24, 27.98) * mm});
            skLineSegment(sketch, "E2730", {"start": v(33.24, 27.98) * mm, "end": v(33.28, 27.96) * mm});
            skLineSegment(sketch, "E2731", {"start": v(33.28, 27.96) * mm, "end": v(33.32, 27.94) * mm});
            skLineSegment(sketch, "E2732", {"start": v(33.32, 27.94) * mm, "end": v(33.36, 27.92) * mm});
            skLineSegment(sketch, "E2733", {"start": v(33.36, 27.92) * mm, "end": v(33.4, 27.9) * mm});
            skLineSegment(sketch, "E2734", {"start": v(33.4, 27.9) * mm, "end": v(33.44, 27.88) * mm});
            skLineSegment(sketch, "E2735", {"start": v(33.44, 27.88) * mm, "end": v(33.48, 27.86) * mm});
            skLineSegment(sketch, "E2736", {"start": v(33.48, 27.86) * mm, "end": v(33.52, 27.83) * mm});
            skLineSegment(sketch, "E2737", {"start": v(33.52, 27.83) * mm, "end": v(33.56, 27.81) * mm});
            skLineSegment(sketch, "E2738", {"start": v(33.56, 27.81) * mm, "end": v(33.6, 27.79) * mm});
            skLineSegment(sketch, "E2739", {"start": v(33.6, 27.79) * mm, "end": v(33.64, 27.76) * mm});
            skLineSegment(sketch, "E2740", {"start": v(33.64, 27.76) * mm, "end": v(33.67, 27.73) * mm});
            skLineSegment(sketch, "E2741", {"start": v(33.67, 27.73) * mm, "end": v(33.71, 27.7) * mm});
            skLineSegment(sketch, "E2742", {"start": v(33.71, 27.7) * mm, "end": v(33.75, 27.68) * mm});
            skLineSegment(sketch, "E2743", {"start": v(33.75, 27.68) * mm, "end": v(33.79, 27.65) * mm});
            skLineSegment(sketch, "E2744", {"start": v(33.79, 27.65) * mm, "end": v(33.82, 27.62) * mm});
            skLineSegment(sketch, "E2745", {"start": v(33.82, 27.62) * mm, "end": v(33.86, 27.58) * mm});
            skLineSegment(sketch, "E2746", {"start": v(33.86, 27.58) * mm, "end": v(33.9, 27.55) * mm});
            skLineSegment(sketch, "E2747", {"start": v(33.9, 27.55) * mm, "end": v(33.93, 27.52) * mm});
            skLineSegment(sketch, "E2748", {"start": v(33.93, 27.52) * mm, "end": v(33.97, 27.48) * mm});
            skLineSegment(sketch, "E2749", {"start": v(33.97, 27.48) * mm, "end": v(34, 27.45) * mm});
            skLineSegment(sketch, "E2750", {"start": v(34, 27.45) * mm, "end": v(34.04, 27.41) * mm});
            skLineSegment(sketch, "E2751", {"start": v(34.04, 27.41) * mm, "end": v(34.07, 27.37) * mm});
            skLineSegment(sketch, "E2752", {"start": v(34.07, 27.37) * mm, "end": v(34.1, 27.33) * mm});
            skLineSegment(sketch, "E2753", {"start": v(34.1, 27.33) * mm, "end": v(34.13, 27.3) * mm});
            skLineSegment(sketch, "E2754", {"start": v(34.13, 27.3) * mm, "end": v(34.17, 27.25) * mm});
            skLineSegment(sketch, "E2755", {"start": v(34.17, 27.25) * mm, "end": v(34.2, 27.21) * mm});
            skLineSegment(sketch, "E2756", {"start": v(34.2, 27.21) * mm, "end": v(34.23, 27.17) * mm});
            skLineSegment(sketch, "E2757", {"start": v(34.23, 27.17) * mm, "end": v(34.26, 27.12) * mm});
            skLineSegment(sketch, "E2758", {"start": v(34.26, 27.12) * mm, "end": v(34.28, 27.08) * mm});
            skLineSegment(sketch, "E2759", {"start": v(34.28, 27.08) * mm, "end": v(34.31, 27.03) * mm});
            skLineSegment(sketch, "E2760", {"start": v(34.31, 27.03) * mm, "end": v(34.34, 26.98) * mm});
            skLineSegment(sketch, "E2761", {"start": v(34.34, 26.98) * mm, "end": v(34.36, 26.94) * mm});
            skLineSegment(sketch, "E2762", {"start": v(34.36, 26.94) * mm, "end": v(34.39, 26.89) * mm});
            skLineSegment(sketch, "E2763", {"start": v(34.39, 26.89) * mm, "end": v(34.41, 26.83) * mm});
            skLineSegment(sketch, "E2764", {"start": v(34.41, 26.83) * mm, "end": v(34.44, 26.78) * mm});
            skLineSegment(sketch, "E2765", {"start": v(34.44, 26.78) * mm, "end": v(34.46, 26.73) * mm});
            skLineSegment(sketch, "E2766", {"start": v(34.46, 26.73) * mm, "end": v(34.48, 26.67) * mm});
            skLineSegment(sketch, "E2767", {"start": v(34.48, 26.67) * mm, "end": v(34.5, 26.62) * mm});
            skLineSegment(sketch, "E2768", {"start": v(34.5, 26.62) * mm, "end": v(34.52, 26.56) * mm});
            skLineSegment(sketch, "E2769", {"start": v(34.52, 26.56) * mm, "end": v(34.53, 26.5) * mm});
            skLineSegment(sketch, "E2770", {"start": v(34.53, 26.5) * mm, "end": v(34.55, 26.44) * mm});
            skLineSegment(sketch, "E2771", {"start": v(34.55, 26.44) * mm, "end": v(34.57, 26.38) * mm});
            skLineSegment(sketch, "E2772", {"start": v(34.57, 26.38) * mm, "end": v(34.58, 26.31) * mm});
            skLineSegment(sketch, "E2773", {"start": v(34.58, 26.31) * mm, "end": v(34.6, 26.25) * mm});
            skLineSegment(sketch, "E2774", {"start": v(34.6, 26.25) * mm, "end": v(34.6, 26.18) * mm});
            skLineSegment(sketch, "E2775", {"start": v(34.6, 26.18) * mm, "end": v(34.61, 26.12) * mm});
            skLineSegment(sketch, "E2776", {"start": v(34.61, 26.12) * mm, "end": v(34.62, 26.05) * mm});
            skLineSegment(sketch, "E2777", {"start": v(34.62, 26.05) * mm, "end": v(34.63, 25.98) * mm});
            skLineSegment(sketch, "E2778", {"start": v(34.63, 25.98) * mm, "end": v(34.64, 25.9) * mm});
            skLineSegment(sketch, "E2779", {"start": v(34.64, 25.9) * mm, "end": v(34.64, 25.83) * mm});
            skLineSegment(sketch, "E2780", {"start": v(34.64, 25.83) * mm, "end": v(34.64, 25.76) * mm});
            skLineSegment(sketch, "E2781", {"start": v(34.64, 25.76) * mm, "end": v(34.65, 25.68) * mm});
            skLineSegment(sketch, "E2782", {"start": v(34.65, 25.68) * mm, "end": v(34.65, 25.6) * mm});
            skLineSegment(sketch, "E2783", {"start": v(34.65, 25.6) * mm, "end": v(34.64, 25.53) * mm});
            skLineSegment(sketch, "E2784", {"start": v(34.64, 25.53) * mm, "end": v(34.64, 25.45) * mm});
            skLineSegment(sketch, "E2785", {"start": v(34.64, 25.45) * mm, "end": v(34.64, 25.36) * mm});
            skLineSegment(sketch, "E2786", {"start": v(34.64, 25.36) * mm, "end": v(34.63, 25.28) * mm});
            skLineSegment(sketch, "E2787", {"start": v(34.63, 25.28) * mm, "end": v(34.62, 25.2) * mm});
            skLineSegment(sketch, "E2788", {"start": v(34.62, 25.2) * mm, "end": v(34.61, 25.1) * mm});
            skLineSegment(sketch, "E2789", {"start": v(34.61, 25.1) * mm, "end": v(34.6, 25.02) * mm});
            skLineSegment(sketch, "E2790", {"start": v(34.6, 25.02) * mm, "end": v(34.59, 24.93) * mm});
            skLineSegment(sketch, "E2791", {"start": v(34.59, 24.93) * mm, "end": v(34.57, 24.84) * mm});
            skLineSegment(sketch, "E2792", {"start": v(34.57, 24.84) * mm, "end": v(34.56, 24.75) * mm});
            skLineSegment(sketch, "E2793", {"start": v(34.56, 24.75) * mm, "end": v(34.54, 24.65) * mm});
            skLineSegment(sketch, "E2794", {"start": v(34.54, 24.65) * mm, "end": v(34.52, 24.55) * mm});
            skLineSegment(sketch, "E2795", {"start": v(34.52, 24.55) * mm, "end": v(34.5, 24.46) * mm});
            skLineSegment(sketch, "E2796", {"start": v(34.5, 24.46) * mm, "end": v(34.47, 24.36) * mm});
            skLineSegment(sketch, "E2797", {"start": v(34.47, 24.36) * mm, "end": v(34.44, 24.25) * mm});
            skLineSegment(sketch, "E2798", {"start": v(34.44, 24.25) * mm, "end": v(34.42, 24.15) * mm});
            skLineSegment(sketch, "E2799", {"start": v(34.42, 24.15) * mm, "end": v(34.39, 24.05) * mm});
            skLineSegment(sketch, "E2800", {"start": v(34.39, 24.05) * mm, "end": v(34.35, 23.94) * mm});
            skLineSegment(sketch, "E2801", {"start": v(34.35, 23.94) * mm, "end": v(34.32, 23.83) * mm});
            skLineSegment(sketch, "E2802", {"start": v(34.32, 23.83) * mm, "end": v(34.28, 23.72) * mm});
            skLineSegment(sketch, "E2803", {"start": v(34.28, 23.72) * mm, "end": v(34.24, 23.6) * mm});
            skLineSegment(sketch, "E2804", {"start": v(34.24, 23.6) * mm, "end": v(34.2, 23.5) * mm});
            skLineSegment(sketch, "E2805", {"start": v(34.2, 23.5) * mm, "end": v(34.16, 23.38) * mm});
            skLineSegment(sketch, "E2806", {"start": v(34.16, 23.38) * mm, "end": v(34.11, 23.26) * mm});
            skLineSegment(sketch, "E2807", {"start": v(34.11, 23.26) * mm, "end": v(34.12, 23.26) * mm});
            skLineSegment(sketch, "E2808", {"start": v(34.12, 23.26) * mm, "end": v(34.12, 23.26) * mm});
            skLineSegment(sketch, "E2809", {"start": v(34.12, 23.26) * mm, "end": v(34.13, 23.26) * mm});
            skLineSegment(sketch, "E2810", {"start": v(34.13, 23.26) * mm, "end": v(34.13, 23.26) * mm});
            skLineSegment(sketch, "E2811", {"start": v(34.13, 23.26) * mm, "end": v(34.14, 23.26) * mm});
            skLineSegment(sketch, "E2812", {"start": v(34.14, 23.26) * mm, "end": v(34.14, 23.26) * mm});
            skLineSegment(sketch, "E2813", {"start": v(34.14, 23.26) * mm, "end": v(34.15, 23.26) * mm});
            skLineSegment(sketch, "E2814", {"start": v(34.15, 23.26) * mm, "end": v(34.15, 23.26) * mm});
            skLineSegment(sketch, "E2815", {"start": v(34.15, 23.26) * mm, "end": v(34.16, 23.26) * mm});
            skLineSegment(sketch, "E2816", {"start": v(34.16, 23.26) * mm, "end": v(34.16, 23.26) * mm});
            skLineSegment(sketch, "E2817", {"start": v(34.16, 23.26) * mm, "end": v(34.17, 23.26) * mm});
            skLineSegment(sketch, "E2818", {"start": v(34.17, 23.26) * mm, "end": v(34.17, 23.26) * mm});
            skLineSegment(sketch, "E2819", {"start": v(34.17, 23.26) * mm, "end": v(34.15, 23.2) * mm});
            skLineSegment(sketch, "E2820", {"start": v(34.15, 23.2) * mm, "end": v(34.13, 23.15) * mm});
            skLineSegment(sketch, "E2821", {"start": v(34.13, 23.15) * mm, "end": v(34.11, 23.1) * mm});
            skLineSegment(sketch, "E2822", {"start": v(34.11, 23.1) * mm, "end": v(34.1, 23.04) * mm});
            skLineSegment(sketch, "E2823", {"start": v(34.1, 23.04) * mm, "end": v(34.07, 22.99) * mm});
            skLineSegment(sketch, "E2824", {"start": v(34.07, 22.99) * mm, "end": v(34.06, 22.93) * mm});
            skLineSegment(sketch, "E2825", {"start": v(34.06, 22.93) * mm, "end": v(34.04, 22.88) * mm});
            skLineSegment(sketch, "E2826", {"start": v(34.04, 22.88) * mm, "end": v(34.02, 22.83) * mm});
            skLineSegment(sketch, "E2827", {"start": v(34.02, 22.83) * mm, "end": v(34, 22.77) * mm});
            skLineSegment(sketch, "E2828", {"start": v(34, 22.77) * mm, "end": v(33.98, 22.72) * mm});
            skLineSegment(sketch, "E2829", {"start": v(33.98, 22.72) * mm, "end": v(33.96, 22.66) * mm});
            skLineSegment(sketch, "E2830", {"start": v(33.96, 22.66) * mm, "end": v(33.95, 22.61) * mm});
            skLineSegment(sketch, "E2831", {"start": v(33.95, 22.61) * mm, "end": v(33.93, 22.56) * mm});
            skLineSegment(sketch, "E2832", {"start": v(33.93, 22.56) * mm, "end": v(33.9, 22.5) * mm});
            skLineSegment(sketch, "E2833", {"start": v(33.9, 22.5) * mm, "end": v(33.89, 22.45) * mm});
            skLineSegment(sketch, "E2834", {"start": v(33.89, 22.45) * mm, "end": v(33.87, 22.4) * mm});
            skLineSegment(sketch, "E2835", {"start": v(33.87, 22.4) * mm, "end": v(33.85, 22.35) * mm});
            skLineSegment(sketch, "E2836", {"start": v(33.85, 22.35) * mm, "end": v(33.83, 22.3) * mm});
            skLineSegment(sketch, "E2837", {"start": v(33.83, 22.3) * mm, "end": v(33.81, 22.24) * mm});
            skLineSegment(sketch, "E2838", {"start": v(33.81, 22.24) * mm, "end": v(33.8, 22.19) * mm});
            skLineSegment(sketch, "E2839", {"start": v(33.8, 22.19) * mm, "end": v(33.78, 22.13) * mm});
            skLineSegment(sketch, "E2840", {"start": v(33.78, 22.13) * mm, "end": v(33.76, 22.08) * mm});
            skLineSegment(sketch, "E2841", {"start": v(33.76, 22.08) * mm, "end": v(33.74, 22.03) * mm});
            skLineSegment(sketch, "E2842", {"start": v(33.74, 22.03) * mm, "end": v(33.72, 21.98) * mm});
            skLineSegment(sketch, "E2843", {"start": v(33.72, 21.98) * mm, "end": v(33.7, 21.93) * mm});
            skLineSegment(sketch, "E2844", {"start": v(33.7, 21.93) * mm, "end": v(33.68, 21.87) * mm});
            skLineSegment(sketch, "E2845", {"start": v(33.68, 21.87) * mm, "end": v(33.66, 21.82) * mm});
            skLineSegment(sketch, "E2846", {"start": v(33.66, 21.82) * mm, "end": v(33.64, 21.77) * mm});
            skLineSegment(sketch, "E2847", {"start": v(33.64, 21.77) * mm, "end": v(33.62, 21.72) * mm});
            skLineSegment(sketch, "E2848", {"start": v(33.62, 21.72) * mm, "end": v(33.6, 21.67) * mm});
            skLineSegment(sketch, "E2849", {"start": v(33.6, 21.67) * mm, "end": v(33.59, 21.61) * mm});
            skLineSegment(sketch, "E2850", {"start": v(33.59, 21.61) * mm, "end": v(33.57, 21.56) * mm});
            skLineSegment(sketch, "E2851", {"start": v(33.57, 21.56) * mm, "end": v(33.55, 21.51) * mm});
            skLineSegment(sketch, "E2852", {"start": v(33.55, 21.51) * mm, "end": v(33.53, 21.46) * mm});
            skLineSegment(sketch, "E2853", {"start": v(33.53, 21.46) * mm, "end": v(33.5, 21.4) * mm});
            skLineSegment(sketch, "E2854", {"start": v(33.5, 21.4) * mm, "end": v(33.49, 21.36) * mm});
            skLineSegment(sketch, "E2855", {"start": v(33.49, 21.36) * mm, "end": v(33.47, 21.3) * mm});
            skLineSegment(sketch, "E2856", {"start": v(33.47, 21.3) * mm, "end": v(33.45, 21.26) * mm});
            skLineSegment(sketch, "E2857", {"start": v(33.45, 21.26) * mm, "end": v(33.43, 21.2) * mm});
            skLineSegment(sketch, "E2858", {"start": v(33.43, 21.2) * mm, "end": v(33.41, 21.16) * mm});
            skLineSegment(sketch, "E2859", {"start": v(33.41, 21.16) * mm, "end": v(33.4, 21.1) * mm});
            skLineSegment(sketch, "E2860", {"start": v(33.4, 21.1) * mm, "end": v(33.37, 21.06) * mm});
            skLineSegment(sketch, "E2861", {"start": v(33.37, 21.06) * mm, "end": v(33.36, 21) * mm});
            skLineSegment(sketch, "E2862", {"start": v(33.36, 21) * mm, "end": v(33.34, 20.96) * mm});
            skLineSegment(sketch, "E2863", {"start": v(33.34, 20.96) * mm, "end": v(33.32, 20.9) * mm});
            skLineSegment(sketch, "E2864", {"start": v(33.32, 20.9) * mm, "end": v(33.3, 20.86) * mm});
            skLineSegment(sketch, "E2865", {"start": v(33.3, 20.86) * mm, "end": v(33.28, 20.8) * mm});
            skLineSegment(sketch, "E2866", {"start": v(33.28, 20.8) * mm, "end": v(33.26, 20.76) * mm});
            skLineSegment(sketch, "E2867", {"start": v(33.26, 20.76) * mm, "end": v(33.24, 20.7) * mm});
            skLineSegment(sketch, "E2868", {"start": v(33.24, 20.7) * mm, "end": v(33.22, 20.66) * mm});
            skLineSegment(sketch, "E2869", {"start": v(33.22, 20.66) * mm, "end": v(33.2, 20.61) * mm});
            skLineSegment(sketch, "E2870", {"start": v(33.2, 20.61) * mm, "end": v(33.18, 20.56) * mm});
            skLineSegment(sketch, "E2871", {"start": v(33.18, 20.56) * mm, "end": v(33.16, 20.52) * mm});
            skLineSegment(sketch, "E2872", {"start": v(33.16, 20.52) * mm, "end": v(33.15, 20.47) * mm});
            skLineSegment(sketch, "E2873", {"start": v(33.15, 20.47) * mm, "end": v(33.13, 20.42) * mm});
            skLineSegment(sketch, "E2874", {"start": v(33.13, 20.42) * mm, "end": v(33.1, 20.37) * mm});
            skLineSegment(sketch, "E2875", {"start": v(33.1, 20.37) * mm, "end": v(33.09, 20.32) * mm});
            skLineSegment(sketch, "E2876", {"start": v(33.09, 20.32) * mm, "end": v(33.07, 20.28) * mm});
            skLineSegment(sketch, "E2877", {"start": v(33.07, 20.28) * mm, "end": v(33.05, 20.23) * mm});
            skLineSegment(sketch, "E2878", {"start": v(33.05, 20.23) * mm, "end": v(33.03, 20.18) * mm});
            skLineSegment(sketch, "E2879", {"start": v(33.03, 20.18) * mm, "end": v(33.01, 20.14) * mm});
            skLineSegment(sketch, "E2880", {"start": v(33.01, 20.14) * mm, "end": v(33, 20.1) * mm});
            skLineSegment(sketch, "E2881", {"start": v(33, 20.1) * mm, "end": v(32.98, 20.04) * mm});
            skLineSegment(sketch, "E2882", {"start": v(32.98, 20.04) * mm, "end": v(32.96, 20) * mm});
            skLineSegment(sketch, "E2883", {"start": v(32.96, 20) * mm, "end": v(32.94, 19.95) * mm});
            skLineSegment(sketch, "E2884", {"start": v(32.94, 19.95) * mm, "end": v(32.92, 19.9) * mm});
            skLineSegment(sketch, "E2885", {"start": v(32.92, 19.9) * mm, "end": v(32.9, 19.86) * mm});
            skLineSegment(sketch, "E2886", {"start": v(32.9, 19.86) * mm, "end": v(32.88, 19.82) * mm});
            skLineSegment(sketch, "E2887", {"start": v(32.88, 19.82) * mm, "end": v(32.86, 19.77) * mm});
            skLineSegment(sketch, "E2888", {"start": v(32.86, 19.77) * mm, "end": v(32.85, 19.73) * mm});
            skLineSegment(sketch, "E2889", {"start": v(32.85, 19.73) * mm, "end": v(32.83, 19.68) * mm});
            skLineSegment(sketch, "E2890", {"start": v(32.83, 19.68) * mm, "end": v(32.8, 19.64) * mm});
            skLineSegment(sketch, "E2891", {"start": v(32.8, 19.64) * mm, "end": v(32.8, 19.6) * mm});
            skLineSegment(sketch, "E2892", {"start": v(32.8, 19.6) * mm, "end": v(32.77, 19.55) * mm});
            skLineSegment(sketch, "E2893", {"start": v(32.77, 19.55) * mm, "end": v(32.76, 19.5) * mm});
            skLineSegment(sketch, "E2894", {"start": v(32.76, 19.5) * mm, "end": v(32.74, 19.46) * mm});
            skLineSegment(sketch, "E2895", {"start": v(32.74, 19.46) * mm, "end": v(32.72, 19.42) * mm});
            skLineSegment(sketch, "E2896", {"start": v(32.72, 19.42) * mm, "end": v(32.7, 19.37) * mm});
            skLineSegment(sketch, "E2897", {"start": v(32.7, 19.37) * mm, "end": v(32.68, 19.33) * mm});
            skLineSegment(sketch, "E2898", {"start": v(32.68, 19.33) * mm, "end": v(32.67, 19.29) * mm});
            skLineSegment(sketch, "E2899", {"start": v(32.67, 19.29) * mm, "end": v(32.65, 19.25) * mm});
            skLineSegment(sketch, "E2900", {"start": v(32.65, 19.25) * mm, "end": v(32.63, 19.2) * mm});
            skLineSegment(sketch, "E2901", {"start": v(32.63, 19.2) * mm, "end": v(32.61, 19.16) * mm});
            skLineSegment(sketch, "E2902", {"start": v(32.61, 19.16) * mm, "end": v(32.6, 19.12) * mm});
            skLineSegment(sketch, "E2903", {"start": v(32.6, 19.12) * mm, "end": v(32.58, 19.08) * mm});
            skLineSegment(sketch, "E2904", {"start": v(32.58, 19.08) * mm, "end": v(32.56, 19.04) * mm});
            skLineSegment(sketch, "E2905", {"start": v(32.56, 19.04) * mm, "end": v(32.54, 19) * mm});
            skLineSegment(sketch, "E2906", {"start": v(32.54, 19) * mm, "end": v(32.53, 18.96) * mm});
            skLineSegment(sketch, "E2907", {"start": v(32.53, 18.96) * mm, "end": v(32.5, 18.92) * mm});
            skLineSegment(sketch, "E2908", {"start": v(32.5, 18.92) * mm, "end": v(32.5, 18.88) * mm});
            skLineSegment(sketch, "E2909", {"start": v(32.5, 18.88) * mm, "end": v(32.48, 18.84) * mm});
            skLineSegment(sketch, "E2910", {"start": v(32.48, 18.84) * mm, "end": v(32.46, 18.8) * mm});
            skLineSegment(sketch, "E2911", {"start": v(32.46, 18.8) * mm, "end": v(32.44, 18.76) * mm});
            skLineSegment(sketch, "E2912", {"start": v(32.44, 18.76) * mm, "end": v(32.43, 18.72) * mm});
            skLineSegment(sketch, "E2913", {"start": v(32.43, 18.72) * mm, "end": v(32.4, 18.68) * mm});
            skLineSegment(sketch, "E2914", {"start": v(32.4, 18.68) * mm, "end": v(32.4, 18.64) * mm});
            skLineSegment(sketch, "E2915", {"start": v(32.4, 18.64) * mm, "end": v(32.38, 18.6) * mm});
            skLineSegment(sketch, "E2916", {"start": v(32.38, 18.6) * mm, "end": v(32.36, 18.57) * mm});
            skLineSegment(sketch, "E2917", {"start": v(32.36, 18.57) * mm, "end": v(32.34, 18.53) * mm});
            skLineSegment(sketch, "E2918", {"start": v(32.34, 18.53) * mm, "end": v(32.33, 18.5) * mm});
            skLineSegment(sketch, "E2919", {"start": v(32.33, 18.5) * mm, "end": v(32.31, 18.46) * mm});
            skLineSegment(sketch, "E2920", {"start": v(32.31, 18.46) * mm, "end": v(32.3, 18.42) * mm});
            skLineSegment(sketch, "E2921", {"start": v(32.3, 18.42) * mm, "end": v(32.28, 18.38) * mm});
            skLineSegment(sketch, "E2922", {"start": v(32.28, 18.38) * mm, "end": v(32.27, 18.35) * mm});
            skLineSegment(sketch, "E2923", {"start": v(32.27, 18.35) * mm, "end": v(32.25, 18.31) * mm});
            skLineSegment(sketch, "E2924", {"start": v(32.25, 18.31) * mm, "end": v(32.23, 18.28) * mm});
            skLineSegment(sketch, "E2925", {"start": v(32.23, 18.28) * mm, "end": v(32.22, 18.24) * mm});
            skLineSegment(sketch, "E2926", {"start": v(32.22, 18.24) * mm, "end": v(32.2, 18.2) * mm});
            skLineSegment(sketch, "E2927", {"start": v(32.2, 18.2) * mm, "end": v(32.19, 18.17) * mm});
            skLineSegment(sketch, "E2928", {"start": v(32.19, 18.17) * mm, "end": v(32.17, 18.14) * mm});
            skLineSegment(sketch, "E2929", {"start": v(32.17, 18.14) * mm, "end": v(32.16, 18.1) * mm});
            skLineSegment(sketch, "E2930", {"start": v(32.16, 18.1) * mm, "end": v(32.14, 18.07) * mm});
            skLineSegment(sketch, "E2931", {"start": v(32.14, 18.07) * mm, "end": v(32.13, 18.04) * mm});
            skLineSegment(sketch, "E2932", {"start": v(32.13, 18.04) * mm, "end": v(32.12, 18) * mm});
            skLineSegment(sketch, "E2933", {"start": v(32.12, 18) * mm, "end": v(32.1, 17.98) * mm});
            skLineSegment(sketch, "E2934", {"start": v(32.1, 17.98) * mm, "end": v(32.09, 17.94) * mm});
            skLineSegment(sketch, "E2935", {"start": v(32.09, 17.94) * mm, "end": v(32.07, 17.91) * mm});
            skLineSegment(sketch, "E2936", {"start": v(32.07, 17.91) * mm, "end": v(32.06, 17.88) * mm});
            skLineSegment(sketch, "E2937", {"start": v(32.06, 17.88) * mm, "end": v(32.05, 17.85) * mm});
            skLineSegment(sketch, "E2938", {"start": v(32.05, 17.85) * mm, "end": v(32.03, 17.82) * mm});
            skLineSegment(sketch, "E2939", {"start": v(32.03, 17.82) * mm, "end": v(32.02, 17.79) * mm});
            skLineSegment(sketch, "E2940", {"start": v(32.02, 17.79) * mm, "end": v(32, 17.76) * mm});
            skLineSegment(sketch, "E2941", {"start": v(32, 17.76) * mm, "end": v(32, 17.73) * mm});
            skLineSegment(sketch, "E2942", {"start": v(32, 17.73) * mm, "end": v(31.98, 17.7) * mm});
            skLineSegment(sketch, "E2943", {"start": v(31.98, 17.7) * mm, "end": v(31.97, 17.67) * mm});
            skLineSegment(sketch, "E2944", {"start": v(31.97, 17.67) * mm, "end": v(31.95, 17.64) * mm});
            skLineSegment(sketch, "E2945", {"start": v(31.95, 17.64) * mm, "end": v(31.94, 17.61) * mm});
            skLineSegment(sketch, "E2946", {"start": v(31.94, 17.61) * mm, "end": v(31.93, 17.59) * mm});
            skLineSegment(sketch, "E2947", {"start": v(31.93, 17.59) * mm, "end": v(31.78, 17.23) * mm});
            skLineSegment(sketch, "E2948", {"start": v(31.78, 17.23) * mm, "end": v(31.62, 16.87) * mm});
            skLineSegment(sketch, "E2949", {"start": v(31.62, 16.87) * mm, "end": v(31.47, 16.5) * mm});
            skLineSegment(sketch, "E2950", {"start": v(31.47, 16.5) * mm, "end": v(31.32, 16.15) * mm});
            skLineSegment(sketch, "E2951", {"start": v(31.32, 16.15) * mm, "end": v(31.16, 15.78) * mm});
            skLineSegment(sketch, "E2952", {"start": v(31.16, 15.78) * mm, "end": v(31.01, 15.42) * mm});
            skLineSegment(sketch, "E2953", {"start": v(31.01, 15.42) * mm, "end": v(30.86, 15.06) * mm});
            skLineSegment(sketch, "E2954", {"start": v(30.86, 15.06) * mm, "end": v(30.7, 14.7) * mm});
            skLineSegment(sketch, "E2955", {"start": v(30.7, 14.7) * mm, "end": v(30.55, 14.34) * mm});
            skLineSegment(sketch, "E2956", {"start": v(30.55, 14.34) * mm, "end": v(30.4, 13.98) * mm});
            skLineSegment(sketch, "E2957", {"start": v(30.4, 13.98) * mm, "end": v(30.25, 13.62) * mm});
            skLineSegment(sketch, "E2958", {"start": v(30.25, 13.62) * mm, "end": v(30.1, 13.26) * mm});
            skLineSegment(sketch, "E2959", {"start": v(30.1, 13.26) * mm, "end": v(29.94, 12.9) * mm});
            skLineSegment(sketch, "E2960", {"start": v(29.94, 12.9) * mm, "end": v(29.79, 12.54) * mm});
            skLineSegment(sketch, "E2961", {"start": v(29.79, 12.54) * mm, "end": v(29.63, 12.18) * mm});
            skLineSegment(sketch, "E2962", {"start": v(29.63, 12.18) * mm, "end": v(29.48, 11.82) * mm});
            skLineSegment(sketch, "E2963", {"start": v(29.48, 11.82) * mm, "end": v(29.33, 11.46) * mm});
            skLineSegment(sketch, "E2964", {"start": v(29.33, 11.46) * mm, "end": v(29.17, 11.1) * mm});
            skLineSegment(sketch, "E2965", {"start": v(29.17, 11.1) * mm, "end": v(29.02, 10.74) * mm});
            skLineSegment(sketch, "E2966", {"start": v(29.02, 10.74) * mm, "end": v(28.87, 10.38) * mm});
            skLineSegment(sketch, "E2967", {"start": v(28.87, 10.38) * mm, "end": v(28.72, 10.02) * mm});
            skLineSegment(sketch, "E2968", {"start": v(28.72, 10.02) * mm, "end": v(28.56, 9.66) * mm});
            skLineSegment(sketch, "E2969", {"start": v(28.56, 9.66) * mm, "end": v(28.41, 9.3) * mm});
            skLineSegment(sketch, "E2970", {"start": v(28.41, 9.3) * mm, "end": v(28.26, 8.94) * mm});
            skLineSegment(sketch, "E2971", {"start": v(28.26, 8.94) * mm, "end": v(28.1, 8.58) * mm});
            skLineSegment(sketch, "E2972", {"start": v(28.1, 8.58) * mm, "end": v(27.95, 8.22) * mm});
            skLineSegment(sketch, "E2973", {"start": v(27.95, 8.22) * mm, "end": v(27.8, 7.86) * mm});
            skLineSegment(sketch, "E2974", {"start": v(27.8, 7.86) * mm, "end": v(27.65, 7.5) * mm});
            skLineSegment(sketch, "E2975", {"start": v(27.65, 7.5) * mm, "end": v(27.5, 7.13) * mm});
            skLineSegment(sketch, "E2976", {"start": v(27.5, 7.13) * mm, "end": v(27.34, 6.77) * mm});
            skLineSegment(sketch, "E2977", {"start": v(27.34, 6.77) * mm, "end": v(27.19, 6.41) * mm});
            skLineSegment(sketch, "E2978", {"start": v(27.19, 6.41) * mm, "end": v(27.03, 6.05) * mm});
            skLineSegment(sketch, "E2979", {"start": v(27.03, 6.05) * mm, "end": v(26.88, 5.7) * mm});
            skLineSegment(sketch, "E2980", {"start": v(26.88, 5.7) * mm, "end": v(26.73, 5.33) * mm});
            skLineSegment(sketch, "E2981", {"start": v(26.73, 5.33) * mm, "end": v(26.57, 4.97) * mm});
            skLineSegment(sketch, "E2982", {"start": v(26.57, 4.97) * mm, "end": v(26.42, 4.61) * mm});
            skLineSegment(sketch, "E2983", {"start": v(26.42, 4.61) * mm, "end": v(26.27, 4.25) * mm});
            skLineSegment(sketch, "E2984", {"start": v(26.27, 4.25) * mm, "end": v(26.12, 3.9) * mm});
            skLineSegment(sketch, "E2985", {"start": v(26.12, 3.9) * mm, "end": v(25.96, 3.53) * mm});
            skLineSegment(sketch, "E2986", {"start": v(25.96, 3.53) * mm, "end": v(25.8, 3.17) * mm});
            skLineSegment(sketch, "E2987", {"start": v(25.8, 3.17) * mm, "end": v(25.66, 2.8) * mm});
            skLineSegment(sketch, "E2988", {"start": v(25.66, 2.8) * mm, "end": v(25.5, 2.45) * mm});
            skLineSegment(sketch, "E2989", {"start": v(25.5, 2.45) * mm, "end": v(25.35, 2.09) * mm});
            skLineSegment(sketch, "E2990", {"start": v(25.35, 2.09) * mm, "end": v(25.2, 1.73) * mm});
            skLineSegment(sketch, "E2991", {"start": v(25.2, 1.73) * mm, "end": v(25.04, 1.37) * mm});
            skLineSegment(sketch, "E2992", {"start": v(25.04, 1.37) * mm, "end": v(24.9, 1) * mm});
            skLineSegment(sketch, "E2993", {"start": v(24.9, 1) * mm, "end": v(24.74, 0.65) * mm});
            skLineSegment(sketch, "E2994", {"start": v(24.74, 0.65) * mm, "end": v(24.59, 0.29) * mm});
            skLineSegment(sketch, "E2995", {"start": v(24.59, 0.29) * mm, "end": v(24.43, -0.07) * mm});
            skLineSegment(sketch, "E2996", {"start": v(24.43, -0.07) * mm, "end": v(24.28, -0.43) * mm});
            skLineSegment(sketch, "E2997", {"start": v(24.28, -0.43) * mm, "end": v(24.13, -0.8) * mm});
            skLineSegment(sketch, "E2998", {"start": v(24.13, -0.8) * mm, "end": v(23.97, -1.16) * mm});
            skLineSegment(sketch, "E2999", {"start": v(23.97, -1.16) * mm, "end": v(23.82, -1.52) * mm});
            skLineSegment(sketch, "E3000", {"start": v(23.82, -1.52) * mm, "end": v(23.67, -1.88) * mm});
            skLineSegment(sketch, "E3001", {"start": v(23.67, -1.88) * mm, "end": v(23.51, -2.24) * mm});
            skLineSegment(sketch, "E3002", {"start": v(23.51, -2.24) * mm, "end": v(23.36, -2.6) * mm});
            skLineSegment(sketch, "E3003", {"start": v(23.36, -2.6) * mm, "end": v(23.2, -2.96) * mm});
            skLineSegment(sketch, "E3004", {"start": v(23.2, -2.96) * mm, "end": v(23.06, -3.32) * mm});
            skLineSegment(sketch, "E3005", {"start": v(23.06, -3.32) * mm, "end": v(22.9, -3.68) * mm});
            skLineSegment(sketch, "E3006", {"start": v(22.9, -3.68) * mm, "end": v(22.75, -4.04) * mm});
            skLineSegment(sketch, "E3007", {"start": v(22.75, -4.04) * mm, "end": v(22.6, -4.4) * mm});
            skLineSegment(sketch, "E3008", {"start": v(22.6, -4.4) * mm, "end": v(22.44, -4.76) * mm});
            skLineSegment(sketch, "E3009", {"start": v(22.44, -4.76) * mm, "end": v(22.3, -5.12) * mm});
            skLineSegment(sketch, "E3010", {"start": v(22.3, -5.12) * mm, "end": v(22.14, -5.48) * mm});
            skLineSegment(sketch, "E3011", {"start": v(22.14, -5.48) * mm, "end": v(21.99, -5.84) * mm});
            skLineSegment(sketch, "E3012", {"start": v(21.99, -5.84) * mm, "end": v(21.83, -6.2) * mm});
            skLineSegment(sketch, "E3013", {"start": v(21.83, -6.2) * mm, "end": v(21.68, -6.56) * mm});
            skLineSegment(sketch, "E3014", {"start": v(21.68, -6.56) * mm, "end": v(21.53, -6.92) * mm});
            skLineSegment(sketch, "E3015", {"start": v(21.53, -6.92) * mm, "end": v(21.37, -7.28) * mm});
            skLineSegment(sketch, "E3016", {"start": v(21.37, -7.28) * mm, "end": v(21.22, -7.64) * mm});
            skLineSegment(sketch, "E3017", {"start": v(21.22, -7.64) * mm, "end": v(21.07, -8) * mm});
            skLineSegment(sketch, "E3018", {"start": v(21.07, -8) * mm, "end": v(20.91, -8.36) * mm});
            skLineSegment(sketch, "E3019", {"start": v(20.91, -8.36) * mm, "end": v(20.76, -8.72) * mm});
            skLineSegment(sketch, "E3020", {"start": v(20.76, -8.72) * mm, "end": v(20.6, -9.08) * mm});
            skLineSegment(sketch, "E3021", {"start": v(20.6, -9.08) * mm, "end": v(20.46, -9.45) * mm});
            skLineSegment(sketch, "E3022", {"start": v(20.46, -9.45) * mm, "end": v(20.3, -9.8) * mm});
            skLineSegment(sketch, "E3023", {"start": v(20.3, -9.8) * mm, "end": v(20.15, -10.17) * mm});
            skLineSegment(sketch, "E3024", {"start": v(20.15, -10.17) * mm, "end": v(20, -10.53) * mm});
            skLineSegment(sketch, "E3025", {"start": v(20, -10.53) * mm, "end": v(19.84, -10.89) * mm});
            skLineSegment(sketch, "E3026", {"start": v(19.84, -10.89) * mm, "end": v(19.7, -11.25) * mm});
            skLineSegment(sketch, "E3027", {"start": v(19.7, -11.25) * mm, "end": v(19.54, -11.6) * mm});
            skLineSegment(sketch, "E3028", {"start": v(19.54, -11.6) * mm, "end": v(19.38, -11.97) * mm});
            skLineSegment(sketch, "E3029", {"start": v(19.38, -11.97) * mm, "end": v(19.23, -12.33) * mm});
            skLineSegment(sketch, "E3030", {"start": v(19.23, -12.33) * mm, "end": v(19.08, -12.69) * mm});
            skLineSegment(sketch, "E3031", {"start": v(19.08, -12.69) * mm, "end": v(18.93, -13.05) * mm});
            skLineSegment(sketch, "E3032", {"start": v(18.93, -13.05) * mm, "end": v(18.77, -13.41) * mm});
            skLineSegment(sketch, "E3033", {"start": v(18.77, -13.41) * mm, "end": v(18.62, -13.77) * mm});
            skLineSegment(sketch, "E3034", {"start": v(18.62, -13.77) * mm, "end": v(18.47, -14.13) * mm});
            skLineSegment(sketch, "E3035", {"start": v(18.47, -14.13) * mm, "end": v(18.31, -14.5) * mm});
            skLineSegment(sketch, "E3036", {"start": v(18.31, -14.5) * mm, "end": v(18.16, -14.85) * mm});
            skLineSegment(sketch, "E3037", {"start": v(18.16, -14.85) * mm, "end": v(18, -15.21) * mm});
            skLineSegment(sketch, "E3038", {"start": v(18, -15.21) * mm, "end": v(17.86, -15.57) * mm});
            skLineSegment(sketch, "E3039", {"start": v(17.86, -15.57) * mm, "end": v(17.7, -15.93) * mm});
            skLineSegment(sketch, "E3040", {"start": v(17.7, -15.93) * mm, "end": v(17.55, -16.3) * mm});
            skLineSegment(sketch, "E3041", {"start": v(17.55, -16.3) * mm, "end": v(17.4, -16.65) * mm});
            skLineSegment(sketch, "E3042", {"start": v(17.4, -16.65) * mm, "end": v(17.24, -17.01) * mm});
            skLineSegment(sketch, "E3043", {"start": v(17.24, -17.01) * mm, "end": v(17.1, -17.37) * mm});
            skLineSegment(sketch, "E3044", {"start": v(17.1, -17.37) * mm, "end": v(16.94, -17.74) * mm});
            skLineSegment(sketch, "E3045", {"start": v(16.94, -17.74) * mm, "end": v(16.78, -18.1) * mm});
            skLineSegment(sketch, "E3046", {"start": v(16.78, -18.1) * mm, "end": v(16.63, -18.46) * mm});
            skLineSegment(sketch, "E3047", {"start": v(16.63, -18.46) * mm, "end": v(16.48, -18.82) * mm});
            skLineSegment(sketch, "E3048", {"start": v(16.48, -18.82) * mm, "end": v(16.33, -19.18) * mm});
            skLineSegment(sketch, "E3049", {"start": v(16.33, -19.18) * mm, "end": v(16.17, -19.54) * mm});
            skLineSegment(sketch, "E3050", {"start": v(16.17, -19.54) * mm, "end": v(16.02, -19.9) * mm});
            skLineSegment(sketch, "E3051", {"start": v(16.02, -19.9) * mm, "end": v(15.87, -20.26) * mm});
            skLineSegment(sketch, "E3052", {"start": v(15.87, -20.26) * mm, "end": v(15.71, -20.62) * mm});
            skLineSegment(sketch, "E3053", {"start": v(15.71, -20.62) * mm, "end": v(15.56, -20.98) * mm});
            skLineSegment(sketch, "E3054", {"start": v(15.56, -20.98) * mm, "end": v(15.4, -21.34) * mm});
            skLineSegment(sketch, "E3055", {"start": v(15.4, -21.34) * mm, "end": v(15.25, -21.7) * mm});
            skLineSegment(sketch, "E3056", {"start": v(15.25, -21.7) * mm, "end": v(15.1, -22.06) * mm});
            skLineSegment(sketch, "E3057", {"start": v(15.1, -22.06) * mm, "end": v(14.95, -22.42) * mm});
            skLineSegment(sketch, "E3058", {"start": v(14.95, -22.42) * mm, "end": v(14.8, -22.78) * mm});
            skLineSegment(sketch, "E3059", {"start": v(14.8, -22.78) * mm, "end": v(14.64, -23.14) * mm});
            skLineSegment(sketch, "E3060", {"start": v(14.64, -23.14) * mm, "end": v(14.49, -23.5) * mm});
            skLineSegment(sketch, "E3061", {"start": v(14.49, -23.5) * mm, "end": v(14.34, -23.86) * mm});
            skLineSegment(sketch, "E3062", {"start": v(14.34, -23.86) * mm, "end": v(14.18, -24.22) * mm});
            skLineSegment(sketch, "E3063", {"start": v(14.18, -24.22) * mm, "end": v(14.03, -24.58) * mm});
            skLineSegment(sketch, "E3064", {"start": v(14.03, -24.58) * mm, "end": v(13.88, -24.94) * mm});
            skLineSegment(sketch, "E3065", {"start": v(13.88, -24.94) * mm, "end": v(13.72, -25.3) * mm});
            skLineSegment(sketch, "E3066", {"start": v(13.72, -25.3) * mm, "end": v(13.57, -25.66) * mm});
            skLineSegment(sketch, "E3067", {"start": v(13.57, -25.66) * mm, "end": v(13.42, -26.03) * mm});
            skLineSegment(sketch, "E3068", {"start": v(13.42, -26.03) * mm, "end": v(13.27, -26.39) * mm});
            skLineSegment(sketch, "E3069", {"start": v(13.27, -26.39) * mm, "end": v(13.11, -26.75) * mm});
            skLineSegment(sketch, "E3070", {"start": v(13.11, -26.75) * mm, "end": v(12.96, -27.1) * mm});
            skLineSegment(sketch, "E3071", {"start": v(12.96, -27.1) * mm, "end": v(12.8, -27.47) * mm});
            skLineSegment(sketch, "E3072", {"start": v(12.8, -27.47) * mm, "end": v(12.65, -27.83) * mm});
            skLineSegment(sketch, "E3073", {"start": v(12.65, -27.83) * mm, "end": v(12.5, -28.19) * mm});
            skLineSegment(sketch, "E3074", {"start": v(12.5, -28.19) * mm, "end": v(12.35, -28.55) * mm});
            skLineSegment(sketch, "E3075", {"start": v(12.35, -28.55) * mm, "end": v(12.27, -28.75) * mm});
            skLineSegment(sketch, "E3076", {"start": v(12.27, -28.75) * mm, "end": v(12.2, -28.94) * mm});
            skLineSegment(sketch, "E3077", {"start": v(12.2, -28.94) * mm, "end": v(12.14, -29.13) * mm});
            skLineSegment(sketch, "E3078", {"start": v(12.14, -29.13) * mm, "end": v(12.08, -29.32) * mm});
            skLineSegment(sketch, "E3079", {"start": v(12.08, -29.32) * mm, "end": v(12.02, -29.51) * mm});
            skLineSegment(sketch, "E3080", {"start": v(12.02, -29.51) * mm, "end": v(11.96, -29.7) * mm});
            skLineSegment(sketch, "E3081", {"start": v(11.96, -29.7) * mm, "end": v(11.91, -29.88) * mm});
            skLineSegment(sketch, "E3082", {"start": v(11.91, -29.88) * mm, "end": v(11.86, -30.06) * mm});
            skLineSegment(sketch, "E3083", {"start": v(11.86, -30.06) * mm, "end": v(11.82, -30.23) * mm});
            skLineSegment(sketch, "E3084", {"start": v(11.82, -30.23) * mm, "end": v(11.78, -30.4) * mm});
            skLineSegment(sketch, "E3085", {"start": v(11.78, -30.4) * mm, "end": v(11.74, -30.58) * mm});
            skLineSegment(sketch, "E3086", {"start": v(11.74, -30.58) * mm, "end": v(11.7, -30.75) * mm});
            skLineSegment(sketch, "E3087", {"start": v(11.7, -30.75) * mm, "end": v(11.68, -30.92) * mm});
            skLineSegment(sketch, "E3088", {"start": v(11.68, -30.92) * mm, "end": v(11.65, -31.08) * mm});
            skLineSegment(sketch, "E3089", {"start": v(11.65, -31.08) * mm, "end": v(11.62, -31.24) * mm});
            skLineSegment(sketch, "E3090", {"start": v(11.62, -31.24) * mm, "end": v(11.6, -31.4) * mm});
            skLineSegment(sketch, "E3091", {"start": v(11.6, -31.4) * mm, "end": v(11.58, -31.56) * mm});
            skLineSegment(sketch, "E3092", {"start": v(11.58, -31.56) * mm, "end": v(11.57, -31.71) * mm});
            skLineSegment(sketch, "E3093", {"start": v(11.57, -31.71) * mm, "end": v(11.56, -31.86) * mm});
            skLineSegment(sketch, "E3094", {"start": v(11.56, -31.86) * mm, "end": v(11.55, -32.01) * mm});
            skLineSegment(sketch, "E3095", {"start": v(11.55, -32.01) * mm, "end": v(11.54, -32.16) * mm});
            skLineSegment(sketch, "E3096", {"start": v(11.54, -32.16) * mm, "end": v(11.54, -32.3) * mm});
            skLineSegment(sketch, "E3097", {"start": v(11.54, -32.3) * mm, "end": v(11.54, -32.45) * mm});
            skLineSegment(sketch, "E3098", {"start": v(11.54, -32.45) * mm, "end": v(11.54, -32.59) * mm});
            skLineSegment(sketch, "E3099", {"start": v(11.54, -32.59) * mm, "end": v(11.55, -32.73) * mm});
            skLineSegment(sketch, "E3100", {"start": v(11.55, -32.73) * mm, "end": v(11.56, -32.86) * mm});
            skLineSegment(sketch, "E3101", {"start": v(11.56, -32.86) * mm, "end": v(11.57, -33) * mm});
            skLineSegment(sketch, "E3102", {"start": v(11.57, -33) * mm, "end": v(11.59, -33.13) * mm});
            skLineSegment(sketch, "E3103", {"start": v(11.59, -33.13) * mm, "end": v(11.6, -33.26) * mm});
            skLineSegment(sketch, "E3104", {"start": v(11.6, -33.26) * mm, "end": v(11.62, -33.38) * mm});
            skLineSegment(sketch, "E3105", {"start": v(11.62, -33.38) * mm, "end": v(11.64, -33.5) * mm});
            skLineSegment(sketch, "E3106", {"start": v(11.64, -33.5) * mm, "end": v(11.67, -33.63) * mm});
            skLineSegment(sketch, "E3107", {"start": v(11.67, -33.63) * mm, "end": v(11.7, -33.75) * mm});
            skLineSegment(sketch, "E3108", {"start": v(11.7, -33.75) * mm, "end": v(11.73, -33.87) * mm});
            skLineSegment(sketch, "E3109", {"start": v(11.73, -33.87) * mm, "end": v(11.76, -33.98) * mm});
            skLineSegment(sketch, "E3110", {"start": v(11.76, -33.98) * mm, "end": v(11.8, -34.1) * mm});
            skLineSegment(sketch, "E3111", {"start": v(11.8, -34.1) * mm, "end": v(11.83, -34.2) * mm});
            skLineSegment(sketch, "E3112", {"start": v(11.83, -34.2) * mm, "end": v(11.87, -34.32) * mm});
            skLineSegment(sketch, "E3113", {"start": v(11.87, -34.32) * mm, "end": v(11.92, -34.43) * mm});
            skLineSegment(sketch, "E3114", {"start": v(11.92, -34.43) * mm, "end": v(11.96, -34.53) * mm});
            skLineSegment(sketch, "E3115", {"start": v(11.96, -34.53) * mm, "end": v(12, -34.64) * mm});
            skLineSegment(sketch, "E3116", {"start": v(12, -34.64) * mm, "end": v(12.06, -34.74) * mm});
            skLineSegment(sketch, "E3117", {"start": v(12.06, -34.74) * mm, "end": v(12.11, -34.84) * mm});
            skLineSegment(sketch, "E3118", {"start": v(12.11, -34.84) * mm, "end": v(12.16, -34.94) * mm});
            skLineSegment(sketch, "E3119", {"start": v(12.16, -34.94) * mm, "end": v(12.22, -35.03) * mm});
            skLineSegment(sketch, "E3120", {"start": v(12.22, -35.03) * mm, "end": v(12.28, -35.13) * mm});
            skLineSegment(sketch, "E3121", {"start": v(12.28, -35.13) * mm, "end": v(12.34, -35.22) * mm});
            skLineSegment(sketch, "E3122", {"start": v(12.34, -35.22) * mm, "end": v(12.4, -35.3) * mm});
            skLineSegment(sketch, "E3123", {"start": v(12.4, -35.3) * mm, "end": v(12.46, -35.4) * mm});
            skLineSegment(sketch, "E3124", {"start": v(12.46, -35.4) * mm, "end": v(12.53, -35.49) * mm});
            skLineSegment(sketch, "E3125", {"start": v(12.53, -35.49) * mm, "end": v(12.6, -35.57) * mm});
            skLineSegment(sketch, "E3126", {"start": v(12.6, -35.57) * mm, "end": v(12.67, -35.65) * mm});
            skLineSegment(sketch, "E3127", {"start": v(12.67, -35.65) * mm, "end": v(12.74, -35.73) * mm});
            skLineSegment(sketch, "E3128", {"start": v(12.74, -35.73) * mm, "end": v(12.82, -35.81) * mm});
            skLineSegment(sketch, "E3129", {"start": v(12.82, -35.81) * mm, "end": v(12.9, -35.9) * mm});
            skLineSegment(sketch, "E3130", {"start": v(12.9, -35.9) * mm, "end": v(12.97, -35.97) * mm});
            skLineSegment(sketch, "E3131", {"start": v(12.97, -35.97) * mm, "end": v(13.05, -36.04) * mm});
            skLineSegment(sketch, "E3132", {"start": v(13.05, -36.04) * mm, "end": v(13.13, -36.12) * mm});
            skLineSegment(sketch, "E3133", {"start": v(13.13, -36.12) * mm, "end": v(13.21, -36.19) * mm});
            skLineSegment(sketch, "E3134", {"start": v(13.21, -36.19) * mm, "end": v(13.3, -36.26) * mm});
            skLineSegment(sketch, "E3135", {"start": v(13.3, -36.26) * mm, "end": v(13.38, -36.32) * mm});
            skLineSegment(sketch, "E3136", {"start": v(13.38, -36.32) * mm, "end": v(13.47, -36.39) * mm});
            skLineSegment(sketch, "E3137", {"start": v(13.47, -36.39) * mm, "end": v(13.55, -36.45) * mm});
            skLineSegment(sketch, "E3138", {"start": v(13.55, -36.45) * mm, "end": v(13.64, -36.52) * mm});
            skLineSegment(sketch, "E3139", {"start": v(13.64, -36.52) * mm, "end": v(13.74, -36.58) * mm});
            skLineSegment(sketch, "E3140", {"start": v(13.74, -36.58) * mm, "end": v(13.83, -36.64) * mm});
            skLineSegment(sketch, "E3141", {"start": v(13.83, -36.64) * mm, "end": v(13.92, -36.7) * mm});
            skLineSegment(sketch, "E3142", {"start": v(13.92, -36.7) * mm, "end": v(14.02, -36.75) * mm});
            skLineSegment(sketch, "E3143", {"start": v(14.02, -36.75) * mm, "end": v(14.12, -36.8) * mm});
            skLineSegment(sketch, "E3144", {"start": v(14.12, -36.8) * mm, "end": v(14.21, -36.86) * mm});
            skLineSegment(sketch, "E3145", {"start": v(14.21, -36.86) * mm, "end": v(14.31, -36.92) * mm});
            skLineSegment(sketch, "E3146", {"start": v(14.31, -36.92) * mm, "end": v(14.41, -36.97) * mm});
            skLineSegment(sketch, "E3147", {"start": v(14.41, -36.97) * mm, "end": v(14.51, -37.02) * mm});
            skLineSegment(sketch, "E3148", {"start": v(14.51, -37.02) * mm, "end": v(14.62, -37.06) * mm});
            skLineSegment(sketch, "E3149", {"start": v(14.62, -37.06) * mm, "end": v(14.72, -37.11) * mm});
            skLineSegment(sketch, "E3150", {"start": v(14.72, -37.11) * mm, "end": v(14.82, -37.16) * mm});
            skLineSegment(sketch, "E3151", {"start": v(14.82, -37.16) * mm, "end": v(14.93, -37.2) * mm});
            skLineSegment(sketch, "E3152", {"start": v(14.93, -37.2) * mm, "end": v(15.04, -37.24) * mm});
            skLineSegment(sketch, "E3153", {"start": v(15.04, -37.24) * mm, "end": v(15.14, -37.29) * mm});
            skLineSegment(sketch, "E3154", {"start": v(15.14, -37.29) * mm, "end": v(15.25, -37.33) * mm});
            skLineSegment(sketch, "E3155", {"start": v(15.25, -37.33) * mm, "end": v(15.36, -37.37) * mm});
            skLineSegment(sketch, "E3156", {"start": v(15.36, -37.37) * mm, "end": v(15.47, -37.4) * mm});
            skLineSegment(sketch, "E3157", {"start": v(15.47, -37.4) * mm, "end": v(15.58, -37.44) * mm});
            skLineSegment(sketch, "E3158", {"start": v(15.58, -37.44) * mm, "end": v(15.7, -37.47) * mm});
            skLineSegment(sketch, "E3159", {"start": v(15.7, -37.47) * mm, "end": v(15.8, -37.5) * mm});
            skLineSegment(sketch, "E3160", {"start": v(15.8, -37.5) * mm, "end": v(15.92, -37.54) * mm});
            skLineSegment(sketch, "E3161", {"start": v(15.92, -37.54) * mm, "end": v(16.03, -37.57) * mm});
            skLineSegment(sketch, "E3162", {"start": v(16.03, -37.57) * mm, "end": v(16.15, -37.6) * mm});
            skLineSegment(sketch, "E3163", {"start": v(16.15, -37.6) * mm, "end": v(16.26, -37.63) * mm});
            skLineSegment(sketch, "E3164", {"start": v(16.26, -37.63) * mm, "end": v(16.38, -37.66) * mm});
            skLineSegment(sketch, "E3165", {"start": v(16.38, -37.66) * mm, "end": v(16.5, -37.69) * mm});
            skLineSegment(sketch, "E3166", {"start": v(16.5, -37.69) * mm, "end": v(16.6, -37.72) * mm});
            skLineSegment(sketch, "E3167", {"start": v(16.6, -37.72) * mm, "end": v(16.72, -37.74) * mm});
            skLineSegment(sketch, "E3168", {"start": v(16.72, -37.74) * mm, "end": v(16.84, -37.77) * mm});
            skLineSegment(sketch, "E3169", {"start": v(16.84, -37.77) * mm, "end": v(16.96, -37.79) * mm});
            skLineSegment(sketch, "E3170", {"start": v(16.96, -37.79) * mm, "end": v(17.07, -37.81) * mm});
            skLineSegment(sketch, "E3171", {"start": v(17.07, -37.81) * mm, "end": v(17.2, -37.83) * mm});
            skLineSegment(sketch, "E3172", {"start": v(17.2, -37.83) * mm, "end": v(17.3, -37.85) * mm});
            skLineSegment(sketch, "E3173", {"start": v(17.3, -37.85) * mm, "end": v(17.43, -37.87) * mm});
            skLineSegment(sketch, "E3174", {"start": v(17.43, -37.87) * mm, "end": v(17.55, -37.9) * mm});
            skLineSegment(sketch, "E3175", {"start": v(17.55, -37.9) * mm, "end": v(17.66, -37.9) * mm});
            skLineSegment(sketch, "E3176", {"start": v(17.66, -37.9) * mm, "end": v(17.78, -37.92) * mm});
            skLineSegment(sketch, "E3177", {"start": v(17.78, -37.92) * mm, "end": v(17.9, -37.94) * mm});
            skLineSegment(sketch, "E3178", {"start": v(17.9, -37.94) * mm, "end": v(18.02, -37.96) * mm});
            skLineSegment(sketch, "E3179", {"start": v(18.02, -37.96) * mm, "end": v(18.14, -37.97) * mm});
            skLineSegment(sketch, "E3180", {"start": v(18.14, -37.97) * mm, "end": v(18.26, -37.98) * mm});
            skLineSegment(sketch, "E3181", {"start": v(18.26, -37.98) * mm, "end": v(18.37, -38) * mm});
            skLineSegment(sketch, "E3182", {"start": v(18.37, -38) * mm, "end": v(18.5, -38) * mm});
            skLineSegment(sketch, "E3183", {"start": v(18.5, -38) * mm, "end": v(18.6, -38.02) * mm});
            skLineSegment(sketch, "E3184", {"start": v(18.6, -38.02) * mm, "end": v(18.73, -38.03) * mm});
            skLineSegment(sketch, "E3185", {"start": v(18.73, -38.03) * mm, "end": v(18.84, -38.04) * mm});
            skLineSegment(sketch, "E3186", {"start": v(18.84, -38.04) * mm, "end": v(18.96, -38.05) * mm});
            skLineSegment(sketch, "E3187", {"start": v(18.96, -38.05) * mm, "end": v(19.08, -38.06) * mm});
            skLineSegment(sketch, "E3188", {"start": v(19.08, -38.06) * mm, "end": v(19.2, -38.06) * mm});
            skLineSegment(sketch, "E3189", {"start": v(19.2, -38.06) * mm, "end": v(19.3, -38.07) * mm});
            skLineSegment(sketch, "E3190", {"start": v(19.3, -38.07) * mm, "end": v(19.42, -38.08) * mm});
            skLineSegment(sketch, "E3191", {"start": v(19.42, -38.08) * mm, "end": v(19.54, -38.08) * mm});
            skLineSegment(sketch, "E3192", {"start": v(19.54, -38.08) * mm, "end": v(19.65, -38.09) * mm});
            skLineSegment(sketch, "E3193", {"start": v(19.65, -38.09) * mm, "end": v(19.77, -38.1) * mm});
            skLineSegment(sketch, "E3194", {"start": v(19.77, -38.1) * mm, "end": v(19.88, -38.1) * mm});
            skLineSegment(sketch, "E3195", {"start": v(19.88, -38.1) * mm, "end": v(20, -38.1) * mm});
            skLineSegment(sketch, "E3196", {"start": v(20, -38.1) * mm, "end": v(20.1, -38.1) * mm});
            skLineSegment(sketch, "E3197", {"start": v(20.1, -38.1) * mm, "end": v(20.22, -38.1) * mm});
            skLineSegment(sketch, "E3198", {"start": v(20.22, -38.1) * mm, "end": v(20.33, -38.1) * mm});
            skLineSegment(sketch, "E3199", {"start": v(20.33, -38.1) * mm, "end": v(20.44, -38.1) * mm});
            skLineSegment(sketch, "E3200", {"start": v(20.44, -38.1) * mm, "end": v(20.55, -38.1) * mm});
            skLineSegment(sketch, "E3201", {"start": v(20.55, -38.1) * mm, "end": v(20.65, -38.1) * mm});
            skLineSegment(sketch, "E3202", {"start": v(20.65, -38.1) * mm, "end": v(20.76, -38.1) * mm});
            skLineSegment(sketch, "E3203", {"start": v(20.76, -38.1) * mm, "end": v(20.88, -38.1) * mm});
            skLineSegment(sketch, "E3204", {"start": v(20.88, -38.1) * mm, "end": v(21, -38.1) * mm});
            skLineSegment(sketch, "E3205", {"start": v(21, -38.1) * mm, "end": v(21.13, -38.1) * mm});
            skLineSegment(sketch, "E3206", {"start": v(21.13, -38.1) * mm, "end": v(21.25, -38.1) * mm});
            skLineSegment(sketch, "E3207", {"start": v(21.25, -38.1) * mm, "end": v(21.37, -38.1) * mm});
            skLineSegment(sketch, "E3208", {"start": v(21.37, -38.1) * mm, "end": v(21.49, -38.1) * mm});
            skLineSegment(sketch, "E3209", {"start": v(21.49, -38.1) * mm, "end": v(21.6, -38.1) * mm});
            skLineSegment(sketch, "E3210", {"start": v(21.6, -38.1) * mm, "end": v(21.73, -38.1) * mm});
            skLineSegment(sketch, "E3211", {"start": v(21.73, -38.1) * mm, "end": v(21.84, -38.09) * mm});
            skLineSegment(sketch, "E3212", {"start": v(21.84, -38.09) * mm, "end": v(21.96, -38.08) * mm});
            skLineSegment(sketch, "E3213", {"start": v(21.96, -38.08) * mm, "end": v(22.08, -38.08) * mm});
            skLineSegment(sketch, "E3214", {"start": v(22.08, -38.08) * mm, "end": v(22.2, -38.07) * mm});
            skLineSegment(sketch, "E3215", {"start": v(22.2, -38.07) * mm, "end": v(22.32, -38.06) * mm});
            skLineSegment(sketch, "E3216", {"start": v(22.32, -38.06) * mm, "end": v(22.43, -38.05) * mm});
            skLineSegment(sketch, "E3217", {"start": v(22.43, -38.05) * mm, "end": v(22.55, -38.05) * mm});
            skLineSegment(sketch, "E3218", {"start": v(22.55, -38.05) * mm, "end": v(22.67, -38.04) * mm});
            skLineSegment(sketch, "E3219", {"start": v(22.67, -38.04) * mm, "end": v(22.78, -38.03) * mm});
            skLineSegment(sketch, "E3220", {"start": v(22.78, -38.03) * mm, "end": v(22.9, -38.02) * mm});
            skLineSegment(sketch, "E3221", {"start": v(22.9, -38.02) * mm, "end": v(23.01, -38) * mm});
            skLineSegment(sketch, "E3222", {"start": v(23.01, -38) * mm, "end": v(23.13, -38) * mm});
            skLineSegment(sketch, "E3223", {"start": v(23.13, -38) * mm, "end": v(23.24, -37.98) * mm});
            skLineSegment(sketch, "E3224", {"start": v(23.24, -37.98) * mm, "end": v(23.36, -37.97) * mm});
            skLineSegment(sketch, "E3225", {"start": v(23.36, -37.97) * mm, "end": v(23.47, -37.96) * mm});
            skLineSegment(sketch, "E3226", {"start": v(23.47, -37.96) * mm, "end": v(23.58, -37.94) * mm});
            skLineSegment(sketch, "E3227", {"start": v(23.58, -37.94) * mm, "end": v(23.7, -37.93) * mm});
            skLineSegment(sketch, "E3228", {"start": v(23.7, -37.93) * mm, "end": v(23.81, -37.92) * mm});
            skLineSegment(sketch, "E3229", {"start": v(23.81, -37.92) * mm, "end": v(23.93, -37.9) * mm});
            skLineSegment(sketch, "E3230", {"start": v(23.93, -37.9) * mm, "end": v(24.04, -37.88) * mm});
            skLineSegment(sketch, "E3231", {"start": v(24.04, -37.88) * mm, "end": v(24.15, -37.87) * mm});
            skLineSegment(sketch, "E3232", {"start": v(24.15, -37.87) * mm, "end": v(24.26, -37.85) * mm});
            skLineSegment(sketch, "E3233", {"start": v(24.26, -37.85) * mm, "end": v(24.38, -37.83) * mm});
            skLineSegment(sketch, "E3234", {"start": v(24.38, -37.83) * mm, "end": v(24.49, -37.81) * mm});
            skLineSegment(sketch, "E3235", {"start": v(24.49, -37.81) * mm, "end": v(24.6, -37.8) * mm});
            skLineSegment(sketch, "E3236", {"start": v(24.6, -37.8) * mm, "end": v(24.71, -37.77) * mm});
            skLineSegment(sketch, "E3237", {"start": v(24.71, -37.77) * mm, "end": v(24.82, -37.75) * mm});
            skLineSegment(sketch, "E3238", {"start": v(24.82, -37.75) * mm, "end": v(24.94, -37.73) * mm});
            skLineSegment(sketch, "E3239", {"start": v(24.94, -37.73) * mm, "end": v(25.05, -37.7) * mm});
            skLineSegment(sketch, "E3240", {"start": v(25.05, -37.7) * mm, "end": v(25.16, -37.68) * mm});
            skLineSegment(sketch, "E3241", {"start": v(25.16, -37.68) * mm, "end": v(25.27, -37.66) * mm});
            skLineSegment(sketch, "E3242", {"start": v(25.27, -37.66) * mm, "end": v(25.38, -37.63) * mm});
            skLineSegment(sketch, "E3243", {"start": v(25.38, -37.63) * mm, "end": v(25.5, -37.6) * mm});
            skLineSegment(sketch, "E3244", {"start": v(25.5, -37.6) * mm, "end": v(25.6, -37.58) * mm});
            skLineSegment(sketch, "E3245", {"start": v(25.6, -37.58) * mm, "end": v(25.72, -37.56) * mm});
            skLineSegment(sketch, "E3246", {"start": v(25.72, -37.56) * mm, "end": v(25.83, -37.53) * mm});
            skLineSegment(sketch, "E3247", {"start": v(25.83, -37.53) * mm, "end": v(25.94, -37.5) * mm});
            skLineSegment(sketch, "E3248", {"start": v(25.94, -37.5) * mm, "end": v(26.05, -37.47) * mm});
            skLineSegment(sketch, "E3249", {"start": v(26.05, -37.47) * mm, "end": v(26.16, -37.44) * mm});
            skLineSegment(sketch, "E3250", {"start": v(26.16, -37.44) * mm, "end": v(26.27, -37.41) * mm});
            skLineSegment(sketch, "E3251", {"start": v(26.27, -37.41) * mm, "end": v(26.38, -37.38) * mm});
            skLineSegment(sketch, "E3252", {"start": v(26.38, -37.38) * mm, "end": v(26.5, -37.35) * mm});
            skLineSegment(sketch, "E3253", {"start": v(26.5, -37.35) * mm, "end": v(26.6, -37.32) * mm});
            skLineSegment(sketch, "E3254", {"start": v(26.6, -37.32) * mm, "end": v(26.71, -37.28) * mm});
            skLineSegment(sketch, "E3255", {"start": v(26.71, -37.28) * mm, "end": v(26.82, -37.25) * mm});
            skLineSegment(sketch, "E3256", {"start": v(26.82, -37.25) * mm, "end": v(26.94, -37.22) * mm});
            skLineSegment(sketch, "E3257", {"start": v(26.94, -37.22) * mm, "end": v(27.05, -37.18) * mm});
            skLineSegment(sketch, "E3258", {"start": v(27.05, -37.18) * mm, "end": v(27.16, -37.14) * mm});
            skLineSegment(sketch, "E3259", {"start": v(27.16, -37.14) * mm, "end": v(27.27, -37.1) * mm});
            skLineSegment(sketch, "E3260", {"start": v(27.27, -37.1) * mm, "end": v(27.38, -37.07) * mm});
            skLineSegment(sketch, "E3261", {"start": v(27.38, -37.07) * mm, "end": v(27.5, -37.03) * mm});
            skLineSegment(sketch, "E3262", {"start": v(27.5, -37.03) * mm, "end": v(27.6, -37) * mm});
            skLineSegment(sketch, "E3263", {"start": v(27.6, -37) * mm, "end": v(27.71, -36.95) * mm});
            skLineSegment(sketch, "E3264", {"start": v(27.71, -36.95) * mm, "end": v(27.83, -36.9) * mm});
            skLineSegment(sketch, "E3265", {"start": v(27.83, -36.9) * mm, "end": v(27.94, -36.87) * mm});
            skLineSegment(sketch, "E3266", {"start": v(27.94, -36.87) * mm, "end": v(28.05, -36.83) * mm});
            skLineSegment(sketch, "E3267", {"start": v(28.05, -36.83) * mm, "end": v(28.16, -36.78) * mm});
            skLineSegment(sketch, "E3268", {"start": v(28.16, -36.78) * mm, "end": v(28.27, -36.74) * mm});
            skLineSegment(sketch, "E3269", {"start": v(28.27, -36.74) * mm, "end": v(28.39, -36.7) * mm});
            skLineSegment(sketch, "E3270", {"start": v(28.39, -36.7) * mm, "end": v(28.5, -36.65) * mm});
            skLineSegment(sketch, "E3271", {"start": v(28.5, -36.65) * mm, "end": v(28.61, -36.6) * mm});
            skLineSegment(sketch, "E3272", {"start": v(28.61, -36.6) * mm, "end": v(28.72, -36.55) * mm});
            skLineSegment(sketch, "E3273", {"start": v(28.72, -36.55) * mm, "end": v(28.84, -36.5) * mm});
            skLineSegment(sketch, "E3274", {"start": v(28.84, -36.5) * mm, "end": v(28.95, -36.46) * mm});
            skLineSegment(sketch, "E3275", {"start": v(28.95, -36.46) * mm, "end": v(29.06, -36.4) * mm});
            skLineSegment(sketch, "E3276", {"start": v(29.06, -36.4) * mm, "end": v(29.18, -36.36) * mm});
            skLineSegment(sketch, "E3277", {"start": v(29.18, -36.36) * mm, "end": v(29.3, -36.3) * mm});
            skLineSegment(sketch, "E3278", {"start": v(29.3, -36.3) * mm, "end": v(29.4, -36.25) * mm});
            skLineSegment(sketch, "E3279", {"start": v(29.4, -36.25) * mm, "end": v(29.52, -36.2) * mm});
            skLineSegment(sketch, "E3280", {"start": v(29.52, -36.2) * mm, "end": v(29.64, -36.14) * mm});
            skLineSegment(sketch, "E3281", {"start": v(29.64, -36.14) * mm, "end": v(29.75, -36.09) * mm});
            skLineSegment(sketch, "E3282", {"start": v(29.75, -36.09) * mm, "end": v(29.87, -36.03) * mm});
            skLineSegment(sketch, "E3283", {"start": v(29.87, -36.03) * mm, "end": v(29.98, -35.98) * mm});
            skLineSegment(sketch, "E3284", {"start": v(29.98, -35.98) * mm, "end": v(30.1, -35.92) * mm});
            skLineSegment(sketch, "E3285", {"start": v(30.1, -35.92) * mm, "end": v(30.21, -35.86) * mm});
            skLineSegment(sketch, "E3286", {"start": v(30.21, -35.86) * mm, "end": v(30.33, -35.8) * mm});
            skLineSegment(sketch, "E3287", {"start": v(30.33, -35.8) * mm, "end": v(30.45, -35.74) * mm});
            skLineSegment(sketch, "E3288", {"start": v(30.45, -35.74) * mm, "end": v(30.57, -35.68) * mm});
            skLineSegment(sketch, "E3289", {"start": v(30.57, -35.68) * mm, "end": v(30.68, -35.62) * mm});
            skLineSegment(sketch, "E3290", {"start": v(30.68, -35.62) * mm, "end": v(30.8, -35.55) * mm});
            skLineSegment(sketch, "E3291", {"start": v(30.8, -35.55) * mm, "end": v(30.92, -35.5) * mm});
            skLineSegment(sketch, "E3292", {"start": v(30.92, -35.5) * mm, "end": v(31.04, -35.43) * mm});
            skLineSegment(sketch, "E3293", {"start": v(31.04, -35.43) * mm, "end": v(31.16, -35.36) * mm});
            skLineSegment(sketch, "E3294", {"start": v(31.16, -35.36) * mm, "end": v(31.28, -35.3) * mm});
            skLineSegment(sketch, "E3295", {"start": v(31.28, -35.3) * mm, "end": v(31.4, -35.23) * mm});
            skLineSegment(sketch, "E3296", {"start": v(31.4, -35.23) * mm, "end": v(31.52, -35.16) * mm});
            skLineSegment(sketch, "E3297", {"start": v(31.52, -35.16) * mm, "end": v(31.64, -35.09) * mm});
            skLineSegment(sketch, "E3298", {"start": v(31.64, -35.09) * mm, "end": v(31.76, -35.02) * mm});
            skLineSegment(sketch, "E3299", {"start": v(31.76, -35.02) * mm, "end": v(31.88, -34.95) * mm});
            skLineSegment(sketch, "E3300", {"start": v(31.88, -34.95) * mm, "end": v(32, -34.88) * mm});
            skLineSegment(sketch, "E3301", {"start": v(32, -34.88) * mm, "end": v(32.13, -34.8) * mm});
            skLineSegment(sketch, "E3302", {"start": v(32.13, -34.8) * mm, "end": v(32.25, -34.73) * mm});
            skLineSegment(sketch, "E3303", {"start": v(32.25, -34.73) * mm, "end": v(32.38, -34.65) * mm});
            skLineSegment(sketch, "E3304", {"start": v(32.38, -34.65) * mm, "end": v(32.5, -34.58) * mm});
            skLineSegment(sketch, "E3305", {"start": v(32.5, -34.58) * mm, "end": v(32.62, -34.5) * mm});
            skLineSegment(sketch, "E3306", {"start": v(32.62, -34.5) * mm, "end": v(32.75, -34.42) * mm});
            skLineSegment(sketch, "E3307", {"start": v(32.75, -34.42) * mm, "end": v(32.88, -34.34) * mm});
            skLineSegment(sketch, "E3308", {"start": v(32.88, -34.34) * mm, "end": v(33, -34.26) * mm});
            skLineSegment(sketch, "E3309", {"start": v(33, -34.26) * mm, "end": v(33.13, -34.18) * mm});
            skLineSegment(sketch, "E3310", {"start": v(33.13, -34.18) * mm, "end": v(33.26, -34.1) * mm});
            skLineSegment(sketch, "E3311", {"start": v(33.26, -34.1) * mm, "end": v(33.38, -34.02) * mm});
            skLineSegment(sketch, "E3312", {"start": v(33.38, -34.02) * mm, "end": v(33.51, -33.94) * mm});
            skLineSegment(sketch, "E3313", {"start": v(33.51, -33.94) * mm, "end": v(33.64, -33.85) * mm});
            skLineSegment(sketch, "E3314", {"start": v(33.64, -33.85) * mm, "end": v(33.77, -33.77) * mm});
            skLineSegment(sketch, "E3315", {"start": v(33.77, -33.77) * mm, "end": v(33.9, -33.68) * mm});
            skLineSegment(sketch, "E3316", {"start": v(33.9, -33.68) * mm, "end": v(34.03, -33.6) * mm});
            skLineSegment(sketch, "E3317", {"start": v(34.03, -33.6) * mm, "end": v(34.17, -33.5) * mm});
            skLineSegment(sketch, "E3318", {"start": v(34.17, -33.5) * mm, "end": v(34.3, -33.41) * mm});
            skLineSegment(sketch, "E3319", {"start": v(34.3, -33.41) * mm, "end": v(34.43, -33.32) * mm});
            skLineSegment(sketch, "E3320", {"start": v(34.43, -33.32) * mm, "end": v(34.57, -33.23) * mm});
            skLineSegment(sketch, "E3321", {"start": v(34.57, -33.23) * mm, "end": v(34.7, -33.14) * mm});
            skLineSegment(sketch, "E3322", {"start": v(34.7, -33.14) * mm, "end": v(34.83, -33.04) * mm});
            skLineSegment(sketch, "E3323", {"start": v(34.83, -33.04) * mm, "end": v(34.97, -32.95) * mm});
            skLineSegment(sketch, "E3324", {"start": v(34.97, -32.95) * mm, "end": v(35.1, -32.85) * mm});
            skLineSegment(sketch, "E3325", {"start": v(35.1, -32.85) * mm, "end": v(35.24, -32.76) * mm});
            skLineSegment(sketch, "E3326", {"start": v(35.24, -32.76) * mm, "end": v(35.38, -32.66) * mm});
            skLineSegment(sketch, "E3327", {"start": v(35.38, -32.66) * mm, "end": v(35.52, -32.56) * mm});
            skLineSegment(sketch, "E3328", {"start": v(35.52, -32.56) * mm, "end": v(35.66, -32.46) * mm});
            skLineSegment(sketch, "E3329", {"start": v(35.66, -32.46) * mm, "end": v(35.8, -32.36) * mm});
            skLineSegment(sketch, "E3330", {"start": v(35.8, -32.36) * mm, "end": v(35.94, -32.26) * mm});
            skLineSegment(sketch, "E3331", {"start": v(35.94, -32.26) * mm, "end": v(36.12, -32.12) * mm});
            skLineSegment(sketch, "E3332", {"start": v(36.12, -32.12) * mm, "end": v(36.3, -32) * mm});
            skLineSegment(sketch, "E3333", {"start": v(36.3, -32) * mm, "end": v(36.48, -31.86) * mm});
            skLineSegment(sketch, "E3334", {"start": v(36.48, -31.86) * mm, "end": v(36.66, -31.73) * mm});
            skLineSegment(sketch, "E3335", {"start": v(36.66, -31.73) * mm, "end": v(36.84, -31.6) * mm});
            skLineSegment(sketch, "E3336", {"start": v(36.84, -31.6) * mm, "end": v(37.02, -31.46) * mm});
            skLineSegment(sketch, "E3337", {"start": v(37.02, -31.46) * mm, "end": v(37.2, -31.33) * mm});
            skLineSegment(sketch, "E3338", {"start": v(37.2, -31.33) * mm, "end": v(37.37, -31.2) * mm});
            skLineSegment(sketch, "E3339", {"start": v(37.37, -31.2) * mm, "end": v(37.55, -31.06) * mm});
            skLineSegment(sketch, "E3340", {"start": v(37.55, -31.06) * mm, "end": v(37.72, -30.92) * mm});
            skLineSegment(sketch, "E3341", {"start": v(37.72, -30.92) * mm, "end": v(37.9, -30.79) * mm});
            skLineSegment(sketch, "E3342", {"start": v(37.9, -30.79) * mm, "end": v(38.07, -30.65) * mm});
            skLineSegment(sketch, "E3343", {"start": v(38.07, -30.65) * mm, "end": v(38.24, -30.52) * mm});
            skLineSegment(sketch, "E3344", {"start": v(38.24, -30.52) * mm, "end": v(38.42, -30.38) * mm});
            skLineSegment(sketch, "E3345", {"start": v(38.42, -30.38) * mm, "end": v(38.59, -30.24) * mm});
            skLineSegment(sketch, "E3346", {"start": v(38.59, -30.24) * mm, "end": v(38.76, -30.1) * mm});
            skLineSegment(sketch, "E3347", {"start": v(38.76, -30.1) * mm, "end": v(38.93, -29.97) * mm});
            skLineSegment(sketch, "E3348", {"start": v(38.93, -29.97) * mm, "end": v(39.1, -29.84) * mm});
            skLineSegment(sketch, "E3349", {"start": v(39.1, -29.84) * mm, "end": v(39.27, -29.7) * mm});
            skLineSegment(sketch, "E3350", {"start": v(39.27, -29.7) * mm, "end": v(39.44, -29.56) * mm});
            skLineSegment(sketch, "E3351", {"start": v(39.44, -29.56) * mm, "end": v(39.6, -29.43) * mm});
            skLineSegment(sketch, "E3352", {"start": v(39.6, -29.43) * mm, "end": v(39.77, -29.3) * mm});
            skLineSegment(sketch, "E3353", {"start": v(39.77, -29.3) * mm, "end": v(39.94, -29.16) * mm});
            skLineSegment(sketch, "E3354", {"start": v(39.94, -29.16) * mm, "end": v(40.1, -29.02) * mm});
            skLineSegment(sketch, "E3355", {"start": v(40.1, -29.02) * mm, "end": v(40.26, -28.88) * mm});
            skLineSegment(sketch, "E3356", {"start": v(40.26, -28.88) * mm, "end": v(40.43, -28.75) * mm});
            skLineSegment(sketch, "E3357", {"start": v(40.43, -28.75) * mm, "end": v(40.6, -28.61) * mm});
            skLineSegment(sketch, "E3358", {"start": v(40.6, -28.61) * mm, "end": v(40.75, -28.48) * mm});
            skLineSegment(sketch, "E3359", {"start": v(40.75, -28.48) * mm, "end": v(40.91, -28.34) * mm});
            skLineSegment(sketch, "E3360", {"start": v(40.91, -28.34) * mm, "end": v(41.07, -28.2) * mm});
            skLineSegment(sketch, "E3361", {"start": v(41.07, -28.2) * mm, "end": v(41.23, -28.07) * mm});
            skLineSegment(sketch, "E3362", {"start": v(41.23, -28.07) * mm, "end": v(41.39, -27.94) * mm});
            skLineSegment(sketch, "E3363", {"start": v(41.39, -27.94) * mm, "end": v(41.55, -27.8) * mm});
            skLineSegment(sketch, "E3364", {"start": v(41.55, -27.8) * mm, "end": v(41.7, -27.67) * mm});
            skLineSegment(sketch, "E3365", {"start": v(41.7, -27.67) * mm, "end": v(41.86, -27.53) * mm});
            skLineSegment(sketch, "E3366", {"start": v(41.86, -27.53) * mm, "end": v(42.01, -27.4) * mm});
            skLineSegment(sketch, "E3367", {"start": v(42.01, -27.4) * mm, "end": v(42.16, -27.27) * mm});
            skLineSegment(sketch, "E3368", {"start": v(42.16, -27.27) * mm, "end": v(42.32, -27.13) * mm});
            skLineSegment(sketch, "E3369", {"start": v(42.32, -27.13) * mm, "end": v(42.47, -27) * mm});
            skLineSegment(sketch, "E3370", {"start": v(42.47, -27) * mm, "end": v(42.62, -26.87) * mm});
            skLineSegment(sketch, "E3371", {"start": v(42.62, -26.87) * mm, "end": v(42.77, -26.74) * mm});
            skLineSegment(sketch, "E3372", {"start": v(42.77, -26.74) * mm, "end": v(42.91, -26.6) * mm});
            skLineSegment(sketch, "E3373", {"start": v(42.91, -26.6) * mm, "end": v(43.06, -26.48) * mm});
            skLineSegment(sketch, "E3374", {"start": v(43.06, -26.48) * mm, "end": v(43.2, -26.35) * mm});
            skLineSegment(sketch, "E3375", {"start": v(43.2, -26.35) * mm, "end": v(43.35, -26.22) * mm});
            skLineSegment(sketch, "E3376", {"start": v(43.35, -26.22) * mm, "end": v(43.5, -26.09) * mm});
            skLineSegment(sketch, "E3377", {"start": v(43.5, -26.09) * mm, "end": v(43.63, -25.96) * mm});
            skLineSegment(sketch, "E3378", {"start": v(43.63, -25.96) * mm, "end": v(43.78, -25.83) * mm});
            skLineSegment(sketch, "E3379", {"start": v(43.78, -25.83) * mm, "end": v(43.91, -25.7) * mm});
            skLineSegment(sketch, "E3380", {"start": v(43.91, -25.7) * mm, "end": v(44.05, -25.58) * mm});
            skLineSegment(sketch, "E3381", {"start": v(44.05, -25.58) * mm, "end": v(44.2, -25.46) * mm});
            skLineSegment(sketch, "E3382", {"start": v(44.2, -25.46) * mm, "end": v(44.33, -25.33) * mm});
            skLineSegment(sketch, "E3383", {"start": v(44.33, -25.33) * mm, "end": v(44.46, -25.2) * mm});
            skLineSegment(sketch, "E3384", {"start": v(44.46, -25.2) * mm, "end": v(44.6, -25.08) * mm});
            skLineSegment(sketch, "E3385", {"start": v(44.6, -25.08) * mm, "end": v(44.73, -24.96) * mm});
            skLineSegment(sketch, "E3386", {"start": v(44.73, -24.96) * mm, "end": v(44.86, -24.84) * mm});
            skLineSegment(sketch, "E3387", {"start": v(44.86, -24.84) * mm, "end": v(44.99, -24.72) * mm});
            skLineSegment(sketch, "E3388", {"start": v(44.99, -24.72) * mm, "end": v(45.12, -24.6) * mm});
            skLineSegment(sketch, "E3389", {"start": v(45.12, -24.6) * mm, "end": v(45.24, -24.48) * mm});
            skLineSegment(sketch, "E3390", {"start": v(45.24, -24.48) * mm, "end": v(45.37, -24.36) * mm});
            skLineSegment(sketch, "E3391", {"start": v(45.37, -24.36) * mm, "end": v(45.5, -24.24) * mm});
            skLineSegment(sketch, "E3392", {"start": v(45.5, -24.24) * mm, "end": v(45.62, -24.13) * mm});
            skLineSegment(sketch, "E3393", {"start": v(45.62, -24.13) * mm, "end": v(45.74, -24.01) * mm});
            skLineSegment(sketch, "E3394", {"start": v(45.74, -24.01) * mm, "end": v(45.86, -23.9) * mm});
            skLineSegment(sketch, "E3395", {"start": v(45.86, -23.9) * mm, "end": v(45.98, -23.79) * mm});
            skLineSegment(sketch, "E3396", {"start": v(45.98, -23.79) * mm, "end": v(46.1, -23.67) * mm});
            skLineSegment(sketch, "E3397", {"start": v(46.1, -23.67) * mm, "end": v(46.21, -23.56) * mm});
            skLineSegment(sketch, "E3398", {"start": v(46.21, -23.56) * mm, "end": v(46.33, -23.45) * mm});
            skLineSegment(sketch, "E3399", {"start": v(46.33, -23.45) * mm, "end": v(46.44, -23.34) * mm});
            skLineSegment(sketch, "E3400", {"start": v(46.44, -23.34) * mm, "end": v(46.55, -23.24) * mm});
            skLineSegment(sketch, "E3401", {"start": v(46.55, -23.24) * mm, "end": v(46.66, -23.13) * mm});
            skLineSegment(sketch, "E3402", {"start": v(46.66, -23.13) * mm, "end": v(46.77, -23.02) * mm});
            skLineSegment(sketch, "E3403", {"start": v(46.77, -23.02) * mm, "end": v(46.88, -22.92) * mm});
            skLineSegment(sketch, "E3404", {"start": v(46.88, -22.92) * mm, "end": v(46.98, -22.82) * mm});
            skLineSegment(sketch, "E3405", {"start": v(46.98, -22.82) * mm, "end": v(47.08, -22.72) * mm});
            skLineSegment(sketch, "E3406", {"start": v(47.08, -22.72) * mm, "end": v(47.19, -22.62) * mm});
            skLineSegment(sketch, "E3407", {"start": v(47.19, -22.62) * mm, "end": v(47.29, -22.52) * mm});
            skLineSegment(sketch, "E3408", {"start": v(47.29, -22.52) * mm, "end": v(47.39, -22.42) * mm});
            skLineSegment(sketch, "E3409", {"start": v(47.39, -22.42) * mm, "end": v(47.48, -22.32) * mm});
            skLineSegment(sketch, "E3410", {"start": v(47.48, -22.32) * mm, "end": v(47.58, -22.23) * mm});
            skLineSegment(sketch, "E3411", {"start": v(47.58, -22.23) * mm, "end": v(47.67, -22.13) * mm});
            skLineSegment(sketch, "E3412", {"start": v(47.67, -22.13) * mm, "end": v(47.77, -22.04) * mm});
            skLineSegment(sketch, "E3413", {"start": v(47.77, -22.04) * mm, "end": v(47.86, -21.95) * mm});
            skLineSegment(sketch, "E3414", {"start": v(47.86, -21.95) * mm, "end": v(47.95, -21.86) * mm});
            skLineSegment(sketch, "E3415", {"start": v(47.95, -21.86) * mm, "end": v(48.03, -21.77) * mm});
            skLineSegment(sketch, "E3416", {"start": v(48.03, -21.77) * mm, "end": v(48.12, -21.69) * mm});
            skLineSegment(sketch, "E3417", {"start": v(48.12, -21.69) * mm, "end": v(48.2, -21.6) * mm});
            skLineSegment(sketch, "E3418", {"start": v(48.2, -21.6) * mm, "end": v(48.29, -21.52) * mm});
            skLineSegment(sketch, "E3419", {"start": v(48.29, -21.52) * mm, "end": v(48.37, -21.44) * mm});
            skLineSegment(sketch, "E3420", {"start": v(48.37, -21.44) * mm, "end": v(48.45, -21.36) * mm});
            skLineSegment(sketch, "E3421", {"start": v(48.45, -21.36) * mm, "end": v(48.52, -21.28) * mm});
            skLineSegment(sketch, "E3422", {"start": v(48.52, -21.28) * mm, "end": v(48.6, -21.2) * mm});
            skLineSegment(sketch, "E3423", {"start": v(48.6, -21.2) * mm, "end": v(48.67, -21.13) * mm});
            skLineSegment(sketch, "E3424", {"start": v(48.67, -21.13) * mm, "end": v(48.74, -21.05) * mm});
            skLineSegment(sketch, "E3425", {"start": v(48.74, -21.05) * mm, "end": v(48.81, -20.98) * mm});
            skLineSegment(sketch, "E3426", {"start": v(48.81, -20.98) * mm, "end": v(48.88, -20.91) * mm});
            skLineSegment(sketch, "E3427", {"start": v(48.88, -20.91) * mm, "end": v(48.95, -20.85) * mm});
            skLineSegment(sketch, "E3428", {"start": v(48.95, -20.85) * mm, "end": v(49.01, -20.78) * mm});
            skLineSegment(sketch, "E3429", {"start": v(49.01, -20.78) * mm, "end": v(49.07, -20.72) * mm});
            skLineSegment(sketch, "E3430", {"start": v(49.07, -20.72) * mm, "end": v(49.14, -20.65) * mm});
            skLineSegment(sketch, "E3431", {"start": v(49.14, -20.65) * mm, "end": v(49.2, -20.6) * mm});
            skLineSegment(sketch, "E3432", {"start": v(49.2, -20.6) * mm, "end": v(49.25, -20.53) * mm});
            skLineSegment(sketch, "E3433", {"start": v(49.25, -20.53) * mm, "end": v(49.3, -20.48) * mm});
            skLineSegment(sketch, "E3434", {"start": v(49.3, -20.48) * mm, "end": v(49.36, -20.42) * mm});
            skLineSegment(sketch, "E3435", {"start": v(49.36, -20.42) * mm, "end": v(49.4, -20.37) * mm});
            skLineSegment(sketch, "E3436", {"start": v(49.4, -20.37) * mm, "end": v(49.46, -20.32) * mm});
            skLineSegment(sketch, "E3437", {"start": v(49.46, -20.32) * mm, "end": v(49.5, -20.27) * mm});
            skLineSegment(sketch, "E3438", {"start": v(49.5, -20.27) * mm, "end": v(49.55, -20.22) * mm});
            skLineSegment(sketch, "E3439", {"start": v(49.55, -20.22) * mm, "end": v(49.6, -20.18) * mm});
            skLineSegment(sketch, "E3440", {"start": v(49.6, -20.18) * mm, "end": v(49.63, -20.13) * mm});
            skLineSegment(sketch, "E3441", {"start": v(49.63, -20.13) * mm, "end": v(49.67, -20.1) * mm});
            skLineSegment(sketch, "E3442", {"start": v(49.67, -20.1) * mm, "end": v(49.7, -20.06) * mm});
            skLineSegment(sketch, "E3443", {"start": v(49.7, -20.06) * mm, "end": v(49.74, -20.02) * mm});
            skLineSegment(sketch, "E3444", {"start": v(49.74, -20.02) * mm, "end": v(49.77, -19.98) * mm});
            skLineSegment(sketch, "E3445", {"start": v(49.77, -19.98) * mm, "end": v(49.8, -19.95) * mm});
            skLineSegment(sketch, "E3446", {"start": v(49.8, -19.95) * mm, "end": v(49.83, -19.92) * mm});
            skLineSegment(sketch, "E3447", {"start": v(49.83, -19.92) * mm, "end": v(49.86, -19.9) * mm});
            skLineSegment(sketch, "E3448", {"start": v(49.86, -19.9) * mm, "end": v(49.88, -19.87) * mm});
            skLineSegment(sketch, "E3449", {"start": v(49.88, -19.87) * mm, "end": v(49.9, -19.85) * mm});
            skLineSegment(sketch, "E3450", {"start": v(49.9, -19.85) * mm, "end": v(49.92, -19.83) * mm});
            skLineSegment(sketch, "E3451", {"start": v(49.92, -19.83) * mm, "end": v(49.94, -19.8) * mm});
            skLineSegment(sketch, "E3452", {"start": v(49.94, -19.8) * mm, "end": v(49.95, -19.8) * mm});
            skLineSegment(sketch, "E3453", {"start": v(49.95, -19.8) * mm, "end": v(49.97, -19.78) * mm});
            skLineSegment(sketch, "E3454", {"start": v(49.97, -19.78) * mm, "end": v(49.98, -19.77) * mm});
            skLineSegment(sketch, "E3455", {"start": v(49.98, -19.77) * mm, "end": v(49.98, -19.76) * mm});
            skLineSegment(sketch, "E3456", {"start": v(49.98, -19.76) * mm, "end": v(49.99, -19.75) * mm});
            skLineSegment(sketch, "E3457", {"start": v(49.99, -19.75) * mm, "end": v(50, -19.75) * mm});
            skLineSegment(sketch, "E3458", {"start": v(50, -19.75) * mm, "end": v(50, -19.75) * mm});
            skLineSegment(sketch, "E3459", {"start": v(50, -19.75) * mm, "end": v(49.94, -19.75) * mm});
            skLineSegment(sketch, "E3460", {"start": v(49.94, -19.75) * mm, "end": v(49.9, -19.75) * mm});
            skLineSegment(sketch, "E3461", {"start": v(49.9, -19.75) * mm, "end": v(49.84, -19.75) * mm});
            skLineSegment(sketch, "E3462", {"start": v(49.84, -19.75) * mm, "end": v(49.79, -19.75) * mm});
            skLineSegment(sketch, "E3463", {"start": v(49.79, -19.75) * mm, "end": v(49.74, -19.75) * mm});
            skLineSegment(sketch, "E3464", {"start": v(49.74, -19.75) * mm, "end": v(49.69, -19.75) * mm});
            skLineSegment(sketch, "E3465", {"start": v(49.69, -19.75) * mm, "end": v(49.64, -19.75) * mm});
            skLineSegment(sketch, "E3466", {"start": v(49.64, -19.75) * mm, "end": v(49.59, -19.75) * mm});
            skLineSegment(sketch, "E3467", {"start": v(49.59, -19.75) * mm, "end": v(49.53, -19.75) * mm});
            skLineSegment(sketch, "E3468", {"start": v(49.53, -19.75) * mm, "end": v(49.48, -19.75) * mm});
            skLineSegment(sketch, "E3469", {"start": v(49.48, -19.75) * mm, "end": v(49.43, -19.75) * mm});
            skLineSegment(sketch, "E3470", {"start": v(49.43, -19.75) * mm, "end": v(49.38, -19.75) * mm});
            skLineSegment(sketch, "E3471", {"start": v(49.38, -19.75) * mm, "end": v(49.33, -19.75) * mm});
            skLineSegment(sketch, "E3472", {"start": v(49.33, -19.75) * mm, "end": v(49.28, -19.75) * mm});
            skLineSegment(sketch, "E3473", {"start": v(49.28, -19.75) * mm, "end": v(49.23, -19.75) * mm});
            skLineSegment(sketch, "E3474", {"start": v(49.23, -19.75) * mm, "end": v(49.18, -19.75) * mm});
            skLineSegment(sketch, "E3475", {"start": v(49.18, -19.75) * mm, "end": v(49.13, -19.75) * mm});
            skLineSegment(sketch, "E3476", {"start": v(49.13, -19.75) * mm, "end": v(49.08, -19.75) * mm});
            skLineSegment(sketch, "E3477", {"start": v(49.08, -19.75) * mm, "end": v(49.02, -19.75) * mm});
            skLineSegment(sketch, "E3478", {"start": v(49.02, -19.75) * mm, "end": v(48.97, -19.75) * mm});
            skLineSegment(sketch, "E3479", {"start": v(48.97, -19.75) * mm, "end": v(48.92, -19.75) * mm});
            skLineSegment(sketch, "E3480", {"start": v(48.92, -19.75) * mm, "end": v(48.87, -19.75) * mm});
            skLineSegment(sketch, "E3481", {"start": v(48.87, -19.75) * mm, "end": v(48.82, -19.75) * mm});
            skLineSegment(sketch, "E3482", {"start": v(48.82, -19.75) * mm, "end": v(48.77, -19.75) * mm});
            skLineSegment(sketch, "E3483", {"start": v(48.77, -19.75) * mm, "end": v(48.72, -19.75) * mm});
            skLineSegment(sketch, "E3484", {"start": v(48.72, -19.75) * mm, "end": v(48.67, -19.75) * mm});
            skLineSegment(sketch, "E3485", {"start": v(48.67, -19.75) * mm, "end": v(48.62, -19.75) * mm});
            skLineSegment(sketch, "E3486", {"start": v(48.62, -19.75) * mm, "end": v(48.57, -19.75) * mm});
            skLineSegment(sketch, "E3487", {"start": v(48.57, -19.75) * mm, "end": v(48.51, -19.75) * mm});
            skLineSegment(sketch, "E3488", {"start": v(48.51, -19.75) * mm, "end": v(48.46, -19.75) * mm});
            skLineSegment(sketch, "E3489", {"start": v(48.46, -19.75) * mm, "end": v(48.41, -19.75) * mm});
            skLineSegment(sketch, "E3490", {"start": v(48.41, -19.75) * mm, "end": v(48.36, -19.75) * mm});
            skLineSegment(sketch, "E3491", {"start": v(48.36, -19.75) * mm, "end": v(48.31, -19.75) * mm});
            skLineSegment(sketch, "E3492", {"start": v(48.31, -19.75) * mm, "end": v(48.26, -19.75) * mm});
            skLineSegment(sketch, "E3493", {"start": v(48.26, -19.75) * mm, "end": v(48.2, -19.75) * mm});
            skLineSegment(sketch, "E3494", {"start": v(48.2, -19.75) * mm, "end": v(48.16, -19.75) * mm});
            skLineSegment(sketch, "E3495", {"start": v(48.16, -19.75) * mm, "end": v(48.1, -19.75) * mm});
            skLineSegment(sketch, "E3496", {"start": v(48.1, -19.75) * mm, "end": v(48.06, -19.75) * mm});
            skLineSegment(sketch, "E3497", {"start": v(48.06, -19.75) * mm, "end": v(48, -19.75) * mm});
            skLineSegment(sketch, "E3498", {"start": v(48, -19.75) * mm, "end": v(47.95, -19.75) * mm});
            skLineSegment(sketch, "E3499", {"start": v(47.95, -19.75) * mm, "end": v(47.9, -19.75) * mm});
            skLineSegment(sketch, "E3500", {"start": v(47.9, -19.75) * mm, "end": v(47.85, -19.75) * mm});
            skLineSegment(sketch, "E3501", {"start": v(47.85, -19.75) * mm, "end": v(47.8, -19.75) * mm});
            skLineSegment(sketch, "E3502", {"start": v(47.8, -19.75) * mm, "end": v(47.75, -19.75) * mm});
            skLineSegment(sketch, "E3503", {"start": v(47.75, -19.75) * mm, "end": v(47.7, -19.75) * mm});
            skLineSegment(sketch, "E3504", {"start": v(47.7, -19.75) * mm, "end": v(47.65, -19.75) * mm});
            skLineSegment(sketch, "E3505", {"start": v(47.65, -19.75) * mm, "end": v(47.6, -19.75) * mm});
            skLineSegment(sketch, "E3506", {"start": v(47.6, -19.75) * mm, "end": v(47.55, -19.75) * mm});
            skLineSegment(sketch, "E3507", {"start": v(47.55, -19.75) * mm, "end": v(47.5, -19.75) * mm});
            skLineSegment(sketch, "E3508", {"start": v(47.5, -19.75) * mm, "end": v(47.44, -19.75) * mm});
            skLineSegment(sketch, "E3509", {"start": v(47.44, -19.75) * mm, "end": v(47.4, -19.75) * mm});
            skLineSegment(sketch, "E3510", {"start": v(47.4, -19.75) * mm, "end": v(47.34, -19.75) * mm});
            skLineSegment(sketch, "E3511", {"start": v(47.34, -19.75) * mm, "end": v(47.3, -19.75) * mm});
            skLineSegment(sketch, "E3512", {"start": v(47.3, -19.75) * mm, "end": v(47.24, -19.75) * mm});
            skLineSegment(sketch, "E3513", {"start": v(47.24, -19.75) * mm, "end": v(47.19, -19.75) * mm});
            skLineSegment(sketch, "E3514", {"start": v(47.19, -19.75) * mm, "end": v(47.14, -19.75) * mm});
            skLineSegment(sketch, "E3515", {"start": v(47.14, -19.75) * mm, "end": v(47.09, -19.75) * mm});
            skLineSegment(sketch, "E3516", {"start": v(47.09, -19.75) * mm, "end": v(47.04, -19.75) * mm});
            skLineSegment(sketch, "E3517", {"start": v(47.04, -19.75) * mm, "end": v(46.98, -19.75) * mm});
            skLineSegment(sketch, "E3518", {"start": v(46.98, -19.75) * mm, "end": v(46.93, -19.75) * mm});
            skLineSegment(sketch, "E3519", {"start": v(46.93, -19.75) * mm, "end": v(46.88, -19.75) * mm});
            skLineSegment(sketch, "E3520", {"start": v(46.88, -19.75) * mm, "end": v(46.83, -19.75) * mm});
            skLineSegment(sketch, "E3521", {"start": v(46.83, -19.75) * mm, "end": v(46.78, -19.75) * mm});
            skLineSegment(sketch, "E3522", {"start": v(46.78, -19.75) * mm, "end": v(46.73, -19.75) * mm});
            skLineSegment(sketch, "E3523", {"start": v(46.73, -19.75) * mm, "end": v(46.68, -19.75) * mm});
            skLineSegment(sketch, "E3524", {"start": v(46.68, -19.75) * mm, "end": v(46.63, -19.75) * mm});
            skLineSegment(sketch, "E3525", {"start": v(46.63, -19.75) * mm, "end": v(46.58, -19.75) * mm});
            skLineSegment(sketch, "E3526", {"start": v(46.58, -19.75) * mm, "end": v(46.52, -19.75) * mm});
            skLineSegment(sketch, "E3527", {"start": v(46.52, -19.75) * mm, "end": v(46.47, -19.75) * mm});
            skLineSegment(sketch, "E3528", {"start": v(46.47, -19.75) * mm, "end": v(46.42, -19.75) * mm});
            skLineSegment(sketch, "E3529", {"start": v(46.42, -19.75) * mm, "end": v(46.37, -19.75) * mm});
            skLineSegment(sketch, "E3530", {"start": v(46.37, -19.75) * mm, "end": v(46.32, -19.75) * mm});
            skLineSegment(sketch, "E3531", {"start": v(46.32, -19.75) * mm, "end": v(46.27, -19.75) * mm});
            skLineSegment(sketch, "E3532", {"start": v(46.27, -19.75) * mm, "end": v(46.22, -19.75) * mm});
            skLineSegment(sketch, "E3533", {"start": v(46.22, -19.75) * mm, "end": v(46.17, -19.75) * mm});
            skLineSegment(sketch, "E3534", {"start": v(46.17, -19.75) * mm, "end": v(46.12, -19.75) * mm});
            skLineSegment(sketch, "E3535", {"start": v(46.12, -19.75) * mm, "end": v(46.07, -19.75) * mm});
            skLineSegment(sketch, "E3536", {"start": v(46.07, -19.75) * mm, "end": v(46.01, -19.75) * mm});
            skLineSegment(sketch, "E3537", {"start": v(46.01, -19.75) * mm, "end": v(45.96, -19.75) * mm});
            skLineSegment(sketch, "E3538", {"start": v(45.96, -19.75) * mm, "end": v(45.91, -19.75) * mm});
            skLineSegment(sketch, "E3539", {"start": v(45.91, -19.75) * mm, "end": v(45.86, -19.75) * mm});
            skLineSegment(sketch, "E3540", {"start": v(45.86, -19.75) * mm, "end": v(45.81, -19.75) * mm});
            skLineSegment(sketch, "E3541", {"start": v(45.81, -19.75) * mm, "end": v(45.76, -19.75) * mm});
            skLineSegment(sketch, "E3542", {"start": v(45.76, -19.75) * mm, "end": v(45.7, -19.75) * mm});
            skLineSegment(sketch, "E3543", {"start": v(45.7, -19.75) * mm, "end": v(45.66, -19.75) * mm});
            skLineSegment(sketch, "E3544", {"start": v(45.66, -19.75) * mm, "end": v(45.6, -19.75) * mm});
            skLineSegment(sketch, "E3545", {"start": v(45.6, -19.75) * mm, "end": v(45.56, -19.75) * mm});
            skLineSegment(sketch, "E3546", {"start": v(45.56, -19.75) * mm, "end": v(45.5, -19.75) * mm});
            skLineSegment(sketch, "E3547", {"start": v(45.5, -19.75) * mm, "end": v(45.45, -19.75) * mm});
            skLineSegment(sketch, "E3548", {"start": v(45.45, -19.75) * mm, "end": v(45.4, -19.75) * mm});
            skLineSegment(sketch, "E3549", {"start": v(45.4, -19.75) * mm, "end": v(45.35, -19.75) * mm});
            skLineSegment(sketch, "E3550", {"start": v(45.35, -19.75) * mm, "end": v(45.3, -19.75) * mm});
            skLineSegment(sketch, "E3551", {"start": v(45.3, -19.75) * mm, "end": v(45.25, -19.75) * mm});
            skLineSegment(sketch, "E3552", {"start": v(45.25, -19.75) * mm, "end": v(45.2, -19.75) * mm});
            skLineSegment(sketch, "E3553", {"start": v(45.2, -19.75) * mm, "end": v(45.15, -19.75) * mm});
            skLineSegment(sketch, "E3554", {"start": v(45.15, -19.75) * mm, "end": v(45.1, -19.75) * mm});
            skLineSegment(sketch, "E3555", {"start": v(45.1, -19.75) * mm, "end": v(45.05, -19.75) * mm});
            skLineSegment(sketch, "E3556", {"start": v(45.05, -19.75) * mm, "end": v(45, -19.75) * mm});
            skLineSegment(sketch, "E3557", {"start": v(45, -19.75) * mm, "end": v(44.94, -19.75) * mm});
            skLineSegment(sketch, "E3558", {"start": v(44.94, -19.75) * mm, "end": v(44.9, -19.75) * mm});
            skLineSegment(sketch, "E3559", {"start": v(44.9, -19.75) * mm, "end": v(44.84, -19.75) * mm});
            skLineSegment(sketch, "E3560", {"start": v(44.84, -19.75) * mm, "end": v(44.8, -19.75) * mm});
            skLineSegment(sketch, "E3561", {"start": v(44.8, -19.75) * mm, "end": v(44.74, -19.75) * mm});
            skLineSegment(sketch, "E3562", {"start": v(44.74, -19.75) * mm, "end": v(44.69, -19.75) * mm});
            skLineSegment(sketch, "E3563", {"start": v(44.69, -19.75) * mm, "end": v(44.64, -19.75) * mm});
            skLineSegment(sketch, "E3564", {"start": v(44.64, -19.75) * mm, "end": v(44.59, -19.75) * mm});
            skLineSegment(sketch, "E3565", {"start": v(44.59, -19.75) * mm, "end": v(44.54, -19.75) * mm});
            skLineSegment(sketch, "E3566", {"start": v(44.54, -19.75) * mm, "end": v(44.48, -19.75) * mm});
            skLineSegment(sketch, "E3567", {"start": v(44.48, -19.75) * mm, "end": v(44.43, -19.75) * mm});
            skLineSegment(sketch, "E3568", {"start": v(44.43, -19.75) * mm, "end": v(44.38, -19.75) * mm});
            skLineSegment(sketch, "E3569", {"start": v(44.38, -19.75) * mm, "end": v(44.33, -19.75) * mm});
            skLineSegment(sketch, "E3570", {"start": v(44.33, -19.75) * mm, "end": v(44.28, -19.75) * mm});
            skLineSegment(sketch, "E3571", {"start": v(44.28, -19.75) * mm, "end": v(44.23, -19.75) * mm});
            skLineSegment(sketch, "E3572", {"start": v(44.23, -19.75) * mm, "end": v(44.18, -19.75) * mm});
            skLineSegment(sketch, "E3573", {"start": v(44.18, -19.75) * mm, "end": v(44.13, -19.75) * mm});
            skLineSegment(sketch, "E3574", {"start": v(44.13, -19.75) * mm, "end": v(44.08, -19.75) * mm});
            skLineSegment(sketch, "E3575", {"start": v(44.08, -19.75) * mm, "end": v(44.03, -19.75) * mm});
            skLineSegment(sketch, "E3576", {"start": v(44.03, -19.75) * mm, "end": v(43.97, -19.75) * mm});
            skLineSegment(sketch, "E3577", {"start": v(43.97, -19.75) * mm, "end": v(43.92, -19.75) * mm});
            skLineSegment(sketch, "E3578", {"start": v(43.92, -19.75) * mm, "end": v(43.87, -19.75) * mm});
            skLineSegment(sketch, "E3579", {"start": v(43.87, -19.75) * mm, "end": v(43.82, -19.75) * mm});
            skLineSegment(sketch, "E3580", {"start": v(43.82, -19.75) * mm, "end": v(43.77, -19.75) * mm});
            skLineSegment(sketch, "E3581", {"start": v(43.77, -19.75) * mm, "end": v(43.72, -19.75) * mm});
            skLineSegment(sketch, "E3582", {"start": v(43.72, -19.75) * mm, "end": v(43.67, -19.75) * mm});
            skLineSegment(sketch, "E3583", {"start": v(43.67, -19.75) * mm, "end": v(43.62, -19.75) * mm});
            skLineSegment(sketch, "E3584", {"start": v(43.62, -19.75) * mm, "end": v(43.57, -19.75) * mm});
            skLineSegment(sketch, "E3585", {"start": v(43.57, -19.75) * mm, "end": v(43.52, -19.75) * mm});
            skLineSegment(sketch, "E3586", {"start": v(43.52, -19.75) * mm, "end": v(43.46, -19.75) * mm});
            skLineSegment(sketch, "E3587", {"start": v(43.46, -19.75) * mm, "end": v(43.46, -19.75) * mm});
            skLineSegment(sketch, "E3588", {"start": v(43.46, -19.75) * mm, "end": v(43.45, -19.76) * mm});
            skLineSegment(sketch, "E3589", {"start": v(43.45, -19.76) * mm, "end": v(43.43, -19.78) * mm});
            skLineSegment(sketch, "E3590", {"start": v(43.43, -19.78) * mm, "end": v(43.4, -19.8) * mm});
            skLineSegment(sketch, "E3591", {"start": v(43.4, -19.8) * mm, "end": v(43.37, -19.83) * mm});
            skLineSegment(sketch, "E3592", {"start": v(43.37, -19.83) * mm, "end": v(43.34, -19.86) * mm});
            skLineSegment(sketch, "E3593", {"start": v(43.34, -19.86) * mm, "end": v(43.3, -19.9) * mm});
            skLineSegment(sketch, "E3594", {"start": v(43.3, -19.9) * mm, "end": v(43.24, -19.94) * mm});
            skLineSegment(sketch, "E3595", {"start": v(43.24, -19.94) * mm, "end": v(43.18, -20) * mm});
            skLineSegment(sketch, "E3596", {"start": v(43.18, -20) * mm, "end": v(43.12, -20.05) * mm});
            skLineSegment(sketch, "E3597", {"start": v(43.12, -20.05) * mm, "end": v(43.05, -20.1) * mm});
            skLineSegment(sketch, "E3598", {"start": v(43.05, -20.1) * mm, "end": v(42.97, -20.17) * mm});
            skLineSegment(sketch, "E3599", {"start": v(42.97, -20.17) * mm, "end": v(42.89, -20.24) * mm});
            skLineSegment(sketch, "E3600", {"start": v(42.89, -20.24) * mm, "end": v(42.8, -20.32) * mm});
            skLineSegment(sketch, "E3601", {"start": v(42.8, -20.32) * mm, "end": v(42.7, -20.4) * mm});
            skLineSegment(sketch, "E3602", {"start": v(42.7, -20.4) * mm, "end": v(42.6, -20.48) * mm});
            skLineSegment(sketch, "E3603", {"start": v(42.6, -20.48) * mm, "end": v(42.5, -20.57) * mm});
            skLineSegment(sketch, "E3604", {"start": v(42.5, -20.57) * mm, "end": v(42.4, -20.66) * mm});
            skLineSegment(sketch, "E3605", {"start": v(42.4, -20.66) * mm, "end": v(42.28, -20.76) * mm});
            skLineSegment(sketch, "E3606", {"start": v(42.28, -20.76) * mm, "end": v(42.16, -20.86) * mm});
            skLineSegment(sketch, "E3607", {"start": v(42.16, -20.86) * mm, "end": v(42.04, -20.97) * mm});
            skLineSegment(sketch, "E3608", {"start": v(42.04, -20.97) * mm, "end": v(41.91, -21.07) * mm});
            skLineSegment(sketch, "E3609", {"start": v(41.91, -21.07) * mm, "end": v(41.78, -21.18) * mm});
            skLineSegment(sketch, "E3610", {"start": v(41.78, -21.18) * mm, "end": v(41.64, -21.3) * mm});
            skLineSegment(sketch, "E3611", {"start": v(41.64, -21.3) * mm, "end": v(41.5, -21.42) * mm});
            skLineSegment(sketch, "E3612", {"start": v(41.5, -21.42) * mm, "end": v(41.35, -21.54) * mm});
            skLineSegment(sketch, "E3613", {"start": v(41.35, -21.54) * mm, "end": v(41.2, -21.66) * mm});
            skLineSegment(sketch, "E3614", {"start": v(41.2, -21.66) * mm, "end": v(41.05, -21.8) * mm});
            skLineSegment(sketch, "E3615", {"start": v(41.05, -21.8) * mm, "end": v(40.9, -21.92) * mm});
            skLineSegment(sketch, "E3616", {"start": v(40.9, -21.92) * mm, "end": v(40.73, -22.05) * mm});
            skLineSegment(sketch, "E3617", {"start": v(40.73, -22.05) * mm, "end": v(40.56, -22.19) * mm});
            skLineSegment(sketch, "E3618", {"start": v(40.56, -22.19) * mm, "end": v(40.4, -22.33) * mm});
            skLineSegment(sketch, "E3619", {"start": v(40.4, -22.33) * mm, "end": v(40.22, -22.47) * mm});
            skLineSegment(sketch, "E3620", {"start": v(40.22, -22.47) * mm, "end": v(40.05, -22.6) * mm});
            skLineSegment(sketch, "E3621", {"start": v(40.05, -22.6) * mm, "end": v(39.87, -22.75) * mm});
            skLineSegment(sketch, "E3622", {"start": v(39.87, -22.75) * mm, "end": v(39.7, -22.9) * mm});
            skLineSegment(sketch, "E3623", {"start": v(39.7, -22.9) * mm, "end": v(39.5, -23.05) * mm});
            skLineSegment(sketch, "E3624", {"start": v(39.5, -23.05) * mm, "end": v(39.32, -23.2) * mm});
            skLineSegment(sketch, "E3625", {"start": v(39.32, -23.2) * mm, "end": v(39.14, -23.35) * mm});
            skLineSegment(sketch, "E3626", {"start": v(39.14, -23.35) * mm, "end": v(38.94, -23.5) * mm});
            skLineSegment(sketch, "E3627", {"start": v(38.94, -23.5) * mm, "end": v(38.75, -23.65) * mm});
            skLineSegment(sketch, "E3628", {"start": v(38.75, -23.65) * mm, "end": v(38.56, -23.8) * mm});
            skLineSegment(sketch, "E3629", {"start": v(38.56, -23.8) * mm, "end": v(38.36, -23.96) * mm});
            skLineSegment(sketch, "E3630", {"start": v(38.36, -23.96) * mm, "end": v(38.16, -24.11) * mm});
            skLineSegment(sketch, "E3631", {"start": v(38.16, -24.11) * mm, "end": v(37.96, -24.27) * mm});
            skLineSegment(sketch, "E3632", {"start": v(37.96, -24.27) * mm, "end": v(37.76, -24.43) * mm});
            skLineSegment(sketch, "E3633", {"start": v(37.76, -24.43) * mm, "end": v(37.56, -24.58) * mm});
            skLineSegment(sketch, "E3634", {"start": v(37.56, -24.58) * mm, "end": v(37.35, -24.74) * mm});
            skLineSegment(sketch, "E3635", {"start": v(37.35, -24.74) * mm, "end": v(37.15, -24.9) * mm});
            skLineSegment(sketch, "E3636", {"start": v(37.15, -24.9) * mm, "end": v(36.94, -25.06) * mm});
            skLineSegment(sketch, "E3637", {"start": v(36.94, -25.06) * mm, "end": v(36.73, -25.21) * mm});
            skLineSegment(sketch, "E3638", {"start": v(36.73, -25.21) * mm, "end": v(36.52, -25.37) * mm});
            skLineSegment(sketch, "E3639", {"start": v(36.52, -25.37) * mm, "end": v(36.31, -25.53) * mm});
            skLineSegment(sketch, "E3640", {"start": v(36.31, -25.53) * mm, "end": v(36.1, -25.68) * mm});
            skLineSegment(sketch, "E3641", {"start": v(36.1, -25.68) * mm, "end": v(35.9, -25.84) * mm});
            skLineSegment(sketch, "E3642", {"start": v(35.9, -25.84) * mm, "end": v(35.68, -26) * mm});
            skLineSegment(sketch, "E3643", {"start": v(35.68, -26) * mm, "end": v(35.47, -26.15) * mm});
            skLineSegment(sketch, "E3644", {"start": v(35.47, -26.15) * mm, "end": v(35.26, -26.3) * mm});
            skLineSegment(sketch, "E3645", {"start": v(35.26, -26.3) * mm, "end": v(35.05, -26.45) * mm});
            skLineSegment(sketch, "E3646", {"start": v(35.05, -26.45) * mm, "end": v(34.84, -26.6) * mm});
            skLineSegment(sketch, "E3647", {"start": v(34.84, -26.6) * mm, "end": v(34.63, -26.75) * mm});
            skLineSegment(sketch, "E3648", {"start": v(34.63, -26.75) * mm, "end": v(34.42, -26.9) * mm});
            skLineSegment(sketch, "E3649", {"start": v(34.42, -26.9) * mm, "end": v(34.2, -27.04) * mm});
            skLineSegment(sketch, "E3650", {"start": v(34.2, -27.04) * mm, "end": v(34, -27.18) * mm});
            skLineSegment(sketch, "E3651", {"start": v(34, -27.18) * mm, "end": v(33.8, -27.33) * mm});
            skLineSegment(sketch, "E3652", {"start": v(33.8, -27.33) * mm, "end": v(33.59, -27.46) * mm});
            skLineSegment(sketch, "E3653", {"start": v(33.59, -27.46) * mm, "end": v(33.38, -27.6) * mm});
            skLineSegment(sketch, "E3654", {"start": v(33.38, -27.6) * mm, "end": v(33.18, -27.74) * mm});
            skLineSegment(sketch, "E3655", {"start": v(33.18, -27.74) * mm, "end": v(32.97, -27.87) * mm});
            skLineSegment(sketch, "E3656", {"start": v(32.97, -27.87) * mm, "end": v(32.77, -28) * mm});
            skLineSegment(sketch, "E3657", {"start": v(32.77, -28) * mm, "end": v(32.57, -28.12) * mm});
            skLineSegment(sketch, "E3658", {"start": v(32.57, -28.12) * mm, "end": v(32.38, -28.25) * mm});
            skLineSegment(sketch, "E3659", {"start": v(32.38, -28.25) * mm, "end": v(32.18, -28.37) * mm});
            skLineSegment(sketch, "E3660", {"start": v(32.18, -28.37) * mm, "end": v(31.99, -28.49) * mm});
            skLineSegment(sketch, "E3661", {"start": v(31.99, -28.49) * mm, "end": v(31.8, -28.6) * mm});
            skLineSegment(sketch, "E3662", {"start": v(31.8, -28.6) * mm, "end": v(31.6, -28.71) * mm});
            skLineSegment(sketch, "E3663", {"start": v(31.6, -28.71) * mm, "end": v(31.42, -28.82) * mm});
            skLineSegment(sketch, "E3664", {"start": v(31.42, -28.82) * mm, "end": v(31.23, -28.92) * mm});
            skLineSegment(sketch, "E3665", {"start": v(31.23, -28.92) * mm, "end": v(31.05, -29.02) * mm});
            skLineSegment(sketch, "E3666", {"start": v(31.05, -29.02) * mm, "end": v(30.87, -29.12) * mm});
            skLineSegment(sketch, "E3667", {"start": v(30.87, -29.12) * mm, "end": v(30.7, -29.2) * mm});
            skLineSegment(sketch, "E3668", {"start": v(30.7, -29.2) * mm, "end": v(30.52, -29.3) * mm});
            skLineSegment(sketch, "E3669", {"start": v(30.52, -29.3) * mm, "end": v(30.35, -29.38) * mm});
            skLineSegment(sketch, "E3670", {"start": v(30.35, -29.38) * mm, "end": v(30.19, -29.46) * mm});
            skLineSegment(sketch, "E3671", {"start": v(30.19, -29.46) * mm, "end": v(30.02, -29.53) * mm});
            skLineSegment(sketch, "E3672", {"start": v(30.02, -29.53) * mm, "end": v(29.86, -29.6) * mm});
            skLineSegment(sketch, "E3673", {"start": v(29.86, -29.6) * mm, "end": v(29.7, -29.66) * mm});
            skLineSegment(sketch, "E3674", {"start": v(29.7, -29.66) * mm, "end": v(29.55, -29.72) * mm});
            skLineSegment(sketch, "E3675", {"start": v(29.55, -29.72) * mm, "end": v(29.4, -29.78) * mm});
            skLineSegment(sketch, "E3676", {"start": v(29.4, -29.78) * mm, "end": v(29.26, -29.82) * mm});
            skLineSegment(sketch, "E3677", {"start": v(29.26, -29.82) * mm, "end": v(29.12, -29.87) * mm});
            skLineSegment(sketch, "E3678", {"start": v(29.12, -29.87) * mm, "end": v(28.99, -29.9) * mm});
            skLineSegment(sketch, "E3679", {"start": v(28.99, -29.9) * mm, "end": v(28.86, -29.94) * mm});
            skLineSegment(sketch, "E3680", {"start": v(28.86, -29.94) * mm, "end": v(28.73, -29.96) * mm});
            skLineSegment(sketch, "E3681", {"start": v(28.73, -29.96) * mm, "end": v(28.6, -29.98) * mm});
            skLineSegment(sketch, "E3682", {"start": v(28.6, -29.98) * mm, "end": v(28.49, -30) * mm});
            skLineSegment(sketch, "E3683", {"start": v(28.49, -30) * mm, "end": v(28.38, -30) * mm});
            skLineSegment(sketch, "E3684", {"start": v(28.38, -30) * mm, "end": v(28.27, -30) * mm});
            skLineSegment(sketch, "E3685", {"start": v(28.27, -30) * mm, "end": v(28.17, -30) * mm});
            skLineSegment(sketch, "E3686", {"start": v(28.17, -30) * mm, "end": v(28.07, -29.99) * mm});
            skLineSegment(sketch, "E3687", {"start": v(28.07, -29.99) * mm, "end": v(27.98, -29.97) * mm});
            skLineSegment(sketch, "E3688", {"start": v(27.98, -29.97) * mm, "end": v(27.9, -29.94) * mm});
            skLineSegment(sketch, "E3689", {"start": v(27.9, -29.94) * mm, "end": v(27.82, -29.91) * mm});
            skLineSegment(sketch, "E3690", {"start": v(27.82, -29.91) * mm, "end": v(27.74, -29.87) * mm});
            skLineSegment(sketch, "E3691", {"start": v(27.74, -29.87) * mm, "end": v(27.68, -29.83) * mm});
            skLineSegment(sketch, "E3692", {"start": v(27.68, -29.83) * mm, "end": v(27.62, -29.77) * mm});
            skLineSegment(sketch, "E3693", {"start": v(27.62, -29.77) * mm, "end": v(27.56, -29.71) * mm});
            skLineSegment(sketch, "E3694", {"start": v(27.56, -29.71) * mm, "end": v(27.51, -29.64) * mm});
            skLineSegment(sketch, "E3695", {"start": v(27.51, -29.64) * mm, "end": v(27.47, -29.56) * mm});
            skLineSegment(sketch, "E3696", {"start": v(27.47, -29.56) * mm, "end": v(27.43, -29.48) * mm});
            skLineSegment(sketch, "E3697", {"start": v(27.43, -29.48) * mm, "end": v(27.4, -29.39) * mm});
            skLineSegment(sketch, "E3698", {"start": v(27.4, -29.39) * mm, "end": v(27.38, -29.28) * mm});
            skLineSegment(sketch, "E3699", {"start": v(27.38, -29.28) * mm, "end": v(27.37, -29.17) * mm});
            skLineSegment(sketch, "E3700", {"start": v(27.37, -29.17) * mm, "end": v(27.36, -29.06) * mm});
            skLineSegment(sketch, "E3701", {"start": v(27.36, -29.06) * mm, "end": v(27.36, -28.93) * mm});
            skLineSegment(sketch, "E3702", {"start": v(27.36, -28.93) * mm, "end": v(27.37, -28.8) * mm});
            skLineSegment(sketch, "E3703", {"start": v(27.37, -28.8) * mm, "end": v(27.38, -28.65) * mm});
            skLineSegment(sketch, "E3704", {"start": v(27.38, -28.65) * mm, "end": v(27.4, -28.5) * mm});
            skLineSegment(sketch, "E3705", {"start": v(27.4, -28.5) * mm, "end": v(27.43, -28.33) * mm});
            skLineSegment(sketch, "E3706", {"start": v(27.43, -28.33) * mm, "end": v(27.47, -28.16) * mm});
            skLineSegment(sketch, "E3707", {"start": v(27.47, -28.16) * mm, "end": v(27.52, -27.98) * mm});
            skLineSegment(sketch, "E3708", {"start": v(27.52, -27.98) * mm, "end": v(27.57, -27.8) * mm});
            skLineSegment(sketch, "E3709", {"start": v(27.57, -27.8) * mm, "end": v(27.63, -27.6) * mm});
            skLineSegment(sketch, "E3710", {"start": v(27.63, -27.6) * mm, "end": v(27.7, -27.38) * mm});
            skLineSegment(sketch, "E3711", {"start": v(27.7, -27.38) * mm, "end": v(27.78, -27.16) * mm});
            skLineSegment(sketch, "E3712", {"start": v(27.78, -27.16) * mm, "end": v(27.87, -26.93) * mm});
            skLineSegment(sketch, "E3713", {"start": v(27.87, -26.93) * mm, "end": v(27.97, -26.7) * mm});
            skLineSegment(sketch, "E3714", {"start": v(27.97, -26.7) * mm, "end": v(28.08, -26.44) * mm});
            skSolve(sketch);
        }
        {
            var Q0;
            Q0=makeQuery(id+"F0.imprint","IMPRINT",FACE,{"disambiguationData":[TD([[makeQuery(id+"F0.imprint","IMPRINT",EDGE,{"derivedFrom":sQuery(id+"F0.wireOp",EDGE,"E0")}),1.0]])]});
            extrude(context, id + "F1", {"entities" : qUnion([Q0]), "depth" : 25.4 * mm, "offsetDistance" : 25.4 * mm});
        }
    });
